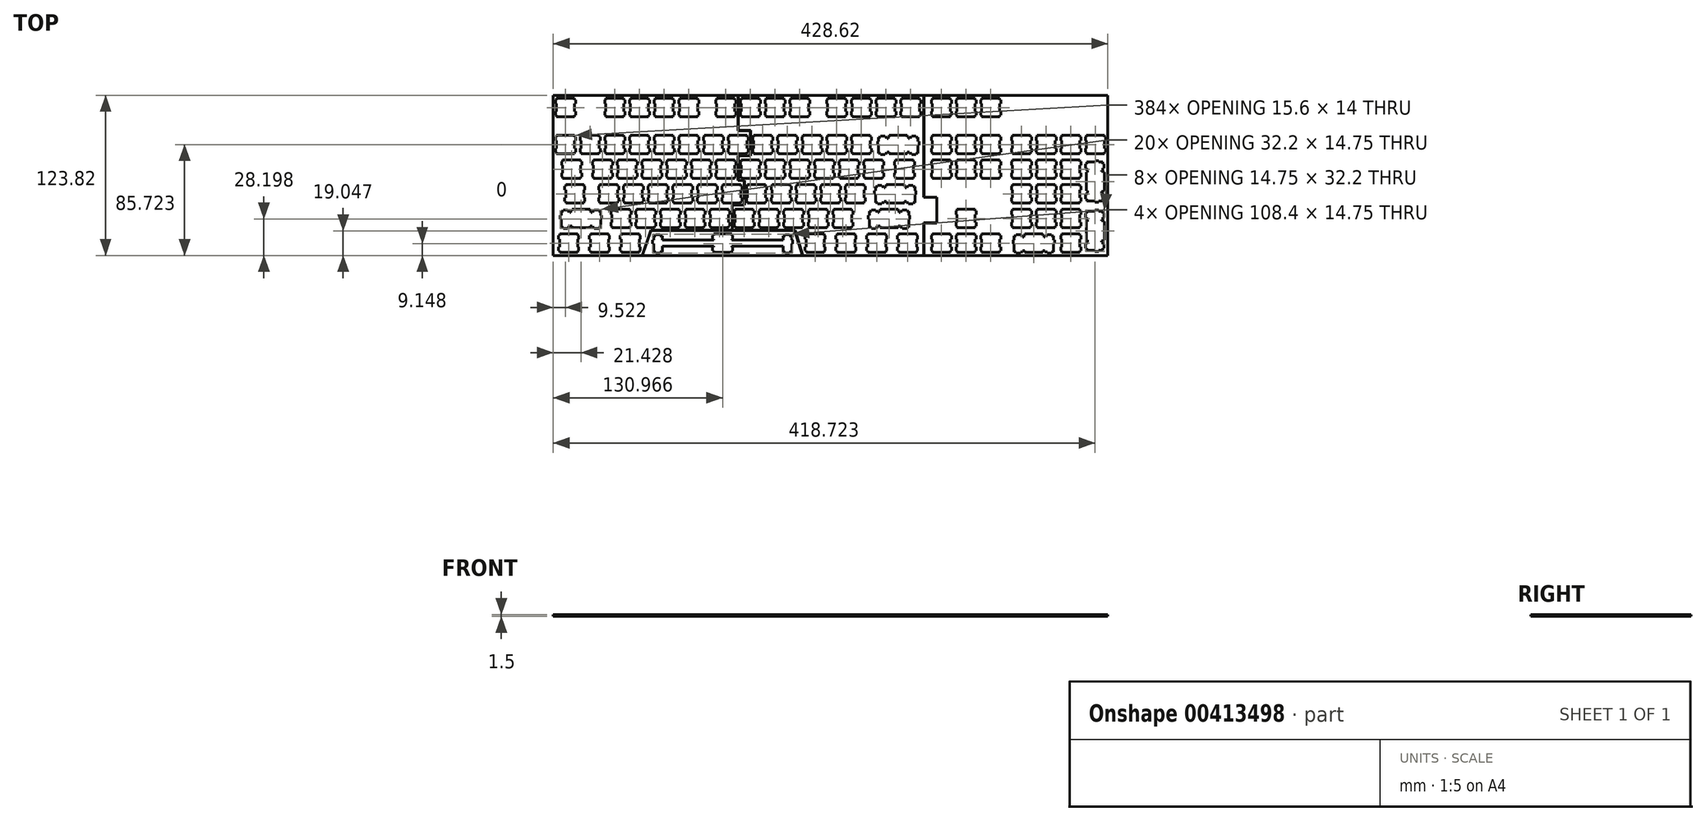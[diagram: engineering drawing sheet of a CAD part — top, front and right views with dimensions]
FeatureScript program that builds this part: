
annotation { "Feature Type Name" : "Feature", "Feature Type Description" : "" }
export const myFeature = defineFeature(function(context is Context, id is Id, definition is map)
    precondition{}
    {
        {
            var Q0;
            Q0=qCreatedBy(makeId("Top.planeOp"),FACE);
            var sketch = newSketch(context, id + "F0", { "sketchPlane" : qUnion([Q0])});
            skLineSegment(sketch, "E0", {"start": v(-214.31, 61.91) * mm, "end": v(214.31, 61.91) * mm});
            skLineSegment(sketch, "E1", {"start": v(214.31, 61.91) * mm, "end": v(214.31, -61.91) * mm});
            skLineSegment(sketch, "E2", {"start": v(214.31, -61.91) * mm, "end": v(-214.31, -61.91) * mm});
            skLineSegment(sketch, "E3", {"start": v(-214.31, -61.91) * mm, "end": v(-214.31, 61.91) * mm});
            skLineSegment(sketch, "E4", {"start": v(-197.79, 46.39) * mm, "end": v(-197.79, 45.39) * mm});
            skLineSegment(sketch, "E5", {"start": v(-197.79, 45.39) * mm, "end": v(-211.79, 45.39) * mm});
            skLineSegment(sketch, "E6", {"start": v(-211.79, 45.39) * mm, "end": v(-211.79, 46.39) * mm});
            skLineSegment(sketch, "E7", {"start": v(-211.79, 46.39) * mm, "end": v(-212.59, 46.39) * mm});
            skLineSegment(sketch, "E8", {"start": v(-212.59, 46.39) * mm, "end": v(-212.59, 49.49) * mm});
            skLineSegment(sketch, "E9", {"start": v(-212.59, 49.49) * mm, "end": v(-211.79, 49.49) * mm});
            skLineSegment(sketch, "E10", {"start": v(-211.79, 49.49) * mm, "end": v(-211.79, 55.29) * mm});
            skLineSegment(sketch, "E11", {"start": v(-211.79, 55.29) * mm, "end": v(-212.59, 55.29) * mm});
            skLineSegment(sketch, "E12", {"start": v(-212.59, 55.29) * mm, "end": v(-212.59, 58.39) * mm});
            skLineSegment(sketch, "E13", {"start": v(-212.59, 58.39) * mm, "end": v(-211.79, 58.39) * mm});
            skLineSegment(sketch, "E14", {"start": v(-211.79, 58.39) * mm, "end": v(-211.79, 59.39) * mm});
            skLineSegment(sketch, "E15", {"start": v(-211.79, 59.39) * mm, "end": v(-197.79, 59.39) * mm});
            skLineSegment(sketch, "E16", {"start": v(-197.79, 59.39) * mm, "end": v(-197.79, 58.39) * mm});
            skLineSegment(sketch, "E17", {"start": v(-197.79, 58.39) * mm, "end": v(-196.99, 58.39) * mm});
            skLineSegment(sketch, "E18", {"start": v(-196.99, 58.39) * mm, "end": v(-196.99, 55.29) * mm});
            skLineSegment(sketch, "E19", {"start": v(-196.99, 55.29) * mm, "end": v(-197.79, 55.29) * mm});
            skLineSegment(sketch, "E20", {"start": v(-197.79, 55.29) * mm, "end": v(-197.79, 49.49) * mm});
            skLineSegment(sketch, "E21", {"start": v(-197.79, 49.49) * mm, "end": v(-196.99, 49.49) * mm});
            skLineSegment(sketch, "E22", {"start": v(-196.99, 49.49) * mm, "end": v(-196.99, 46.39) * mm});
            skLineSegment(sketch, "E23", {"start": v(-196.99, 46.39) * mm, "end": v(-197.79, 46.39) * mm});
            skLineSegment(sketch, "E24", {"start": v(-197.79, 17.81) * mm, "end": v(-197.79, 16.81) * mm});
            skLineSegment(sketch, "E25", {"start": v(-197.79, 16.81) * mm, "end": v(-211.79, 16.81) * mm});
            skLineSegment(sketch, "E26", {"start": v(-211.79, 16.81) * mm, "end": v(-211.79, 17.81) * mm});
            skLineSegment(sketch, "E27", {"start": v(-211.79, 17.81) * mm, "end": v(-212.59, 17.81) * mm});
            skLineSegment(sketch, "E28", {"start": v(-212.59, 17.81) * mm, "end": v(-212.59, 20.91) * mm});
            skLineSegment(sketch, "E29", {"start": v(-212.59, 20.91) * mm, "end": v(-211.79, 20.91) * mm});
            skLineSegment(sketch, "E30", {"start": v(-211.79, 20.91) * mm, "end": v(-211.79, 26.71) * mm});
            skLineSegment(sketch, "E31", {"start": v(-211.79, 26.71) * mm, "end": v(-212.59, 26.71) * mm});
            skLineSegment(sketch, "E32", {"start": v(-212.59, 26.71) * mm, "end": v(-212.59, 29.81) * mm});
            skLineSegment(sketch, "E33", {"start": v(-212.59, 29.81) * mm, "end": v(-211.79, 29.81) * mm});
            skLineSegment(sketch, "E34", {"start": v(-211.79, 29.81) * mm, "end": v(-211.79, 30.81) * mm});
            skLineSegment(sketch, "E35", {"start": v(-211.79, 30.81) * mm, "end": v(-197.79, 30.81) * mm});
            skLineSegment(sketch, "E36", {"start": v(-197.79, 30.81) * mm, "end": v(-197.79, 29.81) * mm});
            skLineSegment(sketch, "E37", {"start": v(-197.79, 29.81) * mm, "end": v(-196.99, 29.81) * mm});
            skLineSegment(sketch, "E38", {"start": v(-196.99, 29.81) * mm, "end": v(-196.99, 26.71) * mm});
            skLineSegment(sketch, "E39", {"start": v(-196.99, 26.71) * mm, "end": v(-197.79, 26.71) * mm});
            skLineSegment(sketch, "E40", {"start": v(-197.79, 26.71) * mm, "end": v(-197.79, 20.91) * mm});
            skLineSegment(sketch, "E41", {"start": v(-197.79, 20.91) * mm, "end": v(-196.99, 20.91) * mm});
            skLineSegment(sketch, "E42", {"start": v(-196.99, 20.91) * mm, "end": v(-196.99, 17.81) * mm});
            skLineSegment(sketch, "E43", {"start": v(-196.99, 17.81) * mm, "end": v(-197.79, 17.81) * mm});
            skLineSegment(sketch, "E44", {"start": v(-195.4, -58.39) * mm, "end": v(-195.4, -59.39) * mm});
            skLineSegment(sketch, "E45", {"start": v(-195.4, -59.39) * mm, "end": v(-209.4, -59.39) * mm});
            skLineSegment(sketch, "E46", {"start": v(-209.4, -59.39) * mm, "end": v(-209.4, -58.39) * mm});
            skLineSegment(sketch, "E47", {"start": v(-209.4, -58.39) * mm, "end": v(-210.2, -58.39) * mm});
            skLineSegment(sketch, "E48", {"start": v(-210.2, -58.39) * mm, "end": v(-210.2, -55.29) * mm});
            skLineSegment(sketch, "E49", {"start": v(-210.2, -55.29) * mm, "end": v(-209.4, -55.29) * mm});
            skLineSegment(sketch, "E50", {"start": v(-209.4, -55.29) * mm, "end": v(-209.4, -49.49) * mm});
            skLineSegment(sketch, "E51", {"start": v(-209.4, -49.49) * mm, "end": v(-210.2, -49.49) * mm});
            skLineSegment(sketch, "E52", {"start": v(-210.2, -49.49) * mm, "end": v(-210.2, -46.39) * mm});
            skLineSegment(sketch, "E53", {"start": v(-210.2, -46.39) * mm, "end": v(-209.4, -46.39) * mm});
            skLineSegment(sketch, "E54", {"start": v(-209.4, -46.39) * mm, "end": v(-209.4, -45.39) * mm});
            skLineSegment(sketch, "E55", {"start": v(-209.4, -45.39) * mm, "end": v(-195.4, -45.39) * mm});
            skLineSegment(sketch, "E56", {"start": v(-195.4, -45.39) * mm, "end": v(-195.4, -46.39) * mm});
            skLineSegment(sketch, "E57", {"start": v(-195.4, -46.39) * mm, "end": v(-194.6, -46.39) * mm});
            skLineSegment(sketch, "E58", {"start": v(-194.6, -46.39) * mm, "end": v(-194.6, -49.49) * mm});
            skLineSegment(sketch, "E59", {"start": v(-194.6, -49.49) * mm, "end": v(-195.4, -49.49) * mm});
            skLineSegment(sketch, "E60", {"start": v(-195.4, -49.49) * mm, "end": v(-195.4, -55.29) * mm});
            skLineSegment(sketch, "E61", {"start": v(-195.4, -55.29) * mm, "end": v(-194.6, -55.29) * mm});
            skLineSegment(sketch, "E62", {"start": v(-194.6, -55.29) * mm, "end": v(-194.6, -58.39) * mm});
            skLineSegment(sketch, "E63", {"start": v(-194.6, -58.39) * mm, "end": v(-195.4, -58.39) * mm});
            skLineSegment(sketch, "E64", {"start": v(-193.03, -1.24) * mm, "end": v(-193.03, -2.24) * mm});
            skLineSegment(sketch, "E65", {"start": v(-193.03, -2.24) * mm, "end": v(-207.02, -2.24) * mm});
            skLineSegment(sketch, "E66", {"start": v(-207.02, -2.24) * mm, "end": v(-207.02, -1.24) * mm});
            skLineSegment(sketch, "E67", {"start": v(-207.02, -1.24) * mm, "end": v(-207.83, -1.24) * mm});
            skLineSegment(sketch, "E68", {"start": v(-207.83, -1.24) * mm, "end": v(-207.83, 1.86) * mm});
            skLineSegment(sketch, "E69", {"start": v(-207.83, 1.86) * mm, "end": v(-207.02, 1.86) * mm});
            skLineSegment(sketch, "E70", {"start": v(-207.02, 1.86) * mm, "end": v(-207.02, 7.66) * mm});
            skLineSegment(sketch, "E71", {"start": v(-207.02, 7.66) * mm, "end": v(-207.83, 7.66) * mm});
            skLineSegment(sketch, "E72", {"start": v(-207.83, 7.66) * mm, "end": v(-207.83, 10.76) * mm});
            skLineSegment(sketch, "E73", {"start": v(-207.83, 10.76) * mm, "end": v(-207.02, 10.76) * mm});
            skLineSegment(sketch, "E74", {"start": v(-207.02, 10.76) * mm, "end": v(-207.02, 11.76) * mm});
            skLineSegment(sketch, "E75", {"start": v(-207.02, 11.76) * mm, "end": v(-193.03, 11.76) * mm});
            skLineSegment(sketch, "E76", {"start": v(-193.03, 11.76) * mm, "end": v(-193.03, 10.76) * mm});
            skLineSegment(sketch, "E77", {"start": v(-193.03, 10.76) * mm, "end": v(-192.22, 10.76) * mm});
            skLineSegment(sketch, "E78", {"start": v(-192.22, 10.76) * mm, "end": v(-192.22, 7.66) * mm});
            skLineSegment(sketch, "E79", {"start": v(-192.22, 7.66) * mm, "end": v(-193.03, 7.66) * mm});
            skLineSegment(sketch, "E80", {"start": v(-193.03, 7.66) * mm, "end": v(-193.03, 1.86) * mm});
            skLineSegment(sketch, "E81", {"start": v(-193.03, 1.86) * mm, "end": v(-192.22, 1.86) * mm});
            skLineSegment(sketch, "E82", {"start": v(-192.22, 1.86) * mm, "end": v(-192.22, -1.24) * mm});
            skLineSegment(sketch, "E83", {"start": v(-192.22, -1.24) * mm, "end": v(-193.03, -1.24) * mm});
            skLineSegment(sketch, "E84", {"start": v(-190.64, -20.29) * mm, "end": v(-190.64, -21.29) * mm});
            skLineSegment(sketch, "E85", {"start": v(-190.64, -21.29) * mm, "end": v(-204.64, -21.29) * mm});
            skLineSegment(sketch, "E86", {"start": v(-204.64, -21.29) * mm, "end": v(-204.64, -20.29) * mm});
            skLineSegment(sketch, "E87", {"start": v(-204.64, -20.29) * mm, "end": v(-205.44, -20.29) * mm});
            skLineSegment(sketch, "E88", {"start": v(-205.44, -20.29) * mm, "end": v(-205.44, -17.19) * mm});
            skLineSegment(sketch, "E89", {"start": v(-205.44, -17.19) * mm, "end": v(-204.64, -17.19) * mm});
            skLineSegment(sketch, "E90", {"start": v(-204.64, -17.19) * mm, "end": v(-204.64, -11.39) * mm});
            skLineSegment(sketch, "E91", {"start": v(-204.64, -11.39) * mm, "end": v(-205.44, -11.39) * mm});
            skLineSegment(sketch, "E92", {"start": v(-205.44, -11.39) * mm, "end": v(-205.44, -8.29) * mm});
            skLineSegment(sketch, "E93", {"start": v(-205.44, -8.29) * mm, "end": v(-204.64, -8.29) * mm});
            skLineSegment(sketch, "E94", {"start": v(-204.64, -8.29) * mm, "end": v(-204.64, -7.29) * mm});
            skLineSegment(sketch, "E95", {"start": v(-204.64, -7.29) * mm, "end": v(-190.64, -7.29) * mm});
            skLineSegment(sketch, "E96", {"start": v(-190.64, -7.29) * mm, "end": v(-190.64, -8.29) * mm});
            skLineSegment(sketch, "E97", {"start": v(-190.64, -8.29) * mm, "end": v(-189.84, -8.29) * mm});
            skLineSegment(sketch, "E98", {"start": v(-189.84, -8.29) * mm, "end": v(-189.84, -11.39) * mm});
            skLineSegment(sketch, "E99", {"start": v(-189.84, -11.39) * mm, "end": v(-190.64, -11.39) * mm});
            skLineSegment(sketch, "E100", {"start": v(-190.64, -11.39) * mm, "end": v(-190.64, -17.19) * mm});
            skLineSegment(sketch, "E101", {"start": v(-190.64, -17.19) * mm, "end": v(-189.84, -17.19) * mm});
            skLineSegment(sketch, "E102", {"start": v(-189.84, -17.19) * mm, "end": v(-189.84, -20.29) * mm});
            skLineSegment(sketch, "E103", {"start": v(-189.84, -20.29) * mm, "end": v(-190.64, -20.29) * mm});
            skLineSegment(sketch, "E104", {"start": v(-178.74, 17.81) * mm, "end": v(-178.74, 16.81) * mm});
            skLineSegment(sketch, "E105", {"start": v(-178.74, 16.81) * mm, "end": v(-192.74, 16.81) * mm});
            skLineSegment(sketch, "E106", {"start": v(-192.74, 16.81) * mm, "end": v(-192.74, 17.81) * mm});
            skLineSegment(sketch, "E107", {"start": v(-192.74, 17.81) * mm, "end": v(-193.54, 17.81) * mm});
            skLineSegment(sketch, "E108", {"start": v(-193.54, 17.81) * mm, "end": v(-193.54, 20.91) * mm});
            skLineSegment(sketch, "E109", {"start": v(-193.54, 20.91) * mm, "end": v(-192.74, 20.91) * mm});
            skLineSegment(sketch, "E110", {"start": v(-192.74, 20.91) * mm, "end": v(-192.74, 26.71) * mm});
            skLineSegment(sketch, "E111", {"start": v(-192.74, 26.71) * mm, "end": v(-193.54, 26.71) * mm});
            skLineSegment(sketch, "E112", {"start": v(-193.54, 26.71) * mm, "end": v(-193.54, 29.81) * mm});
            skLineSegment(sketch, "E113", {"start": v(-193.54, 29.81) * mm, "end": v(-192.74, 29.81) * mm});
            skLineSegment(sketch, "E114", {"start": v(-192.74, 29.81) * mm, "end": v(-192.74, 30.81) * mm});
            skLineSegment(sketch, "E115", {"start": v(-192.74, 30.81) * mm, "end": v(-178.74, 30.81) * mm});
            skLineSegment(sketch, "E116", {"start": v(-178.74, 30.81) * mm, "end": v(-178.74, 29.81) * mm});
            skLineSegment(sketch, "E117", {"start": v(-178.74, 29.81) * mm, "end": v(-177.94, 29.81) * mm});
            skLineSegment(sketch, "E118", {"start": v(-177.94, 29.81) * mm, "end": v(-177.94, 26.71) * mm});
            skLineSegment(sketch, "E119", {"start": v(-177.94, 26.71) * mm, "end": v(-178.74, 26.71) * mm});
            skLineSegment(sketch, "E120", {"start": v(-178.74, 26.71) * mm, "end": v(-178.74, 20.91) * mm});
            skLineSegment(sketch, "E121", {"start": v(-178.74, 20.91) * mm, "end": v(-177.94, 20.91) * mm});
            skLineSegment(sketch, "E122", {"start": v(-177.94, 20.91) * mm, "end": v(-177.94, 17.81) * mm});
            skLineSegment(sketch, "E123", {"start": v(-177.94, 17.81) * mm, "end": v(-178.74, 17.81) * mm});
            skLineSegment(sketch, "E124", {"start": v(-177.66, -33.84) * mm, "end": v(-177.66, -40.1) * mm});
            skLineSegment(sketch, "E125", {"start": v(-177.66, -40.1) * mm, "end": v(-179.28, -40.1) * mm});
            skLineSegment(sketch, "E126", {"start": v(-179.28, -40.1) * mm, "end": v(-179.28, -41.09) * mm});
            skLineSegment(sketch, "E127", {"start": v(-179.28, -41.09) * mm, "end": v(-182.58, -41.09) * mm});
            skLineSegment(sketch, "E128", {"start": v(-182.58, -41.09) * mm, "end": v(-182.58, -40.1) * mm});
            skLineSegment(sketch, "E129", {"start": v(-182.58, -40.1) * mm, "end": v(-184.3, -40.1) * mm});
            skLineSegment(sketch, "E130", {"start": v(-184.3, -40.1) * mm, "end": v(-184.3, -39.3) * mm});
            skLineSegment(sketch, "E131", {"start": v(-184.3, -39.3) * mm, "end": v(-185.08, -39.3) * mm});
            skLineSegment(sketch, "E132", {"start": v(-185.08, -39.3) * mm, "end": v(-185.08, -39.34) * mm});
            skLineSegment(sketch, "E133", {"start": v(-185.08, -39.34) * mm, "end": v(-185.88, -39.34) * mm});
            skLineSegment(sketch, "E134", {"start": v(-185.88, -39.34) * mm, "end": v(-185.88, -40.34) * mm});
            skLineSegment(sketch, "E135", {"start": v(-185.88, -40.34) * mm, "end": v(-199.88, -40.34) * mm});
            skLineSegment(sketch, "E136", {"start": v(-199.88, -40.34) * mm, "end": v(-199.88, -39.34) * mm});
            skLineSegment(sketch, "E137", {"start": v(-199.88, -39.34) * mm, "end": v(-200.68, -39.34) * mm});
            skLineSegment(sketch, "E138", {"start": v(-200.68, -39.34) * mm, "end": v(-200.68, -39.3) * mm});
            skLineSegment(sketch, "E139", {"start": v(-200.68, -39.3) * mm, "end": v(-201.46, -39.3) * mm});
            skLineSegment(sketch, "E140", {"start": v(-201.46, -39.3) * mm, "end": v(-201.46, -40.1) * mm});
            skLineSegment(sketch, "E141", {"start": v(-201.46, -40.1) * mm, "end": v(-203.18, -40.1) * mm});
            skLineSegment(sketch, "E142", {"start": v(-203.18, -40.1) * mm, "end": v(-203.18, -41.09) * mm});
            skLineSegment(sketch, "E143", {"start": v(-203.18, -41.09) * mm, "end": v(-206.48, -41.09) * mm});
            skLineSegment(sketch, "E144", {"start": v(-206.48, -41.09) * mm, "end": v(-206.48, -40.1) * mm});
            skLineSegment(sketch, "E145", {"start": v(-206.48, -40.1) * mm, "end": v(-208.1, -40.1) * mm});
            skLineSegment(sketch, "E146", {"start": v(-208.1, -40.1) * mm, "end": v(-208.1, -33.84) * mm});
            skLineSegment(sketch, "E147", {"start": v(-208.1, -33.84) * mm, "end": v(-208.98, -33.84) * mm});
            skLineSegment(sketch, "E148", {"start": v(-208.98, -33.84) * mm, "end": v(-208.98, -31.04) * mm});
            skLineSegment(sketch, "E149", {"start": v(-208.98, -31.04) * mm, "end": v(-208.1, -31.04) * mm});
            skLineSegment(sketch, "E150", {"start": v(-208.1, -31.04) * mm, "end": v(-208.1, -27.8) * mm});
            skLineSegment(sketch, "E151", {"start": v(-208.1, -27.8) * mm, "end": v(-206.48, -27.8) * mm});
            skLineSegment(sketch, "E152", {"start": v(-206.48, -27.8) * mm, "end": v(-206.48, -26.89) * mm});
            skLineSegment(sketch, "E153", {"start": v(-206.48, -26.89) * mm, "end": v(-203.18, -26.89) * mm});
            skLineSegment(sketch, "E154", {"start": v(-203.18, -26.89) * mm, "end": v(-203.18, -27.8) * mm});
            skLineSegment(sketch, "E155", {"start": v(-203.18, -27.8) * mm, "end": v(-201.46, -27.8) * mm});
            skLineSegment(sketch, "E156", {"start": v(-201.46, -27.8) * mm, "end": v(-201.46, -28.6) * mm});
            skLineSegment(sketch, "E157", {"start": v(-201.46, -28.6) * mm, "end": v(-200.68, -28.6) * mm});
            skLineSegment(sketch, "E158", {"start": v(-200.68, -28.6) * mm, "end": v(-200.68, -27.34) * mm});
            skLineSegment(sketch, "E159", {"start": v(-200.68, -27.34) * mm, "end": v(-199.88, -27.34) * mm});
            skLineSegment(sketch, "E160", {"start": v(-199.88, -27.34) * mm, "end": v(-199.88, -26.34) * mm});
            skLineSegment(sketch, "E161", {"start": v(-199.88, -26.34) * mm, "end": v(-185.88, -26.34) * mm});
            skLineSegment(sketch, "E162", {"start": v(-185.88, -26.34) * mm, "end": v(-185.88, -27.34) * mm});
            skLineSegment(sketch, "E163", {"start": v(-185.88, -27.34) * mm, "end": v(-185.08, -27.34) * mm});
            skLineSegment(sketch, "E164", {"start": v(-185.08, -27.34) * mm, "end": v(-185.08, -28.6) * mm});
            skLineSegment(sketch, "E165", {"start": v(-185.08, -28.6) * mm, "end": v(-184.3, -28.6) * mm});
            skLineSegment(sketch, "E166", {"start": v(-184.3, -28.6) * mm, "end": v(-184.3, -27.8) * mm});
            skLineSegment(sketch, "E167", {"start": v(-184.3, -27.8) * mm, "end": v(-182.58, -27.8) * mm});
            skLineSegment(sketch, "E168", {"start": v(-182.58, -27.8) * mm, "end": v(-182.58, -26.89) * mm});
            skLineSegment(sketch, "E169", {"start": v(-182.58, -26.89) * mm, "end": v(-179.28, -26.89) * mm});
            skLineSegment(sketch, "E170", {"start": v(-179.28, -26.89) * mm, "end": v(-179.28, -27.8) * mm});
            skLineSegment(sketch, "E171", {"start": v(-179.28, -27.8) * mm, "end": v(-177.66, -27.8) * mm});
            skLineSegment(sketch, "E172", {"start": v(-177.66, -27.8) * mm, "end": v(-177.66, -31.04) * mm});
            skLineSegment(sketch, "E173", {"start": v(-177.66, -31.04) * mm, "end": v(-176.78, -31.04) * mm});
            skLineSegment(sketch, "E174", {"start": v(-176.78, -31.04) * mm, "end": v(-176.78, -33.84) * mm});
            skLineSegment(sketch, "E175", {"start": v(-176.78, -33.84) * mm, "end": v(-177.66, -33.84) * mm});
            skLineSegment(sketch, "E176", {"start": v(-171.6, -58.39) * mm, "end": v(-171.6, -59.39) * mm});
            skLineSegment(sketch, "E177", {"start": v(-171.6, -59.39) * mm, "end": v(-185.6, -59.39) * mm});
            skLineSegment(sketch, "E178", {"start": v(-185.6, -59.39) * mm, "end": v(-185.6, -58.39) * mm});
            skLineSegment(sketch, "E179", {"start": v(-185.6, -58.39) * mm, "end": v(-186.4, -58.39) * mm});
            skLineSegment(sketch, "E180", {"start": v(-186.4, -58.39) * mm, "end": v(-186.4, -55.29) * mm});
            skLineSegment(sketch, "E181", {"start": v(-186.4, -55.29) * mm, "end": v(-185.6, -55.29) * mm});
            skLineSegment(sketch, "E182", {"start": v(-185.6, -55.29) * mm, "end": v(-185.6, -49.49) * mm});
            skLineSegment(sketch, "E183", {"start": v(-185.6, -49.49) * mm, "end": v(-186.4, -49.49) * mm});
            skLineSegment(sketch, "E184", {"start": v(-186.4, -49.49) * mm, "end": v(-186.4, -46.39) * mm});
            skLineSegment(sketch, "E185", {"start": v(-186.4, -46.39) * mm, "end": v(-185.6, -46.39) * mm});
            skLineSegment(sketch, "E186", {"start": v(-185.6, -46.39) * mm, "end": v(-185.6, -45.39) * mm});
            skLineSegment(sketch, "E187", {"start": v(-185.6, -45.39) * mm, "end": v(-171.6, -45.39) * mm});
            skLineSegment(sketch, "E188", {"start": v(-171.6, -45.39) * mm, "end": v(-171.6, -46.39) * mm});
            skLineSegment(sketch, "E189", {"start": v(-171.6, -46.39) * mm, "end": v(-170.8, -46.39) * mm});
            skLineSegment(sketch, "E190", {"start": v(-170.8, -46.39) * mm, "end": v(-170.8, -49.49) * mm});
            skLineSegment(sketch, "E191", {"start": v(-170.8, -49.49) * mm, "end": v(-171.6, -49.49) * mm});
            skLineSegment(sketch, "E192", {"start": v(-171.6, -49.49) * mm, "end": v(-171.6, -55.29) * mm});
            skLineSegment(sketch, "E193", {"start": v(-171.6, -55.29) * mm, "end": v(-170.8, -55.29) * mm});
            skLineSegment(sketch, "E194", {"start": v(-170.8, -55.29) * mm, "end": v(-170.8, -58.39) * mm});
            skLineSegment(sketch, "E195", {"start": v(-170.8, -58.39) * mm, "end": v(-171.6, -58.39) * mm});
            skLineSegment(sketch, "E196", {"start": v(-169.21, -1.24) * mm, "end": v(-169.21, -2.24) * mm});
            skLineSegment(sketch, "E197", {"start": v(-169.21, -2.24) * mm, "end": v(-183.21, -2.24) * mm});
            skLineSegment(sketch, "E198", {"start": v(-183.21, -2.24) * mm, "end": v(-183.21, -1.24) * mm});
            skLineSegment(sketch, "E199", {"start": v(-183.21, -1.24) * mm, "end": v(-184.01, -1.24) * mm});
            skLineSegment(sketch, "E200", {"start": v(-184.01, -1.24) * mm, "end": v(-184.01, 1.86) * mm});
            skLineSegment(sketch, "E201", {"start": v(-184.01, 1.86) * mm, "end": v(-183.21, 1.86) * mm});
            skLineSegment(sketch, "E202", {"start": v(-183.21, 1.86) * mm, "end": v(-183.21, 7.66) * mm});
            skLineSegment(sketch, "E203", {"start": v(-183.21, 7.66) * mm, "end": v(-184.01, 7.66) * mm});
            skLineSegment(sketch, "E204", {"start": v(-184.01, 7.66) * mm, "end": v(-184.01, 10.76) * mm});
            skLineSegment(sketch, "E205", {"start": v(-184.01, 10.76) * mm, "end": v(-183.21, 10.76) * mm});
            skLineSegment(sketch, "E206", {"start": v(-183.21, 10.76) * mm, "end": v(-183.21, 11.76) * mm});
            skLineSegment(sketch, "E207", {"start": v(-183.21, 11.76) * mm, "end": v(-169.21, 11.76) * mm});
            skLineSegment(sketch, "E208", {"start": v(-169.21, 11.76) * mm, "end": v(-169.21, 10.76) * mm});
            skLineSegment(sketch, "E209", {"start": v(-169.21, 10.76) * mm, "end": v(-168.41, 10.76) * mm});
            skLineSegment(sketch, "E210", {"start": v(-168.41, 10.76) * mm, "end": v(-168.41, 7.66) * mm});
            skLineSegment(sketch, "E211", {"start": v(-168.41, 7.66) * mm, "end": v(-169.21, 7.66) * mm});
            skLineSegment(sketch, "E212", {"start": v(-169.21, 7.66) * mm, "end": v(-169.21, 1.86) * mm});
            skLineSegment(sketch, "E213", {"start": v(-169.21, 1.86) * mm, "end": v(-168.41, 1.86) * mm});
            skLineSegment(sketch, "E214", {"start": v(-168.41, 1.86) * mm, "end": v(-168.41, -1.24) * mm});
            skLineSegment(sketch, "E215", {"start": v(-168.41, -1.24) * mm, "end": v(-169.21, -1.24) * mm});
            skLineSegment(sketch, "E216", {"start": v(-164.45, -20.29) * mm, "end": v(-164.45, -21.29) * mm});
            skLineSegment(sketch, "E217", {"start": v(-164.45, -21.29) * mm, "end": v(-178.45, -21.29) * mm});
            skLineSegment(sketch, "E218", {"start": v(-178.45, -21.29) * mm, "end": v(-178.45, -20.29) * mm});
            skLineSegment(sketch, "E219", {"start": v(-178.45, -20.29) * mm, "end": v(-179.25, -20.29) * mm});
            skLineSegment(sketch, "E220", {"start": v(-179.25, -20.29) * mm, "end": v(-179.25, -17.19) * mm});
            skLineSegment(sketch, "E221", {"start": v(-179.25, -17.19) * mm, "end": v(-178.45, -17.19) * mm});
            skLineSegment(sketch, "E222", {"start": v(-178.45, -17.19) * mm, "end": v(-178.45, -11.39) * mm});
            skLineSegment(sketch, "E223", {"start": v(-178.45, -11.39) * mm, "end": v(-179.25, -11.39) * mm});
            skLineSegment(sketch, "E224", {"start": v(-179.25, -11.39) * mm, "end": v(-179.25, -8.29) * mm});
            skLineSegment(sketch, "E225", {"start": v(-179.25, -8.29) * mm, "end": v(-178.45, -8.29) * mm});
            skLineSegment(sketch, "E226", {"start": v(-178.45, -8.29) * mm, "end": v(-178.45, -7.29) * mm});
            skLineSegment(sketch, "E227", {"start": v(-178.45, -7.29) * mm, "end": v(-164.45, -7.29) * mm});
            skLineSegment(sketch, "E228", {"start": v(-164.45, -7.29) * mm, "end": v(-164.45, -8.29) * mm});
            skLineSegment(sketch, "E229", {"start": v(-164.45, -8.29) * mm, "end": v(-163.65, -8.29) * mm});
            skLineSegment(sketch, "E230", {"start": v(-163.65, -8.29) * mm, "end": v(-163.65, -11.39) * mm});
            skLineSegment(sketch, "E231", {"start": v(-163.65, -11.39) * mm, "end": v(-164.45, -11.39) * mm});
            skLineSegment(sketch, "E232", {"start": v(-164.45, -11.39) * mm, "end": v(-164.45, -17.19) * mm});
            skLineSegment(sketch, "E233", {"start": v(-164.45, -17.19) * mm, "end": v(-163.65, -17.19) * mm});
            skLineSegment(sketch, "E234", {"start": v(-163.65, -17.19) * mm, "end": v(-163.65, -20.29) * mm});
            skLineSegment(sketch, "E235", {"start": v(-163.65, -20.29) * mm, "end": v(-164.45, -20.29) * mm});
            skLineSegment(sketch, "E236", {"start": v(-159.69, 46.39) * mm, "end": v(-159.69, 45.39) * mm});
            skLineSegment(sketch, "E237", {"start": v(-159.69, 45.39) * mm, "end": v(-173.69, 45.39) * mm});
            skLineSegment(sketch, "E238", {"start": v(-173.69, 45.39) * mm, "end": v(-173.69, 46.39) * mm});
            skLineSegment(sketch, "E239", {"start": v(-173.69, 46.39) * mm, "end": v(-174.49, 46.39) * mm});
            skLineSegment(sketch, "E240", {"start": v(-174.49, 46.39) * mm, "end": v(-174.49, 49.49) * mm});
            skLineSegment(sketch, "E241", {"start": v(-174.49, 49.49) * mm, "end": v(-173.69, 49.49) * mm});
            skLineSegment(sketch, "E242", {"start": v(-173.69, 49.49) * mm, "end": v(-173.69, 55.29) * mm});
            skLineSegment(sketch, "E243", {"start": v(-173.69, 55.29) * mm, "end": v(-174.49, 55.29) * mm});
            skLineSegment(sketch, "E244", {"start": v(-174.49, 55.29) * mm, "end": v(-174.49, 58.39) * mm});
            skLineSegment(sketch, "E245", {"start": v(-174.49, 58.39) * mm, "end": v(-173.69, 58.39) * mm});
            skLineSegment(sketch, "E246", {"start": v(-173.69, 58.39) * mm, "end": v(-173.69, 59.39) * mm});
            skLineSegment(sketch, "E247", {"start": v(-173.69, 59.39) * mm, "end": v(-159.69, 59.39) * mm});
            skLineSegment(sketch, "E248", {"start": v(-159.69, 59.39) * mm, "end": v(-159.69, 58.39) * mm});
            skLineSegment(sketch, "E249", {"start": v(-159.69, 58.39) * mm, "end": v(-158.89, 58.39) * mm});
            skLineSegment(sketch, "E250", {"start": v(-158.89, 58.39) * mm, "end": v(-158.89, 55.29) * mm});
            skLineSegment(sketch, "E251", {"start": v(-158.89, 55.29) * mm, "end": v(-159.69, 55.29) * mm});
            skLineSegment(sketch, "E252", {"start": v(-159.69, 55.29) * mm, "end": v(-159.69, 49.49) * mm});
            skLineSegment(sketch, "E253", {"start": v(-159.69, 49.49) * mm, "end": v(-158.89, 49.49) * mm});
            skLineSegment(sketch, "E254", {"start": v(-158.89, 49.49) * mm, "end": v(-158.89, 46.39) * mm});
            skLineSegment(sketch, "E255", {"start": v(-158.89, 46.39) * mm, "end": v(-159.69, 46.39) * mm});
            skLineSegment(sketch, "E256", {"start": v(-159.69, 17.81) * mm, "end": v(-159.69, 16.81) * mm});
            skLineSegment(sketch, "E257", {"start": v(-159.69, 16.81) * mm, "end": v(-173.69, 16.81) * mm});
            skLineSegment(sketch, "E258", {"start": v(-173.69, 16.81) * mm, "end": v(-173.69, 17.81) * mm});
            skLineSegment(sketch, "E259", {"start": v(-173.69, 17.81) * mm, "end": v(-174.49, 17.81) * mm});
            skLineSegment(sketch, "E260", {"start": v(-174.49, 17.81) * mm, "end": v(-174.49, 20.91) * mm});
            skLineSegment(sketch, "E261", {"start": v(-174.49, 20.91) * mm, "end": v(-173.69, 20.91) * mm});
            skLineSegment(sketch, "E262", {"start": v(-173.69, 20.91) * mm, "end": v(-173.69, 26.71) * mm});
            skLineSegment(sketch, "E263", {"start": v(-173.69, 26.71) * mm, "end": v(-174.49, 26.71) * mm});
            skLineSegment(sketch, "E264", {"start": v(-174.49, 26.71) * mm, "end": v(-174.49, 29.81) * mm});
            skLineSegment(sketch, "E265", {"start": v(-174.49, 29.81) * mm, "end": v(-173.69, 29.81) * mm});
            skLineSegment(sketch, "E266", {"start": v(-173.69, 29.81) * mm, "end": v(-173.69, 30.81) * mm});
            skLineSegment(sketch, "E267", {"start": v(-173.69, 30.81) * mm, "end": v(-159.69, 30.81) * mm});
            skLineSegment(sketch, "E268", {"start": v(-159.69, 30.81) * mm, "end": v(-159.69, 29.81) * mm});
            skLineSegment(sketch, "E269", {"start": v(-159.69, 29.81) * mm, "end": v(-158.89, 29.81) * mm});
            skLineSegment(sketch, "E270", {"start": v(-158.89, 29.81) * mm, "end": v(-158.89, 26.71) * mm});
            skLineSegment(sketch, "E271", {"start": v(-158.89, 26.71) * mm, "end": v(-159.69, 26.71) * mm});
            skLineSegment(sketch, "E272", {"start": v(-159.69, 26.71) * mm, "end": v(-159.69, 20.91) * mm});
            skLineSegment(sketch, "E273", {"start": v(-159.69, 20.91) * mm, "end": v(-158.89, 20.91) * mm});
            skLineSegment(sketch, "E274", {"start": v(-158.89, 20.91) * mm, "end": v(-158.89, 17.81) * mm});
            skLineSegment(sketch, "E275", {"start": v(-158.89, 17.81) * mm, "end": v(-159.69, 17.81) * mm});
            skLineSegment(sketch, "E276", {"start": v(-154.93, -39.34) * mm, "end": v(-154.93, -40.34) * mm});
            skLineSegment(sketch, "E277", {"start": v(-154.93, -40.34) * mm, "end": v(-168.92, -40.34) * mm});
            skLineSegment(sketch, "E278", {"start": v(-168.92, -40.34) * mm, "end": v(-168.92, -39.34) * mm});
            skLineSegment(sketch, "E279", {"start": v(-168.92, -39.34) * mm, "end": v(-169.73, -39.34) * mm});
            skLineSegment(sketch, "E280", {"start": v(-169.73, -39.34) * mm, "end": v(-169.73, -36.24) * mm});
            skLineSegment(sketch, "E281", {"start": v(-169.73, -36.24) * mm, "end": v(-168.92, -36.24) * mm});
            skLineSegment(sketch, "E282", {"start": v(-168.92, -36.24) * mm, "end": v(-168.92, -30.44) * mm});
            skLineSegment(sketch, "E283", {"start": v(-168.92, -30.44) * mm, "end": v(-169.73, -30.44) * mm});
            skLineSegment(sketch, "E284", {"start": v(-169.73, -30.44) * mm, "end": v(-169.73, -27.34) * mm});
            skLineSegment(sketch, "E285", {"start": v(-169.73, -27.34) * mm, "end": v(-168.92, -27.34) * mm});
            skLineSegment(sketch, "E286", {"start": v(-168.92, -27.34) * mm, "end": v(-168.92, -26.34) * mm});
            skLineSegment(sketch, "E287", {"start": v(-168.92, -26.34) * mm, "end": v(-154.93, -26.34) * mm});
            skLineSegment(sketch, "E288", {"start": v(-154.93, -26.34) * mm, "end": v(-154.93, -27.34) * mm});
            skLineSegment(sketch, "E289", {"start": v(-154.93, -27.34) * mm, "end": v(-154.12, -27.34) * mm});
            skLineSegment(sketch, "E290", {"start": v(-154.12, -27.34) * mm, "end": v(-154.12, -30.44) * mm});
            skLineSegment(sketch, "E291", {"start": v(-154.12, -30.44) * mm, "end": v(-154.93, -30.44) * mm});
            skLineSegment(sketch, "E292", {"start": v(-154.93, -30.44) * mm, "end": v(-154.93, -36.24) * mm});
            skLineSegment(sketch, "E293", {"start": v(-154.93, -36.24) * mm, "end": v(-154.12, -36.24) * mm});
            skLineSegment(sketch, "E294", {"start": v(-154.12, -36.24) * mm, "end": v(-154.12, -39.34) * mm});
            skLineSegment(sketch, "E295", {"start": v(-154.12, -39.34) * mm, "end": v(-154.93, -39.34) * mm});
            skLineSegment(sketch, "E296", {"start": v(-150.16, -1.24) * mm, "end": v(-150.16, -2.24) * mm});
            skLineSegment(sketch, "E297", {"start": v(-150.16, -2.24) * mm, "end": v(-164.16, -2.24) * mm});
            skLineSegment(sketch, "E298", {"start": v(-164.16, -2.24) * mm, "end": v(-164.16, -1.24) * mm});
            skLineSegment(sketch, "E299", {"start": v(-164.16, -1.24) * mm, "end": v(-164.96, -1.24) * mm});
            skLineSegment(sketch, "E300", {"start": v(-164.96, -1.24) * mm, "end": v(-164.96, 1.86) * mm});
            skLineSegment(sketch, "E301", {"start": v(-164.96, 1.86) * mm, "end": v(-164.16, 1.86) * mm});
            skLineSegment(sketch, "E302", {"start": v(-164.16, 1.86) * mm, "end": v(-164.16, 7.66) * mm});
            skLineSegment(sketch, "E303", {"start": v(-164.16, 7.66) * mm, "end": v(-164.96, 7.66) * mm});
            skLineSegment(sketch, "E304", {"start": v(-164.96, 7.66) * mm, "end": v(-164.96, 10.76) * mm});
            skLineSegment(sketch, "E305", {"start": v(-164.96, 10.76) * mm, "end": v(-164.16, 10.76) * mm});
            skLineSegment(sketch, "E306", {"start": v(-164.16, 10.76) * mm, "end": v(-164.16, 11.76) * mm});
            skLineSegment(sketch, "E307", {"start": v(-164.16, 11.76) * mm, "end": v(-150.16, 11.76) * mm});
            skLineSegment(sketch, "E308", {"start": v(-150.16, 11.76) * mm, "end": v(-150.16, 10.76) * mm});
            skLineSegment(sketch, "E309", {"start": v(-150.16, 10.76) * mm, "end": v(-149.36, 10.76) * mm});
            skLineSegment(sketch, "E310", {"start": v(-149.36, 10.76) * mm, "end": v(-149.36, 7.66) * mm});
            skLineSegment(sketch, "E311", {"start": v(-149.36, 7.66) * mm, "end": v(-150.16, 7.66) * mm});
            skLineSegment(sketch, "E312", {"start": v(-150.16, 7.66) * mm, "end": v(-150.16, 1.86) * mm});
            skLineSegment(sketch, "E313", {"start": v(-150.16, 1.86) * mm, "end": v(-149.36, 1.86) * mm});
            skLineSegment(sketch, "E314", {"start": v(-149.36, 1.86) * mm, "end": v(-149.36, -1.24) * mm});
            skLineSegment(sketch, "E315", {"start": v(-149.36, -1.24) * mm, "end": v(-150.16, -1.24) * mm});
            skLineSegment(sketch, "E316", {"start": v(-147.78, -58.39) * mm, "end": v(-147.78, -59.39) * mm});
            skLineSegment(sketch, "E317", {"start": v(-147.78, -59.39) * mm, "end": v(-161.78, -59.39) * mm});
            skLineSegment(sketch, "E318", {"start": v(-161.78, -59.39) * mm, "end": v(-161.78, -58.39) * mm});
            skLineSegment(sketch, "E319", {"start": v(-161.78, -58.39) * mm, "end": v(-162.58, -58.39) * mm});
            skLineSegment(sketch, "E320", {"start": v(-162.58, -58.39) * mm, "end": v(-162.58, -55.29) * mm});
            skLineSegment(sketch, "E321", {"start": v(-162.58, -55.29) * mm, "end": v(-161.78, -55.29) * mm});
            skLineSegment(sketch, "E322", {"start": v(-161.78, -55.29) * mm, "end": v(-161.78, -49.49) * mm});
            skLineSegment(sketch, "E323", {"start": v(-161.78, -49.49) * mm, "end": v(-162.58, -49.49) * mm});
            skLineSegment(sketch, "E324", {"start": v(-162.58, -49.49) * mm, "end": v(-162.58, -46.39) * mm});
            skLineSegment(sketch, "E325", {"start": v(-162.58, -46.39) * mm, "end": v(-161.78, -46.39) * mm});
            skLineSegment(sketch, "E326", {"start": v(-161.78, -46.39) * mm, "end": v(-161.78, -45.39) * mm});
            skLineSegment(sketch, "E327", {"start": v(-161.78, -45.39) * mm, "end": v(-147.78, -45.39) * mm});
            skLineSegment(sketch, "E328", {"start": v(-147.78, -45.39) * mm, "end": v(-147.78, -46.39) * mm});
            skLineSegment(sketch, "E329", {"start": v(-147.78, -46.39) * mm, "end": v(-146.98, -46.39) * mm});
            skLineSegment(sketch, "E330", {"start": v(-146.98, -46.39) * mm, "end": v(-146.98, -49.49) * mm});
            skLineSegment(sketch, "E331", {"start": v(-146.98, -49.49) * mm, "end": v(-147.78, -49.49) * mm});
            skLineSegment(sketch, "E332", {"start": v(-147.78, -49.49) * mm, "end": v(-147.78, -55.29) * mm});
            skLineSegment(sketch, "E333", {"start": v(-147.78, -55.29) * mm, "end": v(-146.98, -55.29) * mm});
            skLineSegment(sketch, "E334", {"start": v(-146.98, -55.29) * mm, "end": v(-146.98, -58.39) * mm});
            skLineSegment(sketch, "E335", {"start": v(-146.98, -58.39) * mm, "end": v(-147.78, -58.39) * mm});
            skLineSegment(sketch, "E336", {"start": v(-145.4, -20.29) * mm, "end": v(-145.4, -21.29) * mm});
            skLineSegment(sketch, "E337", {"start": v(-145.4, -21.29) * mm, "end": v(-159.4, -21.29) * mm});
            skLineSegment(sketch, "E338", {"start": v(-159.4, -21.29) * mm, "end": v(-159.4, -20.29) * mm});
            skLineSegment(sketch, "E339", {"start": v(-159.4, -20.29) * mm, "end": v(-160.2, -20.29) * mm});
            skLineSegment(sketch, "E340", {"start": v(-160.2, -20.29) * mm, "end": v(-160.2, -17.19) * mm});
            skLineSegment(sketch, "E341", {"start": v(-160.2, -17.19) * mm, "end": v(-159.4, -17.19) * mm});
            skLineSegment(sketch, "E342", {"start": v(-159.4, -17.19) * mm, "end": v(-159.4, -11.39) * mm});
            skLineSegment(sketch, "E343", {"start": v(-159.4, -11.39) * mm, "end": v(-160.2, -11.39) * mm});
            skLineSegment(sketch, "E344", {"start": v(-160.2, -11.39) * mm, "end": v(-160.2, -8.29) * mm});
            skLineSegment(sketch, "E345", {"start": v(-160.2, -8.29) * mm, "end": v(-159.4, -8.29) * mm});
            skLineSegment(sketch, "E346", {"start": v(-159.4, -8.29) * mm, "end": v(-159.4, -7.29) * mm});
            skLineSegment(sketch, "E347", {"start": v(-159.4, -7.29) * mm, "end": v(-145.4, -7.29) * mm});
            skLineSegment(sketch, "E348", {"start": v(-145.4, -7.29) * mm, "end": v(-145.4, -8.29) * mm});
            skLineSegment(sketch, "E349", {"start": v(-145.4, -8.29) * mm, "end": v(-144.6, -8.29) * mm});
            skLineSegment(sketch, "E350", {"start": v(-144.6, -8.29) * mm, "end": v(-144.6, -11.39) * mm});
            skLineSegment(sketch, "E351", {"start": v(-144.6, -11.39) * mm, "end": v(-145.4, -11.39) * mm});
            skLineSegment(sketch, "E352", {"start": v(-145.4, -11.39) * mm, "end": v(-145.4, -17.19) * mm});
            skLineSegment(sketch, "E353", {"start": v(-145.4, -17.19) * mm, "end": v(-144.6, -17.19) * mm});
            skLineSegment(sketch, "E354", {"start": v(-144.6, -17.19) * mm, "end": v(-144.6, -20.29) * mm});
            skLineSegment(sketch, "E355", {"start": v(-144.6, -20.29) * mm, "end": v(-145.4, -20.29) * mm});
            skLineSegment(sketch, "E356", {"start": v(-140.64, 46.39) * mm, "end": v(-140.64, 45.39) * mm});
            skLineSegment(sketch, "E357", {"start": v(-140.64, 45.39) * mm, "end": v(-154.64, 45.39) * mm});
            skLineSegment(sketch, "E358", {"start": v(-154.64, 45.39) * mm, "end": v(-154.64, 46.39) * mm});
            skLineSegment(sketch, "E359", {"start": v(-154.64, 46.39) * mm, "end": v(-155.44, 46.39) * mm});
            skLineSegment(sketch, "E360", {"start": v(-155.44, 46.39) * mm, "end": v(-155.44, 49.49) * mm});
            skLineSegment(sketch, "E361", {"start": v(-155.44, 49.49) * mm, "end": v(-154.64, 49.49) * mm});
            skLineSegment(sketch, "E362", {"start": v(-154.64, 49.49) * mm, "end": v(-154.64, 55.29) * mm});
            skLineSegment(sketch, "E363", {"start": v(-154.64, 55.29) * mm, "end": v(-155.44, 55.29) * mm});
            skLineSegment(sketch, "E364", {"start": v(-155.44, 55.29) * mm, "end": v(-155.44, 58.39) * mm});
            skLineSegment(sketch, "E365", {"start": v(-155.44, 58.39) * mm, "end": v(-154.64, 58.39) * mm});
            skLineSegment(sketch, "E366", {"start": v(-154.64, 58.39) * mm, "end": v(-154.64, 59.39) * mm});
            skLineSegment(sketch, "E367", {"start": v(-154.64, 59.39) * mm, "end": v(-140.64, 59.39) * mm});
            skLineSegment(sketch, "E368", {"start": v(-140.64, 59.39) * mm, "end": v(-140.64, 58.39) * mm});
            skLineSegment(sketch, "E369", {"start": v(-140.64, 58.39) * mm, "end": v(-139.84, 58.39) * mm});
            skLineSegment(sketch, "E370", {"start": v(-139.84, 58.39) * mm, "end": v(-139.84, 55.29) * mm});
            skLineSegment(sketch, "E371", {"start": v(-139.84, 55.29) * mm, "end": v(-140.64, 55.29) * mm});
            skLineSegment(sketch, "E372", {"start": v(-140.64, 55.29) * mm, "end": v(-140.64, 49.49) * mm});
            skLineSegment(sketch, "E373", {"start": v(-140.64, 49.49) * mm, "end": v(-139.84, 49.49) * mm});
            skLineSegment(sketch, "E374", {"start": v(-139.84, 49.49) * mm, "end": v(-139.84, 46.39) * mm});
            skLineSegment(sketch, "E375", {"start": v(-139.84, 46.39) * mm, "end": v(-140.64, 46.39) * mm});
            skLineSegment(sketch, "E376", {"start": v(-140.64, 17.81) * mm, "end": v(-140.64, 16.81) * mm});
            skLineSegment(sketch, "E377", {"start": v(-140.64, 16.81) * mm, "end": v(-154.64, 16.81) * mm});
            skLineSegment(sketch, "E378", {"start": v(-154.64, 16.81) * mm, "end": v(-154.64, 17.81) * mm});
            skLineSegment(sketch, "E379", {"start": v(-154.64, 17.81) * mm, "end": v(-155.44, 17.81) * mm});
            skLineSegment(sketch, "E380", {"start": v(-155.44, 17.81) * mm, "end": v(-155.44, 20.91) * mm});
            skLineSegment(sketch, "E381", {"start": v(-155.44, 20.91) * mm, "end": v(-154.64, 20.91) * mm});
            skLineSegment(sketch, "E382", {"start": v(-154.64, 20.91) * mm, "end": v(-154.64, 26.71) * mm});
            skLineSegment(sketch, "E383", {"start": v(-154.64, 26.71) * mm, "end": v(-155.44, 26.71) * mm});
            skLineSegment(sketch, "E384", {"start": v(-155.44, 26.71) * mm, "end": v(-155.44, 29.81) * mm});
            skLineSegment(sketch, "E385", {"start": v(-155.44, 29.81) * mm, "end": v(-154.64, 29.81) * mm});
            skLineSegment(sketch, "E386", {"start": v(-154.64, 29.81) * mm, "end": v(-154.64, 30.81) * mm});
            skLineSegment(sketch, "E387", {"start": v(-154.64, 30.81) * mm, "end": v(-140.64, 30.81) * mm});
            skLineSegment(sketch, "E388", {"start": v(-140.64, 30.81) * mm, "end": v(-140.64, 29.81) * mm});
            skLineSegment(sketch, "E389", {"start": v(-140.64, 29.81) * mm, "end": v(-139.84, 29.81) * mm});
            skLineSegment(sketch, "E390", {"start": v(-139.84, 29.81) * mm, "end": v(-139.84, 26.71) * mm});
            skLineSegment(sketch, "E391", {"start": v(-139.84, 26.71) * mm, "end": v(-140.64, 26.71) * mm});
            skLineSegment(sketch, "E392", {"start": v(-140.64, 26.71) * mm, "end": v(-140.64, 20.91) * mm});
            skLineSegment(sketch, "E393", {"start": v(-140.64, 20.91) * mm, "end": v(-139.84, 20.91) * mm});
            skLineSegment(sketch, "E394", {"start": v(-139.84, 20.91) * mm, "end": v(-139.84, 17.81) * mm});
            skLineSegment(sketch, "E395", {"start": v(-139.84, 17.81) * mm, "end": v(-140.64, 17.81) * mm});
            skLineSegment(sketch, "E396", {"start": v(-135.88, -39.34) * mm, "end": v(-135.88, -40.34) * mm});
            skLineSegment(sketch, "E397", {"start": v(-135.88, -40.34) * mm, "end": v(-149.87, -40.34) * mm});
            skLineSegment(sketch, "E398", {"start": v(-149.87, -40.34) * mm, "end": v(-149.87, -39.34) * mm});
            skLineSegment(sketch, "E399", {"start": v(-149.87, -39.34) * mm, "end": v(-150.68, -39.34) * mm});
            skLineSegment(sketch, "E400", {"start": v(-150.68, -39.34) * mm, "end": v(-150.68, -36.24) * mm});
            skLineSegment(sketch, "E401", {"start": v(-150.68, -36.24) * mm, "end": v(-149.87, -36.24) * mm});
            skLineSegment(sketch, "E402", {"start": v(-149.87, -36.24) * mm, "end": v(-149.87, -30.44) * mm});
            skLineSegment(sketch, "E403", {"start": v(-149.87, -30.44) * mm, "end": v(-150.68, -30.44) * mm});
            skLineSegment(sketch, "E404", {"start": v(-150.68, -30.44) * mm, "end": v(-150.68, -27.34) * mm});
            skLineSegment(sketch, "E405", {"start": v(-150.68, -27.34) * mm, "end": v(-149.87, -27.34) * mm});
            skLineSegment(sketch, "E406", {"start": v(-149.87, -27.34) * mm, "end": v(-149.87, -26.34) * mm});
            skLineSegment(sketch, "E407", {"start": v(-149.87, -26.34) * mm, "end": v(-135.88, -26.34) * mm});
            skLineSegment(sketch, "E408", {"start": v(-135.88, -26.34) * mm, "end": v(-135.88, -27.34) * mm});
            skLineSegment(sketch, "E409", {"start": v(-135.88, -27.34) * mm, "end": v(-135.08, -27.34) * mm});
            skLineSegment(sketch, "E410", {"start": v(-135.08, -27.34) * mm, "end": v(-135.08, -30.44) * mm});
            skLineSegment(sketch, "E411", {"start": v(-135.08, -30.44) * mm, "end": v(-135.88, -30.44) * mm});
            skLineSegment(sketch, "E412", {"start": v(-135.88, -30.44) * mm, "end": v(-135.88, -36.24) * mm});
            skLineSegment(sketch, "E413", {"start": v(-135.88, -36.24) * mm, "end": v(-135.08, -36.24) * mm});
            skLineSegment(sketch, "E414", {"start": v(-135.08, -36.24) * mm, "end": v(-135.08, -39.34) * mm});
            skLineSegment(sketch, "E415", {"start": v(-135.08, -39.34) * mm, "end": v(-135.88, -39.34) * mm});
            skLineSegment(sketch, "E416", {"start": v(-131.11, -1.24) * mm, "end": v(-131.11, -2.24) * mm});
            skLineSegment(sketch, "E417", {"start": v(-131.11, -2.24) * mm, "end": v(-145.11, -2.24) * mm});
            skLineSegment(sketch, "E418", {"start": v(-145.11, -2.24) * mm, "end": v(-145.11, -1.24) * mm});
            skLineSegment(sketch, "E419", {"start": v(-145.11, -1.24) * mm, "end": v(-145.91, -1.24) * mm});
            skLineSegment(sketch, "E420", {"start": v(-145.91, -1.24) * mm, "end": v(-145.91, 1.86) * mm});
            skLineSegment(sketch, "E421", {"start": v(-145.91, 1.86) * mm, "end": v(-145.11, 1.86) * mm});
            skLineSegment(sketch, "E422", {"start": v(-145.11, 1.86) * mm, "end": v(-145.11, 7.66) * mm});
            skLineSegment(sketch, "E423", {"start": v(-145.11, 7.66) * mm, "end": v(-145.91, 7.66) * mm});
            skLineSegment(sketch, "E424", {"start": v(-145.91, 7.66) * mm, "end": v(-145.91, 10.76) * mm});
            skLineSegment(sketch, "E425", {"start": v(-145.91, 10.76) * mm, "end": v(-145.11, 10.76) * mm});
            skLineSegment(sketch, "E426", {"start": v(-145.11, 10.76) * mm, "end": v(-145.11, 11.76) * mm});
            skLineSegment(sketch, "E427", {"start": v(-145.11, 11.76) * mm, "end": v(-131.11, 11.76) * mm});
            skLineSegment(sketch, "E428", {"start": v(-131.11, 11.76) * mm, "end": v(-131.11, 10.76) * mm});
            skLineSegment(sketch, "E429", {"start": v(-131.11, 10.76) * mm, "end": v(-130.31, 10.76) * mm});
            skLineSegment(sketch, "E430", {"start": v(-130.31, 10.76) * mm, "end": v(-130.31, 7.66) * mm});
            skLineSegment(sketch, "E431", {"start": v(-130.31, 7.66) * mm, "end": v(-131.11, 7.66) * mm});
            skLineSegment(sketch, "E432", {"start": v(-131.11, 7.66) * mm, "end": v(-131.11, 1.86) * mm});
            skLineSegment(sketch, "E433", {"start": v(-131.11, 1.86) * mm, "end": v(-130.31, 1.86) * mm});
            skLineSegment(sketch, "E434", {"start": v(-130.31, 1.86) * mm, "end": v(-130.31, -1.24) * mm});
            skLineSegment(sketch, "E435", {"start": v(-130.31, -1.24) * mm, "end": v(-131.11, -1.24) * mm});
            skLineSegment(sketch, "E436", {"start": v(-126.35, -20.29) * mm, "end": v(-126.35, -21.29) * mm});
            skLineSegment(sketch, "E437", {"start": v(-126.35, -21.29) * mm, "end": v(-140.35, -21.29) * mm});
            skLineSegment(sketch, "E438", {"start": v(-140.35, -21.29) * mm, "end": v(-140.35, -20.29) * mm});
            skLineSegment(sketch, "E439", {"start": v(-140.35, -20.29) * mm, "end": v(-141.15, -20.29) * mm});
            skLineSegment(sketch, "E440", {"start": v(-141.15, -20.29) * mm, "end": v(-141.15, -17.19) * mm});
            skLineSegment(sketch, "E441", {"start": v(-141.15, -17.19) * mm, "end": v(-140.35, -17.19) * mm});
            skLineSegment(sketch, "E442", {"start": v(-140.35, -17.19) * mm, "end": v(-140.35, -11.39) * mm});
            skLineSegment(sketch, "E443", {"start": v(-140.35, -11.39) * mm, "end": v(-141.15, -11.39) * mm});
            skLineSegment(sketch, "E444", {"start": v(-141.15, -11.39) * mm, "end": v(-141.15, -8.29) * mm});
            skLineSegment(sketch, "E445", {"start": v(-141.15, -8.29) * mm, "end": v(-140.35, -8.29) * mm});
            skLineSegment(sketch, "E446", {"start": v(-140.35, -8.29) * mm, "end": v(-140.35, -7.29) * mm});
            skLineSegment(sketch, "E447", {"start": v(-140.35, -7.29) * mm, "end": v(-126.35, -7.29) * mm});
            skLineSegment(sketch, "E448", {"start": v(-126.35, -7.29) * mm, "end": v(-126.35, -8.29) * mm});
            skLineSegment(sketch, "E449", {"start": v(-126.35, -8.29) * mm, "end": v(-125.55, -8.29) * mm});
            skLineSegment(sketch, "E450", {"start": v(-125.55, -8.29) * mm, "end": v(-125.55, -11.39) * mm});
            skLineSegment(sketch, "E451", {"start": v(-125.55, -11.39) * mm, "end": v(-126.35, -11.39) * mm});
            skLineSegment(sketch, "E452", {"start": v(-126.35, -11.39) * mm, "end": v(-126.35, -17.19) * mm});
            skLineSegment(sketch, "E453", {"start": v(-126.35, -17.19) * mm, "end": v(-125.55, -17.19) * mm});
            skLineSegment(sketch, "E454", {"start": v(-125.55, -17.19) * mm, "end": v(-125.55, -20.29) * mm});
            skLineSegment(sketch, "E455", {"start": v(-125.55, -20.29) * mm, "end": v(-126.35, -20.29) * mm});
            skLineSegment(sketch, "E456", {"start": v(-121.59, 46.39) * mm, "end": v(-121.59, 45.39) * mm});
            skLineSegment(sketch, "E457", {"start": v(-121.59, 45.39) * mm, "end": v(-135.59, 45.39) * mm});
            skLineSegment(sketch, "E458", {"start": v(-135.59, 45.39) * mm, "end": v(-135.59, 46.39) * mm});
            skLineSegment(sketch, "E459", {"start": v(-135.59, 46.39) * mm, "end": v(-136.39, 46.39) * mm});
            skLineSegment(sketch, "E460", {"start": v(-136.39, 46.39) * mm, "end": v(-136.39, 49.49) * mm});
            skLineSegment(sketch, "E461", {"start": v(-136.39, 49.49) * mm, "end": v(-135.59, 49.49) * mm});
            skLineSegment(sketch, "E462", {"start": v(-135.59, 49.49) * mm, "end": v(-135.59, 55.29) * mm});
            skLineSegment(sketch, "E463", {"start": v(-135.59, 55.29) * mm, "end": v(-136.39, 55.29) * mm});
            skLineSegment(sketch, "E464", {"start": v(-136.39, 55.29) * mm, "end": v(-136.39, 58.39) * mm});
            skLineSegment(sketch, "E465", {"start": v(-136.39, 58.39) * mm, "end": v(-135.59, 58.39) * mm});
            skLineSegment(sketch, "E466", {"start": v(-135.59, 58.39) * mm, "end": v(-135.59, 59.39) * mm});
            skLineSegment(sketch, "E467", {"start": v(-135.59, 59.39) * mm, "end": v(-121.59, 59.39) * mm});
            skLineSegment(sketch, "E468", {"start": v(-121.59, 59.39) * mm, "end": v(-121.59, 58.39) * mm});
            skLineSegment(sketch, "E469", {"start": v(-121.59, 58.39) * mm, "end": v(-120.79, 58.39) * mm});
            skLineSegment(sketch, "E470", {"start": v(-120.79, 58.39) * mm, "end": v(-120.79, 55.29) * mm});
            skLineSegment(sketch, "E471", {"start": v(-120.79, 55.29) * mm, "end": v(-121.59, 55.29) * mm});
            skLineSegment(sketch, "E472", {"start": v(-121.59, 55.29) * mm, "end": v(-121.59, 49.49) * mm});
            skLineSegment(sketch, "E473", {"start": v(-121.59, 49.49) * mm, "end": v(-120.79, 49.49) * mm});
            skLineSegment(sketch, "E474", {"start": v(-120.79, 49.49) * mm, "end": v(-120.79, 46.39) * mm});
            skLineSegment(sketch, "E475", {"start": v(-120.79, 46.39) * mm, "end": v(-121.59, 46.39) * mm});
            skLineSegment(sketch, "E476", {"start": v(-121.59, 17.81) * mm, "end": v(-121.59, 16.81) * mm});
            skLineSegment(sketch, "E477", {"start": v(-121.59, 16.81) * mm, "end": v(-135.59, 16.81) * mm});
            skLineSegment(sketch, "E478", {"start": v(-135.59, 16.81) * mm, "end": v(-135.59, 17.81) * mm});
            skLineSegment(sketch, "E479", {"start": v(-135.59, 17.81) * mm, "end": v(-136.39, 17.81) * mm});
            skLineSegment(sketch, "E480", {"start": v(-136.39, 17.81) * mm, "end": v(-136.39, 20.91) * mm});
            skLineSegment(sketch, "E481", {"start": v(-136.39, 20.91) * mm, "end": v(-135.59, 20.91) * mm});
            skLineSegment(sketch, "E482", {"start": v(-135.59, 20.91) * mm, "end": v(-135.59, 26.71) * mm});
            skLineSegment(sketch, "E483", {"start": v(-135.59, 26.71) * mm, "end": v(-136.39, 26.71) * mm});
            skLineSegment(sketch, "E484", {"start": v(-136.39, 26.71) * mm, "end": v(-136.39, 29.81) * mm});
            skLineSegment(sketch, "E485", {"start": v(-136.39, 29.81) * mm, "end": v(-135.59, 29.81) * mm});
            skLineSegment(sketch, "E486", {"start": v(-135.59, 29.81) * mm, "end": v(-135.59, 30.81) * mm});
            skLineSegment(sketch, "E487", {"start": v(-135.59, 30.81) * mm, "end": v(-121.59, 30.81) * mm});
            skLineSegment(sketch, "E488", {"start": v(-121.59, 30.81) * mm, "end": v(-121.59, 29.81) * mm});
            skLineSegment(sketch, "E489", {"start": v(-121.59, 29.81) * mm, "end": v(-120.79, 29.81) * mm});
            skLineSegment(sketch, "E490", {"start": v(-120.79, 29.81) * mm, "end": v(-120.79, 26.71) * mm});
            skLineSegment(sketch, "E491", {"start": v(-120.79, 26.71) * mm, "end": v(-121.59, 26.71) * mm});
            skLineSegment(sketch, "E492", {"start": v(-121.59, 26.71) * mm, "end": v(-121.59, 20.91) * mm});
            skLineSegment(sketch, "E493", {"start": v(-121.59, 20.91) * mm, "end": v(-120.79, 20.91) * mm});
            skLineSegment(sketch, "E494", {"start": v(-120.79, 20.91) * mm, "end": v(-120.79, 17.81) * mm});
            skLineSegment(sketch, "E495", {"start": v(-120.79, 17.81) * mm, "end": v(-121.59, 17.81) * mm});
            skLineSegment(sketch, "E496", {"start": v(-116.83, -39.34) * mm, "end": v(-116.83, -40.34) * mm});
            skLineSegment(sketch, "E497", {"start": v(-116.83, -40.34) * mm, "end": v(-130.83, -40.34) * mm});
            skLineSegment(sketch, "E498", {"start": v(-130.83, -40.34) * mm, "end": v(-130.83, -39.34) * mm});
            skLineSegment(sketch, "E499", {"start": v(-130.83, -39.34) * mm, "end": v(-131.63, -39.34) * mm});
            skLineSegment(sketch, "E500", {"start": v(-131.63, -39.34) * mm, "end": v(-131.63, -36.24) * mm});
            skLineSegment(sketch, "E501", {"start": v(-131.63, -36.24) * mm, "end": v(-130.83, -36.24) * mm});
            skLineSegment(sketch, "E502", {"start": v(-130.83, -36.24) * mm, "end": v(-130.83, -30.44) * mm});
            skLineSegment(sketch, "E503", {"start": v(-130.83, -30.44) * mm, "end": v(-131.63, -30.44) * mm});
            skLineSegment(sketch, "E504", {"start": v(-131.63, -30.44) * mm, "end": v(-131.63, -27.34) * mm});
            skLineSegment(sketch, "E505", {"start": v(-131.63, -27.34) * mm, "end": v(-130.83, -27.34) * mm});
            skLineSegment(sketch, "E506", {"start": v(-130.83, -27.34) * mm, "end": v(-130.83, -26.34) * mm});
            skLineSegment(sketch, "E507", {"start": v(-130.83, -26.34) * mm, "end": v(-116.83, -26.34) * mm});
            skLineSegment(sketch, "E508", {"start": v(-116.83, -26.34) * mm, "end": v(-116.83, -27.34) * mm});
            skLineSegment(sketch, "E509", {"start": v(-116.83, -27.34) * mm, "end": v(-116.03, -27.34) * mm});
            skLineSegment(sketch, "E510", {"start": v(-116.03, -27.34) * mm, "end": v(-116.03, -30.44) * mm});
            skLineSegment(sketch, "E511", {"start": v(-116.03, -30.44) * mm, "end": v(-116.83, -30.44) * mm});
            skLineSegment(sketch, "E512", {"start": v(-116.83, -30.44) * mm, "end": v(-116.83, -36.24) * mm});
            skLineSegment(sketch, "E513", {"start": v(-116.83, -36.24) * mm, "end": v(-116.03, -36.24) * mm});
            skLineSegment(sketch, "E514", {"start": v(-116.03, -36.24) * mm, "end": v(-116.03, -39.34) * mm});
            skLineSegment(sketch, "E515", {"start": v(-116.03, -39.34) * mm, "end": v(-116.83, -39.34) * mm});
            skLineSegment(sketch, "E516", {"start": v(-112.06, -1.24) * mm, "end": v(-112.06, -2.24) * mm});
            skLineSegment(sketch, "E517", {"start": v(-112.06, -2.24) * mm, "end": v(-126.06, -2.24) * mm});
            skLineSegment(sketch, "E518", {"start": v(-126.06, -2.24) * mm, "end": v(-126.06, -1.24) * mm});
            skLineSegment(sketch, "E519", {"start": v(-126.06, -1.24) * mm, "end": v(-126.86, -1.24) * mm});
            skLineSegment(sketch, "E520", {"start": v(-126.86, -1.24) * mm, "end": v(-126.86, 1.86) * mm});
            skLineSegment(sketch, "E521", {"start": v(-126.86, 1.86) * mm, "end": v(-126.06, 1.86) * mm});
            skLineSegment(sketch, "E522", {"start": v(-126.06, 1.86) * mm, "end": v(-126.06, 7.66) * mm});
            skLineSegment(sketch, "E523", {"start": v(-126.06, 7.66) * mm, "end": v(-126.86, 7.66) * mm});
            skLineSegment(sketch, "E524", {"start": v(-126.86, 7.66) * mm, "end": v(-126.86, 10.76) * mm});
            skLineSegment(sketch, "E525", {"start": v(-126.86, 10.76) * mm, "end": v(-126.06, 10.76) * mm});
            skLineSegment(sketch, "E526", {"start": v(-126.06, 10.76) * mm, "end": v(-126.06, 11.76) * mm});
            skLineSegment(sketch, "E527", {"start": v(-126.06, 11.76) * mm, "end": v(-112.06, 11.76) * mm});
            skLineSegment(sketch, "E528", {"start": v(-112.06, 11.76) * mm, "end": v(-112.06, 10.76) * mm});
            skLineSegment(sketch, "E529", {"start": v(-112.06, 10.76) * mm, "end": v(-111.26, 10.76) * mm});
            skLineSegment(sketch, "E530", {"start": v(-111.26, 10.76) * mm, "end": v(-111.26, 7.66) * mm});
            skLineSegment(sketch, "E531", {"start": v(-111.26, 7.66) * mm, "end": v(-112.06, 7.66) * mm});
            skLineSegment(sketch, "E532", {"start": v(-112.06, 7.66) * mm, "end": v(-112.06, 1.86) * mm});
            skLineSegment(sketch, "E533", {"start": v(-112.06, 1.86) * mm, "end": v(-111.26, 1.86) * mm});
            skLineSegment(sketch, "E534", {"start": v(-111.26, 1.86) * mm, "end": v(-111.26, -1.24) * mm});
            skLineSegment(sketch, "E535", {"start": v(-111.26, -1.24) * mm, "end": v(-112.06, -1.24) * mm});
            skLineSegment(sketch, "E536", {"start": v(-107.3, -20.29) * mm, "end": v(-107.3, -21.29) * mm});
            skLineSegment(sketch, "E537", {"start": v(-107.3, -21.29) * mm, "end": v(-121.3, -21.29) * mm});
            skLineSegment(sketch, "E538", {"start": v(-121.3, -21.29) * mm, "end": v(-121.3, -20.29) * mm});
            skLineSegment(sketch, "E539", {"start": v(-121.3, -20.29) * mm, "end": v(-122.1, -20.29) * mm});
            skLineSegment(sketch, "E540", {"start": v(-122.1, -20.29) * mm, "end": v(-122.1, -17.19) * mm});
            skLineSegment(sketch, "E541", {"start": v(-122.1, -17.19) * mm, "end": v(-121.3, -17.19) * mm});
            skLineSegment(sketch, "E542", {"start": v(-121.3, -17.19) * mm, "end": v(-121.3, -11.39) * mm});
            skLineSegment(sketch, "E543", {"start": v(-121.3, -11.39) * mm, "end": v(-122.1, -11.39) * mm});
            skLineSegment(sketch, "E544", {"start": v(-122.1, -11.39) * mm, "end": v(-122.1, -8.29) * mm});
            skLineSegment(sketch, "E545", {"start": v(-122.1, -8.29) * mm, "end": v(-121.3, -8.29) * mm});
            skLineSegment(sketch, "E546", {"start": v(-121.3, -8.29) * mm, "end": v(-121.3, -7.29) * mm});
            skLineSegment(sketch, "E547", {"start": v(-121.3, -7.29) * mm, "end": v(-107.3, -7.29) * mm});
            skLineSegment(sketch, "E548", {"start": v(-107.3, -7.29) * mm, "end": v(-107.3, -8.29) * mm});
            skLineSegment(sketch, "E549", {"start": v(-107.3, -8.29) * mm, "end": v(-106.5, -8.29) * mm});
            skLineSegment(sketch, "E550", {"start": v(-106.5, -8.29) * mm, "end": v(-106.5, -11.39) * mm});
            skLineSegment(sketch, "E551", {"start": v(-106.5, -11.39) * mm, "end": v(-107.3, -11.39) * mm});
            skLineSegment(sketch, "E552", {"start": v(-107.3, -11.39) * mm, "end": v(-107.3, -17.19) * mm});
            skLineSegment(sketch, "E553", {"start": v(-107.3, -17.19) * mm, "end": v(-106.5, -17.19) * mm});
            skLineSegment(sketch, "E554", {"start": v(-106.5, -17.19) * mm, "end": v(-106.5, -20.29) * mm});
            skLineSegment(sketch, "E555", {"start": v(-106.5, -20.29) * mm, "end": v(-107.3, -20.29) * mm});
            skLineSegment(sketch, "E556", {"start": v(-102.54, 46.39) * mm, "end": v(-102.54, 45.39) * mm});
            skLineSegment(sketch, "E557", {"start": v(-102.54, 45.39) * mm, "end": v(-116.54, 45.39) * mm});
            skLineSegment(sketch, "E558", {"start": v(-116.54, 45.39) * mm, "end": v(-116.54, 46.39) * mm});
            skLineSegment(sketch, "E559", {"start": v(-116.54, 46.39) * mm, "end": v(-117.34, 46.39) * mm});
            skLineSegment(sketch, "E560", {"start": v(-117.34, 46.39) * mm, "end": v(-117.34, 49.49) * mm});
            skLineSegment(sketch, "E561", {"start": v(-117.34, 49.49) * mm, "end": v(-116.54, 49.49) * mm});
            skLineSegment(sketch, "E562", {"start": v(-116.54, 49.49) * mm, "end": v(-116.54, 55.29) * mm});
            skLineSegment(sketch, "E563", {"start": v(-116.54, 55.29) * mm, "end": v(-117.34, 55.29) * mm});
            skLineSegment(sketch, "E564", {"start": v(-117.34, 55.29) * mm, "end": v(-117.34, 58.39) * mm});
            skLineSegment(sketch, "E565", {"start": v(-117.34, 58.39) * mm, "end": v(-116.54, 58.39) * mm});
            skLineSegment(sketch, "E566", {"start": v(-116.54, 58.39) * mm, "end": v(-116.54, 59.39) * mm});
            skLineSegment(sketch, "E567", {"start": v(-116.54, 59.39) * mm, "end": v(-102.54, 59.39) * mm});
            skLineSegment(sketch, "E568", {"start": v(-102.54, 59.39) * mm, "end": v(-102.54, 58.39) * mm});
            skLineSegment(sketch, "E569", {"start": v(-102.54, 58.39) * mm, "end": v(-101.74, 58.39) * mm});
            skLineSegment(sketch, "E570", {"start": v(-101.74, 58.39) * mm, "end": v(-101.74, 55.29) * mm});
            skLineSegment(sketch, "E571", {"start": v(-101.74, 55.29) * mm, "end": v(-102.54, 55.29) * mm});
            skLineSegment(sketch, "E572", {"start": v(-102.54, 55.29) * mm, "end": v(-102.54, 49.49) * mm});
            skLineSegment(sketch, "E573", {"start": v(-102.54, 49.49) * mm, "end": v(-101.74, 49.49) * mm});
            skLineSegment(sketch, "E574", {"start": v(-101.74, 49.49) * mm, "end": v(-101.74, 46.39) * mm});
            skLineSegment(sketch, "E575", {"start": v(-101.74, 46.39) * mm, "end": v(-102.54, 46.39) * mm});
            skLineSegment(sketch, "E576", {"start": v(-102.54, 17.81) * mm, "end": v(-102.54, 16.81) * mm});
            skLineSegment(sketch, "E577", {"start": v(-102.54, 16.81) * mm, "end": v(-116.54, 16.81) * mm});
            skLineSegment(sketch, "E578", {"start": v(-116.54, 16.81) * mm, "end": v(-116.54, 17.81) * mm});
            skLineSegment(sketch, "E579", {"start": v(-116.54, 17.81) * mm, "end": v(-117.34, 17.81) * mm});
            skLineSegment(sketch, "E580", {"start": v(-117.34, 17.81) * mm, "end": v(-117.34, 20.91) * mm});
            skLineSegment(sketch, "E581", {"start": v(-117.34, 20.91) * mm, "end": v(-116.54, 20.91) * mm});
            skLineSegment(sketch, "E582", {"start": v(-116.54, 20.91) * mm, "end": v(-116.54, 26.71) * mm});
            skLineSegment(sketch, "E583", {"start": v(-116.54, 26.71) * mm, "end": v(-117.34, 26.71) * mm});
            skLineSegment(sketch, "E584", {"start": v(-117.34, 26.71) * mm, "end": v(-117.34, 29.81) * mm});
            skLineSegment(sketch, "E585", {"start": v(-117.34, 29.81) * mm, "end": v(-116.54, 29.81) * mm});
            skLineSegment(sketch, "E586", {"start": v(-116.54, 29.81) * mm, "end": v(-116.54, 30.81) * mm});
            skLineSegment(sketch, "E587", {"start": v(-116.54, 30.81) * mm, "end": v(-102.54, 30.81) * mm});
            skLineSegment(sketch, "E588", {"start": v(-102.54, 30.81) * mm, "end": v(-102.54, 29.81) * mm});
            skLineSegment(sketch, "E589", {"start": v(-102.54, 29.81) * mm, "end": v(-101.74, 29.81) * mm});
            skLineSegment(sketch, "E590", {"start": v(-101.74, 29.81) * mm, "end": v(-101.74, 26.71) * mm});
            skLineSegment(sketch, "E591", {"start": v(-101.74, 26.71) * mm, "end": v(-102.54, 26.71) * mm});
            skLineSegment(sketch, "E592", {"start": v(-102.54, 26.71) * mm, "end": v(-102.54, 20.91) * mm});
            skLineSegment(sketch, "E593", {"start": v(-102.54, 20.91) * mm, "end": v(-101.74, 20.91) * mm});
            skLineSegment(sketch, "E594", {"start": v(-101.74, 20.91) * mm, "end": v(-101.74, 17.81) * mm});
            skLineSegment(sketch, "E595", {"start": v(-101.74, 17.81) * mm, "end": v(-102.54, 17.81) * mm});
            skLineSegment(sketch, "E596", {"start": v(-97.78, -39.34) * mm, "end": v(-97.78, -40.34) * mm});
            skLineSegment(sketch, "E597", {"start": v(-97.78, -40.34) * mm, "end": v(-111.78, -40.34) * mm});
            skLineSegment(sketch, "E598", {"start": v(-111.78, -40.34) * mm, "end": v(-111.78, -39.34) * mm});
            skLineSegment(sketch, "E599", {"start": v(-111.78, -39.34) * mm, "end": v(-112.58, -39.34) * mm});
            skLineSegment(sketch, "E600", {"start": v(-112.58, -39.34) * mm, "end": v(-112.58, -36.24) * mm});
            skLineSegment(sketch, "E601", {"start": v(-112.58, -36.24) * mm, "end": v(-111.78, -36.24) * mm});
            skLineSegment(sketch, "E602", {"start": v(-111.78, -36.24) * mm, "end": v(-111.78, -30.44) * mm});
            skLineSegment(sketch, "E603", {"start": v(-111.78, -30.44) * mm, "end": v(-112.58, -30.44) * mm});
            skLineSegment(sketch, "E604", {"start": v(-112.58, -30.44) * mm, "end": v(-112.58, -27.34) * mm});
            skLineSegment(sketch, "E605", {"start": v(-112.58, -27.34) * mm, "end": v(-111.78, -27.34) * mm});
            skLineSegment(sketch, "E606", {"start": v(-111.78, -27.34) * mm, "end": v(-111.78, -26.34) * mm});
            skLineSegment(sketch, "E607", {"start": v(-111.78, -26.34) * mm, "end": v(-97.78, -26.34) * mm});
            skLineSegment(sketch, "E608", {"start": v(-97.78, -26.34) * mm, "end": v(-97.78, -27.34) * mm});
            skLineSegment(sketch, "E609", {"start": v(-97.78, -27.34) * mm, "end": v(-96.98, -27.34) * mm});
            skLineSegment(sketch, "E610", {"start": v(-96.98, -27.34) * mm, "end": v(-96.98, -30.44) * mm});
            skLineSegment(sketch, "E611", {"start": v(-96.98, -30.44) * mm, "end": v(-97.78, -30.44) * mm});
            skLineSegment(sketch, "E612", {"start": v(-97.78, -30.44) * mm, "end": v(-97.78, -36.24) * mm});
            skLineSegment(sketch, "E613", {"start": v(-97.78, -36.24) * mm, "end": v(-96.98, -36.24) * mm});
            skLineSegment(sketch, "E614", {"start": v(-96.98, -36.24) * mm, "end": v(-96.98, -39.34) * mm});
            skLineSegment(sketch, "E615", {"start": v(-96.98, -39.34) * mm, "end": v(-97.78, -39.34) * mm});
            skLineSegment(sketch, "E616", {"start": v(-93.01, -1.24) * mm, "end": v(-93.01, -2.24) * mm});
            skLineSegment(sketch, "E617", {"start": v(-93.01, -2.24) * mm, "end": v(-107.01, -2.24) * mm});
            skLineSegment(sketch, "E618", {"start": v(-107.01, -2.24) * mm, "end": v(-107.01, -1.24) * mm});
            skLineSegment(sketch, "E619", {"start": v(-107.01, -1.24) * mm, "end": v(-107.81, -1.24) * mm});
            skLineSegment(sketch, "E620", {"start": v(-107.81, -1.24) * mm, "end": v(-107.81, 1.86) * mm});
            skLineSegment(sketch, "E621", {"start": v(-107.81, 1.86) * mm, "end": v(-107.01, 1.86) * mm});
            skLineSegment(sketch, "E622", {"start": v(-107.01, 1.86) * mm, "end": v(-107.01, 7.66) * mm});
            skLineSegment(sketch, "E623", {"start": v(-107.01, 7.66) * mm, "end": v(-107.81, 7.66) * mm});
            skLineSegment(sketch, "E624", {"start": v(-107.81, 7.66) * mm, "end": v(-107.81, 10.76) * mm});
            skLineSegment(sketch, "E625", {"start": v(-107.81, 10.76) * mm, "end": v(-107.01, 10.76) * mm});
            skLineSegment(sketch, "E626", {"start": v(-107.01, 10.76) * mm, "end": v(-107.01, 11.76) * mm});
            skLineSegment(sketch, "E627", {"start": v(-107.01, 11.76) * mm, "end": v(-93.01, 11.76) * mm});
            skLineSegment(sketch, "E628", {"start": v(-93.01, 11.76) * mm, "end": v(-93.01, 10.76) * mm});
            skLineSegment(sketch, "E629", {"start": v(-93.01, 10.76) * mm, "end": v(-92.21, 10.76) * mm});
            skLineSegment(sketch, "E630", {"start": v(-92.21, 10.76) * mm, "end": v(-92.21, 7.66) * mm});
            skLineSegment(sketch, "E631", {"start": v(-92.21, 7.66) * mm, "end": v(-93.01, 7.66) * mm});
            skLineSegment(sketch, "E632", {"start": v(-93.01, 7.66) * mm, "end": v(-93.01, 1.86) * mm});
            skLineSegment(sketch, "E633", {"start": v(-93.01, 1.86) * mm, "end": v(-92.21, 1.86) * mm});
            skLineSegment(sketch, "E634", {"start": v(-92.21, 1.86) * mm, "end": v(-92.21, -1.24) * mm});
            skLineSegment(sketch, "E635", {"start": v(-92.21, -1.24) * mm, "end": v(-93.01, -1.24) * mm});
            skLineSegment(sketch, "E636", {"start": v(-88.25, -20.29) * mm, "end": v(-88.25, -21.29) * mm});
            skLineSegment(sketch, "E637", {"start": v(-88.25, -21.29) * mm, "end": v(-102.25, -21.29) * mm});
            skLineSegment(sketch, "E638", {"start": v(-102.25, -21.29) * mm, "end": v(-102.25, -20.29) * mm});
            skLineSegment(sketch, "E639", {"start": v(-102.25, -20.29) * mm, "end": v(-103.05, -20.29) * mm});
            skLineSegment(sketch, "E640", {"start": v(-103.05, -20.29) * mm, "end": v(-103.05, -17.19) * mm});
            skLineSegment(sketch, "E641", {"start": v(-103.05, -17.19) * mm, "end": v(-102.25, -17.19) * mm});
            skLineSegment(sketch, "E642", {"start": v(-102.25, -17.19) * mm, "end": v(-102.25, -11.39) * mm});
            skLineSegment(sketch, "E643", {"start": v(-102.25, -11.39) * mm, "end": v(-103.05, -11.39) * mm});
            skLineSegment(sketch, "E644", {"start": v(-103.05, -11.39) * mm, "end": v(-103.05, -8.29) * mm});
            skLineSegment(sketch, "E645", {"start": v(-103.05, -8.29) * mm, "end": v(-102.25, -8.29) * mm});
            skLineSegment(sketch, "E646", {"start": v(-102.25, -8.29) * mm, "end": v(-102.25, -7.29) * mm});
            skLineSegment(sketch, "E647", {"start": v(-102.25, -7.29) * mm, "end": v(-88.25, -7.29) * mm});
            skLineSegment(sketch, "E648", {"start": v(-88.25, -7.29) * mm, "end": v(-88.25, -8.29) * mm});
            skLineSegment(sketch, "E649", {"start": v(-88.25, -8.29) * mm, "end": v(-87.45, -8.29) * mm});
            skLineSegment(sketch, "E650", {"start": v(-87.45, -8.29) * mm, "end": v(-87.45, -11.39) * mm});
            skLineSegment(sketch, "E651", {"start": v(-87.45, -11.39) * mm, "end": v(-88.25, -11.39) * mm});
            skLineSegment(sketch, "E652", {"start": v(-88.25, -11.39) * mm, "end": v(-88.25, -17.19) * mm});
            skLineSegment(sketch, "E653", {"start": v(-88.25, -17.19) * mm, "end": v(-87.45, -17.19) * mm});
            skLineSegment(sketch, "E654", {"start": v(-87.45, -17.19) * mm, "end": v(-87.45, -20.29) * mm});
            skLineSegment(sketch, "E655", {"start": v(-87.45, -20.29) * mm, "end": v(-88.25, -20.29) * mm});
            skLineSegment(sketch, "E656", {"start": v(-83.49, 17.81) * mm, "end": v(-83.49, 16.81) * mm});
            skLineSegment(sketch, "E657", {"start": v(-83.49, 16.81) * mm, "end": v(-97.49, 16.81) * mm});
            skLineSegment(sketch, "E658", {"start": v(-97.49, 16.81) * mm, "end": v(-97.49, 17.81) * mm});
            skLineSegment(sketch, "E659", {"start": v(-97.49, 17.81) * mm, "end": v(-98.29, 17.81) * mm});
            skLineSegment(sketch, "E660", {"start": v(-98.29, 17.81) * mm, "end": v(-98.29, 20.91) * mm});
            skLineSegment(sketch, "E661", {"start": v(-98.29, 20.91) * mm, "end": v(-97.49, 20.91) * mm});
            skLineSegment(sketch, "E662", {"start": v(-97.49, 20.91) * mm, "end": v(-97.49, 26.71) * mm});
            skLineSegment(sketch, "E663", {"start": v(-97.49, 26.71) * mm, "end": v(-98.29, 26.71) * mm});
            skLineSegment(sketch, "E664", {"start": v(-98.29, 26.71) * mm, "end": v(-98.29, 29.81) * mm});
            skLineSegment(sketch, "E665", {"start": v(-98.29, 29.81) * mm, "end": v(-97.49, 29.81) * mm});
            skLineSegment(sketch, "E666", {"start": v(-97.49, 29.81) * mm, "end": v(-97.49, 30.81) * mm});
            skLineSegment(sketch, "E667", {"start": v(-97.49, 30.81) * mm, "end": v(-83.49, 30.81) * mm});
            skLineSegment(sketch, "E668", {"start": v(-83.49, 30.81) * mm, "end": v(-83.49, 29.81) * mm});
            skLineSegment(sketch, "E669", {"start": v(-83.49, 29.81) * mm, "end": v(-82.69, 29.81) * mm});
            skLineSegment(sketch, "E670", {"start": v(-82.69, 29.81) * mm, "end": v(-82.69, 26.71) * mm});
            skLineSegment(sketch, "E671", {"start": v(-82.69, 26.71) * mm, "end": v(-83.49, 26.71) * mm});
            skLineSegment(sketch, "E672", {"start": v(-83.49, 26.71) * mm, "end": v(-83.49, 20.91) * mm});
            skLineSegment(sketch, "E673", {"start": v(-83.49, 20.91) * mm, "end": v(-82.69, 20.91) * mm});
            skLineSegment(sketch, "E674", {"start": v(-82.69, 20.91) * mm, "end": v(-82.69, 17.81) * mm});
            skLineSegment(sketch, "E675", {"start": v(-82.69, 17.81) * mm, "end": v(-83.49, 17.81) * mm});
            skLineSegment(sketch, "E676", {"start": v(-78.72, -39.34) * mm, "end": v(-78.72, -40.34) * mm});
            skLineSegment(sketch, "E677", {"start": v(-78.72, -40.34) * mm, "end": v(-92.72, -40.34) * mm});
            skLineSegment(sketch, "E678", {"start": v(-92.72, -40.34) * mm, "end": v(-92.72, -39.34) * mm});
            skLineSegment(sketch, "E679", {"start": v(-92.72, -39.34) * mm, "end": v(-93.53, -39.34) * mm});
            skLineSegment(sketch, "E680", {"start": v(-93.53, -39.34) * mm, "end": v(-93.53, -36.24) * mm});
            skLineSegment(sketch, "E681", {"start": v(-93.53, -36.24) * mm, "end": v(-92.72, -36.24) * mm});
            skLineSegment(sketch, "E682", {"start": v(-92.72, -36.24) * mm, "end": v(-92.72, -30.44) * mm});
            skLineSegment(sketch, "E683", {"start": v(-92.72, -30.44) * mm, "end": v(-93.53, -30.44) * mm});
            skLineSegment(sketch, "E684", {"start": v(-93.53, -30.44) * mm, "end": v(-93.53, -27.34) * mm});
            skLineSegment(sketch, "E685", {"start": v(-93.53, -27.34) * mm, "end": v(-92.72, -27.34) * mm});
            skLineSegment(sketch, "E686", {"start": v(-92.72, -27.34) * mm, "end": v(-92.72, -26.34) * mm});
            skLineSegment(sketch, "E687", {"start": v(-92.72, -26.34) * mm, "end": v(-78.72, -26.34) * mm});
            skLineSegment(sketch, "E688", {"start": v(-78.72, -26.34) * mm, "end": v(-78.72, -27.34) * mm});
            skLineSegment(sketch, "E689", {"start": v(-78.72, -27.34) * mm, "end": v(-77.92, -27.34) * mm});
            skLineSegment(sketch, "E690", {"start": v(-77.92, -27.34) * mm, "end": v(-77.92, -30.44) * mm});
            skLineSegment(sketch, "E691", {"start": v(-77.92, -30.44) * mm, "end": v(-78.72, -30.44) * mm});
            skLineSegment(sketch, "E692", {"start": v(-78.72, -30.44) * mm, "end": v(-78.72, -36.24) * mm});
            skLineSegment(sketch, "E693", {"start": v(-78.72, -36.24) * mm, "end": v(-77.92, -36.24) * mm});
            skLineSegment(sketch, "E694", {"start": v(-77.92, -36.24) * mm, "end": v(-77.92, -39.34) * mm});
            skLineSegment(sketch, "E695", {"start": v(-77.92, -39.34) * mm, "end": v(-78.72, -39.34) * mm});
            skLineSegment(sketch, "E696", {"start": v(-73.96, 46.39) * mm, "end": v(-73.96, 45.39) * mm});
            skLineSegment(sketch, "E697", {"start": v(-73.96, 45.39) * mm, "end": v(-87.96, 45.39) * mm});
            skLineSegment(sketch, "E698", {"start": v(-87.96, 45.39) * mm, "end": v(-87.96, 46.39) * mm});
            skLineSegment(sketch, "E699", {"start": v(-87.96, 46.39) * mm, "end": v(-88.76, 46.39) * mm});
            skLineSegment(sketch, "E700", {"start": v(-88.76, 46.39) * mm, "end": v(-88.76, 49.49) * mm});
            skLineSegment(sketch, "E701", {"start": v(-88.76, 49.49) * mm, "end": v(-87.96, 49.49) * mm});
            skLineSegment(sketch, "E702", {"start": v(-87.96, 49.49) * mm, "end": v(-87.96, 55.29) * mm});
            skLineSegment(sketch, "E703", {"start": v(-87.96, 55.29) * mm, "end": v(-88.76, 55.29) * mm});
            skLineSegment(sketch, "E704", {"start": v(-88.76, 55.29) * mm, "end": v(-88.76, 58.39) * mm});
            skLineSegment(sketch, "E705", {"start": v(-88.76, 58.39) * mm, "end": v(-87.96, 58.39) * mm});
            skLineSegment(sketch, "E706", {"start": v(-87.96, 58.39) * mm, "end": v(-87.96, 59.39) * mm});
            skLineSegment(sketch, "E707", {"start": v(-87.96, 59.39) * mm, "end": v(-73.96, 59.39) * mm});
            skLineSegment(sketch, "E708", {"start": v(-73.96, 59.39) * mm, "end": v(-73.96, 58.39) * mm});
            skLineSegment(sketch, "E709", {"start": v(-73.96, 58.39) * mm, "end": v(-73.16, 58.39) * mm});
            skLineSegment(sketch, "E710", {"start": v(-73.16, 58.39) * mm, "end": v(-73.16, 55.29) * mm});
            skLineSegment(sketch, "E711", {"start": v(-73.16, 55.29) * mm, "end": v(-73.96, 55.29) * mm});
            skLineSegment(sketch, "E712", {"start": v(-73.96, 55.29) * mm, "end": v(-73.96, 49.49) * mm});
            skLineSegment(sketch, "E713", {"start": v(-73.96, 49.49) * mm, "end": v(-73.16, 49.49) * mm});
            skLineSegment(sketch, "E714", {"start": v(-73.16, 49.49) * mm, "end": v(-73.16, 46.39) * mm});
            skLineSegment(sketch, "E715", {"start": v(-73.16, 46.39) * mm, "end": v(-73.96, 46.39) * mm});
            skLineSegment(sketch, "E716", {"start": v(-73.96, -1.24) * mm, "end": v(-73.96, -2.24) * mm});
            skLineSegment(sketch, "E717", {"start": v(-73.96, -2.24) * mm, "end": v(-87.96, -2.24) * mm});
            skLineSegment(sketch, "E718", {"start": v(-87.96, -2.24) * mm, "end": v(-87.96, -1.24) * mm});
            skLineSegment(sketch, "E719", {"start": v(-87.96, -1.24) * mm, "end": v(-88.76, -1.24) * mm});
            skLineSegment(sketch, "E720", {"start": v(-88.76, -1.24) * mm, "end": v(-88.76, 1.86) * mm});
            skLineSegment(sketch, "E721", {"start": v(-88.76, 1.86) * mm, "end": v(-87.96, 1.86) * mm});
            skLineSegment(sketch, "E722", {"start": v(-87.96, 1.86) * mm, "end": v(-87.96, 7.66) * mm});
            skLineSegment(sketch, "E723", {"start": v(-87.96, 7.66) * mm, "end": v(-88.76, 7.66) * mm});
            skLineSegment(sketch, "E724", {"start": v(-88.76, 7.66) * mm, "end": v(-88.76, 10.76) * mm});
            skLineSegment(sketch, "E725", {"start": v(-88.76, 10.76) * mm, "end": v(-87.96, 10.76) * mm});
            skLineSegment(sketch, "E726", {"start": v(-87.96, 10.76) * mm, "end": v(-87.96, 11.76) * mm});
            skLineSegment(sketch, "E727", {"start": v(-87.96, 11.76) * mm, "end": v(-73.96, 11.76) * mm});
            skLineSegment(sketch, "E728", {"start": v(-73.96, 11.76) * mm, "end": v(-73.96, 10.76) * mm});
            skLineSegment(sketch, "E729", {"start": v(-73.96, 10.76) * mm, "end": v(-73.16, 10.76) * mm});
            skLineSegment(sketch, "E730", {"start": v(-73.16, 10.76) * mm, "end": v(-73.16, 7.66) * mm});
            skLineSegment(sketch, "E731", {"start": v(-73.16, 7.66) * mm, "end": v(-73.96, 7.66) * mm});
            skLineSegment(sketch, "E732", {"start": v(-73.96, 7.66) * mm, "end": v(-73.96, 1.86) * mm});
            skLineSegment(sketch, "E733", {"start": v(-73.96, 1.86) * mm, "end": v(-73.16, 1.86) * mm});
            skLineSegment(sketch, "E734", {"start": v(-73.16, 1.86) * mm, "end": v(-73.16, -1.24) * mm});
            skLineSegment(sketch, "E735", {"start": v(-73.16, -1.24) * mm, "end": v(-73.96, -1.24) * mm});
            skLineSegment(sketch, "E736", {"start": v(-69.2, -20.29) * mm, "end": v(-69.2, -21.29) * mm});
            skLineSegment(sketch, "E737", {"start": v(-69.2, -21.29) * mm, "end": v(-83.2, -21.29) * mm});
            skLineSegment(sketch, "E738", {"start": v(-83.2, -21.29) * mm, "end": v(-83.2, -20.29) * mm});
            skLineSegment(sketch, "E739", {"start": v(-83.2, -20.29) * mm, "end": v(-84, -20.29) * mm});
            skLineSegment(sketch, "E740", {"start": v(-84, -20.29) * mm, "end": v(-84, -17.19) * mm});
            skLineSegment(sketch, "E741", {"start": v(-84, -17.19) * mm, "end": v(-83.2, -17.19) * mm});
            skLineSegment(sketch, "E742", {"start": v(-83.2, -17.19) * mm, "end": v(-83.2, -11.39) * mm});
            skLineSegment(sketch, "E743", {"start": v(-83.2, -11.39) * mm, "end": v(-84, -11.39) * mm});
            skLineSegment(sketch, "E744", {"start": v(-84, -11.39) * mm, "end": v(-84, -8.29) * mm});
            skLineSegment(sketch, "E745", {"start": v(-84, -8.29) * mm, "end": v(-83.2, -8.29) * mm});
            skLineSegment(sketch, "E746", {"start": v(-83.2, -8.29) * mm, "end": v(-83.2, -7.29) * mm});
            skLineSegment(sketch, "E747", {"start": v(-83.2, -7.29) * mm, "end": v(-69.2, -7.29) * mm});
            skLineSegment(sketch, "E748", {"start": v(-69.2, -7.29) * mm, "end": v(-69.2, -8.29) * mm});
            skLineSegment(sketch, "E749", {"start": v(-69.2, -8.29) * mm, "end": v(-68.4, -8.29) * mm});
            skLineSegment(sketch, "E750", {"start": v(-68.4, -8.29) * mm, "end": v(-68.4, -11.39) * mm});
            skLineSegment(sketch, "E751", {"start": v(-68.4, -11.39) * mm, "end": v(-69.2, -11.39) * mm});
            skLineSegment(sketch, "E752", {"start": v(-69.2, -11.39) * mm, "end": v(-69.2, -17.19) * mm});
            skLineSegment(sketch, "E753", {"start": v(-69.2, -17.19) * mm, "end": v(-68.4, -17.19) * mm});
            skLineSegment(sketch, "E754", {"start": v(-68.4, -17.19) * mm, "end": v(-68.4, -20.29) * mm});
            skLineSegment(sketch, "E755", {"start": v(-68.4, -20.29) * mm, "end": v(-69.2, -20.29) * mm});
            skLineSegment(sketch, "E756", {"start": v(-64.44, 17.81) * mm, "end": v(-64.44, 16.81) * mm});
            skLineSegment(sketch, "E757", {"start": v(-64.44, 16.81) * mm, "end": v(-78.44, 16.81) * mm});
            skLineSegment(sketch, "E758", {"start": v(-78.44, 16.81) * mm, "end": v(-78.44, 17.81) * mm});
            skLineSegment(sketch, "E759", {"start": v(-78.44, 17.81) * mm, "end": v(-79.24, 17.81) * mm});
            skLineSegment(sketch, "E760", {"start": v(-79.24, 17.81) * mm, "end": v(-79.24, 20.91) * mm});
            skLineSegment(sketch, "E761", {"start": v(-79.24, 20.91) * mm, "end": v(-78.44, 20.91) * mm});
            skLineSegment(sketch, "E762", {"start": v(-78.44, 20.91) * mm, "end": v(-78.44, 26.71) * mm});
            skLineSegment(sketch, "E763", {"start": v(-78.44, 26.71) * mm, "end": v(-79.24, 26.71) * mm});
            skLineSegment(sketch, "E764", {"start": v(-79.24, 26.71) * mm, "end": v(-79.24, 29.81) * mm});
            skLineSegment(sketch, "E765", {"start": v(-79.24, 29.81) * mm, "end": v(-78.44, 29.81) * mm});
            skLineSegment(sketch, "E766", {"start": v(-78.44, 29.81) * mm, "end": v(-78.44, 30.81) * mm});
            skLineSegment(sketch, "E767", {"start": v(-78.44, 30.81) * mm, "end": v(-64.44, 30.81) * mm});
            skLineSegment(sketch, "E768", {"start": v(-64.44, 30.81) * mm, "end": v(-64.44, 29.81) * mm});
            skLineSegment(sketch, "E769", {"start": v(-64.44, 29.81) * mm, "end": v(-63.64, 29.81) * mm});
            skLineSegment(sketch, "E770", {"start": v(-63.64, 29.81) * mm, "end": v(-63.64, 26.71) * mm});
            skLineSegment(sketch, "E771", {"start": v(-63.64, 26.71) * mm, "end": v(-64.44, 26.71) * mm});
            skLineSegment(sketch, "E772", {"start": v(-64.44, 26.71) * mm, "end": v(-64.44, 20.91) * mm});
            skLineSegment(sketch, "E773", {"start": v(-64.44, 20.91) * mm, "end": v(-63.64, 20.91) * mm});
            skLineSegment(sketch, "E774", {"start": v(-63.64, 20.91) * mm, "end": v(-63.64, 17.81) * mm});
            skLineSegment(sketch, "E775", {"start": v(-63.64, 17.81) * mm, "end": v(-64.44, 17.81) * mm});
            skLineSegment(sketch, "E776", {"start": v(-59.67, -39.34) * mm, "end": v(-59.67, -40.34) * mm});
            skLineSegment(sketch, "E777", {"start": v(-59.67, -40.34) * mm, "end": v(-73.67, -40.34) * mm});
            skLineSegment(sketch, "E778", {"start": v(-73.67, -40.34) * mm, "end": v(-73.67, -39.34) * mm});
            skLineSegment(sketch, "E779", {"start": v(-73.67, -39.34) * mm, "end": v(-74.48, -39.34) * mm});
            skLineSegment(sketch, "E780", {"start": v(-74.48, -39.34) * mm, "end": v(-74.48, -36.24) * mm});
            skLineSegment(sketch, "E781", {"start": v(-74.48, -36.24) * mm, "end": v(-73.67, -36.24) * mm});
            skLineSegment(sketch, "E782", {"start": v(-73.67, -36.24) * mm, "end": v(-73.67, -30.44) * mm});
            skLineSegment(sketch, "E783", {"start": v(-73.67, -30.44) * mm, "end": v(-74.48, -30.44) * mm});
            skLineSegment(sketch, "E784", {"start": v(-74.48, -30.44) * mm, "end": v(-74.48, -27.34) * mm});
            skLineSegment(sketch, "E785", {"start": v(-74.48, -27.34) * mm, "end": v(-73.67, -27.34) * mm});
            skLineSegment(sketch, "E786", {"start": v(-73.67, -27.34) * mm, "end": v(-73.67, -26.34) * mm});
            skLineSegment(sketch, "E787", {"start": v(-73.67, -26.34) * mm, "end": v(-59.67, -26.34) * mm});
            skLineSegment(sketch, "E788", {"start": v(-59.67, -26.34) * mm, "end": v(-59.67, -27.34) * mm});
            skLineSegment(sketch, "E789", {"start": v(-59.67, -27.34) * mm, "end": v(-58.87, -27.34) * mm});
            skLineSegment(sketch, "E790", {"start": v(-58.87, -27.34) * mm, "end": v(-58.87, -30.44) * mm});
            skLineSegment(sketch, "E791", {"start": v(-58.87, -30.44) * mm, "end": v(-59.67, -30.44) * mm});
            skLineSegment(sketch, "E792", {"start": v(-59.67, -30.44) * mm, "end": v(-59.67, -36.24) * mm});
            skLineSegment(sketch, "E793", {"start": v(-59.67, -36.24) * mm, "end": v(-58.87, -36.24) * mm});
            skLineSegment(sketch, "E794", {"start": v(-58.87, -36.24) * mm, "end": v(-58.87, -39.34) * mm});
            skLineSegment(sketch, "E795", {"start": v(-58.87, -39.34) * mm, "end": v(-59.67, -39.34) * mm});
            skLineSegment(sketch, "E796", {"start": v(-54.91, 46.39) * mm, "end": v(-54.91, 45.39) * mm});
            skLineSegment(sketch, "E797", {"start": v(-54.91, 45.39) * mm, "end": v(-68.91, 45.39) * mm});
            skLineSegment(sketch, "E798", {"start": v(-68.91, 45.39) * mm, "end": v(-68.91, 46.39) * mm});
            skLineSegment(sketch, "E799", {"start": v(-68.91, 46.39) * mm, "end": v(-69.71, 46.39) * mm});
            skLineSegment(sketch, "E800", {"start": v(-69.71, 46.39) * mm, "end": v(-69.71, 49.49) * mm});
            skLineSegment(sketch, "E801", {"start": v(-69.71, 49.49) * mm, "end": v(-68.91, 49.49) * mm});
            skLineSegment(sketch, "E802", {"start": v(-68.91, 49.49) * mm, "end": v(-68.91, 55.29) * mm});
            skLineSegment(sketch, "E803", {"start": v(-68.91, 55.29) * mm, "end": v(-69.71, 55.29) * mm});
            skLineSegment(sketch, "E804", {"start": v(-69.71, 55.29) * mm, "end": v(-69.71, 58.39) * mm});
            skLineSegment(sketch, "E805", {"start": v(-69.71, 58.39) * mm, "end": v(-68.91, 58.39) * mm});
            skLineSegment(sketch, "E806", {"start": v(-68.91, 58.39) * mm, "end": v(-68.91, 59.39) * mm});
            skLineSegment(sketch, "E807", {"start": v(-68.91, 59.39) * mm, "end": v(-54.91, 59.39) * mm});
            skLineSegment(sketch, "E808", {"start": v(-54.91, 59.39) * mm, "end": v(-54.91, 58.39) * mm});
            skLineSegment(sketch, "E809", {"start": v(-54.91, 58.39) * mm, "end": v(-54.11, 58.39) * mm});
            skLineSegment(sketch, "E810", {"start": v(-54.11, 58.39) * mm, "end": v(-54.11, 55.29) * mm});
            skLineSegment(sketch, "E811", {"start": v(-54.11, 55.29) * mm, "end": v(-54.91, 55.29) * mm});
            skLineSegment(sketch, "E812", {"start": v(-54.91, 55.29) * mm, "end": v(-54.91, 49.49) * mm});
            skLineSegment(sketch, "E813", {"start": v(-54.91, 49.49) * mm, "end": v(-54.11, 49.49) * mm});
            skLineSegment(sketch, "E814", {"start": v(-54.11, 49.49) * mm, "end": v(-54.11, 46.39) * mm});
            skLineSegment(sketch, "E815", {"start": v(-54.11, 46.39) * mm, "end": v(-54.91, 46.39) * mm});
            skLineSegment(sketch, "E816", {"start": v(-54.91, -1.24) * mm, "end": v(-54.91, -2.24) * mm});
            skLineSegment(sketch, "E817", {"start": v(-54.91, -2.24) * mm, "end": v(-68.91, -2.24) * mm});
            skLineSegment(sketch, "E818", {"start": v(-68.91, -2.24) * mm, "end": v(-68.91, -1.24) * mm});
            skLineSegment(sketch, "E819", {"start": v(-68.91, -1.24) * mm, "end": v(-69.71, -1.24) * mm});
            skLineSegment(sketch, "E820", {"start": v(-69.71, -1.24) * mm, "end": v(-69.71, 1.86) * mm});
            skLineSegment(sketch, "E821", {"start": v(-69.71, 1.86) * mm, "end": v(-68.91, 1.86) * mm});
            skLineSegment(sketch, "E822", {"start": v(-68.91, 1.86) * mm, "end": v(-68.91, 7.66) * mm});
            skLineSegment(sketch, "E823", {"start": v(-68.91, 7.66) * mm, "end": v(-69.71, 7.66) * mm});
            skLineSegment(sketch, "E824", {"start": v(-69.71, 7.66) * mm, "end": v(-69.71, 10.76) * mm});
            skLineSegment(sketch, "E825", {"start": v(-69.71, 10.76) * mm, "end": v(-68.91, 10.76) * mm});
            skLineSegment(sketch, "E826", {"start": v(-68.91, 10.76) * mm, "end": v(-68.91, 11.76) * mm});
            skLineSegment(sketch, "E827", {"start": v(-68.91, 11.76) * mm, "end": v(-54.91, 11.76) * mm});
            skLineSegment(sketch, "E828", {"start": v(-54.91, 11.76) * mm, "end": v(-54.91, 10.76) * mm});
            skLineSegment(sketch, "E829", {"start": v(-54.91, 10.76) * mm, "end": v(-54.11, 10.76) * mm});
            skLineSegment(sketch, "E830", {"start": v(-54.11, 10.76) * mm, "end": v(-54.11, 7.66) * mm});
            skLineSegment(sketch, "E831", {"start": v(-54.11, 7.66) * mm, "end": v(-54.91, 7.66) * mm});
            skLineSegment(sketch, "E832", {"start": v(-54.91, 7.66) * mm, "end": v(-54.91, 1.86) * mm});
            skLineSegment(sketch, "E833", {"start": v(-54.91, 1.86) * mm, "end": v(-54.11, 1.86) * mm});
            skLineSegment(sketch, "E834", {"start": v(-54.11, 1.86) * mm, "end": v(-54.11, -1.24) * mm});
            skLineSegment(sketch, "E835", {"start": v(-54.11, -1.24) * mm, "end": v(-54.91, -1.24) * mm});
            skLineSegment(sketch, "E836", {"start": v(-50.15, -20.29) * mm, "end": v(-50.15, -21.29) * mm});
            skLineSegment(sketch, "E837", {"start": v(-50.15, -21.29) * mm, "end": v(-64.15, -21.29) * mm});
            skLineSegment(sketch, "E838", {"start": v(-64.15, -21.29) * mm, "end": v(-64.15, -20.29) * mm});
            skLineSegment(sketch, "E839", {"start": v(-64.15, -20.29) * mm, "end": v(-64.95, -20.29) * mm});
            skLineSegment(sketch, "E840", {"start": v(-64.95, -20.29) * mm, "end": v(-64.95, -17.19) * mm});
            skLineSegment(sketch, "E841", {"start": v(-64.95, -17.19) * mm, "end": v(-64.15, -17.19) * mm});
            skLineSegment(sketch, "E842", {"start": v(-64.15, -17.19) * mm, "end": v(-64.15, -11.39) * mm});
            skLineSegment(sketch, "E843", {"start": v(-64.15, -11.39) * mm, "end": v(-64.95, -11.39) * mm});
            skLineSegment(sketch, "E844", {"start": v(-64.95, -11.39) * mm, "end": v(-64.95, -8.29) * mm});
            skLineSegment(sketch, "E845", {"start": v(-64.95, -8.29) * mm, "end": v(-64.15, -8.29) * mm});
            skLineSegment(sketch, "E846", {"start": v(-64.15, -8.29) * mm, "end": v(-64.15, -7.29) * mm});
            skLineSegment(sketch, "E847", {"start": v(-64.15, -7.29) * mm, "end": v(-50.15, -7.29) * mm});
            skLineSegment(sketch, "E848", {"start": v(-50.15, -7.29) * mm, "end": v(-50.15, -8.29) * mm});
            skLineSegment(sketch, "E849", {"start": v(-50.15, -8.29) * mm, "end": v(-49.35, -8.29) * mm});
            skLineSegment(sketch, "E850", {"start": v(-49.35, -8.29) * mm, "end": v(-49.35, -11.39) * mm});
            skLineSegment(sketch, "E851", {"start": v(-49.35, -11.39) * mm, "end": v(-50.15, -11.39) * mm});
            skLineSegment(sketch, "E852", {"start": v(-50.15, -11.39) * mm, "end": v(-50.15, -17.19) * mm});
            skLineSegment(sketch, "E853", {"start": v(-50.15, -17.19) * mm, "end": v(-49.35, -17.19) * mm});
            skLineSegment(sketch, "E854", {"start": v(-49.35, -17.19) * mm, "end": v(-49.35, -20.29) * mm});
            skLineSegment(sketch, "E855", {"start": v(-49.35, -20.29) * mm, "end": v(-50.15, -20.29) * mm});
            skLineSegment(sketch, "E856", {"start": v(-45.39, 17.81) * mm, "end": v(-45.39, 16.81) * mm});
            skLineSegment(sketch, "E857", {"start": v(-45.39, 16.81) * mm, "end": v(-59.39, 16.81) * mm});
            skLineSegment(sketch, "E858", {"start": v(-59.39, 16.81) * mm, "end": v(-59.39, 17.81) * mm});
            skLineSegment(sketch, "E859", {"start": v(-59.39, 17.81) * mm, "end": v(-60.19, 17.81) * mm});
            skLineSegment(sketch, "E860", {"start": v(-60.19, 17.81) * mm, "end": v(-60.19, 20.91) * mm});
            skLineSegment(sketch, "E861", {"start": v(-60.19, 20.91) * mm, "end": v(-59.39, 20.91) * mm});
            skLineSegment(sketch, "E862", {"start": v(-59.39, 20.91) * mm, "end": v(-59.39, 26.71) * mm});
            skLineSegment(sketch, "E863", {"start": v(-59.39, 26.71) * mm, "end": v(-60.19, 26.71) * mm});
            skLineSegment(sketch, "E864", {"start": v(-60.19, 26.71) * mm, "end": v(-60.19, 29.81) * mm});
            skLineSegment(sketch, "E865", {"start": v(-60.19, 29.81) * mm, "end": v(-59.39, 29.81) * mm});
            skLineSegment(sketch, "E866", {"start": v(-59.39, 29.81) * mm, "end": v(-59.39, 30.81) * mm});
            skLineSegment(sketch, "E867", {"start": v(-59.39, 30.81) * mm, "end": v(-45.39, 30.81) * mm});
            skLineSegment(sketch, "E868", {"start": v(-45.39, 30.81) * mm, "end": v(-45.39, 29.81) * mm});
            skLineSegment(sketch, "E869", {"start": v(-45.39, 29.81) * mm, "end": v(-44.59, 29.81) * mm});
            skLineSegment(sketch, "E870", {"start": v(-44.59, 29.81) * mm, "end": v(-44.59, 26.71) * mm});
            skLineSegment(sketch, "E871", {"start": v(-44.59, 26.71) * mm, "end": v(-45.39, 26.71) * mm});
            skLineSegment(sketch, "E872", {"start": v(-45.39, 26.71) * mm, "end": v(-45.39, 20.91) * mm});
            skLineSegment(sketch, "E873", {"start": v(-45.39, 20.91) * mm, "end": v(-44.59, 20.91) * mm});
            skLineSegment(sketch, "E874", {"start": v(-44.59, 20.91) * mm, "end": v(-44.59, 17.81) * mm});
            skLineSegment(sketch, "E875", {"start": v(-44.59, 17.81) * mm, "end": v(-45.39, 17.81) * mm});
            skLineSegment(sketch, "E876", {"start": v(-40.62, -39.34) * mm, "end": v(-40.62, -40.34) * mm});
            skLineSegment(sketch, "E877", {"start": v(-40.62, -40.34) * mm, "end": v(-54.62, -40.34) * mm});
            skLineSegment(sketch, "E878", {"start": v(-54.62, -40.34) * mm, "end": v(-54.62, -39.34) * mm});
            skLineSegment(sketch, "E879", {"start": v(-54.62, -39.34) * mm, "end": v(-55.43, -39.34) * mm});
            skLineSegment(sketch, "E880", {"start": v(-55.43, -39.34) * mm, "end": v(-55.43, -36.24) * mm});
            skLineSegment(sketch, "E881", {"start": v(-55.43, -36.24) * mm, "end": v(-54.62, -36.24) * mm});
            skLineSegment(sketch, "E882", {"start": v(-54.62, -36.24) * mm, "end": v(-54.62, -30.44) * mm});
            skLineSegment(sketch, "E883", {"start": v(-54.62, -30.44) * mm, "end": v(-55.43, -30.44) * mm});
            skLineSegment(sketch, "E884", {"start": v(-55.43, -30.44) * mm, "end": v(-55.43, -27.34) * mm});
            skLineSegment(sketch, "E885", {"start": v(-55.43, -27.34) * mm, "end": v(-54.62, -27.34) * mm});
            skLineSegment(sketch, "E886", {"start": v(-54.62, -27.34) * mm, "end": v(-54.62, -26.34) * mm});
            skLineSegment(sketch, "E887", {"start": v(-54.62, -26.34) * mm, "end": v(-40.62, -26.34) * mm});
            skLineSegment(sketch, "E888", {"start": v(-40.62, -26.34) * mm, "end": v(-40.62, -27.34) * mm});
            skLineSegment(sketch, "E889", {"start": v(-40.62, -27.34) * mm, "end": v(-39.82, -27.34) * mm});
            skLineSegment(sketch, "E890", {"start": v(-39.82, -27.34) * mm, "end": v(-39.82, -30.44) * mm});
            skLineSegment(sketch, "E891", {"start": v(-39.82, -30.44) * mm, "end": v(-40.62, -30.44) * mm});
            skLineSegment(sketch, "E892", {"start": v(-40.62, -30.44) * mm, "end": v(-40.62, -36.24) * mm});
            skLineSegment(sketch, "E893", {"start": v(-40.62, -36.24) * mm, "end": v(-39.82, -36.24) * mm});
            skLineSegment(sketch, "E894", {"start": v(-39.82, -36.24) * mm, "end": v(-39.82, -39.34) * mm});
            skLineSegment(sketch, "E895", {"start": v(-39.82, -39.34) * mm, "end": v(-40.62, -39.34) * mm});
            skLineSegment(sketch, "E896", {"start": v(-35.86, 46.39) * mm, "end": v(-35.86, 45.39) * mm});
            skLineSegment(sketch, "E897", {"start": v(-35.86, 45.39) * mm, "end": v(-49.86, 45.39) * mm});
            skLineSegment(sketch, "E898", {"start": v(-49.86, 45.39) * mm, "end": v(-49.86, 46.39) * mm});
            skLineSegment(sketch, "E899", {"start": v(-49.86, 46.39) * mm, "end": v(-50.66, 46.39) * mm});
            skLineSegment(sketch, "E900", {"start": v(-50.66, 46.39) * mm, "end": v(-50.66, 49.49) * mm});
            skLineSegment(sketch, "E901", {"start": v(-50.66, 49.49) * mm, "end": v(-49.86, 49.49) * mm});
            skLineSegment(sketch, "E902", {"start": v(-49.86, 49.49) * mm, "end": v(-49.86, 55.29) * mm});
            skLineSegment(sketch, "E903", {"start": v(-49.86, 55.29) * mm, "end": v(-50.66, 55.29) * mm});
            skLineSegment(sketch, "E904", {"start": v(-50.66, 55.29) * mm, "end": v(-50.66, 58.39) * mm});
            skLineSegment(sketch, "E905", {"start": v(-50.66, 58.39) * mm, "end": v(-49.86, 58.39) * mm});
            skLineSegment(sketch, "E906", {"start": v(-49.86, 58.39) * mm, "end": v(-49.86, 59.39) * mm});
            skLineSegment(sketch, "E907", {"start": v(-49.86, 59.39) * mm, "end": v(-35.86, 59.39) * mm});
            skLineSegment(sketch, "E908", {"start": v(-35.86, 59.39) * mm, "end": v(-35.86, 58.39) * mm});
            skLineSegment(sketch, "E909", {"start": v(-35.86, 58.39) * mm, "end": v(-35.06, 58.39) * mm});
            skLineSegment(sketch, "E910", {"start": v(-35.06, 58.39) * mm, "end": v(-35.06, 55.29) * mm});
            skLineSegment(sketch, "E911", {"start": v(-35.06, 55.29) * mm, "end": v(-35.86, 55.29) * mm});
            skLineSegment(sketch, "E912", {"start": v(-35.86, 55.29) * mm, "end": v(-35.86, 49.49) * mm});
            skLineSegment(sketch, "E913", {"start": v(-35.86, 49.49) * mm, "end": v(-35.06, 49.49) * mm});
            skLineSegment(sketch, "E914", {"start": v(-35.06, 49.49) * mm, "end": v(-35.06, 46.39) * mm});
            skLineSegment(sketch, "E915", {"start": v(-35.06, 46.39) * mm, "end": v(-35.86, 46.39) * mm});
            skLineSegment(sketch, "E916", {"start": v(-35.86, -1.24) * mm, "end": v(-35.86, -2.24) * mm});
            skLineSegment(sketch, "E917", {"start": v(-35.86, -2.24) * mm, "end": v(-49.86, -2.24) * mm});
            skLineSegment(sketch, "E918", {"start": v(-49.86, -2.24) * mm, "end": v(-49.86, -1.24) * mm});
            skLineSegment(sketch, "E919", {"start": v(-49.86, -1.24) * mm, "end": v(-50.66, -1.24) * mm});
            skLineSegment(sketch, "E920", {"start": v(-50.66, -1.24) * mm, "end": v(-50.66, 1.86) * mm});
            skLineSegment(sketch, "E921", {"start": v(-50.66, 1.86) * mm, "end": v(-49.86, 1.86) * mm});
            skLineSegment(sketch, "E922", {"start": v(-49.86, 1.86) * mm, "end": v(-49.86, 7.66) * mm});
            skLineSegment(sketch, "E923", {"start": v(-49.86, 7.66) * mm, "end": v(-50.66, 7.66) * mm});
            skLineSegment(sketch, "E924", {"start": v(-50.66, 7.66) * mm, "end": v(-50.66, 10.76) * mm});
            skLineSegment(sketch, "E925", {"start": v(-50.66, 10.76) * mm, "end": v(-49.86, 10.76) * mm});
            skLineSegment(sketch, "E926", {"start": v(-49.86, 10.76) * mm, "end": v(-49.86, 11.76) * mm});
            skLineSegment(sketch, "E927", {"start": v(-49.86, 11.76) * mm, "end": v(-35.86, 11.76) * mm});
            skLineSegment(sketch, "E928", {"start": v(-35.86, 11.76) * mm, "end": v(-35.86, 10.76) * mm});
            skLineSegment(sketch, "E929", {"start": v(-35.86, 10.76) * mm, "end": v(-35.06, 10.76) * mm});
            skLineSegment(sketch, "E930", {"start": v(-35.06, 10.76) * mm, "end": v(-35.06, 7.66) * mm});
            skLineSegment(sketch, "E931", {"start": v(-35.06, 7.66) * mm, "end": v(-35.86, 7.66) * mm});
            skLineSegment(sketch, "E932", {"start": v(-35.86, 7.66) * mm, "end": v(-35.86, 1.86) * mm});
            skLineSegment(sketch, "E933", {"start": v(-35.86, 1.86) * mm, "end": v(-35.06, 1.86) * mm});
            skLineSegment(sketch, "E934", {"start": v(-35.06, 1.86) * mm, "end": v(-35.06, -1.24) * mm});
            skLineSegment(sketch, "E935", {"start": v(-35.06, -1.24) * mm, "end": v(-35.86, -1.24) * mm});
            skLineSegment(sketch, "E936", {"start": v(-31.1, -20.29) * mm, "end": v(-31.1, -21.29) * mm});
            skLineSegment(sketch, "E937", {"start": v(-31.1, -21.29) * mm, "end": v(-45.1, -21.29) * mm});
            skLineSegment(sketch, "E938", {"start": v(-45.1, -21.29) * mm, "end": v(-45.1, -20.29) * mm});
            skLineSegment(sketch, "E939", {"start": v(-45.1, -20.29) * mm, "end": v(-45.9, -20.29) * mm});
            skLineSegment(sketch, "E940", {"start": v(-45.9, -20.29) * mm, "end": v(-45.9, -17.19) * mm});
            skLineSegment(sketch, "E941", {"start": v(-45.9, -17.19) * mm, "end": v(-45.1, -17.19) * mm});
            skLineSegment(sketch, "E942", {"start": v(-45.1, -17.19) * mm, "end": v(-45.1, -11.39) * mm});
            skLineSegment(sketch, "E943", {"start": v(-45.1, -11.39) * mm, "end": v(-45.9, -11.39) * mm});
            skLineSegment(sketch, "E944", {"start": v(-45.9, -11.39) * mm, "end": v(-45.9, -8.29) * mm});
            skLineSegment(sketch, "E945", {"start": v(-45.9, -8.29) * mm, "end": v(-45.1, -8.29) * mm});
            skLineSegment(sketch, "E946", {"start": v(-45.1, -8.29) * mm, "end": v(-45.1, -7.29) * mm});
            skLineSegment(sketch, "E947", {"start": v(-45.1, -7.29) * mm, "end": v(-31.1, -7.29) * mm});
            skLineSegment(sketch, "E948", {"start": v(-31.1, -7.29) * mm, "end": v(-31.1, -8.29) * mm});
            skLineSegment(sketch, "E949", {"start": v(-31.1, -8.29) * mm, "end": v(-30.3, -8.29) * mm});
            skLineSegment(sketch, "E950", {"start": v(-30.3, -8.29) * mm, "end": v(-30.3, -11.39) * mm});
            skLineSegment(sketch, "E951", {"start": v(-30.3, -11.39) * mm, "end": v(-31.1, -11.39) * mm});
            skLineSegment(sketch, "E952", {"start": v(-31.1, -11.39) * mm, "end": v(-31.1, -17.19) * mm});
            skLineSegment(sketch, "E953", {"start": v(-31.1, -17.19) * mm, "end": v(-30.3, -17.19) * mm});
            skLineSegment(sketch, "E954", {"start": v(-30.3, -17.19) * mm, "end": v(-30.3, -20.29) * mm});
            skLineSegment(sketch, "E955", {"start": v(-30.3, -20.29) * mm, "end": v(-31.1, -20.29) * mm});
            skLineSegment(sketch, "E956", {"start": v(-30.02, -52.89) * mm, "end": v(-30.02, -59.16) * mm});
            skLineSegment(sketch, "E957", {"start": v(-30.02, -59.16) * mm, "end": v(-31.7, -59.16) * mm});
            skLineSegment(sketch, "E958", {"start": v(-31.7, -59.16) * mm, "end": v(-31.7, -60.14) * mm});
            skLineSegment(sketch, "E959", {"start": v(-31.7, -60.14) * mm, "end": v(-35, -60.14) * mm});
            skLineSegment(sketch, "E960", {"start": v(-35, -60.14) * mm, "end": v(-35, -59.16) * mm});
            skLineSegment(sketch, "E961", {"start": v(-35, -59.16) * mm, "end": v(-36.67, -59.16) * mm});
            skLineSegment(sketch, "E962", {"start": v(-36.67, -59.16) * mm, "end": v(-36.67, -54.69) * mm});
            skLineSegment(sketch, "E963", {"start": v(-36.67, -54.69) * mm, "end": v(-76.34, -54.69) * mm});
            skLineSegment(sketch, "E964", {"start": v(-76.34, -54.69) * mm, "end": v(-76.34, -55.29) * mm});
            skLineSegment(sketch, "E965", {"start": v(-76.34, -55.29) * mm, "end": v(-75.54, -55.29) * mm});
            skLineSegment(sketch, "E966", {"start": v(-75.54, -55.29) * mm, "end": v(-75.54, -58.39) * mm});
            skLineSegment(sketch, "E967", {"start": v(-75.54, -58.39) * mm, "end": v(-76.34, -58.39) * mm});
            skLineSegment(sketch, "E968", {"start": v(-76.34, -58.39) * mm, "end": v(-76.34, -59.39) * mm});
            skLineSegment(sketch, "E969", {"start": v(-76.34, -59.39) * mm, "end": v(-90.34, -59.39) * mm});
            skLineSegment(sketch, "E970", {"start": v(-90.34, -59.39) * mm, "end": v(-90.34, -58.39) * mm});
            skLineSegment(sketch, "E971", {"start": v(-90.34, -58.39) * mm, "end": v(-91.14, -58.39) * mm});
            skLineSegment(sketch, "E972", {"start": v(-91.14, -58.39) * mm, "end": v(-91.14, -55.29) * mm});
            skLineSegment(sketch, "E973", {"start": v(-91.14, -55.29) * mm, "end": v(-90.34, -55.29) * mm});
            skLineSegment(sketch, "E974", {"start": v(-90.34, -55.29) * mm, "end": v(-90.34, -54.69) * mm});
            skLineSegment(sketch, "E975", {"start": v(-90.34, -54.69) * mm, "end": v(-130.02, -54.69) * mm});
            skLineSegment(sketch, "E976", {"start": v(-130.02, -54.69) * mm, "end": v(-130.02, -59.16) * mm});
            skLineSegment(sketch, "E977", {"start": v(-130.02, -59.16) * mm, "end": v(-131.7, -59.16) * mm});
            skLineSegment(sketch, "E978", {"start": v(-131.7, -59.16) * mm, "end": v(-131.7, -60.14) * mm});
            skLineSegment(sketch, "E979", {"start": v(-131.7, -60.14) * mm, "end": v(-135, -60.14) * mm});
            skLineSegment(sketch, "E980", {"start": v(-135, -60.14) * mm, "end": v(-135, -59.16) * mm});
            skLineSegment(sketch, "E981", {"start": v(-135, -59.16) * mm, "end": v(-136.67, -59.16) * mm});
            skLineSegment(sketch, "E982", {"start": v(-136.67, -59.16) * mm, "end": v(-136.67, -52.89) * mm});
            skLineSegment(sketch, "E983", {"start": v(-136.67, -52.89) * mm, "end": v(-137.54, -52.89) * mm});
            skLineSegment(sketch, "E984", {"start": v(-137.54, -52.89) * mm, "end": v(-137.54, -50.09) * mm});
            skLineSegment(sketch, "E985", {"start": v(-137.54, -50.09) * mm, "end": v(-136.67, -50.09) * mm});
            skLineSegment(sketch, "E986", {"start": v(-136.67, -50.09) * mm, "end": v(-136.67, -46.86) * mm});
            skLineSegment(sketch, "E987", {"start": v(-136.67, -46.86) * mm, "end": v(-135, -46.86) * mm});
            skLineSegment(sketch, "E988", {"start": v(-135, -46.86) * mm, "end": v(-135, -45.94) * mm});
            skLineSegment(sketch, "E989", {"start": v(-135, -45.94) * mm, "end": v(-131.7, -45.94) * mm});
            skLineSegment(sketch, "E990", {"start": v(-131.7, -45.94) * mm, "end": v(-131.7, -46.86) * mm});
            skLineSegment(sketch, "E991", {"start": v(-131.7, -46.86) * mm, "end": v(-130.02, -46.86) * mm});
            skLineSegment(sketch, "E992", {"start": v(-130.02, -46.86) * mm, "end": v(-130.02, -50.09) * mm});
            skLineSegment(sketch, "E993", {"start": v(-130.02, -50.09) * mm, "end": v(-90.34, -50.09) * mm});
            skLineSegment(sketch, "E994", {"start": v(-90.34, -50.09) * mm, "end": v(-90.34, -49.49) * mm});
            skLineSegment(sketch, "E995", {"start": v(-90.34, -49.49) * mm, "end": v(-91.14, -49.49) * mm});
            skLineSegment(sketch, "E996", {"start": v(-91.14, -49.49) * mm, "end": v(-91.14, -46.39) * mm});
            skLineSegment(sketch, "E997", {"start": v(-91.14, -46.39) * mm, "end": v(-90.34, -46.39) * mm});
            skLineSegment(sketch, "E998", {"start": v(-90.34, -46.39) * mm, "end": v(-90.34, -45.39) * mm});
            skLineSegment(sketch, "E999", {"start": v(-90.34, -45.39) * mm, "end": v(-76.34, -45.39) * mm});
            skLineSegment(sketch, "E1000", {"start": v(-76.34, -45.39) * mm, "end": v(-76.34, -46.39) * mm});
            skLineSegment(sketch, "E1001", {"start": v(-76.34, -46.39) * mm, "end": v(-75.54, -46.39) * mm});
            skLineSegment(sketch, "E1002", {"start": v(-75.54, -46.39) * mm, "end": v(-75.54, -49.49) * mm});
            skLineSegment(sketch, "E1003", {"start": v(-75.54, -49.49) * mm, "end": v(-76.34, -49.49) * mm});
            skLineSegment(sketch, "E1004", {"start": v(-76.34, -49.49) * mm, "end": v(-76.34, -50.09) * mm});
            skLineSegment(sketch, "E1005", {"start": v(-76.34, -50.09) * mm, "end": v(-36.67, -50.09) * mm});
            skLineSegment(sketch, "E1006", {"start": v(-36.67, -50.09) * mm, "end": v(-36.67, -46.86) * mm});
            skLineSegment(sketch, "E1007", {"start": v(-36.67, -46.86) * mm, "end": v(-35, -46.86) * mm});
            skLineSegment(sketch, "E1008", {"start": v(-35, -46.86) * mm, "end": v(-35, -45.94) * mm});
            skLineSegment(sketch, "E1009", {"start": v(-35, -45.94) * mm, "end": v(-31.7, -45.94) * mm});
            skLineSegment(sketch, "E1010", {"start": v(-31.7, -45.94) * mm, "end": v(-31.7, -46.86) * mm});
            skLineSegment(sketch, "E1011", {"start": v(-31.7, -46.86) * mm, "end": v(-30.02, -46.86) * mm});
            skLineSegment(sketch, "E1012", {"start": v(-30.02, -46.86) * mm, "end": v(-30.02, -50.09) * mm});
            skLineSegment(sketch, "E1013", {"start": v(-30.02, -50.09) * mm, "end": v(-29.14, -50.09) * mm});
            skLineSegment(sketch, "E1014", {"start": v(-29.14, -50.09) * mm, "end": v(-29.14, -52.89) * mm});
            skLineSegment(sketch, "E1015", {"start": v(-29.14, -52.89) * mm, "end": v(-30.02, -52.89) * mm});
            skLineSegment(sketch, "E1016", {"start": v(-26.34, 17.81) * mm, "end": v(-26.34, 16.81) * mm});
            skLineSegment(sketch, "E1017", {"start": v(-26.34, 16.81) * mm, "end": v(-40.34, 16.81) * mm});
            skLineSegment(sketch, "E1018", {"start": v(-40.34, 16.81) * mm, "end": v(-40.34, 17.81) * mm});
            skLineSegment(sketch, "E1019", {"start": v(-40.34, 17.81) * mm, "end": v(-41.14, 17.81) * mm});
            skLineSegment(sketch, "E1020", {"start": v(-41.14, 17.81) * mm, "end": v(-41.14, 20.91) * mm});
            skLineSegment(sketch, "E1021", {"start": v(-41.14, 20.91) * mm, "end": v(-40.34, 20.91) * mm});
            skLineSegment(sketch, "E1022", {"start": v(-40.34, 20.91) * mm, "end": v(-40.34, 26.71) * mm});
            skLineSegment(sketch, "E1023", {"start": v(-40.34, 26.71) * mm, "end": v(-41.14, 26.71) * mm});
            skLineSegment(sketch, "E1024", {"start": v(-41.14, 26.71) * mm, "end": v(-41.14, 29.81) * mm});
            skLineSegment(sketch, "E1025", {"start": v(-41.14, 29.81) * mm, "end": v(-40.34, 29.81) * mm});
            skLineSegment(sketch, "E1026", {"start": v(-40.34, 29.81) * mm, "end": v(-40.34, 30.81) * mm});
            skLineSegment(sketch, "E1027", {"start": v(-40.34, 30.81) * mm, "end": v(-26.34, 30.81) * mm});
            skLineSegment(sketch, "E1028", {"start": v(-26.34, 30.81) * mm, "end": v(-26.34, 29.81) * mm});
            skLineSegment(sketch, "E1029", {"start": v(-26.34, 29.81) * mm, "end": v(-25.54, 29.81) * mm});
            skLineSegment(sketch, "E1030", {"start": v(-25.54, 29.81) * mm, "end": v(-25.54, 26.71) * mm});
            skLineSegment(sketch, "E1031", {"start": v(-25.54, 26.71) * mm, "end": v(-26.34, 26.71) * mm});
            skLineSegment(sketch, "E1032", {"start": v(-26.34, 26.71) * mm, "end": v(-26.34, 20.91) * mm});
            skLineSegment(sketch, "E1033", {"start": v(-26.34, 20.91) * mm, "end": v(-25.54, 20.91) * mm});
            skLineSegment(sketch, "E1034", {"start": v(-25.54, 20.91) * mm, "end": v(-25.54, 17.81) * mm});
            skLineSegment(sketch, "E1035", {"start": v(-25.54, 17.81) * mm, "end": v(-26.34, 17.81) * mm});
            skLineSegment(sketch, "E1036", {"start": v(-21.57, -39.34) * mm, "end": v(-21.57, -40.34) * mm});
            skLineSegment(sketch, "E1037", {"start": v(-21.57, -40.34) * mm, "end": v(-35.57, -40.34) * mm});
            skLineSegment(sketch, "E1038", {"start": v(-35.57, -40.34) * mm, "end": v(-35.57, -39.34) * mm});
            skLineSegment(sketch, "E1039", {"start": v(-35.57, -39.34) * mm, "end": v(-36.38, -39.34) * mm});
            skLineSegment(sketch, "E1040", {"start": v(-36.38, -39.34) * mm, "end": v(-36.38, -36.24) * mm});
            skLineSegment(sketch, "E1041", {"start": v(-36.38, -36.24) * mm, "end": v(-35.57, -36.24) * mm});
            skLineSegment(sketch, "E1042", {"start": v(-35.57, -36.24) * mm, "end": v(-35.57, -30.44) * mm});
            skLineSegment(sketch, "E1043", {"start": v(-35.57, -30.44) * mm, "end": v(-36.38, -30.44) * mm});
            skLineSegment(sketch, "E1044", {"start": v(-36.38, -30.44) * mm, "end": v(-36.38, -27.34) * mm});
            skLineSegment(sketch, "E1045", {"start": v(-36.38, -27.34) * mm, "end": v(-35.57, -27.34) * mm});
            skLineSegment(sketch, "E1046", {"start": v(-35.57, -27.34) * mm, "end": v(-35.57, -26.34) * mm});
            skLineSegment(sketch, "E1047", {"start": v(-35.57, -26.34) * mm, "end": v(-21.57, -26.34) * mm});
            skLineSegment(sketch, "E1048", {"start": v(-21.57, -26.34) * mm, "end": v(-21.57, -27.34) * mm});
            skLineSegment(sketch, "E1049", {"start": v(-21.57, -27.34) * mm, "end": v(-20.77, -27.34) * mm});
            skLineSegment(sketch, "E1050", {"start": v(-20.77, -27.34) * mm, "end": v(-20.77, -30.44) * mm});
            skLineSegment(sketch, "E1051", {"start": v(-20.77, -30.44) * mm, "end": v(-21.57, -30.44) * mm});
            skLineSegment(sketch, "E1052", {"start": v(-21.57, -30.44) * mm, "end": v(-21.57, -36.24) * mm});
            skLineSegment(sketch, "E1053", {"start": v(-21.57, -36.24) * mm, "end": v(-20.77, -36.24) * mm});
            skLineSegment(sketch, "E1054", {"start": v(-20.77, -36.24) * mm, "end": v(-20.77, -39.34) * mm});
            skLineSegment(sketch, "E1055", {"start": v(-20.77, -39.34) * mm, "end": v(-21.57, -39.34) * mm});
            skLineSegment(sketch, "E1056", {"start": v(-16.81, 46.39) * mm, "end": v(-16.81, 45.39) * mm});
            skLineSegment(sketch, "E1057", {"start": v(-16.81, 45.39) * mm, "end": v(-30.81, 45.39) * mm});
            skLineSegment(sketch, "E1058", {"start": v(-30.81, 45.39) * mm, "end": v(-30.81, 46.39) * mm});
            skLineSegment(sketch, "E1059", {"start": v(-30.81, 46.39) * mm, "end": v(-31.61, 46.39) * mm});
            skLineSegment(sketch, "E1060", {"start": v(-31.61, 46.39) * mm, "end": v(-31.61, 49.49) * mm});
            skLineSegment(sketch, "E1061", {"start": v(-31.61, 49.49) * mm, "end": v(-30.81, 49.49) * mm});
            skLineSegment(sketch, "E1062", {"start": v(-30.81, 49.49) * mm, "end": v(-30.81, 55.29) * mm});
            skLineSegment(sketch, "E1063", {"start": v(-30.81, 55.29) * mm, "end": v(-31.61, 55.29) * mm});
            skLineSegment(sketch, "E1064", {"start": v(-31.61, 55.29) * mm, "end": v(-31.61, 58.39) * mm});
            skLineSegment(sketch, "E1065", {"start": v(-31.61, 58.39) * mm, "end": v(-30.81, 58.39) * mm});
            skLineSegment(sketch, "E1066", {"start": v(-30.81, 58.39) * mm, "end": v(-30.81, 59.39) * mm});
            skLineSegment(sketch, "E1067", {"start": v(-30.81, 59.39) * mm, "end": v(-16.81, 59.39) * mm});
            skLineSegment(sketch, "E1068", {"start": v(-16.81, 59.39) * mm, "end": v(-16.81, 58.39) * mm});
            skLineSegment(sketch, "E1069", {"start": v(-16.81, 58.39) * mm, "end": v(-16.01, 58.39) * mm});
            skLineSegment(sketch, "E1070", {"start": v(-16.01, 58.39) * mm, "end": v(-16.01, 55.29) * mm});
            skLineSegment(sketch, "E1071", {"start": v(-16.01, 55.29) * mm, "end": v(-16.81, 55.29) * mm});
            skLineSegment(sketch, "E1072", {"start": v(-16.81, 55.29) * mm, "end": v(-16.81, 49.49) * mm});
            skLineSegment(sketch, "E1073", {"start": v(-16.81, 49.49) * mm, "end": v(-16.01, 49.49) * mm});
            skLineSegment(sketch, "E1074", {"start": v(-16.01, 49.49) * mm, "end": v(-16.01, 46.39) * mm});
            skLineSegment(sketch, "E1075", {"start": v(-16.01, 46.39) * mm, "end": v(-16.81, 46.39) * mm});
            skLineSegment(sketch, "E1076", {"start": v(-16.81, -1.24) * mm, "end": v(-16.81, -2.24) * mm});
            skLineSegment(sketch, "E1077", {"start": v(-16.81, -2.24) * mm, "end": v(-30.81, -2.24) * mm});
            skLineSegment(sketch, "E1078", {"start": v(-30.81, -2.24) * mm, "end": v(-30.81, -1.24) * mm});
            skLineSegment(sketch, "E1079", {"start": v(-30.81, -1.24) * mm, "end": v(-31.61, -1.24) * mm});
            skLineSegment(sketch, "E1080", {"start": v(-31.61, -1.24) * mm, "end": v(-31.61, 1.86) * mm});
            skLineSegment(sketch, "E1081", {"start": v(-31.61, 1.86) * mm, "end": v(-30.81, 1.86) * mm});
            skLineSegment(sketch, "E1082", {"start": v(-30.81, 1.86) * mm, "end": v(-30.81, 7.66) * mm});
            skLineSegment(sketch, "E1083", {"start": v(-30.81, 7.66) * mm, "end": v(-31.61, 7.66) * mm});
            skLineSegment(sketch, "E1084", {"start": v(-31.61, 7.66) * mm, "end": v(-31.61, 10.76) * mm});
            skLineSegment(sketch, "E1085", {"start": v(-31.61, 10.76) * mm, "end": v(-30.81, 10.76) * mm});
            skLineSegment(sketch, "E1086", {"start": v(-30.81, 10.76) * mm, "end": v(-30.81, 11.76) * mm});
            skLineSegment(sketch, "E1087", {"start": v(-30.81, 11.76) * mm, "end": v(-16.81, 11.76) * mm});
            skLineSegment(sketch, "E1088", {"start": v(-16.81, 11.76) * mm, "end": v(-16.81, 10.76) * mm});
            skLineSegment(sketch, "E1089", {"start": v(-16.81, 10.76) * mm, "end": v(-16.01, 10.76) * mm});
            skLineSegment(sketch, "E1090", {"start": v(-16.01, 10.76) * mm, "end": v(-16.01, 7.66) * mm});
            skLineSegment(sketch, "E1091", {"start": v(-16.01, 7.66) * mm, "end": v(-16.81, 7.66) * mm});
            skLineSegment(sketch, "E1092", {"start": v(-16.81, 7.66) * mm, "end": v(-16.81, 1.86) * mm});
            skLineSegment(sketch, "E1093", {"start": v(-16.81, 1.86) * mm, "end": v(-16.01, 1.86) * mm});
            skLineSegment(sketch, "E1094", {"start": v(-16.01, 1.86) * mm, "end": v(-16.01, -1.24) * mm});
            skLineSegment(sketch, "E1095", {"start": v(-16.01, -1.24) * mm, "end": v(-16.81, -1.24) * mm});
            skLineSegment(sketch, "E1096", {"start": v(-12.05, -20.29) * mm, "end": v(-12.05, -21.29) * mm});
            skLineSegment(sketch, "E1097", {"start": v(-12.05, -21.29) * mm, "end": v(-26.05, -21.29) * mm});
            skLineSegment(sketch, "E1098", {"start": v(-26.05, -21.29) * mm, "end": v(-26.05, -20.29) * mm});
            skLineSegment(sketch, "E1099", {"start": v(-26.05, -20.29) * mm, "end": v(-26.85, -20.29) * mm});
            skLineSegment(sketch, "E1100", {"start": v(-26.85, -20.29) * mm, "end": v(-26.85, -17.19) * mm});
            skLineSegment(sketch, "E1101", {"start": v(-26.85, -17.19) * mm, "end": v(-26.05, -17.19) * mm});
            skLineSegment(sketch, "E1102", {"start": v(-26.05, -17.19) * mm, "end": v(-26.05, -11.39) * mm});
            skLineSegment(sketch, "E1103", {"start": v(-26.05, -11.39) * mm, "end": v(-26.85, -11.39) * mm});
            skLineSegment(sketch, "E1104", {"start": v(-26.85, -11.39) * mm, "end": v(-26.85, -8.29) * mm});
            skLineSegment(sketch, "E1105", {"start": v(-26.85, -8.29) * mm, "end": v(-26.05, -8.29) * mm});
            skLineSegment(sketch, "E1106", {"start": v(-26.05, -8.29) * mm, "end": v(-26.05, -7.29) * mm});
            skLineSegment(sketch, "E1107", {"start": v(-26.05, -7.29) * mm, "end": v(-12.05, -7.29) * mm});
            skLineSegment(sketch, "E1108", {"start": v(-12.05, -7.29) * mm, "end": v(-12.05, -8.29) * mm});
            skLineSegment(sketch, "E1109", {"start": v(-12.05, -8.29) * mm, "end": v(-11.25, -8.29) * mm});
            skLineSegment(sketch, "E1110", {"start": v(-11.25, -8.29) * mm, "end": v(-11.25, -11.39) * mm});
            skLineSegment(sketch, "E1111", {"start": v(-11.25, -11.39) * mm, "end": v(-12.05, -11.39) * mm});
            skLineSegment(sketch, "E1112", {"start": v(-12.05, -11.39) * mm, "end": v(-12.05, -17.19) * mm});
            skLineSegment(sketch, "E1113", {"start": v(-12.05, -17.19) * mm, "end": v(-11.25, -17.19) * mm});
            skLineSegment(sketch, "E1114", {"start": v(-11.25, -17.19) * mm, "end": v(-11.25, -20.29) * mm});
            skLineSegment(sketch, "E1115", {"start": v(-11.25, -20.29) * mm, "end": v(-12.05, -20.29) * mm});
            skLineSegment(sketch, "E1116", {"start": v(-7.29, 17.81) * mm, "end": v(-7.29, 16.81) * mm});
            skLineSegment(sketch, "E1117", {"start": v(-7.29, 16.81) * mm, "end": v(-21.29, 16.81) * mm});
            skLineSegment(sketch, "E1118", {"start": v(-21.29, 16.81) * mm, "end": v(-21.29, 17.81) * mm});
            skLineSegment(sketch, "E1119", {"start": v(-21.29, 17.81) * mm, "end": v(-22.09, 17.81) * mm});
            skLineSegment(sketch, "E1120", {"start": v(-22.09, 17.81) * mm, "end": v(-22.09, 20.91) * mm});
            skLineSegment(sketch, "E1121", {"start": v(-22.09, 20.91) * mm, "end": v(-21.29, 20.91) * mm});
            skLineSegment(sketch, "E1122", {"start": v(-21.29, 20.91) * mm, "end": v(-21.29, 26.71) * mm});
            skLineSegment(sketch, "E1123", {"start": v(-21.29, 26.71) * mm, "end": v(-22.09, 26.71) * mm});
            skLineSegment(sketch, "E1124", {"start": v(-22.09, 26.71) * mm, "end": v(-22.09, 29.81) * mm});
            skLineSegment(sketch, "E1125", {"start": v(-22.09, 29.81) * mm, "end": v(-21.29, 29.81) * mm});
            skLineSegment(sketch, "E1126", {"start": v(-21.29, 29.81) * mm, "end": v(-21.29, 30.81) * mm});
            skLineSegment(sketch, "E1127", {"start": v(-21.29, 30.81) * mm, "end": v(-7.29, 30.81) * mm});
            skLineSegment(sketch, "E1128", {"start": v(-7.29, 30.81) * mm, "end": v(-7.29, 29.81) * mm});
            skLineSegment(sketch, "E1129", {"start": v(-7.29, 29.81) * mm, "end": v(-6.49, 29.81) * mm});
            skLineSegment(sketch, "E1130", {"start": v(-6.49, 29.81) * mm, "end": v(-6.49, 26.71) * mm});
            skLineSegment(sketch, "E1131", {"start": v(-6.49, 26.71) * mm, "end": v(-7.29, 26.71) * mm});
            skLineSegment(sketch, "E1132", {"start": v(-7.29, 26.71) * mm, "end": v(-7.29, 20.91) * mm});
            skLineSegment(sketch, "E1133", {"start": v(-7.29, 20.91) * mm, "end": v(-6.49, 20.91) * mm});
            skLineSegment(sketch, "E1134", {"start": v(-6.49, 20.91) * mm, "end": v(-6.49, 17.81) * mm});
            skLineSegment(sketch, "E1135", {"start": v(-6.49, 17.81) * mm, "end": v(-7.29, 17.81) * mm});
            skLineSegment(sketch, "E1136", {"start": v(-4.9, -58.39) * mm, "end": v(-4.9, -59.39) * mm});
            skLineSegment(sketch, "E1137", {"start": v(-4.9, -59.39) * mm, "end": v(-18.9, -59.39) * mm});
            skLineSegment(sketch, "E1138", {"start": v(-18.9, -59.39) * mm, "end": v(-18.9, -58.39) * mm});
            skLineSegment(sketch, "E1139", {"start": v(-18.9, -58.39) * mm, "end": v(-19.7, -58.39) * mm});
            skLineSegment(sketch, "E1140", {"start": v(-19.7, -58.39) * mm, "end": v(-19.7, -55.29) * mm});
            skLineSegment(sketch, "E1141", {"start": v(-19.7, -55.29) * mm, "end": v(-18.9, -55.29) * mm});
            skLineSegment(sketch, "E1142", {"start": v(-18.9, -55.29) * mm, "end": v(-18.9, -49.49) * mm});
            skLineSegment(sketch, "E1143", {"start": v(-18.9, -49.49) * mm, "end": v(-19.7, -49.49) * mm});
            skLineSegment(sketch, "E1144", {"start": v(-19.7, -49.49) * mm, "end": v(-19.7, -46.39) * mm});
            skLineSegment(sketch, "E1145", {"start": v(-19.7, -46.39) * mm, "end": v(-18.9, -46.39) * mm});
            skLineSegment(sketch, "E1146", {"start": v(-18.9, -46.39) * mm, "end": v(-18.9, -45.39) * mm});
            skLineSegment(sketch, "E1147", {"start": v(-18.9, -45.39) * mm, "end": v(-4.9, -45.39) * mm});
            skLineSegment(sketch, "E1148", {"start": v(-4.9, -45.39) * mm, "end": v(-4.9, -46.39) * mm});
            skLineSegment(sketch, "E1149", {"start": v(-4.9, -46.39) * mm, "end": v(-4.1, -46.39) * mm});
            skLineSegment(sketch, "E1150", {"start": v(-4.1, -46.39) * mm, "end": v(-4.1, -49.49) * mm});
            skLineSegment(sketch, "E1151", {"start": v(-4.1, -49.49) * mm, "end": v(-4.9, -49.49) * mm});
            skLineSegment(sketch, "E1152", {"start": v(-4.9, -49.49) * mm, "end": v(-4.9, -55.29) * mm});
            skLineSegment(sketch, "E1153", {"start": v(-4.9, -55.29) * mm, "end": v(-4.1, -55.29) * mm});
            skLineSegment(sketch, "E1154", {"start": v(-4.1, -55.29) * mm, "end": v(-4.1, -58.39) * mm});
            skLineSegment(sketch, "E1155", {"start": v(-4.1, -58.39) * mm, "end": v(-4.9, -58.39) * mm});
            skLineSegment(sketch, "E1156", {"start": v(-2.52, -39.34) * mm, "end": v(-2.52, -40.34) * mm});
            skLineSegment(sketch, "E1157", {"start": v(-2.52, -40.34) * mm, "end": v(-16.52, -40.34) * mm});
            skLineSegment(sketch, "E1158", {"start": v(-16.52, -40.34) * mm, "end": v(-16.52, -39.34) * mm});
            skLineSegment(sketch, "E1159", {"start": v(-16.52, -39.34) * mm, "end": v(-17.33, -39.34) * mm});
            skLineSegment(sketch, "E1160", {"start": v(-17.33, -39.34) * mm, "end": v(-17.33, -36.24) * mm});
            skLineSegment(sketch, "E1161", {"start": v(-17.33, -36.24) * mm, "end": v(-16.52, -36.24) * mm});
            skLineSegment(sketch, "E1162", {"start": v(-16.52, -36.24) * mm, "end": v(-16.52, -30.44) * mm});
            skLineSegment(sketch, "E1163", {"start": v(-16.52, -30.44) * mm, "end": v(-17.33, -30.44) * mm});
            skLineSegment(sketch, "E1164", {"start": v(-17.33, -30.44) * mm, "end": v(-17.33, -27.34) * mm});
            skLineSegment(sketch, "E1165", {"start": v(-17.33, -27.34) * mm, "end": v(-16.52, -27.34) * mm});
            skLineSegment(sketch, "E1166", {"start": v(-16.52, -27.34) * mm, "end": v(-16.52, -26.34) * mm});
            skLineSegment(sketch, "E1167", {"start": v(-16.52, -26.34) * mm, "end": v(-2.52, -26.34) * mm});
            skLineSegment(sketch, "E1168", {"start": v(-2.52, -26.34) * mm, "end": v(-2.52, -27.34) * mm});
            skLineSegment(sketch, "E1169", {"start": v(-2.52, -27.34) * mm, "end": v(-1.72, -27.34) * mm});
            skLineSegment(sketch, "E1170", {"start": v(-1.72, -27.34) * mm, "end": v(-1.72, -30.44) * mm});
            skLineSegment(sketch, "E1171", {"start": v(-1.72, -30.44) * mm, "end": v(-2.52, -30.44) * mm});
            skLineSegment(sketch, "E1172", {"start": v(-2.52, -30.44) * mm, "end": v(-2.52, -36.24) * mm});
            skLineSegment(sketch, "E1173", {"start": v(-2.52, -36.24) * mm, "end": v(-1.72, -36.24) * mm});
            skLineSegment(sketch, "E1174", {"start": v(-1.72, -36.24) * mm, "end": v(-1.72, -39.34) * mm});
            skLineSegment(sketch, "E1175", {"start": v(-1.72, -39.34) * mm, "end": v(-2.52, -39.34) * mm});
            skLineSegment(sketch, "E1176", {"start": v(2.24, -1.24) * mm, "end": v(2.24, -2.24) * mm});
            skLineSegment(sketch, "E1177", {"start": v(2.24, -2.24) * mm, "end": v(-11.76, -2.24) * mm});
            skLineSegment(sketch, "E1178", {"start": v(-11.76, -2.24) * mm, "end": v(-11.76, -1.24) * mm});
            skLineSegment(sketch, "E1179", {"start": v(-11.76, -1.24) * mm, "end": v(-12.56, -1.24) * mm});
            skLineSegment(sketch, "E1180", {"start": v(-12.56, -1.24) * mm, "end": v(-12.56, 1.86) * mm});
            skLineSegment(sketch, "E1181", {"start": v(-12.56, 1.86) * mm, "end": v(-11.76, 1.86) * mm});
            skLineSegment(sketch, "E1182", {"start": v(-11.76, 1.86) * mm, "end": v(-11.76, 7.66) * mm});
            skLineSegment(sketch, "E1183", {"start": v(-11.76, 7.66) * mm, "end": v(-12.56, 7.66) * mm});
            skLineSegment(sketch, "E1184", {"start": v(-12.56, 7.66) * mm, "end": v(-12.56, 10.76) * mm});
            skLineSegment(sketch, "E1185", {"start": v(-12.56, 10.76) * mm, "end": v(-11.76, 10.76) * mm});
            skLineSegment(sketch, "E1186", {"start": v(-11.76, 10.76) * mm, "end": v(-11.76, 11.76) * mm});
            skLineSegment(sketch, "E1187", {"start": v(-11.76, 11.76) * mm, "end": v(2.24, 11.76) * mm});
            skLineSegment(sketch, "E1188", {"start": v(2.24, 11.76) * mm, "end": v(2.24, 10.76) * mm});
            skLineSegment(sketch, "E1189", {"start": v(2.24, 10.76) * mm, "end": v(3.04, 10.76) * mm});
            skLineSegment(sketch, "E1190", {"start": v(3.04, 10.76) * mm, "end": v(3.04, 7.66) * mm});
            skLineSegment(sketch, "E1191", {"start": v(3.04, 7.66) * mm, "end": v(2.24, 7.66) * mm});
            skLineSegment(sketch, "E1192", {"start": v(2.24, 7.66) * mm, "end": v(2.24, 1.86) * mm});
            skLineSegment(sketch, "E1193", {"start": v(2.24, 1.86) * mm, "end": v(3.04, 1.86) * mm});
            skLineSegment(sketch, "E1194", {"start": v(3.04, 1.86) * mm, "end": v(3.04, -1.24) * mm});
            skLineSegment(sketch, "E1195", {"start": v(3.04, -1.24) * mm, "end": v(2.24, -1.24) * mm});
            skLineSegment(sketch, "E1196", {"start": v(7, -20.29) * mm, "end": v(7, -21.29) * mm});
            skLineSegment(sketch, "E1197", {"start": v(7, -21.29) * mm, "end": v(-7, -21.29) * mm});
            skLineSegment(sketch, "E1198", {"start": v(-7, -21.29) * mm, "end": v(-7, -20.29) * mm});
            skLineSegment(sketch, "E1199", {"start": v(-7, -20.29) * mm, "end": v(-7.8, -20.29) * mm});
            skLineSegment(sketch, "E1200", {"start": v(-7.8, -20.29) * mm, "end": v(-7.8, -17.19) * mm});
            skLineSegment(sketch, "E1201", {"start": v(-7.8, -17.19) * mm, "end": v(-7, -17.19) * mm});
            skLineSegment(sketch, "E1202", {"start": v(-7, -17.19) * mm, "end": v(-7, -11.39) * mm});
            skLineSegment(sketch, "E1203", {"start": v(-7, -11.39) * mm, "end": v(-7.8, -11.39) * mm});
            skLineSegment(sketch, "E1204", {"start": v(-7.8, -11.39) * mm, "end": v(-7.8, -8.29) * mm});
            skLineSegment(sketch, "E1205", {"start": v(-7.8, -8.29) * mm, "end": v(-7, -8.29) * mm});
            skLineSegment(sketch, "E1206", {"start": v(-7, -8.29) * mm, "end": v(-7, -7.29) * mm});
            skLineSegment(sketch, "E1207", {"start": v(-7, -7.29) * mm, "end": v(7, -7.29) * mm});
            skLineSegment(sketch, "E1208", {"start": v(7, -7.29) * mm, "end": v(7, -8.29) * mm});
            skLineSegment(sketch, "E1209", {"start": v(7, -8.29) * mm, "end": v(7.8, -8.29) * mm});
            skLineSegment(sketch, "E1210", {"start": v(7.8, -8.29) * mm, "end": v(7.8, -11.39) * mm});
            skLineSegment(sketch, "E1211", {"start": v(7.8, -11.39) * mm, "end": v(7, -11.39) * mm});
            skLineSegment(sketch, "E1212", {"start": v(7, -11.39) * mm, "end": v(7, -17.19) * mm});
            skLineSegment(sketch, "E1213", {"start": v(7, -17.19) * mm, "end": v(7.8, -17.19) * mm});
            skLineSegment(sketch, "E1214", {"start": v(7.8, -17.19) * mm, "end": v(7.8, -20.29) * mm});
            skLineSegment(sketch, "E1215", {"start": v(7.8, -20.29) * mm, "end": v(7, -20.29) * mm});
            skLineSegment(sketch, "E1216", {"start": v(11.76, 46.39) * mm, "end": v(11.76, 45.39) * mm});
            skLineSegment(sketch, "E1217", {"start": v(11.76, 45.39) * mm, "end": v(-2.24, 45.39) * mm});
            skLineSegment(sketch, "E1218", {"start": v(-2.24, 45.39) * mm, "end": v(-2.24, 46.39) * mm});
            skLineSegment(sketch, "E1219", {"start": v(-2.24, 46.39) * mm, "end": v(-3.04, 46.39) * mm});
            skLineSegment(sketch, "E1220", {"start": v(-3.04, 46.39) * mm, "end": v(-3.04, 49.49) * mm});
            skLineSegment(sketch, "E1221", {"start": v(-3.04, 49.49) * mm, "end": v(-2.24, 49.49) * mm});
            skLineSegment(sketch, "E1222", {"start": v(-2.24, 49.49) * mm, "end": v(-2.24, 55.29) * mm});
            skLineSegment(sketch, "E1223", {"start": v(-2.24, 55.29) * mm, "end": v(-3.04, 55.29) * mm});
            skLineSegment(sketch, "E1224", {"start": v(-3.04, 55.29) * mm, "end": v(-3.04, 58.39) * mm});
            skLineSegment(sketch, "E1225", {"start": v(-3.04, 58.39) * mm, "end": v(-2.24, 58.39) * mm});
            skLineSegment(sketch, "E1226", {"start": v(-2.24, 58.39) * mm, "end": v(-2.24, 59.39) * mm});
            skLineSegment(sketch, "E1227", {"start": v(-2.24, 59.39) * mm, "end": v(11.76, 59.39) * mm});
            skLineSegment(sketch, "E1228", {"start": v(11.76, 59.39) * mm, "end": v(11.76, 58.39) * mm});
            skLineSegment(sketch, "E1229", {"start": v(11.76, 58.39) * mm, "end": v(12.56, 58.39) * mm});
            skLineSegment(sketch, "E1230", {"start": v(12.56, 58.39) * mm, "end": v(12.56, 55.29) * mm});
            skLineSegment(sketch, "E1231", {"start": v(12.56, 55.29) * mm, "end": v(11.76, 55.29) * mm});
            skLineSegment(sketch, "E1232", {"start": v(11.76, 55.29) * mm, "end": v(11.76, 49.49) * mm});
            skLineSegment(sketch, "E1233", {"start": v(11.76, 49.49) * mm, "end": v(12.56, 49.49) * mm});
            skLineSegment(sketch, "E1234", {"start": v(12.56, 49.49) * mm, "end": v(12.56, 46.39) * mm});
            skLineSegment(sketch, "E1235", {"start": v(12.56, 46.39) * mm, "end": v(11.76, 46.39) * mm});
            skLineSegment(sketch, "E1236", {"start": v(11.76, 17.81) * mm, "end": v(11.76, 16.81) * mm});
            skLineSegment(sketch, "E1237", {"start": v(11.76, 16.81) * mm, "end": v(-2.24, 16.81) * mm});
            skLineSegment(sketch, "E1238", {"start": v(-2.24, 16.81) * mm, "end": v(-2.24, 17.81) * mm});
            skLineSegment(sketch, "E1239", {"start": v(-2.24, 17.81) * mm, "end": v(-3.04, 17.81) * mm});
            skLineSegment(sketch, "E1240", {"start": v(-3.04, 17.81) * mm, "end": v(-3.04, 20.91) * mm});
            skLineSegment(sketch, "E1241", {"start": v(-3.04, 20.91) * mm, "end": v(-2.24, 20.91) * mm});
            skLineSegment(sketch, "E1242", {"start": v(-2.24, 20.91) * mm, "end": v(-2.24, 26.71) * mm});
            skLineSegment(sketch, "E1243", {"start": v(-2.24, 26.71) * mm, "end": v(-3.04, 26.71) * mm});
            skLineSegment(sketch, "E1244", {"start": v(-3.04, 26.71) * mm, "end": v(-3.04, 29.81) * mm});
            skLineSegment(sketch, "E1245", {"start": v(-3.04, 29.81) * mm, "end": v(-2.24, 29.81) * mm});
            skLineSegment(sketch, "E1246", {"start": v(-2.24, 29.81) * mm, "end": v(-2.24, 30.81) * mm});
            skLineSegment(sketch, "E1247", {"start": v(-2.24, 30.81) * mm, "end": v(11.76, 30.81) * mm});
            skLineSegment(sketch, "E1248", {"start": v(11.76, 30.81) * mm, "end": v(11.76, 29.81) * mm});
            skLineSegment(sketch, "E1249", {"start": v(11.76, 29.81) * mm, "end": v(12.56, 29.81) * mm});
            skLineSegment(sketch, "E1250", {"start": v(12.56, 29.81) * mm, "end": v(12.56, 26.71) * mm});
            skLineSegment(sketch, "E1251", {"start": v(12.56, 26.71) * mm, "end": v(11.76, 26.71) * mm});
            skLineSegment(sketch, "E1252", {"start": v(11.76, 26.71) * mm, "end": v(11.76, 20.91) * mm});
            skLineSegment(sketch, "E1253", {"start": v(11.76, 20.91) * mm, "end": v(12.56, 20.91) * mm});
            skLineSegment(sketch, "E1254", {"start": v(12.56, 20.91) * mm, "end": v(12.56, 17.81) * mm});
            skLineSegment(sketch, "E1255", {"start": v(12.56, 17.81) * mm, "end": v(11.76, 17.81) * mm});
            skLineSegment(sketch, "E1256", {"start": v(16.53, -39.34) * mm, "end": v(16.53, -40.34) * mm});
            skLineSegment(sketch, "E1257", {"start": v(16.53, -40.34) * mm, "end": v(2.53, -40.34) * mm});
            skLineSegment(sketch, "E1258", {"start": v(2.53, -40.34) * mm, "end": v(2.53, -39.34) * mm});
            skLineSegment(sketch, "E1259", {"start": v(2.53, -39.34) * mm, "end": v(1.72, -39.34) * mm});
            skLineSegment(sketch, "E1260", {"start": v(1.72, -39.34) * mm, "end": v(1.72, -36.24) * mm});
            skLineSegment(sketch, "E1261", {"start": v(1.72, -36.24) * mm, "end": v(2.53, -36.24) * mm});
            skLineSegment(sketch, "E1262", {"start": v(2.53, -36.24) * mm, "end": v(2.53, -30.44) * mm});
            skLineSegment(sketch, "E1263", {"start": v(2.53, -30.44) * mm, "end": v(1.72, -30.44) * mm});
            skLineSegment(sketch, "E1264", {"start": v(1.72, -30.44) * mm, "end": v(1.72, -27.34) * mm});
            skLineSegment(sketch, "E1265", {"start": v(1.72, -27.34) * mm, "end": v(2.53, -27.34) * mm});
            skLineSegment(sketch, "E1266", {"start": v(2.53, -27.34) * mm, "end": v(2.53, -26.34) * mm});
            skLineSegment(sketch, "E1267", {"start": v(2.53, -26.34) * mm, "end": v(16.53, -26.34) * mm});
            skLineSegment(sketch, "E1268", {"start": v(16.53, -26.34) * mm, "end": v(16.53, -27.34) * mm});
            skLineSegment(sketch, "E1269", {"start": v(16.53, -27.34) * mm, "end": v(17.33, -27.34) * mm});
            skLineSegment(sketch, "E1270", {"start": v(17.33, -27.34) * mm, "end": v(17.33, -30.44) * mm});
            skLineSegment(sketch, "E1271", {"start": v(17.33, -30.44) * mm, "end": v(16.53, -30.44) * mm});
            skLineSegment(sketch, "E1272", {"start": v(16.53, -30.44) * mm, "end": v(16.53, -36.24) * mm});
            skLineSegment(sketch, "E1273", {"start": v(16.53, -36.24) * mm, "end": v(17.33, -36.24) * mm});
            skLineSegment(sketch, "E1274", {"start": v(17.33, -36.24) * mm, "end": v(17.33, -39.34) * mm});
            skLineSegment(sketch, "E1275", {"start": v(17.33, -39.34) * mm, "end": v(16.53, -39.34) * mm});
            skLineSegment(sketch, "E1276", {"start": v(18.9, -58.39) * mm, "end": v(18.9, -59.39) * mm});
            skLineSegment(sketch, "E1277", {"start": v(18.9, -59.39) * mm, "end": v(4.9, -59.39) * mm});
            skLineSegment(sketch, "E1278", {"start": v(4.9, -59.39) * mm, "end": v(4.9, -58.39) * mm});
            skLineSegment(sketch, "E1279", {"start": v(4.9, -58.39) * mm, "end": v(4.1, -58.39) * mm});
            skLineSegment(sketch, "E1280", {"start": v(4.1, -58.39) * mm, "end": v(4.1, -55.29) * mm});
            skLineSegment(sketch, "E1281", {"start": v(4.1, -55.29) * mm, "end": v(4.9, -55.29) * mm});
            skLineSegment(sketch, "E1282", {"start": v(4.9, -55.29) * mm, "end": v(4.9, -49.49) * mm});
            skLineSegment(sketch, "E1283", {"start": v(4.9, -49.49) * mm, "end": v(4.1, -49.49) * mm});
            skLineSegment(sketch, "E1284", {"start": v(4.1, -49.49) * mm, "end": v(4.1, -46.39) * mm});
            skLineSegment(sketch, "E1285", {"start": v(4.1, -46.39) * mm, "end": v(4.9, -46.39) * mm});
            skLineSegment(sketch, "E1286", {"start": v(4.9, -46.39) * mm, "end": v(4.9, -45.39) * mm});
            skLineSegment(sketch, "E1287", {"start": v(4.9, -45.39) * mm, "end": v(18.9, -45.39) * mm});
            skLineSegment(sketch, "E1288", {"start": v(18.9, -45.39) * mm, "end": v(18.9, -46.39) * mm});
            skLineSegment(sketch, "E1289", {"start": v(18.9, -46.39) * mm, "end": v(19.7, -46.39) * mm});
            skLineSegment(sketch, "E1290", {"start": v(19.7, -46.39) * mm, "end": v(19.7, -49.49) * mm});
            skLineSegment(sketch, "E1291", {"start": v(19.7, -49.49) * mm, "end": v(18.9, -49.49) * mm});
            skLineSegment(sketch, "E1292", {"start": v(18.9, -49.49) * mm, "end": v(18.9, -55.29) * mm});
            skLineSegment(sketch, "E1293", {"start": v(18.9, -55.29) * mm, "end": v(19.7, -55.29) * mm});
            skLineSegment(sketch, "E1294", {"start": v(19.7, -55.29) * mm, "end": v(19.7, -58.39) * mm});
            skLineSegment(sketch, "E1295", {"start": v(19.7, -58.39) * mm, "end": v(18.9, -58.39) * mm});
            skLineSegment(sketch, "E1296", {"start": v(21.29, -1.24) * mm, "end": v(21.29, -2.24) * mm});
            skLineSegment(sketch, "E1297", {"start": v(21.29, -2.24) * mm, "end": v(7.29, -2.24) * mm});
            skLineSegment(sketch, "E1298", {"start": v(7.29, -2.24) * mm, "end": v(7.29, -1.24) * mm});
            skLineSegment(sketch, "E1299", {"start": v(7.29, -1.24) * mm, "end": v(6.49, -1.24) * mm});
            skLineSegment(sketch, "E1300", {"start": v(6.49, -1.24) * mm, "end": v(6.49, 1.86) * mm});
            skLineSegment(sketch, "E1301", {"start": v(6.49, 1.86) * mm, "end": v(7.29, 1.86) * mm});
            skLineSegment(sketch, "E1302", {"start": v(7.29, 1.86) * mm, "end": v(7.29, 7.66) * mm});
            skLineSegment(sketch, "E1303", {"start": v(7.29, 7.66) * mm, "end": v(6.49, 7.66) * mm});
            skLineSegment(sketch, "E1304", {"start": v(6.49, 7.66) * mm, "end": v(6.49, 10.76) * mm});
            skLineSegment(sketch, "E1305", {"start": v(6.49, 10.76) * mm, "end": v(7.29, 10.76) * mm});
            skLineSegment(sketch, "E1306", {"start": v(7.29, 10.76) * mm, "end": v(7.29, 11.76) * mm});
            skLineSegment(sketch, "E1307", {"start": v(7.29, 11.76) * mm, "end": v(21.29, 11.76) * mm});
            skLineSegment(sketch, "E1308", {"start": v(21.29, 11.76) * mm, "end": v(21.29, 10.76) * mm});
            skLineSegment(sketch, "E1309", {"start": v(21.29, 10.76) * mm, "end": v(22.09, 10.76) * mm});
            skLineSegment(sketch, "E1310", {"start": v(22.09, 10.76) * mm, "end": v(22.09, 7.66) * mm});
            skLineSegment(sketch, "E1311", {"start": v(22.09, 7.66) * mm, "end": v(21.29, 7.66) * mm});
            skLineSegment(sketch, "E1312", {"start": v(21.29, 7.66) * mm, "end": v(21.29, 1.86) * mm});
            skLineSegment(sketch, "E1313", {"start": v(21.29, 1.86) * mm, "end": v(22.09, 1.86) * mm});
            skLineSegment(sketch, "E1314", {"start": v(22.09, 1.86) * mm, "end": v(22.09, -1.24) * mm});
            skLineSegment(sketch, "E1315", {"start": v(22.09, -1.24) * mm, "end": v(21.29, -1.24) * mm});
            skLineSegment(sketch, "E1316", {"start": v(26.05, -20.29) * mm, "end": v(26.05, -21.29) * mm});
            skLineSegment(sketch, "E1317", {"start": v(26.05, -21.29) * mm, "end": v(12.05, -21.29) * mm});
            skLineSegment(sketch, "E1318", {"start": v(12.05, -21.29) * mm, "end": v(12.05, -20.29) * mm});
            skLineSegment(sketch, "E1319", {"start": v(12.05, -20.29) * mm, "end": v(11.25, -20.29) * mm});
            skLineSegment(sketch, "E1320", {"start": v(11.25, -20.29) * mm, "end": v(11.25, -17.19) * mm});
            skLineSegment(sketch, "E1321", {"start": v(11.25, -17.19) * mm, "end": v(12.05, -17.19) * mm});
            skLineSegment(sketch, "E1322", {"start": v(12.05, -17.19) * mm, "end": v(12.05, -11.39) * mm});
            skLineSegment(sketch, "E1323", {"start": v(12.05, -11.39) * mm, "end": v(11.25, -11.39) * mm});
            skLineSegment(sketch, "E1324", {"start": v(11.25, -11.39) * mm, "end": v(11.25, -8.29) * mm});
            skLineSegment(sketch, "E1325", {"start": v(11.25, -8.29) * mm, "end": v(12.05, -8.29) * mm});
            skLineSegment(sketch, "E1326", {"start": v(12.05, -8.29) * mm, "end": v(12.05, -7.29) * mm});
            skLineSegment(sketch, "E1327", {"start": v(12.05, -7.29) * mm, "end": v(26.05, -7.29) * mm});
            skLineSegment(sketch, "E1328", {"start": v(26.05, -7.29) * mm, "end": v(26.05, -8.29) * mm});
            skLineSegment(sketch, "E1329", {"start": v(26.05, -8.29) * mm, "end": v(26.85, -8.29) * mm});
            skLineSegment(sketch, "E1330", {"start": v(26.85, -8.29) * mm, "end": v(26.85, -11.39) * mm});
            skLineSegment(sketch, "E1331", {"start": v(26.85, -11.39) * mm, "end": v(26.05, -11.39) * mm});
            skLineSegment(sketch, "E1332", {"start": v(26.05, -11.39) * mm, "end": v(26.05, -17.19) * mm});
            skLineSegment(sketch, "E1333", {"start": v(26.05, -17.19) * mm, "end": v(26.85, -17.19) * mm});
            skLineSegment(sketch, "E1334", {"start": v(26.85, -17.19) * mm, "end": v(26.85, -20.29) * mm});
            skLineSegment(sketch, "E1335", {"start": v(26.85, -20.29) * mm, "end": v(26.05, -20.29) * mm});
            skLineSegment(sketch, "E1336", {"start": v(30.81, 46.39) * mm, "end": v(30.81, 45.39) * mm});
            skLineSegment(sketch, "E1337", {"start": v(30.81, 45.39) * mm, "end": v(16.81, 45.39) * mm});
            skLineSegment(sketch, "E1338", {"start": v(16.81, 45.39) * mm, "end": v(16.81, 46.39) * mm});
            skLineSegment(sketch, "E1339", {"start": v(16.81, 46.39) * mm, "end": v(16.01, 46.39) * mm});
            skLineSegment(sketch, "E1340", {"start": v(16.01, 46.39) * mm, "end": v(16.01, 49.49) * mm});
            skLineSegment(sketch, "E1341", {"start": v(16.01, 49.49) * mm, "end": v(16.81, 49.49) * mm});
            skLineSegment(sketch, "E1342", {"start": v(16.81, 49.49) * mm, "end": v(16.81, 55.29) * mm});
            skLineSegment(sketch, "E1343", {"start": v(16.81, 55.29) * mm, "end": v(16.01, 55.29) * mm});
            skLineSegment(sketch, "E1344", {"start": v(16.01, 55.29) * mm, "end": v(16.01, 58.39) * mm});
            skLineSegment(sketch, "E1345", {"start": v(16.01, 58.39) * mm, "end": v(16.81, 58.39) * mm});
            skLineSegment(sketch, "E1346", {"start": v(16.81, 58.39) * mm, "end": v(16.81, 59.39) * mm});
            skLineSegment(sketch, "E1347", {"start": v(16.81, 59.39) * mm, "end": v(30.81, 59.39) * mm});
            skLineSegment(sketch, "E1348", {"start": v(30.81, 59.39) * mm, "end": v(30.81, 58.39) * mm});
            skLineSegment(sketch, "E1349", {"start": v(30.81, 58.39) * mm, "end": v(31.61, 58.39) * mm});
            skLineSegment(sketch, "E1350", {"start": v(31.61, 58.39) * mm, "end": v(31.61, 55.29) * mm});
            skLineSegment(sketch, "E1351", {"start": v(31.61, 55.29) * mm, "end": v(30.81, 55.29) * mm});
            skLineSegment(sketch, "E1352", {"start": v(30.81, 55.29) * mm, "end": v(30.81, 49.49) * mm});
            skLineSegment(sketch, "E1353", {"start": v(30.81, 49.49) * mm, "end": v(31.61, 49.49) * mm});
            skLineSegment(sketch, "E1354", {"start": v(31.61, 49.49) * mm, "end": v(31.61, 46.39) * mm});
            skLineSegment(sketch, "E1355", {"start": v(31.61, 46.39) * mm, "end": v(30.81, 46.39) * mm});
            skLineSegment(sketch, "E1356", {"start": v(30.81, 17.81) * mm, "end": v(30.81, 16.81) * mm});
            skLineSegment(sketch, "E1357", {"start": v(30.81, 16.81) * mm, "end": v(16.81, 16.81) * mm});
            skLineSegment(sketch, "E1358", {"start": v(16.81, 16.81) * mm, "end": v(16.81, 17.81) * mm});
            skLineSegment(sketch, "E1359", {"start": v(16.81, 17.81) * mm, "end": v(16.01, 17.81) * mm});
            skLineSegment(sketch, "E1360", {"start": v(16.01, 17.81) * mm, "end": v(16.01, 20.91) * mm});
            skLineSegment(sketch, "E1361", {"start": v(16.01, 20.91) * mm, "end": v(16.81, 20.91) * mm});
            skLineSegment(sketch, "E1362", {"start": v(16.81, 20.91) * mm, "end": v(16.81, 26.71) * mm});
            skLineSegment(sketch, "E1363", {"start": v(16.81, 26.71) * mm, "end": v(16.01, 26.71) * mm});
            skLineSegment(sketch, "E1364", {"start": v(16.01, 26.71) * mm, "end": v(16.01, 29.81) * mm});
            skLineSegment(sketch, "E1365", {"start": v(16.01, 29.81) * mm, "end": v(16.81, 29.81) * mm});
            skLineSegment(sketch, "E1366", {"start": v(16.81, 29.81) * mm, "end": v(16.81, 30.81) * mm});
            skLineSegment(sketch, "E1367", {"start": v(16.81, 30.81) * mm, "end": v(30.81, 30.81) * mm});
            skLineSegment(sketch, "E1368", {"start": v(30.81, 30.81) * mm, "end": v(30.81, 29.81) * mm});
            skLineSegment(sketch, "E1369", {"start": v(30.81, 29.81) * mm, "end": v(31.61, 29.81) * mm});
            skLineSegment(sketch, "E1370", {"start": v(31.61, 29.81) * mm, "end": v(31.61, 26.71) * mm});
            skLineSegment(sketch, "E1371", {"start": v(31.61, 26.71) * mm, "end": v(30.81, 26.71) * mm});
            skLineSegment(sketch, "E1372", {"start": v(30.81, 26.71) * mm, "end": v(30.81, 20.91) * mm});
            skLineSegment(sketch, "E1373", {"start": v(30.81, 20.91) * mm, "end": v(31.61, 20.91) * mm});
            skLineSegment(sketch, "E1374", {"start": v(31.61, 20.91) * mm, "end": v(31.61, 17.81) * mm});
            skLineSegment(sketch, "E1375", {"start": v(31.61, 17.81) * mm, "end": v(30.81, 17.81) * mm});
            skLineSegment(sketch, "E1376", {"start": v(40.34, -1.24) * mm, "end": v(40.34, -2.24) * mm});
            skLineSegment(sketch, "E1377", {"start": v(40.34, -2.24) * mm, "end": v(26.34, -2.24) * mm});
            skLineSegment(sketch, "E1378", {"start": v(26.34, -2.24) * mm, "end": v(26.34, -1.24) * mm});
            skLineSegment(sketch, "E1379", {"start": v(26.34, -1.24) * mm, "end": v(25.54, -1.24) * mm});
            skLineSegment(sketch, "E1380", {"start": v(25.54, -1.24) * mm, "end": v(25.54, 1.86) * mm});
            skLineSegment(sketch, "E1381", {"start": v(25.54, 1.86) * mm, "end": v(26.34, 1.86) * mm});
            skLineSegment(sketch, "E1382", {"start": v(26.34, 1.86) * mm, "end": v(26.34, 7.66) * mm});
            skLineSegment(sketch, "E1383", {"start": v(26.34, 7.66) * mm, "end": v(25.54, 7.66) * mm});
            skLineSegment(sketch, "E1384", {"start": v(25.54, 7.66) * mm, "end": v(25.54, 10.76) * mm});
            skLineSegment(sketch, "E1385", {"start": v(25.54, 10.76) * mm, "end": v(26.34, 10.76) * mm});
            skLineSegment(sketch, "E1386", {"start": v(26.34, 10.76) * mm, "end": v(26.34, 11.76) * mm});
            skLineSegment(sketch, "E1387", {"start": v(26.34, 11.76) * mm, "end": v(40.34, 11.76) * mm});
            skLineSegment(sketch, "E1388", {"start": v(40.34, 11.76) * mm, "end": v(40.34, 10.76) * mm});
            skLineSegment(sketch, "E1389", {"start": v(40.34, 10.76) * mm, "end": v(41.14, 10.76) * mm});
            skLineSegment(sketch, "E1390", {"start": v(41.14, 10.76) * mm, "end": v(41.14, 7.66) * mm});
            skLineSegment(sketch, "E1391", {"start": v(41.14, 7.66) * mm, "end": v(40.34, 7.66) * mm});
            skLineSegment(sketch, "E1392", {"start": v(40.34, 7.66) * mm, "end": v(40.34, 1.86) * mm});
            skLineSegment(sketch, "E1393", {"start": v(40.34, 1.86) * mm, "end": v(41.14, 1.86) * mm});
            skLineSegment(sketch, "E1394", {"start": v(41.14, 1.86) * mm, "end": v(41.14, -1.24) * mm});
            skLineSegment(sketch, "E1395", {"start": v(41.14, -1.24) * mm, "end": v(40.34, -1.24) * mm});
            skLineSegment(sketch, "E1396", {"start": v(42.72, -58.39) * mm, "end": v(42.72, -59.39) * mm});
            skLineSegment(sketch, "E1397", {"start": v(42.72, -59.39) * mm, "end": v(28.72, -59.39) * mm});
            skLineSegment(sketch, "E1398", {"start": v(28.72, -59.39) * mm, "end": v(28.72, -58.39) * mm});
            skLineSegment(sketch, "E1399", {"start": v(28.72, -58.39) * mm, "end": v(27.92, -58.39) * mm});
            skLineSegment(sketch, "E1400", {"start": v(27.92, -58.39) * mm, "end": v(27.92, -55.29) * mm});
            skLineSegment(sketch, "E1401", {"start": v(27.92, -55.29) * mm, "end": v(28.72, -55.29) * mm});
            skLineSegment(sketch, "E1402", {"start": v(28.72, -55.29) * mm, "end": v(28.72, -49.49) * mm});
            skLineSegment(sketch, "E1403", {"start": v(28.72, -49.49) * mm, "end": v(27.92, -49.49) * mm});
            skLineSegment(sketch, "E1404", {"start": v(27.92, -49.49) * mm, "end": v(27.92, -46.39) * mm});
            skLineSegment(sketch, "E1405", {"start": v(27.92, -46.39) * mm, "end": v(28.72, -46.39) * mm});
            skLineSegment(sketch, "E1406", {"start": v(28.72, -46.39) * mm, "end": v(28.72, -45.39) * mm});
            skLineSegment(sketch, "E1407", {"start": v(28.72, -45.39) * mm, "end": v(42.72, -45.39) * mm});
            skLineSegment(sketch, "E1408", {"start": v(42.72, -45.39) * mm, "end": v(42.72, -46.39) * mm});
            skLineSegment(sketch, "E1409", {"start": v(42.72, -46.39) * mm, "end": v(43.52, -46.39) * mm});
            skLineSegment(sketch, "E1410", {"start": v(43.52, -46.39) * mm, "end": v(43.52, -49.49) * mm});
            skLineSegment(sketch, "E1411", {"start": v(43.52, -49.49) * mm, "end": v(42.72, -49.49) * mm});
            skLineSegment(sketch, "E1412", {"start": v(42.72, -49.49) * mm, "end": v(42.72, -55.29) * mm});
            skLineSegment(sketch, "E1413", {"start": v(42.72, -55.29) * mm, "end": v(43.52, -55.29) * mm});
            skLineSegment(sketch, "E1414", {"start": v(43.52, -55.29) * mm, "end": v(43.52, -58.39) * mm});
            skLineSegment(sketch, "E1415", {"start": v(43.52, -58.39) * mm, "end": v(42.72, -58.39) * mm});
            skLineSegment(sketch, "E1416", {"start": v(49.86, 46.39) * mm, "end": v(49.86, 45.39) * mm});
            skLineSegment(sketch, "E1417", {"start": v(49.86, 45.39) * mm, "end": v(35.86, 45.39) * mm});
            skLineSegment(sketch, "E1418", {"start": v(35.86, 45.39) * mm, "end": v(35.86, 46.39) * mm});
            skLineSegment(sketch, "E1419", {"start": v(35.86, 46.39) * mm, "end": v(35.06, 46.39) * mm});
            skLineSegment(sketch, "E1420", {"start": v(35.06, 46.39) * mm, "end": v(35.06, 49.49) * mm});
            skLineSegment(sketch, "E1421", {"start": v(35.06, 49.49) * mm, "end": v(35.86, 49.49) * mm});
            skLineSegment(sketch, "E1422", {"start": v(35.86, 49.49) * mm, "end": v(35.86, 55.29) * mm});
            skLineSegment(sketch, "E1423", {"start": v(35.86, 55.29) * mm, "end": v(35.06, 55.29) * mm});
            skLineSegment(sketch, "E1424", {"start": v(35.06, 55.29) * mm, "end": v(35.06, 58.39) * mm});
            skLineSegment(sketch, "E1425", {"start": v(35.06, 58.39) * mm, "end": v(35.86, 58.39) * mm});
            skLineSegment(sketch, "E1426", {"start": v(35.86, 58.39) * mm, "end": v(35.86, 59.39) * mm});
            skLineSegment(sketch, "E1427", {"start": v(35.86, 59.39) * mm, "end": v(49.86, 59.39) * mm});
            skLineSegment(sketch, "E1428", {"start": v(49.86, 59.39) * mm, "end": v(49.86, 58.39) * mm});
            skLineSegment(sketch, "E1429", {"start": v(49.86, 58.39) * mm, "end": v(50.66, 58.39) * mm});
            skLineSegment(sketch, "E1430", {"start": v(50.66, 58.39) * mm, "end": v(50.66, 55.29) * mm});
            skLineSegment(sketch, "E1431", {"start": v(50.66, 55.29) * mm, "end": v(49.86, 55.29) * mm});
            skLineSegment(sketch, "E1432", {"start": v(49.86, 55.29) * mm, "end": v(49.86, 49.49) * mm});
            skLineSegment(sketch, "E1433", {"start": v(49.86, 49.49) * mm, "end": v(50.66, 49.49) * mm});
            skLineSegment(sketch, "E1434", {"start": v(50.66, 49.49) * mm, "end": v(50.66, 46.39) * mm});
            skLineSegment(sketch, "E1435", {"start": v(50.66, 46.39) * mm, "end": v(49.86, 46.39) * mm});
            skLineSegment(sketch, "E1436", {"start": v(60.47, -33.84) * mm, "end": v(60.47, -40.1) * mm});
            skLineSegment(sketch, "E1437", {"start": v(60.47, -40.1) * mm, "end": v(58.84, -40.1) * mm});
            skLineSegment(sketch, "E1438", {"start": v(58.84, -40.1) * mm, "end": v(58.84, -41.09) * mm});
            skLineSegment(sketch, "E1439", {"start": v(58.84, -41.09) * mm, "end": v(55.54, -41.09) * mm});
            skLineSegment(sketch, "E1440", {"start": v(55.54, -41.09) * mm, "end": v(55.54, -40.1) * mm});
            skLineSegment(sketch, "E1441", {"start": v(55.54, -40.1) * mm, "end": v(53.82, -40.1) * mm});
            skLineSegment(sketch, "E1442", {"start": v(53.82, -40.1) * mm, "end": v(53.82, -39.3) * mm});
            skLineSegment(sketch, "E1443", {"start": v(53.82, -39.3) * mm, "end": v(53.04, -39.3) * mm});
            skLineSegment(sketch, "E1444", {"start": v(53.04, -39.3) * mm, "end": v(53.04, -39.34) * mm});
            skLineSegment(sketch, "E1445", {"start": v(53.04, -39.34) * mm, "end": v(52.24, -39.34) * mm});
            skLineSegment(sketch, "E1446", {"start": v(52.24, -39.34) * mm, "end": v(52.24, -40.34) * mm});
            skLineSegment(sketch, "E1447", {"start": v(52.24, -40.34) * mm, "end": v(38.24, -40.34) * mm});
            skLineSegment(sketch, "E1448", {"start": v(38.24, -40.34) * mm, "end": v(38.24, -39.34) * mm});
            skLineSegment(sketch, "E1449", {"start": v(38.24, -39.34) * mm, "end": v(37.44, -39.34) * mm});
            skLineSegment(sketch, "E1450", {"start": v(37.44, -39.34) * mm, "end": v(37.44, -39.3) * mm});
            skLineSegment(sketch, "E1451", {"start": v(37.44, -39.3) * mm, "end": v(36.67, -39.3) * mm});
            skLineSegment(sketch, "E1452", {"start": v(36.67, -39.3) * mm, "end": v(36.67, -40.1) * mm});
            skLineSegment(sketch, "E1453", {"start": v(36.67, -40.1) * mm, "end": v(34.94, -40.1) * mm});
            skLineSegment(sketch, "E1454", {"start": v(34.94, -40.1) * mm, "end": v(34.94, -41.09) * mm});
            skLineSegment(sketch, "E1455", {"start": v(34.94, -41.09) * mm, "end": v(31.64, -41.09) * mm});
            skLineSegment(sketch, "E1456", {"start": v(31.64, -41.09) * mm, "end": v(31.64, -40.1) * mm});
            skLineSegment(sketch, "E1457", {"start": v(31.64, -40.1) * mm, "end": v(30.02, -40.1) * mm});
            skLineSegment(sketch, "E1458", {"start": v(30.02, -40.1) * mm, "end": v(30.02, -33.84) * mm});
            skLineSegment(sketch, "E1459", {"start": v(30.02, -33.84) * mm, "end": v(29.14, -33.84) * mm});
            skLineSegment(sketch, "E1460", {"start": v(29.14, -33.84) * mm, "end": v(29.14, -31.04) * mm});
            skLineSegment(sketch, "E1461", {"start": v(29.14, -31.04) * mm, "end": v(30.02, -31.04) * mm});
            skLineSegment(sketch, "E1462", {"start": v(30.02, -31.04) * mm, "end": v(30.02, -27.8) * mm});
            skLineSegment(sketch, "E1463", {"start": v(30.02, -27.8) * mm, "end": v(31.64, -27.8) * mm});
            skLineSegment(sketch, "E1464", {"start": v(31.64, -27.8) * mm, "end": v(31.64, -26.89) * mm});
            skLineSegment(sketch, "E1465", {"start": v(31.64, -26.89) * mm, "end": v(34.94, -26.89) * mm});
            skLineSegment(sketch, "E1466", {"start": v(34.94, -26.89) * mm, "end": v(34.94, -27.8) * mm});
            skLineSegment(sketch, "E1467", {"start": v(34.94, -27.8) * mm, "end": v(36.67, -27.8) * mm});
            skLineSegment(sketch, "E1468", {"start": v(36.67, -27.8) * mm, "end": v(36.67, -28.6) * mm});
            skLineSegment(sketch, "E1469", {"start": v(36.67, -28.6) * mm, "end": v(37.44, -28.6) * mm});
            skLineSegment(sketch, "E1470", {"start": v(37.44, -28.6) * mm, "end": v(37.44, -27.34) * mm});
            skLineSegment(sketch, "E1471", {"start": v(37.44, -27.34) * mm, "end": v(38.24, -27.34) * mm});
            skLineSegment(sketch, "E1472", {"start": v(38.24, -27.34) * mm, "end": v(38.24, -26.34) * mm});
            skLineSegment(sketch, "E1473", {"start": v(38.24, -26.34) * mm, "end": v(52.24, -26.34) * mm});
            skLineSegment(sketch, "E1474", {"start": v(52.24, -26.34) * mm, "end": v(52.24, -27.34) * mm});
            skLineSegment(sketch, "E1475", {"start": v(52.24, -27.34) * mm, "end": v(53.04, -27.34) * mm});
            skLineSegment(sketch, "E1476", {"start": v(53.04, -27.34) * mm, "end": v(53.04, -28.6) * mm});
            skLineSegment(sketch, "E1477", {"start": v(53.04, -28.6) * mm, "end": v(53.82, -28.6) * mm});
            skLineSegment(sketch, "E1478", {"start": v(53.82, -28.6) * mm, "end": v(53.82, -27.8) * mm});
            skLineSegment(sketch, "E1479", {"start": v(53.82, -27.8) * mm, "end": v(55.54, -27.8) * mm});
            skLineSegment(sketch, "E1480", {"start": v(55.54, -27.8) * mm, "end": v(55.54, -26.89) * mm});
            skLineSegment(sketch, "E1481", {"start": v(55.54, -26.89) * mm, "end": v(58.84, -26.89) * mm});
            skLineSegment(sketch, "E1482", {"start": v(58.84, -26.89) * mm, "end": v(58.84, -27.8) * mm});
            skLineSegment(sketch, "E1483", {"start": v(58.84, -27.8) * mm, "end": v(60.47, -27.8) * mm});
            skLineSegment(sketch, "E1484", {"start": v(60.47, -27.8) * mm, "end": v(60.47, -31.04) * mm});
            skLineSegment(sketch, "E1485", {"start": v(60.47, -31.04) * mm, "end": v(61.34, -31.04) * mm});
            skLineSegment(sketch, "E1486", {"start": v(61.34, -31.04) * mm, "end": v(61.34, -33.84) * mm});
            skLineSegment(sketch, "E1487", {"start": v(61.34, -33.84) * mm, "end": v(60.47, -33.84) * mm});
            skLineSegment(sketch, "E1488", {"start": v(64.15, -1.24) * mm, "end": v(64.15, -2.24) * mm});
            skLineSegment(sketch, "E1489", {"start": v(64.15, -2.24) * mm, "end": v(50.15, -2.24) * mm});
            skLineSegment(sketch, "E1490", {"start": v(50.15, -2.24) * mm, "end": v(50.15, -1.24) * mm});
            skLineSegment(sketch, "E1491", {"start": v(50.15, -1.24) * mm, "end": v(49.35, -1.24) * mm});
            skLineSegment(sketch, "E1492", {"start": v(49.35, -1.24) * mm, "end": v(49.35, 1.86) * mm});
            skLineSegment(sketch, "E1493", {"start": v(49.35, 1.86) * mm, "end": v(50.15, 1.86) * mm});
            skLineSegment(sketch, "E1494", {"start": v(50.15, 1.86) * mm, "end": v(50.15, 7.66) * mm});
            skLineSegment(sketch, "E1495", {"start": v(50.15, 7.66) * mm, "end": v(49.35, 7.66) * mm});
            skLineSegment(sketch, "E1496", {"start": v(49.35, 7.66) * mm, "end": v(49.35, 10.76) * mm});
            skLineSegment(sketch, "E1497", {"start": v(49.35, 10.76) * mm, "end": v(50.15, 10.76) * mm});
            skLineSegment(sketch, "E1498", {"start": v(50.15, 10.76) * mm, "end": v(50.15, 11.76) * mm});
            skLineSegment(sketch, "E1499", {"start": v(50.15, 11.76) * mm, "end": v(64.15, 11.76) * mm});
            skLineSegment(sketch, "E1500", {"start": v(64.15, 11.76) * mm, "end": v(64.15, 10.76) * mm});
            skLineSegment(sketch, "E1501", {"start": v(64.15, 10.76) * mm, "end": v(64.95, 10.76) * mm});
            skLineSegment(sketch, "E1502", {"start": v(64.95, 10.76) * mm, "end": v(64.95, 7.66) * mm});
            skLineSegment(sketch, "E1503", {"start": v(64.95, 7.66) * mm, "end": v(64.15, 7.66) * mm});
            skLineSegment(sketch, "E1504", {"start": v(64.15, 7.66) * mm, "end": v(64.15, 1.86) * mm});
            skLineSegment(sketch, "E1505", {"start": v(64.15, 1.86) * mm, "end": v(64.95, 1.86) * mm});
            skLineSegment(sketch, "E1506", {"start": v(64.95, 1.86) * mm, "end": v(64.95, -1.24) * mm});
            skLineSegment(sketch, "E1507", {"start": v(64.95, -1.24) * mm, "end": v(64.15, -1.24) * mm});
            skLineSegment(sketch, "E1508", {"start": v(65.23, -14.79) * mm, "end": v(65.23, -21.06) * mm});
            skLineSegment(sketch, "E1509", {"start": v(65.23, -21.06) * mm, "end": v(63.6, -21.06) * mm});
            skLineSegment(sketch, "E1510", {"start": v(63.6, -21.06) * mm, "end": v(63.6, -22.04) * mm});
            skLineSegment(sketch, "E1511", {"start": v(63.6, -22.04) * mm, "end": v(60.3, -22.04) * mm});
            skLineSegment(sketch, "E1512", {"start": v(60.3, -22.04) * mm, "end": v(60.3, -21.06) * mm});
            skLineSegment(sketch, "E1513", {"start": v(60.3, -21.06) * mm, "end": v(58.58, -21.06) * mm});
            skLineSegment(sketch, "E1514", {"start": v(58.58, -21.06) * mm, "end": v(58.58, -20.26) * mm});
            skLineSegment(sketch, "E1515", {"start": v(58.58, -20.26) * mm, "end": v(57.8, -20.26) * mm});
            skLineSegment(sketch, "E1516", {"start": v(57.8, -20.26) * mm, "end": v(57.8, -20.29) * mm});
            skLineSegment(sketch, "E1517", {"start": v(57.8, -20.29) * mm, "end": v(57, -20.29) * mm});
            skLineSegment(sketch, "E1518", {"start": v(57, -20.29) * mm, "end": v(57, -21.29) * mm});
            skLineSegment(sketch, "E1519", {"start": v(57, -21.29) * mm, "end": v(43, -21.29) * mm});
            skLineSegment(sketch, "E1520", {"start": v(43, -21.29) * mm, "end": v(43, -20.29) * mm});
            skLineSegment(sketch, "E1521", {"start": v(43, -20.29) * mm, "end": v(42.2, -20.29) * mm});
            skLineSegment(sketch, "E1522", {"start": v(42.2, -20.29) * mm, "end": v(42.2, -20.26) * mm});
            skLineSegment(sketch, "E1523", {"start": v(42.2, -20.26) * mm, "end": v(41.43, -20.26) * mm});
            skLineSegment(sketch, "E1524", {"start": v(41.43, -20.26) * mm, "end": v(41.43, -21.06) * mm});
            skLineSegment(sketch, "E1525", {"start": v(41.43, -21.06) * mm, "end": v(39.7, -21.06) * mm});
            skLineSegment(sketch, "E1526", {"start": v(39.7, -21.06) * mm, "end": v(39.7, -22.04) * mm});
            skLineSegment(sketch, "E1527", {"start": v(39.7, -22.04) * mm, "end": v(36.4, -22.04) * mm});
            skLineSegment(sketch, "E1528", {"start": v(36.4, -22.04) * mm, "end": v(36.4, -21.06) * mm});
            skLineSegment(sketch, "E1529", {"start": v(36.4, -21.06) * mm, "end": v(34.78, -21.06) * mm});
            skLineSegment(sketch, "E1530", {"start": v(34.78, -21.06) * mm, "end": v(34.78, -14.79) * mm});
            skLineSegment(sketch, "E1531", {"start": v(34.78, -14.79) * mm, "end": v(33.9, -14.79) * mm});
            skLineSegment(sketch, "E1532", {"start": v(33.9, -14.79) * mm, "end": v(33.9, -11.99) * mm});
            skLineSegment(sketch, "E1533", {"start": v(33.9, -11.99) * mm, "end": v(34.78, -11.99) * mm});
            skLineSegment(sketch, "E1534", {"start": v(34.78, -11.99) * mm, "end": v(34.78, -8.76) * mm});
            skLineSegment(sketch, "E1535", {"start": v(34.78, -8.76) * mm, "end": v(36.4, -8.76) * mm});
            skLineSegment(sketch, "E1536", {"start": v(36.4, -8.76) * mm, "end": v(36.4, -7.84) * mm});
            skLineSegment(sketch, "E1537", {"start": v(36.4, -7.84) * mm, "end": v(39.7, -7.84) * mm});
            skLineSegment(sketch, "E1538", {"start": v(39.7, -7.84) * mm, "end": v(39.7, -8.76) * mm});
            skLineSegment(sketch, "E1539", {"start": v(39.7, -8.76) * mm, "end": v(41.43, -8.76) * mm});
            skLineSegment(sketch, "E1540", {"start": v(41.43, -8.76) * mm, "end": v(41.43, -9.56) * mm});
            skLineSegment(sketch, "E1541", {"start": v(41.43, -9.56) * mm, "end": v(42.2, -9.56) * mm});
            skLineSegment(sketch, "E1542", {"start": v(42.2, -9.56) * mm, "end": v(42.2, -8.29) * mm});
            skLineSegment(sketch, "E1543", {"start": v(42.2, -8.29) * mm, "end": v(43, -8.29) * mm});
            skLineSegment(sketch, "E1544", {"start": v(43, -8.29) * mm, "end": v(43, -7.29) * mm});
            skLineSegment(sketch, "E1545", {"start": v(43, -7.29) * mm, "end": v(57, -7.29) * mm});
            skLineSegment(sketch, "E1546", {"start": v(57, -7.29) * mm, "end": v(57, -8.29) * mm});
            skLineSegment(sketch, "E1547", {"start": v(57, -8.29) * mm, "end": v(57.8, -8.29) * mm});
            skLineSegment(sketch, "E1548", {"start": v(57.8, -8.29) * mm, "end": v(57.8, -9.56) * mm});
            skLineSegment(sketch, "E1549", {"start": v(57.8, -9.56) * mm, "end": v(58.58, -9.56) * mm});
            skLineSegment(sketch, "E1550", {"start": v(58.58, -9.56) * mm, "end": v(58.58, -8.76) * mm});
            skLineSegment(sketch, "E1551", {"start": v(58.58, -8.76) * mm, "end": v(60.3, -8.76) * mm});
            skLineSegment(sketch, "E1552", {"start": v(60.3, -8.76) * mm, "end": v(60.3, -7.84) * mm});
            skLineSegment(sketch, "E1553", {"start": v(60.3, -7.84) * mm, "end": v(63.6, -7.84) * mm});
            skLineSegment(sketch, "E1554", {"start": v(63.6, -7.84) * mm, "end": v(63.6, -8.76) * mm});
            skLineSegment(sketch, "E1555", {"start": v(63.6, -8.76) * mm, "end": v(65.23, -8.76) * mm});
            skLineSegment(sketch, "E1556", {"start": v(65.23, -8.76) * mm, "end": v(65.23, -11.99) * mm});
            skLineSegment(sketch, "E1557", {"start": v(65.23, -11.99) * mm, "end": v(66.1, -11.99) * mm});
            skLineSegment(sketch, "E1558", {"start": v(66.1, -11.99) * mm, "end": v(66.1, -14.79) * mm});
            skLineSegment(sketch, "E1559", {"start": v(66.1, -14.79) * mm, "end": v(65.23, -14.79) * mm});
            skLineSegment(sketch, "E1560", {"start": v(66.53, -58.39) * mm, "end": v(66.53, -59.39) * mm});
            skLineSegment(sketch, "E1561", {"start": v(66.53, -59.39) * mm, "end": v(52.53, -59.39) * mm});
            skLineSegment(sketch, "E1562", {"start": v(52.53, -59.39) * mm, "end": v(52.53, -58.39) * mm});
            skLineSegment(sketch, "E1563", {"start": v(52.53, -58.39) * mm, "end": v(51.73, -58.39) * mm});
            skLineSegment(sketch, "E1564", {"start": v(51.73, -58.39) * mm, "end": v(51.73, -55.29) * mm});
            skLineSegment(sketch, "E1565", {"start": v(51.73, -55.29) * mm, "end": v(52.53, -55.29) * mm});
            skLineSegment(sketch, "E1566", {"start": v(52.53, -55.29) * mm, "end": v(52.53, -49.49) * mm});
            skLineSegment(sketch, "E1567", {"start": v(52.53, -49.49) * mm, "end": v(51.73, -49.49) * mm});
            skLineSegment(sketch, "E1568", {"start": v(51.73, -49.49) * mm, "end": v(51.73, -46.39) * mm});
            skLineSegment(sketch, "E1569", {"start": v(51.73, -46.39) * mm, "end": v(52.53, -46.39) * mm});
            skLineSegment(sketch, "E1570", {"start": v(52.53, -46.39) * mm, "end": v(52.53, -45.39) * mm});
            skLineSegment(sketch, "E1571", {"start": v(52.53, -45.39) * mm, "end": v(66.53, -45.39) * mm});
            skLineSegment(sketch, "E1572", {"start": v(66.53, -45.39) * mm, "end": v(66.53, -46.39) * mm});
            skLineSegment(sketch, "E1573", {"start": v(66.53, -46.39) * mm, "end": v(67.33, -46.39) * mm});
            skLineSegment(sketch, "E1574", {"start": v(67.33, -46.39) * mm, "end": v(67.33, -49.49) * mm});
            skLineSegment(sketch, "E1575", {"start": v(67.33, -49.49) * mm, "end": v(66.53, -49.49) * mm});
            skLineSegment(sketch, "E1576", {"start": v(66.53, -49.49) * mm, "end": v(66.53, -55.29) * mm});
            skLineSegment(sketch, "E1577", {"start": v(66.53, -55.29) * mm, "end": v(67.33, -55.29) * mm});
            skLineSegment(sketch, "E1578", {"start": v(67.33, -55.29) * mm, "end": v(67.33, -58.39) * mm});
            skLineSegment(sketch, "E1579", {"start": v(67.33, -58.39) * mm, "end": v(66.53, -58.39) * mm});
            skLineSegment(sketch, "E1580", {"start": v(67.61, 23.31) * mm, "end": v(67.61, 17.04) * mm});
            skLineSegment(sketch, "E1581", {"start": v(67.61, 17.04) * mm, "end": v(65.99, 17.04) * mm});
            skLineSegment(sketch, "E1582", {"start": v(65.99, 17.04) * mm, "end": v(65.99, 16.06) * mm});
            skLineSegment(sketch, "E1583", {"start": v(65.99, 16.06) * mm, "end": v(62.69, 16.06) * mm});
            skLineSegment(sketch, "E1584", {"start": v(62.69, 16.06) * mm, "end": v(62.69, 17.04) * mm});
            skLineSegment(sketch, "E1585", {"start": v(62.69, 17.04) * mm, "end": v(60.96, 17.04) * mm});
            skLineSegment(sketch, "E1586", {"start": v(60.96, 17.04) * mm, "end": v(60.96, 17.84) * mm});
            skLineSegment(sketch, "E1587", {"start": v(60.96, 17.84) * mm, "end": v(60.19, 17.84) * mm});
            skLineSegment(sketch, "E1588", {"start": v(60.19, 17.84) * mm, "end": v(60.19, 17.81) * mm});
            skLineSegment(sketch, "E1589", {"start": v(60.19, 17.81) * mm, "end": v(59.39, 17.81) * mm});
            skLineSegment(sketch, "E1590", {"start": v(59.39, 17.81) * mm, "end": v(59.39, 16.81) * mm});
            skLineSegment(sketch, "E1591", {"start": v(59.39, 16.81) * mm, "end": v(45.39, 16.81) * mm});
            skLineSegment(sketch, "E1592", {"start": v(45.39, 16.81) * mm, "end": v(45.39, 17.81) * mm});
            skLineSegment(sketch, "E1593", {"start": v(45.39, 17.81) * mm, "end": v(44.59, 17.81) * mm});
            skLineSegment(sketch, "E1594", {"start": v(44.59, 17.81) * mm, "end": v(44.59, 17.84) * mm});
            skLineSegment(sketch, "E1595", {"start": v(44.59, 17.84) * mm, "end": v(43.81, 17.84) * mm});
            skLineSegment(sketch, "E1596", {"start": v(43.81, 17.84) * mm, "end": v(43.81, 17.04) * mm});
            skLineSegment(sketch, "E1597", {"start": v(43.81, 17.04) * mm, "end": v(42.09, 17.04) * mm});
            skLineSegment(sketch, "E1598", {"start": v(42.09, 17.04) * mm, "end": v(42.09, 16.06) * mm});
            skLineSegment(sketch, "E1599", {"start": v(42.09, 16.06) * mm, "end": v(38.79, 16.06) * mm});
            skLineSegment(sketch, "E1600", {"start": v(38.79, 16.06) * mm, "end": v(38.79, 17.04) * mm});
            skLineSegment(sketch, "E1601", {"start": v(38.79, 17.04) * mm, "end": v(37.16, 17.04) * mm});
            skLineSegment(sketch, "E1602", {"start": v(37.16, 17.04) * mm, "end": v(37.16, 23.31) * mm});
            skLineSegment(sketch, "E1603", {"start": v(37.16, 23.31) * mm, "end": v(36.29, 23.31) * mm});
            skLineSegment(sketch, "E1604", {"start": v(36.29, 23.31) * mm, "end": v(36.29, 26.11) * mm});
            skLineSegment(sketch, "E1605", {"start": v(36.29, 26.11) * mm, "end": v(37.16, 26.11) * mm});
            skLineSegment(sketch, "E1606", {"start": v(37.16, 26.11) * mm, "end": v(37.16, 29.34) * mm});
            skLineSegment(sketch, "E1607", {"start": v(37.16, 29.34) * mm, "end": v(38.79, 29.34) * mm});
            skLineSegment(sketch, "E1608", {"start": v(38.79, 29.34) * mm, "end": v(38.79, 30.26) * mm});
            skLineSegment(sketch, "E1609", {"start": v(38.79, 30.26) * mm, "end": v(42.09, 30.26) * mm});
            skLineSegment(sketch, "E1610", {"start": v(42.09, 30.26) * mm, "end": v(42.09, 29.34) * mm});
            skLineSegment(sketch, "E1611", {"start": v(42.09, 29.34) * mm, "end": v(43.81, 29.34) * mm});
            skLineSegment(sketch, "E1612", {"start": v(43.81, 29.34) * mm, "end": v(43.81, 28.54) * mm});
            skLineSegment(sketch, "E1613", {"start": v(43.81, 28.54) * mm, "end": v(44.59, 28.54) * mm});
            skLineSegment(sketch, "E1614", {"start": v(44.59, 28.54) * mm, "end": v(44.59, 29.81) * mm});
            skLineSegment(sketch, "E1615", {"start": v(44.59, 29.81) * mm, "end": v(45.39, 29.81) * mm});
            skLineSegment(sketch, "E1616", {"start": v(45.39, 29.81) * mm, "end": v(45.39, 30.81) * mm});
            skLineSegment(sketch, "E1617", {"start": v(45.39, 30.81) * mm, "end": v(59.39, 30.81) * mm});
            skLineSegment(sketch, "E1618", {"start": v(59.39, 30.81) * mm, "end": v(59.39, 29.81) * mm});
            skLineSegment(sketch, "E1619", {"start": v(59.39, 29.81) * mm, "end": v(60.19, 29.81) * mm});
            skLineSegment(sketch, "E1620", {"start": v(60.19, 29.81) * mm, "end": v(60.19, 28.54) * mm});
            skLineSegment(sketch, "E1621", {"start": v(60.19, 28.54) * mm, "end": v(60.96, 28.54) * mm});
            skLineSegment(sketch, "E1622", {"start": v(60.96, 28.54) * mm, "end": v(60.96, 29.34) * mm});
            skLineSegment(sketch, "E1623", {"start": v(60.96, 29.34) * mm, "end": v(62.69, 29.34) * mm});
            skLineSegment(sketch, "E1624", {"start": v(62.69, 29.34) * mm, "end": v(62.69, 30.26) * mm});
            skLineSegment(sketch, "E1625", {"start": v(62.69, 30.26) * mm, "end": v(65.99, 30.26) * mm});
            skLineSegment(sketch, "E1626", {"start": v(65.99, 30.26) * mm, "end": v(65.99, 29.34) * mm});
            skLineSegment(sketch, "E1627", {"start": v(65.99, 29.34) * mm, "end": v(67.61, 29.34) * mm});
            skLineSegment(sketch, "E1628", {"start": v(67.61, 29.34) * mm, "end": v(67.61, 26.11) * mm});
            skLineSegment(sketch, "E1629", {"start": v(67.61, 26.11) * mm, "end": v(68.49, 26.11) * mm});
            skLineSegment(sketch, "E1630", {"start": v(68.49, 26.11) * mm, "end": v(68.49, 23.31) * mm});
            skLineSegment(sketch, "E1631", {"start": v(68.49, 23.31) * mm, "end": v(67.61, 23.31) * mm});
            skLineSegment(sketch, "E1632", {"start": v(68.91, 46.39) * mm, "end": v(68.91, 45.39) * mm});
            skLineSegment(sketch, "E1633", {"start": v(68.91, 45.39) * mm, "end": v(54.91, 45.39) * mm});
            skLineSegment(sketch, "E1634", {"start": v(54.91, 45.39) * mm, "end": v(54.91, 46.39) * mm});
            skLineSegment(sketch, "E1635", {"start": v(54.91, 46.39) * mm, "end": v(54.11, 46.39) * mm});
            skLineSegment(sketch, "E1636", {"start": v(54.11, 46.39) * mm, "end": v(54.11, 49.49) * mm});
            skLineSegment(sketch, "E1637", {"start": v(54.11, 49.49) * mm, "end": v(54.91, 49.49) * mm});
            skLineSegment(sketch, "E1638", {"start": v(54.91, 49.49) * mm, "end": v(54.91, 55.29) * mm});
            skLineSegment(sketch, "E1639", {"start": v(54.91, 55.29) * mm, "end": v(54.11, 55.29) * mm});
            skLineSegment(sketch, "E1640", {"start": v(54.11, 55.29) * mm, "end": v(54.11, 58.39) * mm});
            skLineSegment(sketch, "E1641", {"start": v(54.11, 58.39) * mm, "end": v(54.91, 58.39) * mm});
            skLineSegment(sketch, "E1642", {"start": v(54.91, 58.39) * mm, "end": v(54.91, 59.39) * mm});
            skLineSegment(sketch, "E1643", {"start": v(54.91, 59.39) * mm, "end": v(68.91, 59.39) * mm});
            skLineSegment(sketch, "E1644", {"start": v(68.91, 59.39) * mm, "end": v(68.91, 58.39) * mm});
            skLineSegment(sketch, "E1645", {"start": v(68.91, 58.39) * mm, "end": v(69.71, 58.39) * mm});
            skLineSegment(sketch, "E1646", {"start": v(69.71, 58.39) * mm, "end": v(69.71, 55.29) * mm});
            skLineSegment(sketch, "E1647", {"start": v(69.71, 55.29) * mm, "end": v(68.91, 55.29) * mm});
            skLineSegment(sketch, "E1648", {"start": v(68.91, 55.29) * mm, "end": v(68.91, 49.49) * mm});
            skLineSegment(sketch, "E1649", {"start": v(68.91, 49.49) * mm, "end": v(69.71, 49.49) * mm});
            skLineSegment(sketch, "E1650", {"start": v(69.71, 49.49) * mm, "end": v(69.71, 46.39) * mm});
            skLineSegment(sketch, "E1651", {"start": v(69.71, 46.39) * mm, "end": v(68.91, 46.39) * mm});
            skLineSegment(sketch, "E1652", {"start": v(92.73, 17.81) * mm, "end": v(92.73, 16.81) * mm});
            skLineSegment(sketch, "E1653", {"start": v(92.73, 16.81) * mm, "end": v(78.73, 16.81) * mm});
            skLineSegment(sketch, "E1654", {"start": v(78.73, 16.81) * mm, "end": v(78.73, 17.81) * mm});
            skLineSegment(sketch, "E1655", {"start": v(78.73, 17.81) * mm, "end": v(77.92, 17.81) * mm});
            skLineSegment(sketch, "E1656", {"start": v(77.92, 17.81) * mm, "end": v(77.92, 20.91) * mm});
            skLineSegment(sketch, "E1657", {"start": v(77.92, 20.91) * mm, "end": v(78.73, 20.91) * mm});
            skLineSegment(sketch, "E1658", {"start": v(78.73, 20.91) * mm, "end": v(78.73, 26.71) * mm});
            skLineSegment(sketch, "E1659", {"start": v(78.73, 26.71) * mm, "end": v(77.92, 26.71) * mm});
            skLineSegment(sketch, "E1660", {"start": v(77.92, 26.71) * mm, "end": v(77.92, 29.81) * mm});
            skLineSegment(sketch, "E1661", {"start": v(77.92, 29.81) * mm, "end": v(78.73, 29.81) * mm});
            skLineSegment(sketch, "E1662", {"start": v(78.73, 29.81) * mm, "end": v(78.73, 30.81) * mm});
            skLineSegment(sketch, "E1663", {"start": v(78.73, 30.81) * mm, "end": v(92.73, 30.81) * mm});
            skLineSegment(sketch, "E1664", {"start": v(92.73, 30.81) * mm, "end": v(92.73, 29.81) * mm});
            skLineSegment(sketch, "E1665", {"start": v(92.73, 29.81) * mm, "end": v(93.53, 29.81) * mm});
            skLineSegment(sketch, "E1666", {"start": v(93.53, 29.81) * mm, "end": v(93.53, 26.71) * mm});
            skLineSegment(sketch, "E1667", {"start": v(93.53, 26.71) * mm, "end": v(92.73, 26.71) * mm});
            skLineSegment(sketch, "E1668", {"start": v(92.73, 26.71) * mm, "end": v(92.73, 20.91) * mm});
            skLineSegment(sketch, "E1669", {"start": v(92.73, 20.91) * mm, "end": v(93.53, 20.91) * mm});
            skLineSegment(sketch, "E1670", {"start": v(93.53, 20.91) * mm, "end": v(93.53, 17.81) * mm});
            skLineSegment(sketch, "E1671", {"start": v(93.53, 17.81) * mm, "end": v(92.73, 17.81) * mm});
            skLineSegment(sketch, "E1672", {"start": v(92.73, -58.39) * mm, "end": v(92.73, -59.39) * mm});
            skLineSegment(sketch, "E1673", {"start": v(92.73, -59.39) * mm, "end": v(78.73, -59.39) * mm});
            skLineSegment(sketch, "E1674", {"start": v(78.73, -59.39) * mm, "end": v(78.73, -58.39) * mm});
            skLineSegment(sketch, "E1675", {"start": v(78.73, -58.39) * mm, "end": v(77.92, -58.39) * mm});
            skLineSegment(sketch, "E1676", {"start": v(77.92, -58.39) * mm, "end": v(77.92, -55.29) * mm});
            skLineSegment(sketch, "E1677", {"start": v(77.92, -55.29) * mm, "end": v(78.73, -55.29) * mm});
            skLineSegment(sketch, "E1678", {"start": v(78.73, -55.29) * mm, "end": v(78.73, -49.49) * mm});
            skLineSegment(sketch, "E1679", {"start": v(78.73, -49.49) * mm, "end": v(77.92, -49.49) * mm});
            skLineSegment(sketch, "E1680", {"start": v(77.92, -49.49) * mm, "end": v(77.92, -46.39) * mm});
            skLineSegment(sketch, "E1681", {"start": v(77.92, -46.39) * mm, "end": v(78.73, -46.39) * mm});
            skLineSegment(sketch, "E1682", {"start": v(78.73, -46.39) * mm, "end": v(78.73, -45.39) * mm});
            skLineSegment(sketch, "E1683", {"start": v(78.73, -45.39) * mm, "end": v(92.73, -45.39) * mm});
            skLineSegment(sketch, "E1684", {"start": v(92.73, -45.39) * mm, "end": v(92.73, -46.39) * mm});
            skLineSegment(sketch, "E1685", {"start": v(92.73, -46.39) * mm, "end": v(93.53, -46.39) * mm});
            skLineSegment(sketch, "E1686", {"start": v(93.53, -46.39) * mm, "end": v(93.53, -49.49) * mm});
            skLineSegment(sketch, "E1687", {"start": v(93.53, -49.49) * mm, "end": v(92.73, -49.49) * mm});
            skLineSegment(sketch, "E1688", {"start": v(92.73, -49.49) * mm, "end": v(92.73, -55.29) * mm});
            skLineSegment(sketch, "E1689", {"start": v(92.73, -55.29) * mm, "end": v(93.53, -55.29) * mm});
            skLineSegment(sketch, "E1690", {"start": v(93.53, -55.29) * mm, "end": v(93.53, -58.39) * mm});
            skLineSegment(sketch, "E1691", {"start": v(93.53, -58.39) * mm, "end": v(92.73, -58.39) * mm});
            skLineSegment(sketch, "E1692", {"start": v(92.73, 46.39) * mm, "end": v(92.73, 45.39) * mm});
            skLineSegment(sketch, "E1693", {"start": v(92.73, 45.39) * mm, "end": v(78.73, 45.39) * mm});
            skLineSegment(sketch, "E1694", {"start": v(78.73, 45.39) * mm, "end": v(78.73, 46.39) * mm});
            skLineSegment(sketch, "E1695", {"start": v(78.73, 46.39) * mm, "end": v(77.92, 46.39) * mm});
            skLineSegment(sketch, "E1696", {"start": v(77.92, 46.39) * mm, "end": v(77.92, 49.49) * mm});
            skLineSegment(sketch, "E1697", {"start": v(77.92, 49.49) * mm, "end": v(78.73, 49.49) * mm});
            skLineSegment(sketch, "E1698", {"start": v(78.73, 49.49) * mm, "end": v(78.73, 55.29) * mm});
            skLineSegment(sketch, "E1699", {"start": v(78.73, 55.29) * mm, "end": v(77.92, 55.29) * mm});
            skLineSegment(sketch, "E1700", {"start": v(77.92, 55.29) * mm, "end": v(77.92, 58.39) * mm});
            skLineSegment(sketch, "E1701", {"start": v(77.92, 58.39) * mm, "end": v(78.73, 58.39) * mm});
            skLineSegment(sketch, "E1702", {"start": v(78.73, 58.39) * mm, "end": v(78.73, 59.39) * mm});
            skLineSegment(sketch, "E1703", {"start": v(78.73, 59.39) * mm, "end": v(92.73, 59.39) * mm});
            skLineSegment(sketch, "E1704", {"start": v(92.73, 59.39) * mm, "end": v(92.73, 58.39) * mm});
            skLineSegment(sketch, "E1705", {"start": v(92.73, 58.39) * mm, "end": v(93.53, 58.39) * mm});
            skLineSegment(sketch, "E1706", {"start": v(93.53, 58.39) * mm, "end": v(93.53, 55.29) * mm});
            skLineSegment(sketch, "E1707", {"start": v(93.53, 55.29) * mm, "end": v(92.73, 55.29) * mm});
            skLineSegment(sketch, "E1708", {"start": v(92.73, 55.29) * mm, "end": v(92.73, 49.49) * mm});
            skLineSegment(sketch, "E1709", {"start": v(92.73, 49.49) * mm, "end": v(93.53, 49.49) * mm});
            skLineSegment(sketch, "E1710", {"start": v(93.53, 49.49) * mm, "end": v(93.53, 46.39) * mm});
            skLineSegment(sketch, "E1711", {"start": v(93.53, 46.39) * mm, "end": v(92.73, 46.39) * mm});
            skLineSegment(sketch, "E1712", {"start": v(92.73, -1.24) * mm, "end": v(92.73, -2.24) * mm});
            skLineSegment(sketch, "E1713", {"start": v(92.73, -2.24) * mm, "end": v(78.73, -2.24) * mm});
            skLineSegment(sketch, "E1714", {"start": v(78.73, -2.24) * mm, "end": v(78.73, -1.24) * mm});
            skLineSegment(sketch, "E1715", {"start": v(78.73, -1.24) * mm, "end": v(77.92, -1.24) * mm});
            skLineSegment(sketch, "E1716", {"start": v(77.92, -1.24) * mm, "end": v(77.92, 1.86) * mm});
            skLineSegment(sketch, "E1717", {"start": v(77.92, 1.86) * mm, "end": v(78.73, 1.86) * mm});
            skLineSegment(sketch, "E1718", {"start": v(78.73, 1.86) * mm, "end": v(78.73, 7.66) * mm});
            skLineSegment(sketch, "E1719", {"start": v(78.73, 7.66) * mm, "end": v(77.92, 7.66) * mm});
            skLineSegment(sketch, "E1720", {"start": v(77.92, 7.66) * mm, "end": v(77.92, 10.76) * mm});
            skLineSegment(sketch, "E1721", {"start": v(77.92, 10.76) * mm, "end": v(78.73, 10.76) * mm});
            skLineSegment(sketch, "E1722", {"start": v(78.73, 10.76) * mm, "end": v(78.73, 11.76) * mm});
            skLineSegment(sketch, "E1723", {"start": v(78.73, 11.76) * mm, "end": v(92.73, 11.76) * mm});
            skLineSegment(sketch, "E1724", {"start": v(92.73, 11.76) * mm, "end": v(92.73, 10.76) * mm});
            skLineSegment(sketch, "E1725", {"start": v(92.73, 10.76) * mm, "end": v(93.53, 10.76) * mm});
            skLineSegment(sketch, "E1726", {"start": v(93.53, 10.76) * mm, "end": v(93.53, 7.66) * mm});
            skLineSegment(sketch, "E1727", {"start": v(93.53, 7.66) * mm, "end": v(92.73, 7.66) * mm});
            skLineSegment(sketch, "E1728", {"start": v(92.73, 7.66) * mm, "end": v(92.73, 1.86) * mm});
            skLineSegment(sketch, "E1729", {"start": v(92.73, 1.86) * mm, "end": v(93.53, 1.86) * mm});
            skLineSegment(sketch, "E1730", {"start": v(93.53, 1.86) * mm, "end": v(93.53, -1.24) * mm});
            skLineSegment(sketch, "E1731", {"start": v(93.53, -1.24) * mm, "end": v(92.73, -1.24) * mm});
            skLineSegment(sketch, "E1732", {"start": v(111.78, 17.81) * mm, "end": v(111.78, 16.81) * mm});
            skLineSegment(sketch, "E1733", {"start": v(111.78, 16.81) * mm, "end": v(97.78, 16.81) * mm});
            skLineSegment(sketch, "E1734", {"start": v(97.78, 16.81) * mm, "end": v(97.78, 17.81) * mm});
            skLineSegment(sketch, "E1735", {"start": v(97.78, 17.81) * mm, "end": v(96.97, 17.81) * mm});
            skLineSegment(sketch, "E1736", {"start": v(96.97, 17.81) * mm, "end": v(96.97, 20.91) * mm});
            skLineSegment(sketch, "E1737", {"start": v(96.97, 20.91) * mm, "end": v(97.78, 20.91) * mm});
            skLineSegment(sketch, "E1738", {"start": v(97.78, 20.91) * mm, "end": v(97.78, 26.71) * mm});
            skLineSegment(sketch, "E1739", {"start": v(97.78, 26.71) * mm, "end": v(96.97, 26.71) * mm});
            skLineSegment(sketch, "E1740", {"start": v(96.97, 26.71) * mm, "end": v(96.97, 29.81) * mm});
            skLineSegment(sketch, "E1741", {"start": v(96.97, 29.81) * mm, "end": v(97.78, 29.81) * mm});
            skLineSegment(sketch, "E1742", {"start": v(97.78, 29.81) * mm, "end": v(97.78, 30.81) * mm});
            skLineSegment(sketch, "E1743", {"start": v(97.78, 30.81) * mm, "end": v(111.78, 30.81) * mm});
            skLineSegment(sketch, "E1744", {"start": v(111.78, 30.81) * mm, "end": v(111.78, 29.81) * mm});
            skLineSegment(sketch, "E1745", {"start": v(111.78, 29.81) * mm, "end": v(112.58, 29.81) * mm});
            skLineSegment(sketch, "E1746", {"start": v(112.58, 29.81) * mm, "end": v(112.58, 26.71) * mm});
            skLineSegment(sketch, "E1747", {"start": v(112.58, 26.71) * mm, "end": v(111.78, 26.71) * mm});
            skLineSegment(sketch, "E1748", {"start": v(111.78, 26.71) * mm, "end": v(111.78, 20.91) * mm});
            skLineSegment(sketch, "E1749", {"start": v(111.78, 20.91) * mm, "end": v(112.58, 20.91) * mm});
            skLineSegment(sketch, "E1750", {"start": v(112.58, 20.91) * mm, "end": v(112.58, 17.81) * mm});
            skLineSegment(sketch, "E1751", {"start": v(112.58, 17.81) * mm, "end": v(111.78, 17.81) * mm});
            skLineSegment(sketch, "E1752", {"start": v(111.78, -58.39) * mm, "end": v(111.78, -59.39) * mm});
            skLineSegment(sketch, "E1753", {"start": v(111.78, -59.39) * mm, "end": v(97.78, -59.39) * mm});
            skLineSegment(sketch, "E1754", {"start": v(97.78, -59.39) * mm, "end": v(97.78, -58.39) * mm});
            skLineSegment(sketch, "E1755", {"start": v(97.78, -58.39) * mm, "end": v(96.97, -58.39) * mm});
            skLineSegment(sketch, "E1756", {"start": v(96.97, -58.39) * mm, "end": v(96.97, -55.29) * mm});
            skLineSegment(sketch, "E1757", {"start": v(96.97, -55.29) * mm, "end": v(97.78, -55.29) * mm});
            skLineSegment(sketch, "E1758", {"start": v(97.78, -55.29) * mm, "end": v(97.78, -49.49) * mm});
            skLineSegment(sketch, "E1759", {"start": v(97.78, -49.49) * mm, "end": v(96.97, -49.49) * mm});
            skLineSegment(sketch, "E1760", {"start": v(96.97, -49.49) * mm, "end": v(96.97, -46.39) * mm});
            skLineSegment(sketch, "E1761", {"start": v(96.97, -46.39) * mm, "end": v(97.78, -46.39) * mm});
            skLineSegment(sketch, "E1762", {"start": v(97.78, -46.39) * mm, "end": v(97.78, -45.39) * mm});
            skLineSegment(sketch, "E1763", {"start": v(97.78, -45.39) * mm, "end": v(111.78, -45.39) * mm});
            skLineSegment(sketch, "E1764", {"start": v(111.78, -45.39) * mm, "end": v(111.78, -46.39) * mm});
            skLineSegment(sketch, "E1765", {"start": v(111.78, -46.39) * mm, "end": v(112.58, -46.39) * mm});
            skLineSegment(sketch, "E1766", {"start": v(112.58, -46.39) * mm, "end": v(112.58, -49.49) * mm});
            skLineSegment(sketch, "E1767", {"start": v(112.58, -49.49) * mm, "end": v(111.78, -49.49) * mm});
            skLineSegment(sketch, "E1768", {"start": v(111.78, -49.49) * mm, "end": v(111.78, -55.29) * mm});
            skLineSegment(sketch, "E1769", {"start": v(111.78, -55.29) * mm, "end": v(112.58, -55.29) * mm});
            skLineSegment(sketch, "E1770", {"start": v(112.58, -55.29) * mm, "end": v(112.58, -58.39) * mm});
            skLineSegment(sketch, "E1771", {"start": v(112.58, -58.39) * mm, "end": v(111.78, -58.39) * mm});
            skLineSegment(sketch, "E1772", {"start": v(111.78, 46.39) * mm, "end": v(111.78, 45.39) * mm});
            skLineSegment(sketch, "E1773", {"start": v(111.78, 45.39) * mm, "end": v(97.78, 45.39) * mm});
            skLineSegment(sketch, "E1774", {"start": v(97.78, 45.39) * mm, "end": v(97.78, 46.39) * mm});
            skLineSegment(sketch, "E1775", {"start": v(97.78, 46.39) * mm, "end": v(96.97, 46.39) * mm});
            skLineSegment(sketch, "E1776", {"start": v(96.97, 46.39) * mm, "end": v(96.97, 49.49) * mm});
            skLineSegment(sketch, "E1777", {"start": v(96.97, 49.49) * mm, "end": v(97.78, 49.49) * mm});
            skLineSegment(sketch, "E1778", {"start": v(97.78, 49.49) * mm, "end": v(97.78, 55.29) * mm});
            skLineSegment(sketch, "E1779", {"start": v(97.78, 55.29) * mm, "end": v(96.97, 55.29) * mm});
            skLineSegment(sketch, "E1780", {"start": v(96.97, 55.29) * mm, "end": v(96.97, 58.39) * mm});
            skLineSegment(sketch, "E1781", {"start": v(96.97, 58.39) * mm, "end": v(97.78, 58.39) * mm});
            skLineSegment(sketch, "E1782", {"start": v(97.78, 58.39) * mm, "end": v(97.78, 59.39) * mm});
            skLineSegment(sketch, "E1783", {"start": v(97.78, 59.39) * mm, "end": v(111.78, 59.39) * mm});
            skLineSegment(sketch, "E1784", {"start": v(111.78, 59.39) * mm, "end": v(111.78, 58.39) * mm});
            skLineSegment(sketch, "E1785", {"start": v(111.78, 58.39) * mm, "end": v(112.58, 58.39) * mm});
            skLineSegment(sketch, "E1786", {"start": v(112.58, 58.39) * mm, "end": v(112.58, 55.29) * mm});
            skLineSegment(sketch, "E1787", {"start": v(112.58, 55.29) * mm, "end": v(111.78, 55.29) * mm});
            skLineSegment(sketch, "E1788", {"start": v(111.78, 55.29) * mm, "end": v(111.78, 49.49) * mm});
            skLineSegment(sketch, "E1789", {"start": v(111.78, 49.49) * mm, "end": v(112.58, 49.49) * mm});
            skLineSegment(sketch, "E1790", {"start": v(112.58, 49.49) * mm, "end": v(112.58, 46.39) * mm});
            skLineSegment(sketch, "E1791", {"start": v(112.58, 46.39) * mm, "end": v(111.78, 46.39) * mm});
            skLineSegment(sketch, "E1792", {"start": v(111.78, -1.24) * mm, "end": v(111.78, -2.24) * mm});
            skLineSegment(sketch, "E1793", {"start": v(111.78, -2.24) * mm, "end": v(97.78, -2.24) * mm});
            skLineSegment(sketch, "E1794", {"start": v(97.78, -2.24) * mm, "end": v(97.78, -1.24) * mm});
            skLineSegment(sketch, "E1795", {"start": v(97.78, -1.24) * mm, "end": v(96.97, -1.24) * mm});
            skLineSegment(sketch, "E1796", {"start": v(96.97, -1.24) * mm, "end": v(96.97, 1.86) * mm});
            skLineSegment(sketch, "E1797", {"start": v(96.97, 1.86) * mm, "end": v(97.78, 1.86) * mm});
            skLineSegment(sketch, "E1798", {"start": v(97.78, 1.86) * mm, "end": v(97.78, 7.66) * mm});
            skLineSegment(sketch, "E1799", {"start": v(97.78, 7.66) * mm, "end": v(96.97, 7.66) * mm});
            skLineSegment(sketch, "E1800", {"start": v(96.97, 7.66) * mm, "end": v(96.97, 10.76) * mm});
            skLineSegment(sketch, "E1801", {"start": v(96.97, 10.76) * mm, "end": v(97.78, 10.76) * mm});
            skLineSegment(sketch, "E1802", {"start": v(97.78, 10.76) * mm, "end": v(97.78, 11.76) * mm});
            skLineSegment(sketch, "E1803", {"start": v(97.78, 11.76) * mm, "end": v(111.78, 11.76) * mm});
            skLineSegment(sketch, "E1804", {"start": v(111.78, 11.76) * mm, "end": v(111.78, 10.76) * mm});
            skLineSegment(sketch, "E1805", {"start": v(111.78, 10.76) * mm, "end": v(112.58, 10.76) * mm});
            skLineSegment(sketch, "E1806", {"start": v(112.58, 10.76) * mm, "end": v(112.58, 7.66) * mm});
            skLineSegment(sketch, "E1807", {"start": v(112.58, 7.66) * mm, "end": v(111.78, 7.66) * mm});
            skLineSegment(sketch, "E1808", {"start": v(111.78, 7.66) * mm, "end": v(111.78, 1.86) * mm});
            skLineSegment(sketch, "E1809", {"start": v(111.78, 1.86) * mm, "end": v(112.58, 1.86) * mm});
            skLineSegment(sketch, "E1810", {"start": v(112.58, 1.86) * mm, "end": v(112.58, -1.24) * mm});
            skLineSegment(sketch, "E1811", {"start": v(112.58, -1.24) * mm, "end": v(111.78, -1.24) * mm});
            skLineSegment(sketch, "E1812", {"start": v(111.78, -39.34) * mm, "end": v(111.78, -40.34) * mm});
            skLineSegment(sketch, "E1813", {"start": v(111.78, -40.34) * mm, "end": v(97.78, -40.34) * mm});
            skLineSegment(sketch, "E1814", {"start": v(97.78, -40.34) * mm, "end": v(97.78, -39.34) * mm});
            skLineSegment(sketch, "E1815", {"start": v(97.78, -39.34) * mm, "end": v(96.97, -39.34) * mm});
            skLineSegment(sketch, "E1816", {"start": v(96.97, -39.34) * mm, "end": v(96.97, -36.24) * mm});
            skLineSegment(sketch, "E1817", {"start": v(96.97, -36.24) * mm, "end": v(97.78, -36.24) * mm});
            skLineSegment(sketch, "E1818", {"start": v(97.78, -36.24) * mm, "end": v(97.78, -30.44) * mm});
            skLineSegment(sketch, "E1819", {"start": v(97.78, -30.44) * mm, "end": v(96.97, -30.44) * mm});
            skLineSegment(sketch, "E1820", {"start": v(96.97, -30.44) * mm, "end": v(96.97, -27.34) * mm});
            skLineSegment(sketch, "E1821", {"start": v(96.97, -27.34) * mm, "end": v(97.78, -27.34) * mm});
            skLineSegment(sketch, "E1822", {"start": v(97.78, -27.34) * mm, "end": v(97.78, -26.34) * mm});
            skLineSegment(sketch, "E1823", {"start": v(97.78, -26.34) * mm, "end": v(111.78, -26.34) * mm});
            skLineSegment(sketch, "E1824", {"start": v(111.78, -26.34) * mm, "end": v(111.78, -27.34) * mm});
            skLineSegment(sketch, "E1825", {"start": v(111.78, -27.34) * mm, "end": v(112.58, -27.34) * mm});
            skLineSegment(sketch, "E1826", {"start": v(112.58, -27.34) * mm, "end": v(112.58, -30.44) * mm});
            skLineSegment(sketch, "E1827", {"start": v(112.58, -30.44) * mm, "end": v(111.78, -30.44) * mm});
            skLineSegment(sketch, "E1828", {"start": v(111.78, -30.44) * mm, "end": v(111.78, -36.24) * mm});
            skLineSegment(sketch, "E1829", {"start": v(111.78, -36.24) * mm, "end": v(112.58, -36.24) * mm});
            skLineSegment(sketch, "E1830", {"start": v(112.58, -36.24) * mm, "end": v(112.58, -39.34) * mm});
            skLineSegment(sketch, "E1831", {"start": v(112.58, -39.34) * mm, "end": v(111.78, -39.34) * mm});
            skLineSegment(sketch, "E1832", {"start": v(130.83, 17.81) * mm, "end": v(130.83, 16.81) * mm});
            skLineSegment(sketch, "E1833", {"start": v(130.83, 16.81) * mm, "end": v(116.83, 16.81) * mm});
            skLineSegment(sketch, "E1834", {"start": v(116.83, 16.81) * mm, "end": v(116.83, 17.81) * mm});
            skLineSegment(sketch, "E1835", {"start": v(116.83, 17.81) * mm, "end": v(116.02, 17.81) * mm});
            skLineSegment(sketch, "E1836", {"start": v(116.02, 17.81) * mm, "end": v(116.02, 20.91) * mm});
            skLineSegment(sketch, "E1837", {"start": v(116.02, 20.91) * mm, "end": v(116.83, 20.91) * mm});
            skLineSegment(sketch, "E1838", {"start": v(116.83, 20.91) * mm, "end": v(116.83, 26.71) * mm});
            skLineSegment(sketch, "E1839", {"start": v(116.83, 26.71) * mm, "end": v(116.02, 26.71) * mm});
            skLineSegment(sketch, "E1840", {"start": v(116.02, 26.71) * mm, "end": v(116.02, 29.81) * mm});
            skLineSegment(sketch, "E1841", {"start": v(116.02, 29.81) * mm, "end": v(116.83, 29.81) * mm});
            skLineSegment(sketch, "E1842", {"start": v(116.83, 29.81) * mm, "end": v(116.83, 30.81) * mm});
            skLineSegment(sketch, "E1843", {"start": v(116.83, 30.81) * mm, "end": v(130.83, 30.81) * mm});
            skLineSegment(sketch, "E1844", {"start": v(130.83, 30.81) * mm, "end": v(130.83, 29.81) * mm});
            skLineSegment(sketch, "E1845", {"start": v(130.83, 29.81) * mm, "end": v(131.63, 29.81) * mm});
            skLineSegment(sketch, "E1846", {"start": v(131.63, 29.81) * mm, "end": v(131.63, 26.71) * mm});
            skLineSegment(sketch, "E1847", {"start": v(131.63, 26.71) * mm, "end": v(130.83, 26.71) * mm});
            skLineSegment(sketch, "E1848", {"start": v(130.83, 26.71) * mm, "end": v(130.83, 20.91) * mm});
            skLineSegment(sketch, "E1849", {"start": v(130.83, 20.91) * mm, "end": v(131.63, 20.91) * mm});
            skLineSegment(sketch, "E1850", {"start": v(131.63, 20.91) * mm, "end": v(131.63, 17.81) * mm});
            skLineSegment(sketch, "E1851", {"start": v(131.63, 17.81) * mm, "end": v(130.83, 17.81) * mm});
            skLineSegment(sketch, "E1852", {"start": v(130.83, -58.39) * mm, "end": v(130.83, -59.39) * mm});
            skLineSegment(sketch, "E1853", {"start": v(130.83, -59.39) * mm, "end": v(116.83, -59.39) * mm});
            skLineSegment(sketch, "E1854", {"start": v(116.83, -59.39) * mm, "end": v(116.83, -58.39) * mm});
            skLineSegment(sketch, "E1855", {"start": v(116.83, -58.39) * mm, "end": v(116.02, -58.39) * mm});
            skLineSegment(sketch, "E1856", {"start": v(116.02, -58.39) * mm, "end": v(116.02, -55.29) * mm});
            skLineSegment(sketch, "E1857", {"start": v(116.02, -55.29) * mm, "end": v(116.83, -55.29) * mm});
            skLineSegment(sketch, "E1858", {"start": v(116.83, -55.29) * mm, "end": v(116.83, -49.49) * mm});
            skLineSegment(sketch, "E1859", {"start": v(116.83, -49.49) * mm, "end": v(116.02, -49.49) * mm});
            skLineSegment(sketch, "E1860", {"start": v(116.02, -49.49) * mm, "end": v(116.02, -46.39) * mm});
            skLineSegment(sketch, "E1861", {"start": v(116.02, -46.39) * mm, "end": v(116.83, -46.39) * mm});
            skLineSegment(sketch, "E1862", {"start": v(116.83, -46.39) * mm, "end": v(116.83, -45.39) * mm});
            skLineSegment(sketch, "E1863", {"start": v(116.83, -45.39) * mm, "end": v(130.83, -45.39) * mm});
            skLineSegment(sketch, "E1864", {"start": v(130.83, -45.39) * mm, "end": v(130.83, -46.39) * mm});
            skLineSegment(sketch, "E1865", {"start": v(130.83, -46.39) * mm, "end": v(131.63, -46.39) * mm});
            skLineSegment(sketch, "E1866", {"start": v(131.63, -46.39) * mm, "end": v(131.63, -49.49) * mm});
            skLineSegment(sketch, "E1867", {"start": v(131.63, -49.49) * mm, "end": v(130.83, -49.49) * mm});
            skLineSegment(sketch, "E1868", {"start": v(130.83, -49.49) * mm, "end": v(130.83, -55.29) * mm});
            skLineSegment(sketch, "E1869", {"start": v(130.83, -55.29) * mm, "end": v(131.63, -55.29) * mm});
            skLineSegment(sketch, "E1870", {"start": v(131.63, -55.29) * mm, "end": v(131.63, -58.39) * mm});
            skLineSegment(sketch, "E1871", {"start": v(131.63, -58.39) * mm, "end": v(130.83, -58.39) * mm});
            skLineSegment(sketch, "E1872", {"start": v(130.83, 46.39) * mm, "end": v(130.83, 45.39) * mm});
            skLineSegment(sketch, "E1873", {"start": v(130.83, 45.39) * mm, "end": v(116.83, 45.39) * mm});
            skLineSegment(sketch, "E1874", {"start": v(116.83, 45.39) * mm, "end": v(116.83, 46.39) * mm});
            skLineSegment(sketch, "E1875", {"start": v(116.83, 46.39) * mm, "end": v(116.02, 46.39) * mm});
            skLineSegment(sketch, "E1876", {"start": v(116.02, 46.39) * mm, "end": v(116.02, 49.49) * mm});
            skLineSegment(sketch, "E1877", {"start": v(116.02, 49.49) * mm, "end": v(116.83, 49.49) * mm});
            skLineSegment(sketch, "E1878", {"start": v(116.83, 49.49) * mm, "end": v(116.83, 55.29) * mm});
            skLineSegment(sketch, "E1879", {"start": v(116.83, 55.29) * mm, "end": v(116.02, 55.29) * mm});
            skLineSegment(sketch, "E1880", {"start": v(116.02, 55.29) * mm, "end": v(116.02, 58.39) * mm});
            skLineSegment(sketch, "E1881", {"start": v(116.02, 58.39) * mm, "end": v(116.83, 58.39) * mm});
            skLineSegment(sketch, "E1882", {"start": v(116.83, 58.39) * mm, "end": v(116.83, 59.39) * mm});
            skLineSegment(sketch, "E1883", {"start": v(116.83, 59.39) * mm, "end": v(130.83, 59.39) * mm});
            skLineSegment(sketch, "E1884", {"start": v(130.83, 59.39) * mm, "end": v(130.83, 58.39) * mm});
            skLineSegment(sketch, "E1885", {"start": v(130.83, 58.39) * mm, "end": v(131.63, 58.39) * mm});
            skLineSegment(sketch, "E1886", {"start": v(131.63, 58.39) * mm, "end": v(131.63, 55.29) * mm});
            skLineSegment(sketch, "E1887", {"start": v(131.63, 55.29) * mm, "end": v(130.83, 55.29) * mm});
            skLineSegment(sketch, "E1888", {"start": v(130.83, 55.29) * mm, "end": v(130.83, 49.49) * mm});
            skLineSegment(sketch, "E1889", {"start": v(130.83, 49.49) * mm, "end": v(131.63, 49.49) * mm});
            skLineSegment(sketch, "E1890", {"start": v(131.63, 49.49) * mm, "end": v(131.63, 46.39) * mm});
            skLineSegment(sketch, "E1891", {"start": v(131.63, 46.39) * mm, "end": v(130.83, 46.39) * mm});
            skLineSegment(sketch, "E1892", {"start": v(130.83, -1.24) * mm, "end": v(130.83, -2.24) * mm});
            skLineSegment(sketch, "E1893", {"start": v(130.83, -2.24) * mm, "end": v(116.83, -2.24) * mm});
            skLineSegment(sketch, "E1894", {"start": v(116.83, -2.24) * mm, "end": v(116.83, -1.24) * mm});
            skLineSegment(sketch, "E1895", {"start": v(116.83, -1.24) * mm, "end": v(116.02, -1.24) * mm});
            skLineSegment(sketch, "E1896", {"start": v(116.02, -1.24) * mm, "end": v(116.02, 1.86) * mm});
            skLineSegment(sketch, "E1897", {"start": v(116.02, 1.86) * mm, "end": v(116.83, 1.86) * mm});
            skLineSegment(sketch, "E1898", {"start": v(116.83, 1.86) * mm, "end": v(116.83, 7.66) * mm});
            skLineSegment(sketch, "E1899", {"start": v(116.83, 7.66) * mm, "end": v(116.02, 7.66) * mm});
            skLineSegment(sketch, "E1900", {"start": v(116.02, 7.66) * mm, "end": v(116.02, 10.76) * mm});
            skLineSegment(sketch, "E1901", {"start": v(116.02, 10.76) * mm, "end": v(116.83, 10.76) * mm});
            skLineSegment(sketch, "E1902", {"start": v(116.83, 10.76) * mm, "end": v(116.83, 11.76) * mm});
            skLineSegment(sketch, "E1903", {"start": v(116.83, 11.76) * mm, "end": v(130.83, 11.76) * mm});
            skLineSegment(sketch, "E1904", {"start": v(130.83, 11.76) * mm, "end": v(130.83, 10.76) * mm});
            skLineSegment(sketch, "E1905", {"start": v(130.83, 10.76) * mm, "end": v(131.63, 10.76) * mm});
            skLineSegment(sketch, "E1906", {"start": v(131.63, 10.76) * mm, "end": v(131.63, 7.66) * mm});
            skLineSegment(sketch, "E1907", {"start": v(131.63, 7.66) * mm, "end": v(130.83, 7.66) * mm});
            skLineSegment(sketch, "E1908", {"start": v(130.83, 7.66) * mm, "end": v(130.83, 1.86) * mm});
            skLineSegment(sketch, "E1909", {"start": v(130.83, 1.86) * mm, "end": v(131.63, 1.86) * mm});
            skLineSegment(sketch, "E1910", {"start": v(131.63, 1.86) * mm, "end": v(131.63, -1.24) * mm});
            skLineSegment(sketch, "E1911", {"start": v(131.63, -1.24) * mm, "end": v(130.83, -1.24) * mm});
            skLineSegment(sketch, "E1912", {"start": v(154.64, 17.81) * mm, "end": v(154.64, 16.81) * mm});
            skLineSegment(sketch, "E1913", {"start": v(154.64, 16.81) * mm, "end": v(140.64, 16.81) * mm});
            skLineSegment(sketch, "E1914", {"start": v(140.64, 16.81) * mm, "end": v(140.64, 17.81) * mm});
            skLineSegment(sketch, "E1915", {"start": v(140.64, 17.81) * mm, "end": v(139.84, 17.81) * mm});
            skLineSegment(sketch, "E1916", {"start": v(139.84, 17.81) * mm, "end": v(139.84, 20.91) * mm});
            skLineSegment(sketch, "E1917", {"start": v(139.84, 20.91) * mm, "end": v(140.64, 20.91) * mm});
            skLineSegment(sketch, "E1918", {"start": v(140.64, 20.91) * mm, "end": v(140.64, 26.71) * mm});
            skLineSegment(sketch, "E1919", {"start": v(140.64, 26.71) * mm, "end": v(139.84, 26.71) * mm});
            skLineSegment(sketch, "E1920", {"start": v(139.84, 26.71) * mm, "end": v(139.84, 29.81) * mm});
            skLineSegment(sketch, "E1921", {"start": v(139.84, 29.81) * mm, "end": v(140.64, 29.81) * mm});
            skLineSegment(sketch, "E1922", {"start": v(140.64, 29.81) * mm, "end": v(140.64, 30.81) * mm});
            skLineSegment(sketch, "E1923", {"start": v(140.64, 30.81) * mm, "end": v(154.64, 30.81) * mm});
            skLineSegment(sketch, "E1924", {"start": v(154.64, 30.81) * mm, "end": v(154.64, 29.81) * mm});
            skLineSegment(sketch, "E1925", {"start": v(154.64, 29.81) * mm, "end": v(155.44, 29.81) * mm});
            skLineSegment(sketch, "E1926", {"start": v(155.44, 29.81) * mm, "end": v(155.44, 26.71) * mm});
            skLineSegment(sketch, "E1927", {"start": v(155.44, 26.71) * mm, "end": v(154.64, 26.71) * mm});
            skLineSegment(sketch, "E1928", {"start": v(154.64, 26.71) * mm, "end": v(154.64, 20.91) * mm});
            skLineSegment(sketch, "E1929", {"start": v(154.64, 20.91) * mm, "end": v(155.44, 20.91) * mm});
            skLineSegment(sketch, "E1930", {"start": v(155.44, 20.91) * mm, "end": v(155.44, 17.81) * mm});
            skLineSegment(sketch, "E1931", {"start": v(155.44, 17.81) * mm, "end": v(154.64, 17.81) * mm});
            skLineSegment(sketch, "E1932", {"start": v(154.64, -20.29) * mm, "end": v(154.64, -21.29) * mm});
            skLineSegment(sketch, "E1933", {"start": v(154.64, -21.29) * mm, "end": v(140.64, -21.29) * mm});
            skLineSegment(sketch, "E1934", {"start": v(140.64, -21.29) * mm, "end": v(140.64, -20.29) * mm});
            skLineSegment(sketch, "E1935", {"start": v(140.64, -20.29) * mm, "end": v(139.84, -20.29) * mm});
            skLineSegment(sketch, "E1936", {"start": v(139.84, -20.29) * mm, "end": v(139.84, -17.19) * mm});
            skLineSegment(sketch, "E1937", {"start": v(139.84, -17.19) * mm, "end": v(140.64, -17.19) * mm});
            skLineSegment(sketch, "E1938", {"start": v(140.64, -17.19) * mm, "end": v(140.64, -11.39) * mm});
            skLineSegment(sketch, "E1939", {"start": v(140.64, -11.39) * mm, "end": v(139.84, -11.39) * mm});
            skLineSegment(sketch, "E1940", {"start": v(139.84, -11.39) * mm, "end": v(139.84, -8.29) * mm});
            skLineSegment(sketch, "E1941", {"start": v(139.84, -8.29) * mm, "end": v(140.64, -8.29) * mm});
            skLineSegment(sketch, "E1942", {"start": v(140.64, -8.29) * mm, "end": v(140.64, -7.29) * mm});
            skLineSegment(sketch, "E1943", {"start": v(140.64, -7.29) * mm, "end": v(154.64, -7.29) * mm});
            skLineSegment(sketch, "E1944", {"start": v(154.64, -7.29) * mm, "end": v(154.64, -8.29) * mm});
            skLineSegment(sketch, "E1945", {"start": v(154.64, -8.29) * mm, "end": v(155.44, -8.29) * mm});
            skLineSegment(sketch, "E1946", {"start": v(155.44, -8.29) * mm, "end": v(155.44, -11.39) * mm});
            skLineSegment(sketch, "E1947", {"start": v(155.44, -11.39) * mm, "end": v(154.64, -11.39) * mm});
            skLineSegment(sketch, "E1948", {"start": v(154.64, -11.39) * mm, "end": v(154.64, -17.19) * mm});
            skLineSegment(sketch, "E1949", {"start": v(154.64, -17.19) * mm, "end": v(155.44, -17.19) * mm});
            skLineSegment(sketch, "E1950", {"start": v(155.44, -17.19) * mm, "end": v(155.44, -20.29) * mm});
            skLineSegment(sketch, "E1951", {"start": v(155.44, -20.29) * mm, "end": v(154.64, -20.29) * mm});
            skLineSegment(sketch, "E1952", {"start": v(154.64, -1.24) * mm, "end": v(154.64, -2.24) * mm});
            skLineSegment(sketch, "E1953", {"start": v(154.64, -2.24) * mm, "end": v(140.64, -2.24) * mm});
            skLineSegment(sketch, "E1954", {"start": v(140.64, -2.24) * mm, "end": v(140.64, -1.24) * mm});
            skLineSegment(sketch, "E1955", {"start": v(140.64, -1.24) * mm, "end": v(139.84, -1.24) * mm});
            skLineSegment(sketch, "E1956", {"start": v(139.84, -1.24) * mm, "end": v(139.84, 1.86) * mm});
            skLineSegment(sketch, "E1957", {"start": v(139.84, 1.86) * mm, "end": v(140.64, 1.86) * mm});
            skLineSegment(sketch, "E1958", {"start": v(140.64, 1.86) * mm, "end": v(140.64, 7.66) * mm});
            skLineSegment(sketch, "E1959", {"start": v(140.64, 7.66) * mm, "end": v(139.84, 7.66) * mm});
            skLineSegment(sketch, "E1960", {"start": v(139.84, 7.66) * mm, "end": v(139.84, 10.76) * mm});
            skLineSegment(sketch, "E1961", {"start": v(139.84, 10.76) * mm, "end": v(140.64, 10.76) * mm});
            skLineSegment(sketch, "E1962", {"start": v(140.64, 10.76) * mm, "end": v(140.64, 11.76) * mm});
            skLineSegment(sketch, "E1963", {"start": v(140.64, 11.76) * mm, "end": v(154.64, 11.76) * mm});
            skLineSegment(sketch, "E1964", {"start": v(154.64, 11.76) * mm, "end": v(154.64, 10.76) * mm});
            skLineSegment(sketch, "E1965", {"start": v(154.64, 10.76) * mm, "end": v(155.44, 10.76) * mm});
            skLineSegment(sketch, "E1966", {"start": v(155.44, 10.76) * mm, "end": v(155.44, 7.66) * mm});
            skLineSegment(sketch, "E1967", {"start": v(155.44, 7.66) * mm, "end": v(154.64, 7.66) * mm});
            skLineSegment(sketch, "E1968", {"start": v(154.64, 7.66) * mm, "end": v(154.64, 1.86) * mm});
            skLineSegment(sketch, "E1969", {"start": v(154.64, 1.86) * mm, "end": v(155.44, 1.86) * mm});
            skLineSegment(sketch, "E1970", {"start": v(155.44, 1.86) * mm, "end": v(155.44, -1.24) * mm});
            skLineSegment(sketch, "E1971", {"start": v(155.44, -1.24) * mm, "end": v(154.64, -1.24) * mm});
            skLineSegment(sketch, "E1972", {"start": v(154.64, -39.34) * mm, "end": v(154.64, -40.34) * mm});
            skLineSegment(sketch, "E1973", {"start": v(154.64, -40.34) * mm, "end": v(140.64, -40.34) * mm});
            skLineSegment(sketch, "E1974", {"start": v(140.64, -40.34) * mm, "end": v(140.64, -39.34) * mm});
            skLineSegment(sketch, "E1975", {"start": v(140.64, -39.34) * mm, "end": v(139.84, -39.34) * mm});
            skLineSegment(sketch, "E1976", {"start": v(139.84, -39.34) * mm, "end": v(139.84, -36.24) * mm});
            skLineSegment(sketch, "E1977", {"start": v(139.84, -36.24) * mm, "end": v(140.64, -36.24) * mm});
            skLineSegment(sketch, "E1978", {"start": v(140.64, -36.24) * mm, "end": v(140.64, -30.44) * mm});
            skLineSegment(sketch, "E1979", {"start": v(140.64, -30.44) * mm, "end": v(139.84, -30.44) * mm});
            skLineSegment(sketch, "E1980", {"start": v(139.84, -30.44) * mm, "end": v(139.84, -27.34) * mm});
            skLineSegment(sketch, "E1981", {"start": v(139.84, -27.34) * mm, "end": v(140.64, -27.34) * mm});
            skLineSegment(sketch, "E1982", {"start": v(140.64, -27.34) * mm, "end": v(140.64, -26.34) * mm});
            skLineSegment(sketch, "E1983", {"start": v(140.64, -26.34) * mm, "end": v(154.64, -26.34) * mm});
            skLineSegment(sketch, "E1984", {"start": v(154.64, -26.34) * mm, "end": v(154.64, -27.34) * mm});
            skLineSegment(sketch, "E1985", {"start": v(154.64, -27.34) * mm, "end": v(155.44, -27.34) * mm});
            skLineSegment(sketch, "E1986", {"start": v(155.44, -27.34) * mm, "end": v(155.44, -30.44) * mm});
            skLineSegment(sketch, "E1987", {"start": v(155.44, -30.44) * mm, "end": v(154.64, -30.44) * mm});
            skLineSegment(sketch, "E1988", {"start": v(154.64, -30.44) * mm, "end": v(154.64, -36.24) * mm});
            skLineSegment(sketch, "E1989", {"start": v(154.64, -36.24) * mm, "end": v(155.44, -36.24) * mm});
            skLineSegment(sketch, "E1990", {"start": v(155.44, -36.24) * mm, "end": v(155.44, -39.34) * mm});
            skLineSegment(sketch, "E1991", {"start": v(155.44, -39.34) * mm, "end": v(154.64, -39.34) * mm});
            skLineSegment(sketch, "E1992", {"start": v(172.39, -52.89) * mm, "end": v(172.39, -59.16) * mm});
            skLineSegment(sketch, "E1993", {"start": v(172.39, -59.16) * mm, "end": v(170.76, -59.16) * mm});
            skLineSegment(sketch, "E1994", {"start": v(170.76, -59.16) * mm, "end": v(170.76, -60.14) * mm});
            skLineSegment(sketch, "E1995", {"start": v(170.76, -60.14) * mm, "end": v(167.46, -60.14) * mm});
            skLineSegment(sketch, "E1996", {"start": v(167.46, -60.14) * mm, "end": v(167.46, -59.16) * mm});
            skLineSegment(sketch, "E1997", {"start": v(167.46, -59.16) * mm, "end": v(165.74, -59.16) * mm});
            skLineSegment(sketch, "E1998", {"start": v(165.74, -59.16) * mm, "end": v(165.74, -58.36) * mm});
            skLineSegment(sketch, "E1999", {"start": v(165.74, -58.36) * mm, "end": v(164.96, -58.36) * mm});
            skLineSegment(sketch, "E2000", {"start": v(164.96, -58.36) * mm, "end": v(164.96, -58.39) * mm});
            skLineSegment(sketch, "E2001", {"start": v(164.96, -58.39) * mm, "end": v(164.16, -58.39) * mm});
            skLineSegment(sketch, "E2002", {"start": v(164.16, -58.39) * mm, "end": v(164.16, -59.39) * mm});
            skLineSegment(sketch, "E2003", {"start": v(164.16, -59.39) * mm, "end": v(150.16, -59.39) * mm});
            skLineSegment(sketch, "E2004", {"start": v(150.16, -59.39) * mm, "end": v(150.16, -58.39) * mm});
            skLineSegment(sketch, "E2005", {"start": v(150.16, -58.39) * mm, "end": v(149.36, -58.39) * mm});
            skLineSegment(sketch, "E2006", {"start": v(149.36, -58.39) * mm, "end": v(149.36, -58.36) * mm});
            skLineSegment(sketch, "E2007", {"start": v(149.36, -58.36) * mm, "end": v(148.59, -58.36) * mm});
            skLineSegment(sketch, "E2008", {"start": v(148.59, -58.36) * mm, "end": v(148.59, -59.16) * mm});
            skLineSegment(sketch, "E2009", {"start": v(148.59, -59.16) * mm, "end": v(146.86, -59.16) * mm});
            skLineSegment(sketch, "E2010", {"start": v(146.86, -59.16) * mm, "end": v(146.86, -60.14) * mm});
            skLineSegment(sketch, "E2011", {"start": v(146.86, -60.14) * mm, "end": v(143.56, -60.14) * mm});
            skLineSegment(sketch, "E2012", {"start": v(143.56, -60.14) * mm, "end": v(143.56, -59.16) * mm});
            skLineSegment(sketch, "E2013", {"start": v(143.56, -59.16) * mm, "end": v(141.94, -59.16) * mm});
            skLineSegment(sketch, "E2014", {"start": v(141.94, -59.16) * mm, "end": v(141.94, -52.89) * mm});
            skLineSegment(sketch, "E2015", {"start": v(141.94, -52.89) * mm, "end": v(141.06, -52.89) * mm});
            skLineSegment(sketch, "E2016", {"start": v(141.06, -52.89) * mm, "end": v(141.06, -50.09) * mm});
            skLineSegment(sketch, "E2017", {"start": v(141.06, -50.09) * mm, "end": v(141.94, -50.09) * mm});
            skLineSegment(sketch, "E2018", {"start": v(141.94, -50.09) * mm, "end": v(141.94, -46.86) * mm});
            skLineSegment(sketch, "E2019", {"start": v(141.94, -46.86) * mm, "end": v(143.56, -46.86) * mm});
            skLineSegment(sketch, "E2020", {"start": v(143.56, -46.86) * mm, "end": v(143.56, -45.94) * mm});
            skLineSegment(sketch, "E2021", {"start": v(143.56, -45.94) * mm, "end": v(146.86, -45.94) * mm});
            skLineSegment(sketch, "E2022", {"start": v(146.86, -45.94) * mm, "end": v(146.86, -46.86) * mm});
            skLineSegment(sketch, "E2023", {"start": v(146.86, -46.86) * mm, "end": v(148.59, -46.86) * mm});
            skLineSegment(sketch, "E2024", {"start": v(148.59, -46.86) * mm, "end": v(148.59, -47.66) * mm});
            skLineSegment(sketch, "E2025", {"start": v(148.59, -47.66) * mm, "end": v(149.36, -47.66) * mm});
            skLineSegment(sketch, "E2026", {"start": v(149.36, -47.66) * mm, "end": v(149.36, -46.39) * mm});
            skLineSegment(sketch, "E2027", {"start": v(149.36, -46.39) * mm, "end": v(150.16, -46.39) * mm});
            skLineSegment(sketch, "E2028", {"start": v(150.16, -46.39) * mm, "end": v(150.16, -45.39) * mm});
            skLineSegment(sketch, "E2029", {"start": v(150.16, -45.39) * mm, "end": v(164.16, -45.39) * mm});
            skLineSegment(sketch, "E2030", {"start": v(164.16, -45.39) * mm, "end": v(164.16, -46.39) * mm});
            skLineSegment(sketch, "E2031", {"start": v(164.16, -46.39) * mm, "end": v(164.96, -46.39) * mm});
            skLineSegment(sketch, "E2032", {"start": v(164.96, -46.39) * mm, "end": v(164.96, -47.66) * mm});
            skLineSegment(sketch, "E2033", {"start": v(164.96, -47.66) * mm, "end": v(165.74, -47.66) * mm});
            skLineSegment(sketch, "E2034", {"start": v(165.74, -47.66) * mm, "end": v(165.74, -46.86) * mm});
            skLineSegment(sketch, "E2035", {"start": v(165.74, -46.86) * mm, "end": v(167.46, -46.86) * mm});
            skLineSegment(sketch, "E2036", {"start": v(167.46, -46.86) * mm, "end": v(167.46, -45.94) * mm});
            skLineSegment(sketch, "E2037", {"start": v(167.46, -45.94) * mm, "end": v(170.76, -45.94) * mm});
            skLineSegment(sketch, "E2038", {"start": v(170.76, -45.94) * mm, "end": v(170.76, -46.86) * mm});
            skLineSegment(sketch, "E2039", {"start": v(170.76, -46.86) * mm, "end": v(172.39, -46.86) * mm});
            skLineSegment(sketch, "E2040", {"start": v(172.39, -46.86) * mm, "end": v(172.39, -50.09) * mm});
            skLineSegment(sketch, "E2041", {"start": v(172.39, -50.09) * mm, "end": v(173.26, -50.09) * mm});
            skLineSegment(sketch, "E2042", {"start": v(173.26, -50.09) * mm, "end": v(173.26, -52.89) * mm});
            skLineSegment(sketch, "E2043", {"start": v(173.26, -52.89) * mm, "end": v(172.39, -52.89) * mm});
            skLineSegment(sketch, "E2044", {"start": v(173.69, 17.81) * mm, "end": v(173.69, 16.81) * mm});
            skLineSegment(sketch, "E2045", {"start": v(173.69, 16.81) * mm, "end": v(159.69, 16.81) * mm});
            skLineSegment(sketch, "E2046", {"start": v(159.69, 16.81) * mm, "end": v(159.69, 17.81) * mm});
            skLineSegment(sketch, "E2047", {"start": v(159.69, 17.81) * mm, "end": v(158.89, 17.81) * mm});
            skLineSegment(sketch, "E2048", {"start": v(158.89, 17.81) * mm, "end": v(158.89, 20.91) * mm});
            skLineSegment(sketch, "E2049", {"start": v(158.89, 20.91) * mm, "end": v(159.69, 20.91) * mm});
            skLineSegment(sketch, "E2050", {"start": v(159.69, 20.91) * mm, "end": v(159.69, 26.71) * mm});
            skLineSegment(sketch, "E2051", {"start": v(159.69, 26.71) * mm, "end": v(158.89, 26.71) * mm});
            skLineSegment(sketch, "E2052", {"start": v(158.89, 26.71) * mm, "end": v(158.89, 29.81) * mm});
            skLineSegment(sketch, "E2053", {"start": v(158.89, 29.81) * mm, "end": v(159.69, 29.81) * mm});
            skLineSegment(sketch, "E2054", {"start": v(159.69, 29.81) * mm, "end": v(159.69, 30.81) * mm});
            skLineSegment(sketch, "E2055", {"start": v(159.69, 30.81) * mm, "end": v(173.69, 30.81) * mm});
            skLineSegment(sketch, "E2056", {"start": v(173.69, 30.81) * mm, "end": v(173.69, 29.81) * mm});
            skLineSegment(sketch, "E2057", {"start": v(173.69, 29.81) * mm, "end": v(174.49, 29.81) * mm});
            skLineSegment(sketch, "E2058", {"start": v(174.49, 29.81) * mm, "end": v(174.49, 26.71) * mm});
            skLineSegment(sketch, "E2059", {"start": v(174.49, 26.71) * mm, "end": v(173.69, 26.71) * mm});
            skLineSegment(sketch, "E2060", {"start": v(173.69, 26.71) * mm, "end": v(173.69, 20.91) * mm});
            skLineSegment(sketch, "E2061", {"start": v(173.69, 20.91) * mm, "end": v(174.49, 20.91) * mm});
            skLineSegment(sketch, "E2062", {"start": v(174.49, 20.91) * mm, "end": v(174.49, 17.81) * mm});
            skLineSegment(sketch, "E2063", {"start": v(174.49, 17.81) * mm, "end": v(173.69, 17.81) * mm});
            skLineSegment(sketch, "E2064", {"start": v(173.69, -20.29) * mm, "end": v(173.69, -21.29) * mm});
            skLineSegment(sketch, "E2065", {"start": v(173.69, -21.29) * mm, "end": v(159.69, -21.29) * mm});
            skLineSegment(sketch, "E2066", {"start": v(159.69, -21.29) * mm, "end": v(159.69, -20.29) * mm});
            skLineSegment(sketch, "E2067", {"start": v(159.69, -20.29) * mm, "end": v(158.89, -20.29) * mm});
            skLineSegment(sketch, "E2068", {"start": v(158.89, -20.29) * mm, "end": v(158.89, -17.19) * mm});
            skLineSegment(sketch, "E2069", {"start": v(158.89, -17.19) * mm, "end": v(159.69, -17.19) * mm});
            skLineSegment(sketch, "E2070", {"start": v(159.69, -17.19) * mm, "end": v(159.69, -11.39) * mm});
            skLineSegment(sketch, "E2071", {"start": v(159.69, -11.39) * mm, "end": v(158.89, -11.39) * mm});
            skLineSegment(sketch, "E2072", {"start": v(158.89, -11.39) * mm, "end": v(158.89, -8.29) * mm});
            skLineSegment(sketch, "E2073", {"start": v(158.89, -8.29) * mm, "end": v(159.69, -8.29) * mm});
            skLineSegment(sketch, "E2074", {"start": v(159.69, -8.29) * mm, "end": v(159.69, -7.29) * mm});
            skLineSegment(sketch, "E2075", {"start": v(159.69, -7.29) * mm, "end": v(173.69, -7.29) * mm});
            skLineSegment(sketch, "E2076", {"start": v(173.69, -7.29) * mm, "end": v(173.69, -8.29) * mm});
            skLineSegment(sketch, "E2077", {"start": v(173.69, -8.29) * mm, "end": v(174.49, -8.29) * mm});
            skLineSegment(sketch, "E2078", {"start": v(174.49, -8.29) * mm, "end": v(174.49, -11.39) * mm});
            skLineSegment(sketch, "E2079", {"start": v(174.49, -11.39) * mm, "end": v(173.69, -11.39) * mm});
            skLineSegment(sketch, "E2080", {"start": v(173.69, -11.39) * mm, "end": v(173.69, -17.19) * mm});
            skLineSegment(sketch, "E2081", {"start": v(173.69, -17.19) * mm, "end": v(174.49, -17.19) * mm});
            skLineSegment(sketch, "E2082", {"start": v(174.49, -17.19) * mm, "end": v(174.49, -20.29) * mm});
            skLineSegment(sketch, "E2083", {"start": v(174.49, -20.29) * mm, "end": v(173.69, -20.29) * mm});
            skLineSegment(sketch, "E2084", {"start": v(173.69, -1.24) * mm, "end": v(173.69, -2.24) * mm});
            skLineSegment(sketch, "E2085", {"start": v(173.69, -2.24) * mm, "end": v(159.69, -2.24) * mm});
            skLineSegment(sketch, "E2086", {"start": v(159.69, -2.24) * mm, "end": v(159.69, -1.24) * mm});
            skLineSegment(sketch, "E2087", {"start": v(159.69, -1.24) * mm, "end": v(158.89, -1.24) * mm});
            skLineSegment(sketch, "E2088", {"start": v(158.89, -1.24) * mm, "end": v(158.89, 1.86) * mm});
            skLineSegment(sketch, "E2089", {"start": v(158.89, 1.86) * mm, "end": v(159.69, 1.86) * mm});
            skLineSegment(sketch, "E2090", {"start": v(159.69, 1.86) * mm, "end": v(159.69, 7.66) * mm});
            skLineSegment(sketch, "E2091", {"start": v(159.69, 7.66) * mm, "end": v(158.89, 7.66) * mm});
            skLineSegment(sketch, "E2092", {"start": v(158.89, 7.66) * mm, "end": v(158.89, 10.76) * mm});
            skLineSegment(sketch, "E2093", {"start": v(158.89, 10.76) * mm, "end": v(159.69, 10.76) * mm});
            skLineSegment(sketch, "E2094", {"start": v(159.69, 10.76) * mm, "end": v(159.69, 11.76) * mm});
            skLineSegment(sketch, "E2095", {"start": v(159.69, 11.76) * mm, "end": v(173.69, 11.76) * mm});
            skLineSegment(sketch, "E2096", {"start": v(173.69, 11.76) * mm, "end": v(173.69, 10.76) * mm});
            skLineSegment(sketch, "E2097", {"start": v(173.69, 10.76) * mm, "end": v(174.49, 10.76) * mm});
            skLineSegment(sketch, "E2098", {"start": v(174.49, 10.76) * mm, "end": v(174.49, 7.66) * mm});
            skLineSegment(sketch, "E2099", {"start": v(174.49, 7.66) * mm, "end": v(173.69, 7.66) * mm});
            skLineSegment(sketch, "E2100", {"start": v(173.69, 7.66) * mm, "end": v(173.69, 1.86) * mm});
            skLineSegment(sketch, "E2101", {"start": v(173.69, 1.86) * mm, "end": v(174.49, 1.86) * mm});
            skLineSegment(sketch, "E2102", {"start": v(174.49, 1.86) * mm, "end": v(174.49, -1.24) * mm});
            skLineSegment(sketch, "E2103", {"start": v(174.49, -1.24) * mm, "end": v(173.69, -1.24) * mm});
            skLineSegment(sketch, "E2104", {"start": v(173.69, -39.34) * mm, "end": v(173.69, -40.34) * mm});
            skLineSegment(sketch, "E2105", {"start": v(173.69, -40.34) * mm, "end": v(159.69, -40.34) * mm});
            skLineSegment(sketch, "E2106", {"start": v(159.69, -40.34) * mm, "end": v(159.69, -39.34) * mm});
            skLineSegment(sketch, "E2107", {"start": v(159.69, -39.34) * mm, "end": v(158.89, -39.34) * mm});
            skLineSegment(sketch, "E2108", {"start": v(158.89, -39.34) * mm, "end": v(158.89, -36.24) * mm});
            skLineSegment(sketch, "E2109", {"start": v(158.89, -36.24) * mm, "end": v(159.69, -36.24) * mm});
            skLineSegment(sketch, "E2110", {"start": v(159.69, -36.24) * mm, "end": v(159.69, -30.44) * mm});
            skLineSegment(sketch, "E2111", {"start": v(159.69, -30.44) * mm, "end": v(158.89, -30.44) * mm});
            skLineSegment(sketch, "E2112", {"start": v(158.89, -30.44) * mm, "end": v(158.89, -27.34) * mm});
            skLineSegment(sketch, "E2113", {"start": v(158.89, -27.34) * mm, "end": v(159.69, -27.34) * mm});
            skLineSegment(sketch, "E2114", {"start": v(159.69, -27.34) * mm, "end": v(159.69, -26.34) * mm});
            skLineSegment(sketch, "E2115", {"start": v(159.69, -26.34) * mm, "end": v(173.69, -26.34) * mm});
            skLineSegment(sketch, "E2116", {"start": v(173.69, -26.34) * mm, "end": v(173.69, -27.34) * mm});
            skLineSegment(sketch, "E2117", {"start": v(173.69, -27.34) * mm, "end": v(174.49, -27.34) * mm});
            skLineSegment(sketch, "E2118", {"start": v(174.49, -27.34) * mm, "end": v(174.49, -30.44) * mm});
            skLineSegment(sketch, "E2119", {"start": v(174.49, -30.44) * mm, "end": v(173.69, -30.44) * mm});
            skLineSegment(sketch, "E2120", {"start": v(173.69, -30.44) * mm, "end": v(173.69, -36.24) * mm});
            skLineSegment(sketch, "E2121", {"start": v(173.69, -36.24) * mm, "end": v(174.49, -36.24) * mm});
            skLineSegment(sketch, "E2122", {"start": v(174.49, -36.24) * mm, "end": v(174.49, -39.34) * mm});
            skLineSegment(sketch, "E2123", {"start": v(174.49, -39.34) * mm, "end": v(173.69, -39.34) * mm});
            skLineSegment(sketch, "E2124", {"start": v(192.74, -58.39) * mm, "end": v(192.74, -59.39) * mm});
            skLineSegment(sketch, "E2125", {"start": v(192.74, -59.39) * mm, "end": v(178.74, -59.39) * mm});
            skLineSegment(sketch, "E2126", {"start": v(178.74, -59.39) * mm, "end": v(178.74, -58.39) * mm});
            skLineSegment(sketch, "E2127", {"start": v(178.74, -58.39) * mm, "end": v(177.94, -58.39) * mm});
            skLineSegment(sketch, "E2128", {"start": v(177.94, -58.39) * mm, "end": v(177.94, -55.29) * mm});
            skLineSegment(sketch, "E2129", {"start": v(177.94, -55.29) * mm, "end": v(178.74, -55.29) * mm});
            skLineSegment(sketch, "E2130", {"start": v(178.74, -55.29) * mm, "end": v(178.74, -49.49) * mm});
            skLineSegment(sketch, "E2131", {"start": v(178.74, -49.49) * mm, "end": v(177.94, -49.49) * mm});
            skLineSegment(sketch, "E2132", {"start": v(177.94, -49.49) * mm, "end": v(177.94, -46.39) * mm});
            skLineSegment(sketch, "E2133", {"start": v(177.94, -46.39) * mm, "end": v(178.74, -46.39) * mm});
            skLineSegment(sketch, "E2134", {"start": v(178.74, -46.39) * mm, "end": v(178.74, -45.39) * mm});
            skLineSegment(sketch, "E2135", {"start": v(178.74, -45.39) * mm, "end": v(192.74, -45.39) * mm});
            skLineSegment(sketch, "E2136", {"start": v(192.74, -45.39) * mm, "end": v(192.74, -46.39) * mm});
            skLineSegment(sketch, "E2137", {"start": v(192.74, -46.39) * mm, "end": v(193.54, -46.39) * mm});
            skLineSegment(sketch, "E2138", {"start": v(193.54, -46.39) * mm, "end": v(193.54, -49.49) * mm});
            skLineSegment(sketch, "E2139", {"start": v(193.54, -49.49) * mm, "end": v(192.74, -49.49) * mm});
            skLineSegment(sketch, "E2140", {"start": v(192.74, -49.49) * mm, "end": v(192.74, -55.29) * mm});
            skLineSegment(sketch, "E2141", {"start": v(192.74, -55.29) * mm, "end": v(193.54, -55.29) * mm});
            skLineSegment(sketch, "E2142", {"start": v(193.54, -55.29) * mm, "end": v(193.54, -58.39) * mm});
            skLineSegment(sketch, "E2143", {"start": v(193.54, -58.39) * mm, "end": v(192.74, -58.39) * mm});
            skLineSegment(sketch, "E2144", {"start": v(192.74, 17.81) * mm, "end": v(192.74, 16.81) * mm});
            skLineSegment(sketch, "E2145", {"start": v(192.74, 16.81) * mm, "end": v(178.74, 16.81) * mm});
            skLineSegment(sketch, "E2146", {"start": v(178.74, 16.81) * mm, "end": v(178.74, 17.81) * mm});
            skLineSegment(sketch, "E2147", {"start": v(178.74, 17.81) * mm, "end": v(177.94, 17.81) * mm});
            skLineSegment(sketch, "E2148", {"start": v(177.94, 17.81) * mm, "end": v(177.94, 20.91) * mm});
            skLineSegment(sketch, "E2149", {"start": v(177.94, 20.91) * mm, "end": v(178.74, 20.91) * mm});
            skLineSegment(sketch, "E2150", {"start": v(178.74, 20.91) * mm, "end": v(178.74, 26.71) * mm});
            skLineSegment(sketch, "E2151", {"start": v(178.74, 26.71) * mm, "end": v(177.94, 26.71) * mm});
            skLineSegment(sketch, "E2152", {"start": v(177.94, 26.71) * mm, "end": v(177.94, 29.81) * mm});
            skLineSegment(sketch, "E2153", {"start": v(177.94, 29.81) * mm, "end": v(178.74, 29.81) * mm});
            skLineSegment(sketch, "E2154", {"start": v(178.74, 29.81) * mm, "end": v(178.74, 30.81) * mm});
            skLineSegment(sketch, "E2155", {"start": v(178.74, 30.81) * mm, "end": v(192.74, 30.81) * mm});
            skLineSegment(sketch, "E2156", {"start": v(192.74, 30.81) * mm, "end": v(192.74, 29.81) * mm});
            skLineSegment(sketch, "E2157", {"start": v(192.74, 29.81) * mm, "end": v(193.54, 29.81) * mm});
            skLineSegment(sketch, "E2158", {"start": v(193.54, 29.81) * mm, "end": v(193.54, 26.71) * mm});
            skLineSegment(sketch, "E2159", {"start": v(193.54, 26.71) * mm, "end": v(192.74, 26.71) * mm});
            skLineSegment(sketch, "E2160", {"start": v(192.74, 26.71) * mm, "end": v(192.74, 20.91) * mm});
            skLineSegment(sketch, "E2161", {"start": v(192.74, 20.91) * mm, "end": v(193.54, 20.91) * mm});
            skLineSegment(sketch, "E2162", {"start": v(193.54, 20.91) * mm, "end": v(193.54, 17.81) * mm});
            skLineSegment(sketch, "E2163", {"start": v(193.54, 17.81) * mm, "end": v(192.74, 17.81) * mm});
            skLineSegment(sketch, "E2164", {"start": v(192.74, -20.29) * mm, "end": v(192.74, -21.29) * mm});
            skLineSegment(sketch, "E2165", {"start": v(192.74, -21.29) * mm, "end": v(178.74, -21.29) * mm});
            skLineSegment(sketch, "E2166", {"start": v(178.74, -21.29) * mm, "end": v(178.74, -20.29) * mm});
            skLineSegment(sketch, "E2167", {"start": v(178.74, -20.29) * mm, "end": v(177.94, -20.29) * mm});
            skLineSegment(sketch, "E2168", {"start": v(177.94, -20.29) * mm, "end": v(177.94, -17.19) * mm});
            skLineSegment(sketch, "E2169", {"start": v(177.94, -17.19) * mm, "end": v(178.74, -17.19) * mm});
            skLineSegment(sketch, "E2170", {"start": v(178.74, -17.19) * mm, "end": v(178.74, -11.39) * mm});
            skLineSegment(sketch, "E2171", {"start": v(178.74, -11.39) * mm, "end": v(177.94, -11.39) * mm});
            skLineSegment(sketch, "E2172", {"start": v(177.94, -11.39) * mm, "end": v(177.94, -8.29) * mm});
            skLineSegment(sketch, "E2173", {"start": v(177.94, -8.29) * mm, "end": v(178.74, -8.29) * mm});
            skLineSegment(sketch, "E2174", {"start": v(178.74, -8.29) * mm, "end": v(178.74, -7.29) * mm});
            skLineSegment(sketch, "E2175", {"start": v(178.74, -7.29) * mm, "end": v(192.74, -7.29) * mm});
            skLineSegment(sketch, "E2176", {"start": v(192.74, -7.29) * mm, "end": v(192.74, -8.29) * mm});
            skLineSegment(sketch, "E2177", {"start": v(192.74, -8.29) * mm, "end": v(193.54, -8.29) * mm});
            skLineSegment(sketch, "E2178", {"start": v(193.54, -8.29) * mm, "end": v(193.54, -11.39) * mm});
            skLineSegment(sketch, "E2179", {"start": v(193.54, -11.39) * mm, "end": v(192.74, -11.39) * mm});
            skLineSegment(sketch, "E2180", {"start": v(192.74, -11.39) * mm, "end": v(192.74, -17.19) * mm});
            skLineSegment(sketch, "E2181", {"start": v(192.74, -17.19) * mm, "end": v(193.54, -17.19) * mm});
            skLineSegment(sketch, "E2182", {"start": v(193.54, -17.19) * mm, "end": v(193.54, -20.29) * mm});
            skLineSegment(sketch, "E2183", {"start": v(193.54, -20.29) * mm, "end": v(192.74, -20.29) * mm});
            skLineSegment(sketch, "E2184", {"start": v(192.74, -1.24) * mm, "end": v(192.74, -2.24) * mm});
            skLineSegment(sketch, "E2185", {"start": v(192.74, -2.24) * mm, "end": v(178.74, -2.24) * mm});
            skLineSegment(sketch, "E2186", {"start": v(178.74, -2.24) * mm, "end": v(178.74, -1.24) * mm});
            skLineSegment(sketch, "E2187", {"start": v(178.74, -1.24) * mm, "end": v(177.94, -1.24) * mm});
            skLineSegment(sketch, "E2188", {"start": v(177.94, -1.24) * mm, "end": v(177.94, 1.86) * mm});
            skLineSegment(sketch, "E2189", {"start": v(177.94, 1.86) * mm, "end": v(178.74, 1.86) * mm});
            skLineSegment(sketch, "E2190", {"start": v(178.74, 1.86) * mm, "end": v(178.74, 7.66) * mm});
            skLineSegment(sketch, "E2191", {"start": v(178.74, 7.66) * mm, "end": v(177.94, 7.66) * mm});
            skLineSegment(sketch, "E2192", {"start": v(177.94, 7.66) * mm, "end": v(177.94, 10.76) * mm});
            skLineSegment(sketch, "E2193", {"start": v(177.94, 10.76) * mm, "end": v(178.74, 10.76) * mm});
            skLineSegment(sketch, "E2194", {"start": v(178.74, 10.76) * mm, "end": v(178.74, 11.76) * mm});
            skLineSegment(sketch, "E2195", {"start": v(178.74, 11.76) * mm, "end": v(192.74, 11.76) * mm});
            skLineSegment(sketch, "E2196", {"start": v(192.74, 11.76) * mm, "end": v(192.74, 10.76) * mm});
            skLineSegment(sketch, "E2197", {"start": v(192.74, 10.76) * mm, "end": v(193.54, 10.76) * mm});
            skLineSegment(sketch, "E2198", {"start": v(193.54, 10.76) * mm, "end": v(193.54, 7.66) * mm});
            skLineSegment(sketch, "E2199", {"start": v(193.54, 7.66) * mm, "end": v(192.74, 7.66) * mm});
            skLineSegment(sketch, "E2200", {"start": v(192.74, 7.66) * mm, "end": v(192.74, 1.86) * mm});
            skLineSegment(sketch, "E2201", {"start": v(192.74, 1.86) * mm, "end": v(193.54, 1.86) * mm});
            skLineSegment(sketch, "E2202", {"start": v(193.54, 1.86) * mm, "end": v(193.54, -1.24) * mm});
            skLineSegment(sketch, "E2203", {"start": v(193.54, -1.24) * mm, "end": v(192.74, -1.24) * mm});
            skLineSegment(sketch, "E2204", {"start": v(192.74, -39.34) * mm, "end": v(192.74, -40.34) * mm});
            skLineSegment(sketch, "E2205", {"start": v(192.74, -40.34) * mm, "end": v(178.74, -40.34) * mm});
            skLineSegment(sketch, "E2206", {"start": v(178.74, -40.34) * mm, "end": v(178.74, -39.34) * mm});
            skLineSegment(sketch, "E2207", {"start": v(178.74, -39.34) * mm, "end": v(177.94, -39.34) * mm});
            skLineSegment(sketch, "E2208", {"start": v(177.94, -39.34) * mm, "end": v(177.94, -36.24) * mm});
            skLineSegment(sketch, "E2209", {"start": v(177.94, -36.24) * mm, "end": v(178.74, -36.24) * mm});
            skLineSegment(sketch, "E2210", {"start": v(178.74, -36.24) * mm, "end": v(178.74, -30.44) * mm});
            skLineSegment(sketch, "E2211", {"start": v(178.74, -30.44) * mm, "end": v(177.94, -30.44) * mm});
            skLineSegment(sketch, "E2212", {"start": v(177.94, -30.44) * mm, "end": v(177.94, -27.34) * mm});
            skLineSegment(sketch, "E2213", {"start": v(177.94, -27.34) * mm, "end": v(178.74, -27.34) * mm});
            skLineSegment(sketch, "E2214", {"start": v(178.74, -27.34) * mm, "end": v(178.74, -26.34) * mm});
            skLineSegment(sketch, "E2215", {"start": v(178.74, -26.34) * mm, "end": v(192.74, -26.34) * mm});
            skLineSegment(sketch, "E2216", {"start": v(192.74, -26.34) * mm, "end": v(192.74, -27.34) * mm});
            skLineSegment(sketch, "E2217", {"start": v(192.74, -27.34) * mm, "end": v(193.54, -27.34) * mm});
            skLineSegment(sketch, "E2218", {"start": v(193.54, -27.34) * mm, "end": v(193.54, -30.44) * mm});
            skLineSegment(sketch, "E2219", {"start": v(193.54, -30.44) * mm, "end": v(192.74, -30.44) * mm});
            skLineSegment(sketch, "E2220", {"start": v(192.74, -30.44) * mm, "end": v(192.74, -36.24) * mm});
            skLineSegment(sketch, "E2221", {"start": v(192.74, -36.24) * mm, "end": v(193.54, -36.24) * mm});
            skLineSegment(sketch, "E2222", {"start": v(193.54, -36.24) * mm, "end": v(193.54, -39.34) * mm});
            skLineSegment(sketch, "E2223", {"start": v(193.54, -39.34) * mm, "end": v(192.74, -39.34) * mm});
            skLineSegment(sketch, "E2224", {"start": v(210.79, -11.76) * mm, "end": v(210.79, -12.56) * mm});
            skLineSegment(sketch, "E2225", {"start": v(210.79, -12.56) * mm, "end": v(209.52, -12.56) * mm});
            skLineSegment(sketch, "E2226", {"start": v(209.52, -12.56) * mm, "end": v(209.52, -13.34) * mm});
            skLineSegment(sketch, "E2227", {"start": v(209.52, -13.34) * mm, "end": v(210.32, -13.34) * mm});
            skLineSegment(sketch, "E2228", {"start": v(210.32, -13.34) * mm, "end": v(210.32, -15.06) * mm});
            skLineSegment(sketch, "E2229", {"start": v(210.32, -15.06) * mm, "end": v(211.24, -15.06) * mm});
            skLineSegment(sketch, "E2230", {"start": v(211.24, -15.06) * mm, "end": v(211.24, -18.36) * mm});
            skLineSegment(sketch, "E2231", {"start": v(211.24, -18.36) * mm, "end": v(210.32, -18.36) * mm});
            skLineSegment(sketch, "E2232", {"start": v(210.32, -18.36) * mm, "end": v(210.32, -19.99) * mm});
            skLineSegment(sketch, "E2233", {"start": v(210.32, -19.99) * mm, "end": v(207.09, -19.99) * mm});
            skLineSegment(sketch, "E2234", {"start": v(207.09, -19.99) * mm, "end": v(207.09, -20.86) * mm});
            skLineSegment(sketch, "E2235", {"start": v(207.09, -20.86) * mm, "end": v(204.29, -20.86) * mm});
            skLineSegment(sketch, "E2236", {"start": v(204.29, -20.86) * mm, "end": v(204.29, -19.99) * mm});
            skLineSegment(sketch, "E2237", {"start": v(204.29, -19.99) * mm, "end": v(198.02, -19.99) * mm});
            skLineSegment(sketch, "E2238", {"start": v(198.02, -19.99) * mm, "end": v(198.02, -18.36) * mm});
            skLineSegment(sketch, "E2239", {"start": v(198.02, -18.36) * mm, "end": v(197.04, -18.36) * mm});
            skLineSegment(sketch, "E2240", {"start": v(197.04, -18.36) * mm, "end": v(197.04, -15.06) * mm});
            skLineSegment(sketch, "E2241", {"start": v(197.04, -15.06) * mm, "end": v(198.02, -15.06) * mm});
            skLineSegment(sketch, "E2242", {"start": v(198.02, -15.06) * mm, "end": v(198.02, -13.34) * mm});
            skLineSegment(sketch, "E2243", {"start": v(198.02, -13.34) * mm, "end": v(198.82, -13.34) * mm});
            skLineSegment(sketch, "E2244", {"start": v(198.82, -13.34) * mm, "end": v(198.82, -12.56) * mm});
            skLineSegment(sketch, "E2245", {"start": v(198.82, -12.56) * mm, "end": v(198.79, -12.56) * mm});
            skLineSegment(sketch, "E2246", {"start": v(198.79, -12.56) * mm, "end": v(198.79, -11.76) * mm});
            skLineSegment(sketch, "E2247", {"start": v(198.79, -11.76) * mm, "end": v(197.79, -11.76) * mm});
            skLineSegment(sketch, "E2248", {"start": v(197.79, -11.76) * mm, "end": v(197.79, 2.24) * mm});
            skLineSegment(sketch, "E2249", {"start": v(197.79, 2.24) * mm, "end": v(198.79, 2.24) * mm});
            skLineSegment(sketch, "E2250", {"start": v(198.79, 2.24) * mm, "end": v(198.79, 3.04) * mm});
            skLineSegment(sketch, "E2251", {"start": v(198.79, 3.04) * mm, "end": v(198.82, 3.04) * mm});
            skLineSegment(sketch, "E2252", {"start": v(198.82, 3.04) * mm, "end": v(198.82, 3.81) * mm});
            skLineSegment(sketch, "E2253", {"start": v(198.82, 3.81) * mm, "end": v(198.02, 3.81) * mm});
            skLineSegment(sketch, "E2254", {"start": v(198.02, 3.81) * mm, "end": v(198.02, 5.54) * mm});
            skLineSegment(sketch, "E2255", {"start": v(198.02, 5.54) * mm, "end": v(197.04, 5.54) * mm});
            skLineSegment(sketch, "E2256", {"start": v(197.04, 5.54) * mm, "end": v(197.04, 8.84) * mm});
            skLineSegment(sketch, "E2257", {"start": v(197.04, 8.84) * mm, "end": v(198.02, 8.84) * mm});
            skLineSegment(sketch, "E2258", {"start": v(198.02, 8.84) * mm, "end": v(198.02, 10.46) * mm});
            skLineSegment(sketch, "E2259", {"start": v(198.02, 10.46) * mm, "end": v(204.29, 10.46) * mm});
            skLineSegment(sketch, "E2260", {"start": v(204.29, 10.46) * mm, "end": v(204.29, 11.34) * mm});
            skLineSegment(sketch, "E2261", {"start": v(204.29, 11.34) * mm, "end": v(207.09, 11.34) * mm});
            skLineSegment(sketch, "E2262", {"start": v(207.09, 11.34) * mm, "end": v(207.09, 10.46) * mm});
            skLineSegment(sketch, "E2263", {"start": v(207.09, 10.46) * mm, "end": v(210.32, 10.46) * mm});
            skLineSegment(sketch, "E2264", {"start": v(210.32, 10.46) * mm, "end": v(210.32, 8.84) * mm});
            skLineSegment(sketch, "E2265", {"start": v(210.32, 8.84) * mm, "end": v(211.24, 8.84) * mm});
            skLineSegment(sketch, "E2266", {"start": v(211.24, 8.84) * mm, "end": v(211.24, 5.54) * mm});
            skLineSegment(sketch, "E2267", {"start": v(211.24, 5.54) * mm, "end": v(210.32, 5.54) * mm});
            skLineSegment(sketch, "E2268", {"start": v(210.32, 5.54) * mm, "end": v(210.32, 3.81) * mm});
            skLineSegment(sketch, "E2269", {"start": v(210.32, 3.81) * mm, "end": v(209.52, 3.81) * mm});
            skLineSegment(sketch, "E2270", {"start": v(209.52, 3.81) * mm, "end": v(209.52, 3.04) * mm});
            skLineSegment(sketch, "E2271", {"start": v(209.52, 3.04) * mm, "end": v(210.79, 3.04) * mm});
            skLineSegment(sketch, "E2272", {"start": v(210.79, 3.04) * mm, "end": v(210.79, 2.24) * mm});
            skLineSegment(sketch, "E2273", {"start": v(210.79, 2.24) * mm, "end": v(211.79, 2.24) * mm});
            skLineSegment(sketch, "E2274", {"start": v(211.79, 2.24) * mm, "end": v(211.79, -11.76) * mm});
            skLineSegment(sketch, "E2275", {"start": v(211.79, -11.76) * mm, "end": v(210.79, -11.76) * mm});
            skLineSegment(sketch, "E2276", {"start": v(210.79, -49.86) * mm, "end": v(210.79, -50.66) * mm});
            skLineSegment(sketch, "E2277", {"start": v(210.79, -50.66) * mm, "end": v(209.52, -50.66) * mm});
            skLineSegment(sketch, "E2278", {"start": v(209.52, -50.66) * mm, "end": v(209.52, -51.44) * mm});
            skLineSegment(sketch, "E2279", {"start": v(209.52, -51.44) * mm, "end": v(210.32, -51.44) * mm});
            skLineSegment(sketch, "E2280", {"start": v(210.32, -51.44) * mm, "end": v(210.32, -53.16) * mm});
            skLineSegment(sketch, "E2281", {"start": v(210.32, -53.16) * mm, "end": v(211.24, -53.16) * mm});
            skLineSegment(sketch, "E2282", {"start": v(211.24, -53.16) * mm, "end": v(211.24, -56.46) * mm});
            skLineSegment(sketch, "E2283", {"start": v(211.24, -56.46) * mm, "end": v(210.32, -56.46) * mm});
            skLineSegment(sketch, "E2284", {"start": v(210.32, -56.46) * mm, "end": v(210.32, -58.09) * mm});
            skLineSegment(sketch, "E2285", {"start": v(210.32, -58.09) * mm, "end": v(207.09, -58.09) * mm});
            skLineSegment(sketch, "E2286", {"start": v(207.09, -58.09) * mm, "end": v(207.09, -58.96) * mm});
            skLineSegment(sketch, "E2287", {"start": v(207.09, -58.96) * mm, "end": v(204.29, -58.96) * mm});
            skLineSegment(sketch, "E2288", {"start": v(204.29, -58.96) * mm, "end": v(204.29, -58.09) * mm});
            skLineSegment(sketch, "E2289", {"start": v(204.29, -58.09) * mm, "end": v(198.02, -58.09) * mm});
            skLineSegment(sketch, "E2290", {"start": v(198.02, -58.09) * mm, "end": v(198.02, -56.46) * mm});
            skLineSegment(sketch, "E2291", {"start": v(198.02, -56.46) * mm, "end": v(197.04, -56.46) * mm});
            skLineSegment(sketch, "E2292", {"start": v(197.04, -56.46) * mm, "end": v(197.04, -53.16) * mm});
            skLineSegment(sketch, "E2293", {"start": v(197.04, -53.16) * mm, "end": v(198.02, -53.16) * mm});
            skLineSegment(sketch, "E2294", {"start": v(198.02, -53.16) * mm, "end": v(198.02, -51.44) * mm});
            skLineSegment(sketch, "E2295", {"start": v(198.02, -51.44) * mm, "end": v(198.82, -51.44) * mm});
            skLineSegment(sketch, "E2296", {"start": v(198.82, -51.44) * mm, "end": v(198.82, -50.66) * mm});
            skLineSegment(sketch, "E2297", {"start": v(198.82, -50.66) * mm, "end": v(198.79, -50.66) * mm});
            skLineSegment(sketch, "E2298", {"start": v(198.79, -50.66) * mm, "end": v(198.79, -49.86) * mm});
            skLineSegment(sketch, "E2299", {"start": v(198.79, -49.86) * mm, "end": v(197.79, -49.86) * mm});
            skLineSegment(sketch, "E2300", {"start": v(197.79, -49.86) * mm, "end": v(197.79, -35.86) * mm});
            skLineSegment(sketch, "E2301", {"start": v(197.79, -35.86) * mm, "end": v(198.79, -35.86) * mm});
            skLineSegment(sketch, "E2302", {"start": v(198.79, -35.86) * mm, "end": v(198.79, -35.06) * mm});
            skLineSegment(sketch, "E2303", {"start": v(198.79, -35.06) * mm, "end": v(198.82, -35.06) * mm});
            skLineSegment(sketch, "E2304", {"start": v(198.82, -35.06) * mm, "end": v(198.82, -34.29) * mm});
            skLineSegment(sketch, "E2305", {"start": v(198.82, -34.29) * mm, "end": v(198.02, -34.29) * mm});
            skLineSegment(sketch, "E2306", {"start": v(198.02, -34.29) * mm, "end": v(198.02, -32.56) * mm});
            skLineSegment(sketch, "E2307", {"start": v(198.02, -32.56) * mm, "end": v(197.04, -32.56) * mm});
            skLineSegment(sketch, "E2308", {"start": v(197.04, -32.56) * mm, "end": v(197.04, -29.26) * mm});
            skLineSegment(sketch, "E2309", {"start": v(197.04, -29.26) * mm, "end": v(198.02, -29.26) * mm});
            skLineSegment(sketch, "E2310", {"start": v(198.02, -29.26) * mm, "end": v(198.02, -27.64) * mm});
            skLineSegment(sketch, "E2311", {"start": v(198.02, -27.64) * mm, "end": v(204.29, -27.64) * mm});
            skLineSegment(sketch, "E2312", {"start": v(204.29, -27.64) * mm, "end": v(204.29, -26.76) * mm});
            skLineSegment(sketch, "E2313", {"start": v(204.29, -26.76) * mm, "end": v(207.09, -26.76) * mm});
            skLineSegment(sketch, "E2314", {"start": v(207.09, -26.76) * mm, "end": v(207.09, -27.64) * mm});
            skLineSegment(sketch, "E2315", {"start": v(207.09, -27.64) * mm, "end": v(210.32, -27.64) * mm});
            skLineSegment(sketch, "E2316", {"start": v(210.32, -27.64) * mm, "end": v(210.32, -29.26) * mm});
            skLineSegment(sketch, "E2317", {"start": v(210.32, -29.26) * mm, "end": v(211.24, -29.26) * mm});
            skLineSegment(sketch, "E2318", {"start": v(211.24, -29.26) * mm, "end": v(211.24, -32.56) * mm});
            skLineSegment(sketch, "E2319", {"start": v(211.24, -32.56) * mm, "end": v(210.32, -32.56) * mm});
            skLineSegment(sketch, "E2320", {"start": v(210.32, -32.56) * mm, "end": v(210.32, -34.29) * mm});
            skLineSegment(sketch, "E2321", {"start": v(210.32, -34.29) * mm, "end": v(209.52, -34.29) * mm});
            skLineSegment(sketch, "E2322", {"start": v(209.52, -34.29) * mm, "end": v(209.52, -35.06) * mm});
            skLineSegment(sketch, "E2323", {"start": v(209.52, -35.06) * mm, "end": v(210.79, -35.06) * mm});
            skLineSegment(sketch, "E2324", {"start": v(210.79, -35.06) * mm, "end": v(210.79, -35.86) * mm});
            skLineSegment(sketch, "E2325", {"start": v(210.79, -35.86) * mm, "end": v(211.79, -35.86) * mm});
            skLineSegment(sketch, "E2326", {"start": v(211.79, -35.86) * mm, "end": v(211.79, -49.86) * mm});
            skLineSegment(sketch, "E2327", {"start": v(211.79, -49.86) * mm, "end": v(210.79, -49.86) * mm});
            skLineSegment(sketch, "E2328", {"start": v(211.79, 17.81) * mm, "end": v(211.79, 16.81) * mm});
            skLineSegment(sketch, "E2329", {"start": v(211.79, 16.81) * mm, "end": v(197.79, 16.81) * mm});
            skLineSegment(sketch, "E2330", {"start": v(197.79, 16.81) * mm, "end": v(197.79, 17.81) * mm});
            skLineSegment(sketch, "E2331", {"start": v(197.79, 17.81) * mm, "end": v(196.99, 17.81) * mm});
            skLineSegment(sketch, "E2332", {"start": v(196.99, 17.81) * mm, "end": v(196.99, 20.91) * mm});
            skLineSegment(sketch, "E2333", {"start": v(196.99, 20.91) * mm, "end": v(197.79, 20.91) * mm});
            skLineSegment(sketch, "E2334", {"start": v(197.79, 20.91) * mm, "end": v(197.79, 26.71) * mm});
            skLineSegment(sketch, "E2335", {"start": v(197.79, 26.71) * mm, "end": v(196.99, 26.71) * mm});
            skLineSegment(sketch, "E2336", {"start": v(196.99, 26.71) * mm, "end": v(196.99, 29.81) * mm});
            skLineSegment(sketch, "E2337", {"start": v(196.99, 29.81) * mm, "end": v(197.79, 29.81) * mm});
            skLineSegment(sketch, "E2338", {"start": v(197.79, 29.81) * mm, "end": v(197.79, 30.81) * mm});
            skLineSegment(sketch, "E2339", {"start": v(197.79, 30.81) * mm, "end": v(211.79, 30.81) * mm});
            skLineSegment(sketch, "E2340", {"start": v(211.79, 30.81) * mm, "end": v(211.79, 29.81) * mm});
            skLineSegment(sketch, "E2341", {"start": v(211.79, 29.81) * mm, "end": v(212.59, 29.81) * mm});
            skLineSegment(sketch, "E2342", {"start": v(212.59, 29.81) * mm, "end": v(212.59, 26.71) * mm});
            skLineSegment(sketch, "E2343", {"start": v(212.59, 26.71) * mm, "end": v(211.79, 26.71) * mm});
            skLineSegment(sketch, "E2344", {"start": v(211.79, 26.71) * mm, "end": v(211.79, 20.91) * mm});
            skLineSegment(sketch, "E2345", {"start": v(211.79, 20.91) * mm, "end": v(212.59, 20.91) * mm});
            skLineSegment(sketch, "E2346", {"start": v(212.59, 20.91) * mm, "end": v(212.59, 17.81) * mm});
            skLineSegment(sketch, "E2347", {"start": v(212.59, 17.81) * mm, "end": v(211.79, 17.81) * mm});
            skSolve(sketch);
        }
        {
            var Q0;
            Q0=makeQuery(id+"F0.imprint","IMPRINT",FACE,{"disambiguationData":[TD([[makeQuery(id+"F0.imprint","IMPRINT",EDGE,{"derivedFrom":sQuery(id+"F0.wireOp",EDGE,"E0")}),-1.0]])]});
            extrude(context, id + "F1", {"entities" : qUnion([Q0]), "depth" : 1.5 * mm});
        }
        {
            var Q0;
            Q0=makeQuery(id+"F1.opExtrude","CAP_FACE",FACE,{"disambiguationData":[OSD([sQuery(id+"F0.wireOp",EDGE,"E0"),sQuery(id+"F0.wireOp",EDGE,"E1"),sQuery(id+"F0.wireOp",EDGE,"E2"),sQuery(id+"F0.wireOp",EDGE,"E3"),sQuery(id+"F0.wireOp",EDGE,"E4"),sQuery(id+"F0.wireOp",EDGE,"E5"),sQuery(id+"F0.wireOp",EDGE,"E6"),sQuery(id+"F0.wireOp",EDGE,"E7"),sQuery(id+"F0.wireOp",EDGE,"E8"),sQuery(id+"F0.wireOp",EDGE,"E9"),sQuery(id+"F0.wireOp",EDGE,"E10"),sQuery(id+"F0.wireOp",EDGE,"E11"),sQuery(id+"F0.wireOp",EDGE,"E12"),sQuery(id+"F0.wireOp",EDGE,"E13"),sQuery(id+"F0.wireOp",EDGE,"E14"),sQuery(id+"F0.wireOp",EDGE,"E15"),sQuery(id+"F0.wireOp",EDGE,"E16"),sQuery(id+"F0.wireOp",EDGE,"E17"),sQuery(id+"F0.wireOp",EDGE,"E18"),sQuery(id+"F0.wireOp",EDGE,"E19"),sQuery(id+"F0.wireOp",EDGE,"E20"),sQuery(id+"F0.wireOp",EDGE,"E21"),sQuery(id+"F0.wireOp",EDGE,"E22"),sQuery(id+"F0.wireOp",EDGE,"E23"),sQuery(id+"F0.wireOp",EDGE,"E24"),sQuery(id+"F0.wireOp",EDGE,"E25"),sQuery(id+"F0.wireOp",EDGE,"E26"),sQuery(id+"F0.wireOp",EDGE,"E27"),sQuery(id+"F0.wireOp",EDGE,"E28"),sQuery(id+"F0.wireOp",EDGE,"E29"),sQuery(id+"F0.wireOp",EDGE,"E30"),sQuery(id+"F0.wireOp",EDGE,"E31"),sQuery(id+"F0.wireOp",EDGE,"E32"),sQuery(id+"F0.wireOp",EDGE,"E33"),sQuery(id+"F0.wireOp",EDGE,"E34"),sQuery(id+"F0.wireOp",EDGE,"E35"),sQuery(id+"F0.wireOp",EDGE,"E36"),sQuery(id+"F0.wireOp",EDGE,"E37"),sQuery(id+"F0.wireOp",EDGE,"E38"),sQuery(id+"F0.wireOp",EDGE,"E39"),sQuery(id+"F0.wireOp",EDGE,"E40"),sQuery(id+"F0.wireOp",EDGE,"E41"),sQuery(id+"F0.wireOp",EDGE,"E42"),sQuery(id+"F0.wireOp",EDGE,"E43"),sQuery(id+"F0.wireOp",EDGE,"E44"),sQuery(id+"F0.wireOp",EDGE,"E45"),sQuery(id+"F0.wireOp",EDGE,"E46"),sQuery(id+"F0.wireOp",EDGE,"E47"),sQuery(id+"F0.wireOp",EDGE,"E48"),sQuery(id+"F0.wireOp",EDGE,"E49"),sQuery(id+"F0.wireOp",EDGE,"E50"),sQuery(id+"F0.wireOp",EDGE,"E51"),sQuery(id+"F0.wireOp",EDGE,"E52"),sQuery(id+"F0.wireOp",EDGE,"E53"),sQuery(id+"F0.wireOp",EDGE,"E54"),sQuery(id+"F0.wireOp",EDGE,"E55"),sQuery(id+"F0.wireOp",EDGE,"E56"),sQuery(id+"F0.wireOp",EDGE,"E57"),sQuery(id+"F0.wireOp",EDGE,"E58"),sQuery(id+"F0.wireOp",EDGE,"E59"),sQuery(id+"F0.wireOp",EDGE,"E60"),sQuery(id+"F0.wireOp",EDGE,"E61"),sQuery(id+"F0.wireOp",EDGE,"E62"),sQuery(id+"F0.wireOp",EDGE,"E63"),sQuery(id+"F0.wireOp",EDGE,"E64"),sQuery(id+"F0.wireOp",EDGE,"E65"),sQuery(id+"F0.wireOp",EDGE,"E66"),sQuery(id+"F0.wireOp",EDGE,"E67"),sQuery(id+"F0.wireOp",EDGE,"E68"),sQuery(id+"F0.wireOp",EDGE,"E69"),sQuery(id+"F0.wireOp",EDGE,"E70"),sQuery(id+"F0.wireOp",EDGE,"E71"),sQuery(id+"F0.wireOp",EDGE,"E72"),sQuery(id+"F0.wireOp",EDGE,"E73"),sQuery(id+"F0.wireOp",EDGE,"E74"),sQuery(id+"F0.wireOp",EDGE,"E75"),sQuery(id+"F0.wireOp",EDGE,"E76"),sQuery(id+"F0.wireOp",EDGE,"E77"),sQuery(id+"F0.wireOp",EDGE,"E78"),sQuery(id+"F0.wireOp",EDGE,"E79"),sQuery(id+"F0.wireOp",EDGE,"E80"),sQuery(id+"F0.wireOp",EDGE,"E81"),sQuery(id+"F0.wireOp",EDGE,"E82"),sQuery(id+"F0.wireOp",EDGE,"E83"),sQuery(id+"F0.wireOp",EDGE,"E84"),sQuery(id+"F0.wireOp",EDGE,"E85"),sQuery(id+"F0.wireOp",EDGE,"E86"),sQuery(id+"F0.wireOp",EDGE,"E87"),sQuery(id+"F0.wireOp",EDGE,"E88"),sQuery(id+"F0.wireOp",EDGE,"E89"),sQuery(id+"F0.wireOp",EDGE,"E90"),sQuery(id+"F0.wireOp",EDGE,"E91"),sQuery(id+"F0.wireOp",EDGE,"E92"),sQuery(id+"F0.wireOp",EDGE,"E93"),sQuery(id+"F0.wireOp",EDGE,"E94"),sQuery(id+"F0.wireOp",EDGE,"E95"),sQuery(id+"F0.wireOp",EDGE,"E96"),sQuery(id+"F0.wireOp",EDGE,"E97"),sQuery(id+"F0.wireOp",EDGE,"E98"),sQuery(id+"F0.wireOp",EDGE,"E99"),sQuery(id+"F0.wireOp",EDGE,"E100"),sQuery(id+"F0.wireOp",EDGE,"E101"),sQuery(id+"F0.wireOp",EDGE,"E102"),sQuery(id+"F0.wireOp",EDGE,"E103"),sQuery(id+"F0.wireOp",EDGE,"E104"),sQuery(id+"F0.wireOp",EDGE,"E105"),sQuery(id+"F0.wireOp",EDGE,"E106"),sQuery(id+"F0.wireOp",EDGE,"E107"),sQuery(id+"F0.wireOp",EDGE,"E108"),sQuery(id+"F0.wireOp",EDGE,"E109"),sQuery(id+"F0.wireOp",EDGE,"E110"),sQuery(id+"F0.wireOp",EDGE,"E111"),sQuery(id+"F0.wireOp",EDGE,"E112"),sQuery(id+"F0.wireOp",EDGE,"E113"),sQuery(id+"F0.wireOp",EDGE,"E114"),sQuery(id+"F0.wireOp",EDGE,"E115"),sQuery(id+"F0.wireOp",EDGE,"E116"),sQuery(id+"F0.wireOp",EDGE,"E117"),sQuery(id+"F0.wireOp",EDGE,"E118"),sQuery(id+"F0.wireOp",EDGE,"E119"),sQuery(id+"F0.wireOp",EDGE,"E120"),sQuery(id+"F0.wireOp",EDGE,"E121"),sQuery(id+"F0.wireOp",EDGE,"E122"),sQuery(id+"F0.wireOp",EDGE,"E123"),sQuery(id+"F0.wireOp",EDGE,"E124"),sQuery(id+"F0.wireOp",EDGE,"E125"),sQuery(id+"F0.wireOp",EDGE,"E126"),sQuery(id+"F0.wireOp",EDGE,"E127"),sQuery(id+"F0.wireOp",EDGE,"E128"),sQuery(id+"F0.wireOp",EDGE,"E129"),sQuery(id+"F0.wireOp",EDGE,"E130"),sQuery(id+"F0.wireOp",EDGE,"E131"),sQuery(id+"F0.wireOp",EDGE,"E132"),sQuery(id+"F0.wireOp",EDGE,"E133"),sQuery(id+"F0.wireOp",EDGE,"E134"),sQuery(id+"F0.wireOp",EDGE,"E135"),sQuery(id+"F0.wireOp",EDGE,"E136"),sQuery(id+"F0.wireOp",EDGE,"E137"),sQuery(id+"F0.wireOp",EDGE,"E138"),sQuery(id+"F0.wireOp",EDGE,"E139"),sQuery(id+"F0.wireOp",EDGE,"E140"),sQuery(id+"F0.wireOp",EDGE,"E141"),sQuery(id+"F0.wireOp",EDGE,"E142"),sQuery(id+"F0.wireOp",EDGE,"E143"),sQuery(id+"F0.wireOp",EDGE,"E144"),sQuery(id+"F0.wireOp",EDGE,"E145"),sQuery(id+"F0.wireOp",EDGE,"E146"),sQuery(id+"F0.wireOp",EDGE,"E147"),sQuery(id+"F0.wireOp",EDGE,"E148"),sQuery(id+"F0.wireOp",EDGE,"E149"),sQuery(id+"F0.wireOp",EDGE,"E150"),sQuery(id+"F0.wireOp",EDGE,"E151"),sQuery(id+"F0.wireOp",EDGE,"E152"),sQuery(id+"F0.wireOp",EDGE,"E153"),sQuery(id+"F0.wireOp",EDGE,"E154"),sQuery(id+"F0.wireOp",EDGE,"E155"),sQuery(id+"F0.wireOp",EDGE,"E156"),sQuery(id+"F0.wireOp",EDGE,"E157"),sQuery(id+"F0.wireOp",EDGE,"E158"),sQuery(id+"F0.wireOp",EDGE,"E159"),sQuery(id+"F0.wireOp",EDGE,"E160"),sQuery(id+"F0.wireOp",EDGE,"E161"),sQuery(id+"F0.wireOp",EDGE,"E162"),sQuery(id+"F0.wireOp",EDGE,"E163"),sQuery(id+"F0.wireOp",EDGE,"E164"),sQuery(id+"F0.wireOp",EDGE,"E165"),sQuery(id+"F0.wireOp",EDGE,"E166"),sQuery(id+"F0.wireOp",EDGE,"E167"),sQuery(id+"F0.wireOp",EDGE,"E168"),sQuery(id+"F0.wireOp",EDGE,"E169"),sQuery(id+"F0.wireOp",EDGE,"E170"),sQuery(id+"F0.wireOp",EDGE,"E171"),sQuery(id+"F0.wireOp",EDGE,"E172"),sQuery(id+"F0.wireOp",EDGE,"E173"),sQuery(id+"F0.wireOp",EDGE,"E174"),sQuery(id+"F0.wireOp",EDGE,"E175"),sQuery(id+"F0.wireOp",EDGE,"E176"),sQuery(id+"F0.wireOp",EDGE,"E177"),sQuery(id+"F0.wireOp",EDGE,"E178"),sQuery(id+"F0.wireOp",EDGE,"E179"),sQuery(id+"F0.wireOp",EDGE,"E180"),sQuery(id+"F0.wireOp",EDGE,"E181"),sQuery(id+"F0.wireOp",EDGE,"E182"),sQuery(id+"F0.wireOp",EDGE,"E183"),sQuery(id+"F0.wireOp",EDGE,"E184"),sQuery(id+"F0.wireOp",EDGE,"E185"),sQuery(id+"F0.wireOp",EDGE,"E186"),sQuery(id+"F0.wireOp",EDGE,"E187"),sQuery(id+"F0.wireOp",EDGE,"E188"),sQuery(id+"F0.wireOp",EDGE,"E189"),sQuery(id+"F0.wireOp",EDGE,"E190"),sQuery(id+"F0.wireOp",EDGE,"E191"),sQuery(id+"F0.wireOp",EDGE,"E192"),sQuery(id+"F0.wireOp",EDGE,"E193"),sQuery(id+"F0.wireOp",EDGE,"E194"),sQuery(id+"F0.wireOp",EDGE,"E195"),sQuery(id+"F0.wireOp",EDGE,"E196"),sQuery(id+"F0.wireOp",EDGE,"E197"),sQuery(id+"F0.wireOp",EDGE,"E198"),sQuery(id+"F0.wireOp",EDGE,"E199"),sQuery(id+"F0.wireOp",EDGE,"E200"),sQuery(id+"F0.wireOp",EDGE,"E201"),sQuery(id+"F0.wireOp",EDGE,"E202"),sQuery(id+"F0.wireOp",EDGE,"E203"),sQuery(id+"F0.wireOp",EDGE,"E204"),sQuery(id+"F0.wireOp",EDGE,"E205"),sQuery(id+"F0.wireOp",EDGE,"E206"),sQuery(id+"F0.wireOp",EDGE,"E207"),sQuery(id+"F0.wireOp",EDGE,"E208"),sQuery(id+"F0.wireOp",EDGE,"E209"),sQuery(id+"F0.wireOp",EDGE,"E210"),sQuery(id+"F0.wireOp",EDGE,"E211"),sQuery(id+"F0.wireOp",EDGE,"E212"),sQuery(id+"F0.wireOp",EDGE,"E213"),sQuery(id+"F0.wireOp",EDGE,"E214"),sQuery(id+"F0.wireOp",EDGE,"E215"),sQuery(id+"F0.wireOp",EDGE,"E216"),sQuery(id+"F0.wireOp",EDGE,"E217"),sQuery(id+"F0.wireOp",EDGE,"E218"),sQuery(id+"F0.wireOp",EDGE,"E219"),sQuery(id+"F0.wireOp",EDGE,"E220"),sQuery(id+"F0.wireOp",EDGE,"E221"),sQuery(id+"F0.wireOp",EDGE,"E222"),sQuery(id+"F0.wireOp",EDGE,"E223"),sQuery(id+"F0.wireOp",EDGE,"E224"),sQuery(id+"F0.wireOp",EDGE,"E225"),sQuery(id+"F0.wireOp",EDGE,"E226"),sQuery(id+"F0.wireOp",EDGE,"E227"),sQuery(id+"F0.wireOp",EDGE,"E228"),sQuery(id+"F0.wireOp",EDGE,"E229"),sQuery(id+"F0.wireOp",EDGE,"E230"),sQuery(id+"F0.wireOp",EDGE,"E231"),sQuery(id+"F0.wireOp",EDGE,"E232"),sQuery(id+"F0.wireOp",EDGE,"E233"),sQuery(id+"F0.wireOp",EDGE,"E234"),sQuery(id+"F0.wireOp",EDGE,"E235"),sQuery(id+"F0.wireOp",EDGE,"E236"),sQuery(id+"F0.wireOp",EDGE,"E237"),sQuery(id+"F0.wireOp",EDGE,"E238"),sQuery(id+"F0.wireOp",EDGE,"E239"),sQuery(id+"F0.wireOp",EDGE,"E240"),sQuery(id+"F0.wireOp",EDGE,"E241"),sQuery(id+"F0.wireOp",EDGE,"E242"),sQuery(id+"F0.wireOp",EDGE,"E243"),sQuery(id+"F0.wireOp",EDGE,"E244"),sQuery(id+"F0.wireOp",EDGE,"E245"),sQuery(id+"F0.wireOp",EDGE,"E246"),sQuery(id+"F0.wireOp",EDGE,"E247"),sQuery(id+"F0.wireOp",EDGE,"E248"),sQuery(id+"F0.wireOp",EDGE,"E249"),sQuery(id+"F0.wireOp",EDGE,"E250"),sQuery(id+"F0.wireOp",EDGE,"E251"),sQuery(id+"F0.wireOp",EDGE,"E252"),sQuery(id+"F0.wireOp",EDGE,"E253"),sQuery(id+"F0.wireOp",EDGE,"E254"),sQuery(id+"F0.wireOp",EDGE,"E255"),sQuery(id+"F0.wireOp",EDGE,"E256"),sQuery(id+"F0.wireOp",EDGE,"E257"),sQuery(id+"F0.wireOp",EDGE,"E258"),sQuery(id+"F0.wireOp",EDGE,"E259"),sQuery(id+"F0.wireOp",EDGE,"E260"),sQuery(id+"F0.wireOp",EDGE,"E261"),sQuery(id+"F0.wireOp",EDGE,"E262"),sQuery(id+"F0.wireOp",EDGE,"E263"),sQuery(id+"F0.wireOp",EDGE,"E264"),sQuery(id+"F0.wireOp",EDGE,"E265"),sQuery(id+"F0.wireOp",EDGE,"E266"),sQuery(id+"F0.wireOp",EDGE,"E267"),sQuery(id+"F0.wireOp",EDGE,"E268"),sQuery(id+"F0.wireOp",EDGE,"E269"),sQuery(id+"F0.wireOp",EDGE,"E270"),sQuery(id+"F0.wireOp",EDGE,"E271"),sQuery(id+"F0.wireOp",EDGE,"E272"),sQuery(id+"F0.wireOp",EDGE,"E273"),sQuery(id+"F0.wireOp",EDGE,"E274"),sQuery(id+"F0.wireOp",EDGE,"E275"),sQuery(id+"F0.wireOp",EDGE,"E276"),sQuery(id+"F0.wireOp",EDGE,"E277"),sQuery(id+"F0.wireOp",EDGE,"E278"),sQuery(id+"F0.wireOp",EDGE,"E279"),sQuery(id+"F0.wireOp",EDGE,"E280"),sQuery(id+"F0.wireOp",EDGE,"E281"),sQuery(id+"F0.wireOp",EDGE,"E282"),sQuery(id+"F0.wireOp",EDGE,"E283"),sQuery(id+"F0.wireOp",EDGE,"E284"),sQuery(id+"F0.wireOp",EDGE,"E285"),sQuery(id+"F0.wireOp",EDGE,"E286"),sQuery(id+"F0.wireOp",EDGE,"E287"),sQuery(id+"F0.wireOp",EDGE,"E288"),sQuery(id+"F0.wireOp",EDGE,"E289"),sQuery(id+"F0.wireOp",EDGE,"E290"),sQuery(id+"F0.wireOp",EDGE,"E291"),sQuery(id+"F0.wireOp",EDGE,"E292"),sQuery(id+"F0.wireOp",EDGE,"E293"),sQuery(id+"F0.wireOp",EDGE,"E294"),sQuery(id+"F0.wireOp",EDGE,"E295"),sQuery(id+"F0.wireOp",EDGE,"E296"),sQuery(id+"F0.wireOp",EDGE,"E297"),sQuery(id+"F0.wireOp",EDGE,"E298"),sQuery(id+"F0.wireOp",EDGE,"E299"),sQuery(id+"F0.wireOp",EDGE,"E300"),sQuery(id+"F0.wireOp",EDGE,"E301"),sQuery(id+"F0.wireOp",EDGE,"E302"),sQuery(id+"F0.wireOp",EDGE,"E303"),sQuery(id+"F0.wireOp",EDGE,"E304"),sQuery(id+"F0.wireOp",EDGE,"E305"),sQuery(id+"F0.wireOp",EDGE,"E306"),sQuery(id+"F0.wireOp",EDGE,"E307"),sQuery(id+"F0.wireOp",EDGE,"E308"),sQuery(id+"F0.wireOp",EDGE,"E309"),sQuery(id+"F0.wireOp",EDGE,"E310"),sQuery(id+"F0.wireOp",EDGE,"E311"),sQuery(id+"F0.wireOp",EDGE,"E312"),sQuery(id+"F0.wireOp",EDGE,"E313"),sQuery(id+"F0.wireOp",EDGE,"E314"),sQuery(id+"F0.wireOp",EDGE,"E315"),sQuery(id+"F0.wireOp",EDGE,"E316"),sQuery(id+"F0.wireOp",EDGE,"E317"),sQuery(id+"F0.wireOp",EDGE,"E318"),sQuery(id+"F0.wireOp",EDGE,"E319"),sQuery(id+"F0.wireOp",EDGE,"E320"),sQuery(id+"F0.wireOp",EDGE,"E321"),sQuery(id+"F0.wireOp",EDGE,"E322"),sQuery(id+"F0.wireOp",EDGE,"E323"),sQuery(id+"F0.wireOp",EDGE,"E324"),sQuery(id+"F0.wireOp",EDGE,"E325"),sQuery(id+"F0.wireOp",EDGE,"E326"),sQuery(id+"F0.wireOp",EDGE,"E327"),sQuery(id+"F0.wireOp",EDGE,"E328"),sQuery(id+"F0.wireOp",EDGE,"E329"),sQuery(id+"F0.wireOp",EDGE,"E330"),sQuery(id+"F0.wireOp",EDGE,"E331"),sQuery(id+"F0.wireOp",EDGE,"E332"),sQuery(id+"F0.wireOp",EDGE,"E333"),sQuery(id+"F0.wireOp",EDGE,"E334"),sQuery(id+"F0.wireOp",EDGE,"E335"),sQuery(id+"F0.wireOp",EDGE,"E336"),sQuery(id+"F0.wireOp",EDGE,"E337"),sQuery(id+"F0.wireOp",EDGE,"E338"),sQuery(id+"F0.wireOp",EDGE,"E339"),sQuery(id+"F0.wireOp",EDGE,"E340"),sQuery(id+"F0.wireOp",EDGE,"E341"),sQuery(id+"F0.wireOp",EDGE,"E342"),sQuery(id+"F0.wireOp",EDGE,"E343"),sQuery(id+"F0.wireOp",EDGE,"E344"),sQuery(id+"F0.wireOp",EDGE,"E345"),sQuery(id+"F0.wireOp",EDGE,"E346"),sQuery(id+"F0.wireOp",EDGE,"E347"),sQuery(id+"F0.wireOp",EDGE,"E348"),sQuery(id+"F0.wireOp",EDGE,"E349"),sQuery(id+"F0.wireOp",EDGE,"E350"),sQuery(id+"F0.wireOp",EDGE,"E351"),sQuery(id+"F0.wireOp",EDGE,"E352"),sQuery(id+"F0.wireOp",EDGE,"E353"),sQuery(id+"F0.wireOp",EDGE,"E354"),sQuery(id+"F0.wireOp",EDGE,"E355"),sQuery(id+"F0.wireOp",EDGE,"E356"),sQuery(id+"F0.wireOp",EDGE,"E357"),sQuery(id+"F0.wireOp",EDGE,"E358"),sQuery(id+"F0.wireOp",EDGE,"E359"),sQuery(id+"F0.wireOp",EDGE,"E360"),sQuery(id+"F0.wireOp",EDGE,"E361"),sQuery(id+"F0.wireOp",EDGE,"E362"),sQuery(id+"F0.wireOp",EDGE,"E363"),sQuery(id+"F0.wireOp",EDGE,"E364"),sQuery(id+"F0.wireOp",EDGE,"E365"),sQuery(id+"F0.wireOp",EDGE,"E366"),sQuery(id+"F0.wireOp",EDGE,"E367"),sQuery(id+"F0.wireOp",EDGE,"E368"),sQuery(id+"F0.wireOp",EDGE,"E369"),sQuery(id+"F0.wireOp",EDGE,"E370"),sQuery(id+"F0.wireOp",EDGE,"E371"),sQuery(id+"F0.wireOp",EDGE,"E372"),sQuery(id+"F0.wireOp",EDGE,"E373"),sQuery(id+"F0.wireOp",EDGE,"E374"),sQuery(id+"F0.wireOp",EDGE,"E375"),sQuery(id+"F0.wireOp",EDGE,"E376"),sQuery(id+"F0.wireOp",EDGE,"E377"),sQuery(id+"F0.wireOp",EDGE,"E378"),sQuery(id+"F0.wireOp",EDGE,"E379"),sQuery(id+"F0.wireOp",EDGE,"E380"),sQuery(id+"F0.wireOp",EDGE,"E381"),sQuery(id+"F0.wireOp",EDGE,"E382"),sQuery(id+"F0.wireOp",EDGE,"E383"),sQuery(id+"F0.wireOp",EDGE,"E384"),sQuery(id+"F0.wireOp",EDGE,"E385"),sQuery(id+"F0.wireOp",EDGE,"E386"),sQuery(id+"F0.wireOp",EDGE,"E387"),sQuery(id+"F0.wireOp",EDGE,"E388"),sQuery(id+"F0.wireOp",EDGE,"E389"),sQuery(id+"F0.wireOp",EDGE,"E390"),sQuery(id+"F0.wireOp",EDGE,"E391"),sQuery(id+"F0.wireOp",EDGE,"E392"),sQuery(id+"F0.wireOp",EDGE,"E393"),sQuery(id+"F0.wireOp",EDGE,"E394"),sQuery(id+"F0.wireOp",EDGE,"E395"),sQuery(id+"F0.wireOp",EDGE,"E396"),sQuery(id+"F0.wireOp",EDGE,"E397"),sQuery(id+"F0.wireOp",EDGE,"E398"),sQuery(id+"F0.wireOp",EDGE,"E399"),sQuery(id+"F0.wireOp",EDGE,"E400"),sQuery(id+"F0.wireOp",EDGE,"E401"),sQuery(id+"F0.wireOp",EDGE,"E402"),sQuery(id+"F0.wireOp",EDGE,"E403"),sQuery(id+"F0.wireOp",EDGE,"E404"),sQuery(id+"F0.wireOp",EDGE,"E405"),sQuery(id+"F0.wireOp",EDGE,"E406"),sQuery(id+"F0.wireOp",EDGE,"E407"),sQuery(id+"F0.wireOp",EDGE,"E408"),sQuery(id+"F0.wireOp",EDGE,"E409"),sQuery(id+"F0.wireOp",EDGE,"E410"),sQuery(id+"F0.wireOp",EDGE,"E411"),sQuery(id+"F0.wireOp",EDGE,"E412"),sQuery(id+"F0.wireOp",EDGE,"E413"),sQuery(id+"F0.wireOp",EDGE,"E414"),sQuery(id+"F0.wireOp",EDGE,"E415"),sQuery(id+"F0.wireOp",EDGE,"E416"),sQuery(id+"F0.wireOp",EDGE,"E417"),sQuery(id+"F0.wireOp",EDGE,"E418"),sQuery(id+"F0.wireOp",EDGE,"E419"),sQuery(id+"F0.wireOp",EDGE,"E420"),sQuery(id+"F0.wireOp",EDGE,"E421"),sQuery(id+"F0.wireOp",EDGE,"E422"),sQuery(id+"F0.wireOp",EDGE,"E423"),sQuery(id+"F0.wireOp",EDGE,"E424"),sQuery(id+"F0.wireOp",EDGE,"E425"),sQuery(id+"F0.wireOp",EDGE,"E426"),sQuery(id+"F0.wireOp",EDGE,"E427"),sQuery(id+"F0.wireOp",EDGE,"E428"),sQuery(id+"F0.wireOp",EDGE,"E429"),sQuery(id+"F0.wireOp",EDGE,"E430"),sQuery(id+"F0.wireOp",EDGE,"E431"),sQuery(id+"F0.wireOp",EDGE,"E432"),sQuery(id+"F0.wireOp",EDGE,"E433"),sQuery(id+"F0.wireOp",EDGE,"E434"),sQuery(id+"F0.wireOp",EDGE,"E435"),sQuery(id+"F0.wireOp",EDGE,"E436"),sQuery(id+"F0.wireOp",EDGE,"E437"),sQuery(id+"F0.wireOp",EDGE,"E438"),sQuery(id+"F0.wireOp",EDGE,"E439"),sQuery(id+"F0.wireOp",EDGE,"E440"),sQuery(id+"F0.wireOp",EDGE,"E441"),sQuery(id+"F0.wireOp",EDGE,"E442"),sQuery(id+"F0.wireOp",EDGE,"E443"),sQuery(id+"F0.wireOp",EDGE,"E444"),sQuery(id+"F0.wireOp",EDGE,"E445"),sQuery(id+"F0.wireOp",EDGE,"E446"),sQuery(id+"F0.wireOp",EDGE,"E447"),sQuery(id+"F0.wireOp",EDGE,"E448"),sQuery(id+"F0.wireOp",EDGE,"E449"),sQuery(id+"F0.wireOp",EDGE,"E450"),sQuery(id+"F0.wireOp",EDGE,"E451"),sQuery(id+"F0.wireOp",EDGE,"E452"),sQuery(id+"F0.wireOp",EDGE,"E453"),sQuery(id+"F0.wireOp",EDGE,"E454"),sQuery(id+"F0.wireOp",EDGE,"E455"),sQuery(id+"F0.wireOp",EDGE,"E456"),sQuery(id+"F0.wireOp",EDGE,"E457"),sQuery(id+"F0.wireOp",EDGE,"E458"),sQuery(id+"F0.wireOp",EDGE,"E459"),sQuery(id+"F0.wireOp",EDGE,"E460"),sQuery(id+"F0.wireOp",EDGE,"E461"),sQuery(id+"F0.wireOp",EDGE,"E462"),sQuery(id+"F0.wireOp",EDGE,"E463"),sQuery(id+"F0.wireOp",EDGE,"E464"),sQuery(id+"F0.wireOp",EDGE,"E465"),sQuery(id+"F0.wireOp",EDGE,"E466"),sQuery(id+"F0.wireOp",EDGE,"E467"),sQuery(id+"F0.wireOp",EDGE,"E468"),sQuery(id+"F0.wireOp",EDGE,"E469"),sQuery(id+"F0.wireOp",EDGE,"E470"),sQuery(id+"F0.wireOp",EDGE,"E471"),sQuery(id+"F0.wireOp",EDGE,"E472"),sQuery(id+"F0.wireOp",EDGE,"E473"),sQuery(id+"F0.wireOp",EDGE,"E474"),sQuery(id+"F0.wireOp",EDGE,"E475"),sQuery(id+"F0.wireOp",EDGE,"E476"),sQuery(id+"F0.wireOp",EDGE,"E477"),sQuery(id+"F0.wireOp",EDGE,"E478"),sQuery(id+"F0.wireOp",EDGE,"E479"),sQuery(id+"F0.wireOp",EDGE,"E480"),sQuery(id+"F0.wireOp",EDGE,"E481"),sQuery(id+"F0.wireOp",EDGE,"E482"),sQuery(id+"F0.wireOp",EDGE,"E483"),sQuery(id+"F0.wireOp",EDGE,"E484"),sQuery(id+"F0.wireOp",EDGE,"E485"),sQuery(id+"F0.wireOp",EDGE,"E486"),sQuery(id+"F0.wireOp",EDGE,"E487"),sQuery(id+"F0.wireOp",EDGE,"E488"),sQuery(id+"F0.wireOp",EDGE,"E489"),sQuery(id+"F0.wireOp",EDGE,"E490"),sQuery(id+"F0.wireOp",EDGE,"E491"),sQuery(id+"F0.wireOp",EDGE,"E492"),sQuery(id+"F0.wireOp",EDGE,"E493"),sQuery(id+"F0.wireOp",EDGE,"E494"),sQuery(id+"F0.wireOp",EDGE,"E495"),sQuery(id+"F0.wireOp",EDGE,"E496"),sQuery(id+"F0.wireOp",EDGE,"E497"),sQuery(id+"F0.wireOp",EDGE,"E498"),sQuery(id+"F0.wireOp",EDGE,"E499"),sQuery(id+"F0.wireOp",EDGE,"E500"),sQuery(id+"F0.wireOp",EDGE,"E501"),sQuery(id+"F0.wireOp",EDGE,"E502"),sQuery(id+"F0.wireOp",EDGE,"E503"),sQuery(id+"F0.wireOp",EDGE,"E504"),sQuery(id+"F0.wireOp",EDGE,"E505"),sQuery(id+"F0.wireOp",EDGE,"E506"),sQuery(id+"F0.wireOp",EDGE,"E507"),sQuery(id+"F0.wireOp",EDGE,"E508"),sQuery(id+"F0.wireOp",EDGE,"E509"),sQuery(id+"F0.wireOp",EDGE,"E510"),sQuery(id+"F0.wireOp",EDGE,"E511"),sQuery(id+"F0.wireOp",EDGE,"E512"),sQuery(id+"F0.wireOp",EDGE,"E513"),sQuery(id+"F0.wireOp",EDGE,"E514"),sQuery(id+"F0.wireOp",EDGE,"E515"),sQuery(id+"F0.wireOp",EDGE,"E516"),sQuery(id+"F0.wireOp",EDGE,"E517"),sQuery(id+"F0.wireOp",EDGE,"E518"),sQuery(id+"F0.wireOp",EDGE,"E519"),sQuery(id+"F0.wireOp",EDGE,"E520"),sQuery(id+"F0.wireOp",EDGE,"E521"),sQuery(id+"F0.wireOp",EDGE,"E522"),sQuery(id+"F0.wireOp",EDGE,"E523"),sQuery(id+"F0.wireOp",EDGE,"E524"),sQuery(id+"F0.wireOp",EDGE,"E525"),sQuery(id+"F0.wireOp",EDGE,"E526"),sQuery(id+"F0.wireOp",EDGE,"E527"),sQuery(id+"F0.wireOp",EDGE,"E528"),sQuery(id+"F0.wireOp",EDGE,"E529"),sQuery(id+"F0.wireOp",EDGE,"E530"),sQuery(id+"F0.wireOp",EDGE,"E531"),sQuery(id+"F0.wireOp",EDGE,"E532"),sQuery(id+"F0.wireOp",EDGE,"E533"),sQuery(id+"F0.wireOp",EDGE,"E534"),sQuery(id+"F0.wireOp",EDGE,"E535"),sQuery(id+"F0.wireOp",EDGE,"E536"),sQuery(id+"F0.wireOp",EDGE,"E537"),sQuery(id+"F0.wireOp",EDGE,"E538"),sQuery(id+"F0.wireOp",EDGE,"E539"),sQuery(id+"F0.wireOp",EDGE,"E540"),sQuery(id+"F0.wireOp",EDGE,"E541"),sQuery(id+"F0.wireOp",EDGE,"E542"),sQuery(id+"F0.wireOp",EDGE,"E543"),sQuery(id+"F0.wireOp",EDGE,"E544"),sQuery(id+"F0.wireOp",EDGE,"E545"),sQuery(id+"F0.wireOp",EDGE,"E546"),sQuery(id+"F0.wireOp",EDGE,"E547"),sQuery(id+"F0.wireOp",EDGE,"E548"),sQuery(id+"F0.wireOp",EDGE,"E549"),sQuery(id+"F0.wireOp",EDGE,"E550"),sQuery(id+"F0.wireOp",EDGE,"E551"),sQuery(id+"F0.wireOp",EDGE,"E552"),sQuery(id+"F0.wireOp",EDGE,"E553"),sQuery(id+"F0.wireOp",EDGE,"E554"),sQuery(id+"F0.wireOp",EDGE,"E555"),sQuery(id+"F0.wireOp",EDGE,"E556"),sQuery(id+"F0.wireOp",EDGE,"E557"),sQuery(id+"F0.wireOp",EDGE,"E558"),sQuery(id+"F0.wireOp",EDGE,"E559"),sQuery(id+"F0.wireOp",EDGE,"E560"),sQuery(id+"F0.wireOp",EDGE,"E561"),sQuery(id+"F0.wireOp",EDGE,"E562"),sQuery(id+"F0.wireOp",EDGE,"E563"),sQuery(id+"F0.wireOp",EDGE,"E564"),sQuery(id+"F0.wireOp",EDGE,"E565"),sQuery(id+"F0.wireOp",EDGE,"E566"),sQuery(id+"F0.wireOp",EDGE,"E567"),sQuery(id+"F0.wireOp",EDGE,"E568"),sQuery(id+"F0.wireOp",EDGE,"E569"),sQuery(id+"F0.wireOp",EDGE,"E570"),sQuery(id+"F0.wireOp",EDGE,"E571"),sQuery(id+"F0.wireOp",EDGE,"E572"),sQuery(id+"F0.wireOp",EDGE,"E573"),sQuery(id+"F0.wireOp",EDGE,"E574"),sQuery(id+"F0.wireOp",EDGE,"E575"),sQuery(id+"F0.wireOp",EDGE,"E576"),sQuery(id+"F0.wireOp",EDGE,"E577"),sQuery(id+"F0.wireOp",EDGE,"E578"),sQuery(id+"F0.wireOp",EDGE,"E579"),sQuery(id+"F0.wireOp",EDGE,"E580"),sQuery(id+"F0.wireOp",EDGE,"E581"),sQuery(id+"F0.wireOp",EDGE,"E582"),sQuery(id+"F0.wireOp",EDGE,"E583"),sQuery(id+"F0.wireOp",EDGE,"E584"),sQuery(id+"F0.wireOp",EDGE,"E585"),sQuery(id+"F0.wireOp",EDGE,"E586"),sQuery(id+"F0.wireOp",EDGE,"E587"),sQuery(id+"F0.wireOp",EDGE,"E588"),sQuery(id+"F0.wireOp",EDGE,"E589"),sQuery(id+"F0.wireOp",EDGE,"E590"),sQuery(id+"F0.wireOp",EDGE,"E591"),sQuery(id+"F0.wireOp",EDGE,"E592"),sQuery(id+"F0.wireOp",EDGE,"E593"),sQuery(id+"F0.wireOp",EDGE,"E594"),sQuery(id+"F0.wireOp",EDGE,"E595"),sQuery(id+"F0.wireOp",EDGE,"E596"),sQuery(id+"F0.wireOp",EDGE,"E597"),sQuery(id+"F0.wireOp",EDGE,"E598"),sQuery(id+"F0.wireOp",EDGE,"E599"),sQuery(id+"F0.wireOp",EDGE,"E600"),sQuery(id+"F0.wireOp",EDGE,"E601"),sQuery(id+"F0.wireOp",EDGE,"E602"),sQuery(id+"F0.wireOp",EDGE,"E603"),sQuery(id+"F0.wireOp",EDGE,"E604"),sQuery(id+"F0.wireOp",EDGE,"E605"),sQuery(id+"F0.wireOp",EDGE,"E606"),sQuery(id+"F0.wireOp",EDGE,"E607"),sQuery(id+"F0.wireOp",EDGE,"E608"),sQuery(id+"F0.wireOp",EDGE,"E609"),sQuery(id+"F0.wireOp",EDGE,"E610"),sQuery(id+"F0.wireOp",EDGE,"E611"),sQuery(id+"F0.wireOp",EDGE,"E612"),sQuery(id+"F0.wireOp",EDGE,"E613"),sQuery(id+"F0.wireOp",EDGE,"E614"),sQuery(id+"F0.wireOp",EDGE,"E615"),sQuery(id+"F0.wireOp",EDGE,"E616"),sQuery(id+"F0.wireOp",EDGE,"E617"),sQuery(id+"F0.wireOp",EDGE,"E618"),sQuery(id+"F0.wireOp",EDGE,"E619"),sQuery(id+"F0.wireOp",EDGE,"E620"),sQuery(id+"F0.wireOp",EDGE,"E621"),sQuery(id+"F0.wireOp",EDGE,"E622"),sQuery(id+"F0.wireOp",EDGE,"E623"),sQuery(id+"F0.wireOp",EDGE,"E624"),sQuery(id+"F0.wireOp",EDGE,"E625"),sQuery(id+"F0.wireOp",EDGE,"E626"),sQuery(id+"F0.wireOp",EDGE,"E627"),sQuery(id+"F0.wireOp",EDGE,"E628"),sQuery(id+"F0.wireOp",EDGE,"E629"),sQuery(id+"F0.wireOp",EDGE,"E630"),sQuery(id+"F0.wireOp",EDGE,"E631"),sQuery(id+"F0.wireOp",EDGE,"E632"),sQuery(id+"F0.wireOp",EDGE,"E633"),sQuery(id+"F0.wireOp",EDGE,"E634"),sQuery(id+"F0.wireOp",EDGE,"E635"),sQuery(id+"F0.wireOp",EDGE,"E636"),sQuery(id+"F0.wireOp",EDGE,"E637"),sQuery(id+"F0.wireOp",EDGE,"E638"),sQuery(id+"F0.wireOp",EDGE,"E639"),sQuery(id+"F0.wireOp",EDGE,"E640"),sQuery(id+"F0.wireOp",EDGE,"E641"),sQuery(id+"F0.wireOp",EDGE,"E642"),sQuery(id+"F0.wireOp",EDGE,"E643"),sQuery(id+"F0.wireOp",EDGE,"E644"),sQuery(id+"F0.wireOp",EDGE,"E645"),sQuery(id+"F0.wireOp",EDGE,"E646"),sQuery(id+"F0.wireOp",EDGE,"E647"),sQuery(id+"F0.wireOp",EDGE,"E648"),sQuery(id+"F0.wireOp",EDGE,"E649"),sQuery(id+"F0.wireOp",EDGE,"E650"),sQuery(id+"F0.wireOp",EDGE,"E651"),sQuery(id+"F0.wireOp",EDGE,"E652"),sQuery(id+"F0.wireOp",EDGE,"E653"),sQuery(id+"F0.wireOp",EDGE,"E654"),sQuery(id+"F0.wireOp",EDGE,"E655"),sQuery(id+"F0.wireOp",EDGE,"E656"),sQuery(id+"F0.wireOp",EDGE,"E657"),sQuery(id+"F0.wireOp",EDGE,"E658"),sQuery(id+"F0.wireOp",EDGE,"E659"),sQuery(id+"F0.wireOp",EDGE,"E660"),sQuery(id+"F0.wireOp",EDGE,"E661"),sQuery(id+"F0.wireOp",EDGE,"E662"),sQuery(id+"F0.wireOp",EDGE,"E663"),sQuery(id+"F0.wireOp",EDGE,"E664"),sQuery(id+"F0.wireOp",EDGE,"E665"),sQuery(id+"F0.wireOp",EDGE,"E666"),sQuery(id+"F0.wireOp",EDGE,"E667"),sQuery(id+"F0.wireOp",EDGE,"E668"),sQuery(id+"F0.wireOp",EDGE,"E669"),sQuery(id+"F0.wireOp",EDGE,"E670"),sQuery(id+"F0.wireOp",EDGE,"E671"),sQuery(id+"F0.wireOp",EDGE,"E672"),sQuery(id+"F0.wireOp",EDGE,"E673"),sQuery(id+"F0.wireOp",EDGE,"E674"),sQuery(id+"F0.wireOp",EDGE,"E675"),sQuery(id+"F0.wireOp",EDGE,"E676"),sQuery(id+"F0.wireOp",EDGE,"E677"),sQuery(id+"F0.wireOp",EDGE,"E678"),sQuery(id+"F0.wireOp",EDGE,"E679"),sQuery(id+"F0.wireOp",EDGE,"E680"),sQuery(id+"F0.wireOp",EDGE,"E681"),sQuery(id+"F0.wireOp",EDGE,"E682"),sQuery(id+"F0.wireOp",EDGE,"E683"),sQuery(id+"F0.wireOp",EDGE,"E684"),sQuery(id+"F0.wireOp",EDGE,"E685"),sQuery(id+"F0.wireOp",EDGE,"E686"),sQuery(id+"F0.wireOp",EDGE,"E687"),sQuery(id+"F0.wireOp",EDGE,"E688"),sQuery(id+"F0.wireOp",EDGE,"E689"),sQuery(id+"F0.wireOp",EDGE,"E690"),sQuery(id+"F0.wireOp",EDGE,"E691"),sQuery(id+"F0.wireOp",EDGE,"E692"),sQuery(id+"F0.wireOp",EDGE,"E693"),sQuery(id+"F0.wireOp",EDGE,"E694"),sQuery(id+"F0.wireOp",EDGE,"E695"),sQuery(id+"F0.wireOp",EDGE,"E696"),sQuery(id+"F0.wireOp",EDGE,"E697"),sQuery(id+"F0.wireOp",EDGE,"E698"),sQuery(id+"F0.wireOp",EDGE,"E699"),sQuery(id+"F0.wireOp",EDGE,"E700"),sQuery(id+"F0.wireOp",EDGE,"E701"),sQuery(id+"F0.wireOp",EDGE,"E702"),sQuery(id+"F0.wireOp",EDGE,"E703"),sQuery(id+"F0.wireOp",EDGE,"E704"),sQuery(id+"F0.wireOp",EDGE,"E705"),sQuery(id+"F0.wireOp",EDGE,"E706"),sQuery(id+"F0.wireOp",EDGE,"E707"),sQuery(id+"F0.wireOp",EDGE,"E708"),sQuery(id+"F0.wireOp",EDGE,"E709"),sQuery(id+"F0.wireOp",EDGE,"E710"),sQuery(id+"F0.wireOp",EDGE,"E711"),sQuery(id+"F0.wireOp",EDGE,"E712"),sQuery(id+"F0.wireOp",EDGE,"E713"),sQuery(id+"F0.wireOp",EDGE,"E714"),sQuery(id+"F0.wireOp",EDGE,"E715"),sQuery(id+"F0.wireOp",EDGE,"E716"),sQuery(id+"F0.wireOp",EDGE,"E717"),sQuery(id+"F0.wireOp",EDGE,"E718"),sQuery(id+"F0.wireOp",EDGE,"E719"),sQuery(id+"F0.wireOp",EDGE,"E720"),sQuery(id+"F0.wireOp",EDGE,"E721"),sQuery(id+"F0.wireOp",EDGE,"E722"),sQuery(id+"F0.wireOp",EDGE,"E723"),sQuery(id+"F0.wireOp",EDGE,"E724"),sQuery(id+"F0.wireOp",EDGE,"E725"),sQuery(id+"F0.wireOp",EDGE,"E726"),sQuery(id+"F0.wireOp",EDGE,"E727"),sQuery(id+"F0.wireOp",EDGE,"E728"),sQuery(id+"F0.wireOp",EDGE,"E729"),sQuery(id+"F0.wireOp",EDGE,"E730"),sQuery(id+"F0.wireOp",EDGE,"E731"),sQuery(id+"F0.wireOp",EDGE,"E732"),sQuery(id+"F0.wireOp",EDGE,"E733"),sQuery(id+"F0.wireOp",EDGE,"E734"),sQuery(id+"F0.wireOp",EDGE,"E735"),sQuery(id+"F0.wireOp",EDGE,"E736"),sQuery(id+"F0.wireOp",EDGE,"E737"),sQuery(id+"F0.wireOp",EDGE,"E738"),sQuery(id+"F0.wireOp",EDGE,"E739"),sQuery(id+"F0.wireOp",EDGE,"E740"),sQuery(id+"F0.wireOp",EDGE,"E741"),sQuery(id+"F0.wireOp",EDGE,"E742"),sQuery(id+"F0.wireOp",EDGE,"E743"),sQuery(id+"F0.wireOp",EDGE,"E744"),sQuery(id+"F0.wireOp",EDGE,"E745"),sQuery(id+"F0.wireOp",EDGE,"E746"),sQuery(id+"F0.wireOp",EDGE,"E747"),sQuery(id+"F0.wireOp",EDGE,"E748"),sQuery(id+"F0.wireOp",EDGE,"E749"),sQuery(id+"F0.wireOp",EDGE,"E750"),sQuery(id+"F0.wireOp",EDGE,"E751"),sQuery(id+"F0.wireOp",EDGE,"E752"),sQuery(id+"F0.wireOp",EDGE,"E753"),sQuery(id+"F0.wireOp",EDGE,"E754"),sQuery(id+"F0.wireOp",EDGE,"E755"),sQuery(id+"F0.wireOp",EDGE,"E756"),sQuery(id+"F0.wireOp",EDGE,"E757"),sQuery(id+"F0.wireOp",EDGE,"E758"),sQuery(id+"F0.wireOp",EDGE,"E759"),sQuery(id+"F0.wireOp",EDGE,"E760"),sQuery(id+"F0.wireOp",EDGE,"E761"),sQuery(id+"F0.wireOp",EDGE,"E762"),sQuery(id+"F0.wireOp",EDGE,"E763"),sQuery(id+"F0.wireOp",EDGE,"E764"),sQuery(id+"F0.wireOp",EDGE,"E765"),sQuery(id+"F0.wireOp",EDGE,"E766"),sQuery(id+"F0.wireOp",EDGE,"E767"),sQuery(id+"F0.wireOp",EDGE,"E768"),sQuery(id+"F0.wireOp",EDGE,"E769"),sQuery(id+"F0.wireOp",EDGE,"E770"),sQuery(id+"F0.wireOp",EDGE,"E771"),sQuery(id+"F0.wireOp",EDGE,"E772"),sQuery(id+"F0.wireOp",EDGE,"E773"),sQuery(id+"F0.wireOp",EDGE,"E774"),sQuery(id+"F0.wireOp",EDGE,"E775"),sQuery(id+"F0.wireOp",EDGE,"E776"),sQuery(id+"F0.wireOp",EDGE,"E777"),sQuery(id+"F0.wireOp",EDGE,"E778"),sQuery(id+"F0.wireOp",EDGE,"E779"),sQuery(id+"F0.wireOp",EDGE,"E780"),sQuery(id+"F0.wireOp",EDGE,"E781"),sQuery(id+"F0.wireOp",EDGE,"E782"),sQuery(id+"F0.wireOp",EDGE,"E783"),sQuery(id+"F0.wireOp",EDGE,"E784"),sQuery(id+"F0.wireOp",EDGE,"E785"),sQuery(id+"F0.wireOp",EDGE,"E786"),sQuery(id+"F0.wireOp",EDGE,"E787"),sQuery(id+"F0.wireOp",EDGE,"E788"),sQuery(id+"F0.wireOp",EDGE,"E789"),sQuery(id+"F0.wireOp",EDGE,"E790"),sQuery(id+"F0.wireOp",EDGE,"E791"),sQuery(id+"F0.wireOp",EDGE,"E792"),sQuery(id+"F0.wireOp",EDGE,"E793"),sQuery(id+"F0.wireOp",EDGE,"E794"),sQuery(id+"F0.wireOp",EDGE,"E795"),sQuery(id+"F0.wireOp",EDGE,"E796"),sQuery(id+"F0.wireOp",EDGE,"E797"),sQuery(id+"F0.wireOp",EDGE,"E798"),sQuery(id+"F0.wireOp",EDGE,"E799"),sQuery(id+"F0.wireOp",EDGE,"E800"),sQuery(id+"F0.wireOp",EDGE,"E801"),sQuery(id+"F0.wireOp",EDGE,"E802"),sQuery(id+"F0.wireOp",EDGE,"E803"),sQuery(id+"F0.wireOp",EDGE,"E804"),sQuery(id+"F0.wireOp",EDGE,"E805"),sQuery(id+"F0.wireOp",EDGE,"E806"),sQuery(id+"F0.wireOp",EDGE,"E807"),sQuery(id+"F0.wireOp",EDGE,"E808"),sQuery(id+"F0.wireOp",EDGE,"E809"),sQuery(id+"F0.wireOp",EDGE,"E810"),sQuery(id+"F0.wireOp",EDGE,"E811"),sQuery(id+"F0.wireOp",EDGE,"E812"),sQuery(id+"F0.wireOp",EDGE,"E813"),sQuery(id+"F0.wireOp",EDGE,"E814"),sQuery(id+"F0.wireOp",EDGE,"E815"),sQuery(id+"F0.wireOp",EDGE,"E816"),sQuery(id+"F0.wireOp",EDGE,"E817"),sQuery(id+"F0.wireOp",EDGE,"E818"),sQuery(id+"F0.wireOp",EDGE,"E819"),sQuery(id+"F0.wireOp",EDGE,"E820"),sQuery(id+"F0.wireOp",EDGE,"E821"),sQuery(id+"F0.wireOp",EDGE,"E822"),sQuery(id+"F0.wireOp",EDGE,"E823"),sQuery(id+"F0.wireOp",EDGE,"E824"),sQuery(id+"F0.wireOp",EDGE,"E825"),sQuery(id+"F0.wireOp",EDGE,"E826"),sQuery(id+"F0.wireOp",EDGE,"E827"),sQuery(id+"F0.wireOp",EDGE,"E828"),sQuery(id+"F0.wireOp",EDGE,"E829"),sQuery(id+"F0.wireOp",EDGE,"E830"),sQuery(id+"F0.wireOp",EDGE,"E831"),sQuery(id+"F0.wireOp",EDGE,"E832"),sQuery(id+"F0.wireOp",EDGE,"E833"),sQuery(id+"F0.wireOp",EDGE,"E834"),sQuery(id+"F0.wireOp",EDGE,"E835"),sQuery(id+"F0.wireOp",EDGE,"E836"),sQuery(id+"F0.wireOp",EDGE,"E837"),sQuery(id+"F0.wireOp",EDGE,"E838"),sQuery(id+"F0.wireOp",EDGE,"E839"),sQuery(id+"F0.wireOp",EDGE,"E840"),sQuery(id+"F0.wireOp",EDGE,"E841"),sQuery(id+"F0.wireOp",EDGE,"E842"),sQuery(id+"F0.wireOp",EDGE,"E843"),sQuery(id+"F0.wireOp",EDGE,"E844"),sQuery(id+"F0.wireOp",EDGE,"E845"),sQuery(id+"F0.wireOp",EDGE,"E846"),sQuery(id+"F0.wireOp",EDGE,"E847"),sQuery(id+"F0.wireOp",EDGE,"E848"),sQuery(id+"F0.wireOp",EDGE,"E849"),sQuery(id+"F0.wireOp",EDGE,"E850"),sQuery(id+"F0.wireOp",EDGE,"E851"),sQuery(id+"F0.wireOp",EDGE,"E852"),sQuery(id+"F0.wireOp",EDGE,"E853"),sQuery(id+"F0.wireOp",EDGE,"E854"),sQuery(id+"F0.wireOp",EDGE,"E855"),sQuery(id+"F0.wireOp",EDGE,"E856"),sQuery(id+"F0.wireOp",EDGE,"E857"),sQuery(id+"F0.wireOp",EDGE,"E858"),sQuery(id+"F0.wireOp",EDGE,"E859"),sQuery(id+"F0.wireOp",EDGE,"E860"),sQuery(id+"F0.wireOp",EDGE,"E861"),sQuery(id+"F0.wireOp",EDGE,"E862"),sQuery(id+"F0.wireOp",EDGE,"E863"),sQuery(id+"F0.wireOp",EDGE,"E864"),sQuery(id+"F0.wireOp",EDGE,"E865"),sQuery(id+"F0.wireOp",EDGE,"E866"),sQuery(id+"F0.wireOp",EDGE,"E867"),sQuery(id+"F0.wireOp",EDGE,"E868"),sQuery(id+"F0.wireOp",EDGE,"E869"),sQuery(id+"F0.wireOp",EDGE,"E870"),sQuery(id+"F0.wireOp",EDGE,"E871"),sQuery(id+"F0.wireOp",EDGE,"E872"),sQuery(id+"F0.wireOp",EDGE,"E873"),sQuery(id+"F0.wireOp",EDGE,"E874"),sQuery(id+"F0.wireOp",EDGE,"E875"),sQuery(id+"F0.wireOp",EDGE,"E876"),sQuery(id+"F0.wireOp",EDGE,"E877"),sQuery(id+"F0.wireOp",EDGE,"E878"),sQuery(id+"F0.wireOp",EDGE,"E879"),sQuery(id+"F0.wireOp",EDGE,"E880"),sQuery(id+"F0.wireOp",EDGE,"E881"),sQuery(id+"F0.wireOp",EDGE,"E882"),sQuery(id+"F0.wireOp",EDGE,"E883"),sQuery(id+"F0.wireOp",EDGE,"E884"),sQuery(id+"F0.wireOp",EDGE,"E885"),sQuery(id+"F0.wireOp",EDGE,"E886"),sQuery(id+"F0.wireOp",EDGE,"E887"),sQuery(id+"F0.wireOp",EDGE,"E888"),sQuery(id+"F0.wireOp",EDGE,"E889"),sQuery(id+"F0.wireOp",EDGE,"E890"),sQuery(id+"F0.wireOp",EDGE,"E891"),sQuery(id+"F0.wireOp",EDGE,"E892"),sQuery(id+"F0.wireOp",EDGE,"E893"),sQuery(id+"F0.wireOp",EDGE,"E894"),sQuery(id+"F0.wireOp",EDGE,"E895"),sQuery(id+"F0.wireOp",EDGE,"E896"),sQuery(id+"F0.wireOp",EDGE,"E897"),sQuery(id+"F0.wireOp",EDGE,"E898"),sQuery(id+"F0.wireOp",EDGE,"E899"),sQuery(id+"F0.wireOp",EDGE,"E900"),sQuery(id+"F0.wireOp",EDGE,"E901"),sQuery(id+"F0.wireOp",EDGE,"E902"),sQuery(id+"F0.wireOp",EDGE,"E903"),sQuery(id+"F0.wireOp",EDGE,"E904"),sQuery(id+"F0.wireOp",EDGE,"E905"),sQuery(id+"F0.wireOp",EDGE,"E906"),sQuery(id+"F0.wireOp",EDGE,"E907"),sQuery(id+"F0.wireOp",EDGE,"E908"),sQuery(id+"F0.wireOp",EDGE,"E909"),sQuery(id+"F0.wireOp",EDGE,"E910"),sQuery(id+"F0.wireOp",EDGE,"E911"),sQuery(id+"F0.wireOp",EDGE,"E912"),sQuery(id+"F0.wireOp",EDGE,"E913"),sQuery(id+"F0.wireOp",EDGE,"E914"),sQuery(id+"F0.wireOp",EDGE,"E915"),sQuery(id+"F0.wireOp",EDGE,"E916"),sQuery(id+"F0.wireOp",EDGE,"E917"),sQuery(id+"F0.wireOp",EDGE,"E918"),sQuery(id+"F0.wireOp",EDGE,"E919"),sQuery(id+"F0.wireOp",EDGE,"E920"),sQuery(id+"F0.wireOp",EDGE,"E921"),sQuery(id+"F0.wireOp",EDGE,"E922"),sQuery(id+"F0.wireOp",EDGE,"E923"),sQuery(id+"F0.wireOp",EDGE,"E924"),sQuery(id+"F0.wireOp",EDGE,"E925"),sQuery(id+"F0.wireOp",EDGE,"E926"),sQuery(id+"F0.wireOp",EDGE,"E927"),sQuery(id+"F0.wireOp",EDGE,"E928"),sQuery(id+"F0.wireOp",EDGE,"E929"),sQuery(id+"F0.wireOp",EDGE,"E930"),sQuery(id+"F0.wireOp",EDGE,"E931"),sQuery(id+"F0.wireOp",EDGE,"E932"),sQuery(id+"F0.wireOp",EDGE,"E933"),sQuery(id+"F0.wireOp",EDGE,"E934"),sQuery(id+"F0.wireOp",EDGE,"E935"),sQuery(id+"F0.wireOp",EDGE,"E936"),sQuery(id+"F0.wireOp",EDGE,"E937"),sQuery(id+"F0.wireOp",EDGE,"E938"),sQuery(id+"F0.wireOp",EDGE,"E939"),sQuery(id+"F0.wireOp",EDGE,"E940"),sQuery(id+"F0.wireOp",EDGE,"E941"),sQuery(id+"F0.wireOp",EDGE,"E942"),sQuery(id+"F0.wireOp",EDGE,"E943"),sQuery(id+"F0.wireOp",EDGE,"E944"),sQuery(id+"F0.wireOp",EDGE,"E945"),sQuery(id+"F0.wireOp",EDGE,"E946"),sQuery(id+"F0.wireOp",EDGE,"E947"),sQuery(id+"F0.wireOp",EDGE,"E948"),sQuery(id+"F0.wireOp",EDGE,"E949"),sQuery(id+"F0.wireOp",EDGE,"E950"),sQuery(id+"F0.wireOp",EDGE,"E951"),sQuery(id+"F0.wireOp",EDGE,"E952"),sQuery(id+"F0.wireOp",EDGE,"E953"),sQuery(id+"F0.wireOp",EDGE,"E954"),sQuery(id+"F0.wireOp",EDGE,"E955"),sQuery(id+"F0.wireOp",EDGE,"E956"),sQuery(id+"F0.wireOp",EDGE,"E957"),sQuery(id+"F0.wireOp",EDGE,"E958"),sQuery(id+"F0.wireOp",EDGE,"E959"),sQuery(id+"F0.wireOp",EDGE,"E960"),sQuery(id+"F0.wireOp",EDGE,"E961"),sQuery(id+"F0.wireOp",EDGE,"E962"),sQuery(id+"F0.wireOp",EDGE,"E963"),sQuery(id+"F0.wireOp",EDGE,"E964"),sQuery(id+"F0.wireOp",EDGE,"E965"),sQuery(id+"F0.wireOp",EDGE,"E966"),sQuery(id+"F0.wireOp",EDGE,"E967"),sQuery(id+"F0.wireOp",EDGE,"E968"),sQuery(id+"F0.wireOp",EDGE,"E969"),sQuery(id+"F0.wireOp",EDGE,"E970"),sQuery(id+"F0.wireOp",EDGE,"E971"),sQuery(id+"F0.wireOp",EDGE,"E972"),sQuery(id+"F0.wireOp",EDGE,"E973"),sQuery(id+"F0.wireOp",EDGE,"E974"),sQuery(id+"F0.wireOp",EDGE,"E975"),sQuery(id+"F0.wireOp",EDGE,"E976"),sQuery(id+"F0.wireOp",EDGE,"E977"),sQuery(id+"F0.wireOp",EDGE,"E978"),sQuery(id+"F0.wireOp",EDGE,"E979"),sQuery(id+"F0.wireOp",EDGE,"E980"),sQuery(id+"F0.wireOp",EDGE,"E981"),sQuery(id+"F0.wireOp",EDGE,"E982"),sQuery(id+"F0.wireOp",EDGE,"E983"),sQuery(id+"F0.wireOp",EDGE,"E984"),sQuery(id+"F0.wireOp",EDGE,"E985"),sQuery(id+"F0.wireOp",EDGE,"E986"),sQuery(id+"F0.wireOp",EDGE,"E987"),sQuery(id+"F0.wireOp",EDGE,"E988"),sQuery(id+"F0.wireOp",EDGE,"E989"),sQuery(id+"F0.wireOp",EDGE,"E990"),sQuery(id+"F0.wireOp",EDGE,"E991"),sQuery(id+"F0.wireOp",EDGE,"E992"),sQuery(id+"F0.wireOp",EDGE,"E993"),sQuery(id+"F0.wireOp",EDGE,"E994"),sQuery(id+"F0.wireOp",EDGE,"E995"),sQuery(id+"F0.wireOp",EDGE,"E996"),sQuery(id+"F0.wireOp",EDGE,"E997"),sQuery(id+"F0.wireOp",EDGE,"E998"),sQuery(id+"F0.wireOp",EDGE,"E999"),sQuery(id+"F0.wireOp",EDGE,"E1000"),sQuery(id+"F0.wireOp",EDGE,"E1001"),sQuery(id+"F0.wireOp",EDGE,"E1002"),sQuery(id+"F0.wireOp",EDGE,"E1003"),sQuery(id+"F0.wireOp",EDGE,"E1004"),sQuery(id+"F0.wireOp",EDGE,"E1005"),sQuery(id+"F0.wireOp",EDGE,"E1006"),sQuery(id+"F0.wireOp",EDGE,"E1007"),sQuery(id+"F0.wireOp",EDGE,"E1008"),sQuery(id+"F0.wireOp",EDGE,"E1009"),sQuery(id+"F0.wireOp",EDGE,"E1010"),sQuery(id+"F0.wireOp",EDGE,"E1011"),sQuery(id+"F0.wireOp",EDGE,"E1012"),sQuery(id+"F0.wireOp",EDGE,"E1013"),sQuery(id+"F0.wireOp",EDGE,"E1014"),sQuery(id+"F0.wireOp",EDGE,"E1015"),sQuery(id+"F0.wireOp",EDGE,"E1016"),sQuery(id+"F0.wireOp",EDGE,"E1017"),sQuery(id+"F0.wireOp",EDGE,"E1018"),sQuery(id+"F0.wireOp",EDGE,"E1019"),sQuery(id+"F0.wireOp",EDGE,"E1020"),sQuery(id+"F0.wireOp",EDGE,"E1021"),sQuery(id+"F0.wireOp",EDGE,"E1022"),sQuery(id+"F0.wireOp",EDGE,"E1023"),sQuery(id+"F0.wireOp",EDGE,"E1024"),sQuery(id+"F0.wireOp",EDGE,"E1025"),sQuery(id+"F0.wireOp",EDGE,"E1026"),sQuery(id+"F0.wireOp",EDGE,"E1027"),sQuery(id+"F0.wireOp",EDGE,"E1028"),sQuery(id+"F0.wireOp",EDGE,"E1029"),sQuery(id+"F0.wireOp",EDGE,"E1030"),sQuery(id+"F0.wireOp",EDGE,"E1031"),sQuery(id+"F0.wireOp",EDGE,"E1032"),sQuery(id+"F0.wireOp",EDGE,"E1033"),sQuery(id+"F0.wireOp",EDGE,"E1034"),sQuery(id+"F0.wireOp",EDGE,"E1035"),sQuery(id+"F0.wireOp",EDGE,"E1036"),sQuery(id+"F0.wireOp",EDGE,"E1037"),sQuery(id+"F0.wireOp",EDGE,"E1038"),sQuery(id+"F0.wireOp",EDGE,"E1039"),sQuery(id+"F0.wireOp",EDGE,"E1040"),sQuery(id+"F0.wireOp",EDGE,"E1041"),sQuery(id+"F0.wireOp",EDGE,"E1042"),sQuery(id+"F0.wireOp",EDGE,"E1043"),sQuery(id+"F0.wireOp",EDGE,"E1044"),sQuery(id+"F0.wireOp",EDGE,"E1045"),sQuery(id+"F0.wireOp",EDGE,"E1046"),sQuery(id+"F0.wireOp",EDGE,"E1047"),sQuery(id+"F0.wireOp",EDGE,"E1048"),sQuery(id+"F0.wireOp",EDGE,"E1049"),sQuery(id+"F0.wireOp",EDGE,"E1050"),sQuery(id+"F0.wireOp",EDGE,"E1051"),sQuery(id+"F0.wireOp",EDGE,"E1052"),sQuery(id+"F0.wireOp",EDGE,"E1053"),sQuery(id+"F0.wireOp",EDGE,"E1054"),sQuery(id+"F0.wireOp",EDGE,"E1055"),sQuery(id+"F0.wireOp",EDGE,"E1056"),sQuery(id+"F0.wireOp",EDGE,"E1057"),sQuery(id+"F0.wireOp",EDGE,"E1058"),sQuery(id+"F0.wireOp",EDGE,"E1059"),sQuery(id+"F0.wireOp",EDGE,"E1060"),sQuery(id+"F0.wireOp",EDGE,"E1061"),sQuery(id+"F0.wireOp",EDGE,"E1062"),sQuery(id+"F0.wireOp",EDGE,"E1063"),sQuery(id+"F0.wireOp",EDGE,"E1064"),sQuery(id+"F0.wireOp",EDGE,"E1065"),sQuery(id+"F0.wireOp",EDGE,"E1066"),sQuery(id+"F0.wireOp",EDGE,"E1067"),sQuery(id+"F0.wireOp",EDGE,"E1068"),sQuery(id+"F0.wireOp",EDGE,"E1069"),sQuery(id+"F0.wireOp",EDGE,"E1070"),sQuery(id+"F0.wireOp",EDGE,"E1071"),sQuery(id+"F0.wireOp",EDGE,"E1072"),sQuery(id+"F0.wireOp",EDGE,"E1073"),sQuery(id+"F0.wireOp",EDGE,"E1074"),sQuery(id+"F0.wireOp",EDGE,"E1075"),sQuery(id+"F0.wireOp",EDGE,"E1076"),sQuery(id+"F0.wireOp",EDGE,"E1077"),sQuery(id+"F0.wireOp",EDGE,"E1078"),sQuery(id+"F0.wireOp",EDGE,"E1079"),sQuery(id+"F0.wireOp",EDGE,"E1080"),sQuery(id+"F0.wireOp",EDGE,"E1081"),sQuery(id+"F0.wireOp",EDGE,"E1082"),sQuery(id+"F0.wireOp",EDGE,"E1083"),sQuery(id+"F0.wireOp",EDGE,"E1084"),sQuery(id+"F0.wireOp",EDGE,"E1085"),sQuery(id+"F0.wireOp",EDGE,"E1086"),sQuery(id+"F0.wireOp",EDGE,"E1087"),sQuery(id+"F0.wireOp",EDGE,"E1088"),sQuery(id+"F0.wireOp",EDGE,"E1089"),sQuery(id+"F0.wireOp",EDGE,"E1090"),sQuery(id+"F0.wireOp",EDGE,"E1091"),sQuery(id+"F0.wireOp",EDGE,"E1092"),sQuery(id+"F0.wireOp",EDGE,"E1093"),sQuery(id+"F0.wireOp",EDGE,"E1094"),sQuery(id+"F0.wireOp",EDGE,"E1095"),sQuery(id+"F0.wireOp",EDGE,"E1096"),sQuery(id+"F0.wireOp",EDGE,"E1097"),sQuery(id+"F0.wireOp",EDGE,"E1098"),sQuery(id+"F0.wireOp",EDGE,"E1099"),sQuery(id+"F0.wireOp",EDGE,"E1100"),sQuery(id+"F0.wireOp",EDGE,"E1101"),sQuery(id+"F0.wireOp",EDGE,"E1102"),sQuery(id+"F0.wireOp",EDGE,"E1103"),sQuery(id+"F0.wireOp",EDGE,"E1104"),sQuery(id+"F0.wireOp",EDGE,"E1105"),sQuery(id+"F0.wireOp",EDGE,"E1106"),sQuery(id+"F0.wireOp",EDGE,"E1107"),sQuery(id+"F0.wireOp",EDGE,"E1108"),sQuery(id+"F0.wireOp",EDGE,"E1109"),sQuery(id+"F0.wireOp",EDGE,"E1110"),sQuery(id+"F0.wireOp",EDGE,"E1111"),sQuery(id+"F0.wireOp",EDGE,"E1112"),sQuery(id+"F0.wireOp",EDGE,"E1113"),sQuery(id+"F0.wireOp",EDGE,"E1114"),sQuery(id+"F0.wireOp",EDGE,"E1115"),sQuery(id+"F0.wireOp",EDGE,"E1116"),sQuery(id+"F0.wireOp",EDGE,"E1117"),sQuery(id+"F0.wireOp",EDGE,"E1118"),sQuery(id+"F0.wireOp",EDGE,"E1119"),sQuery(id+"F0.wireOp",EDGE,"E1120"),sQuery(id+"F0.wireOp",EDGE,"E1121"),sQuery(id+"F0.wireOp",EDGE,"E1122"),sQuery(id+"F0.wireOp",EDGE,"E1123"),sQuery(id+"F0.wireOp",EDGE,"E1124"),sQuery(id+"F0.wireOp",EDGE,"E1125"),sQuery(id+"F0.wireOp",EDGE,"E1126"),sQuery(id+"F0.wireOp",EDGE,"E1127"),sQuery(id+"F0.wireOp",EDGE,"E1128"),sQuery(id+"F0.wireOp",EDGE,"E1129"),sQuery(id+"F0.wireOp",EDGE,"E1130"),sQuery(id+"F0.wireOp",EDGE,"E1131"),sQuery(id+"F0.wireOp",EDGE,"E1132"),sQuery(id+"F0.wireOp",EDGE,"E1133"),sQuery(id+"F0.wireOp",EDGE,"E1134"),sQuery(id+"F0.wireOp",EDGE,"E1135"),sQuery(id+"F0.wireOp",EDGE,"E1136"),sQuery(id+"F0.wireOp",EDGE,"E1137"),sQuery(id+"F0.wireOp",EDGE,"E1138"),sQuery(id+"F0.wireOp",EDGE,"E1139"),sQuery(id+"F0.wireOp",EDGE,"E1140"),sQuery(id+"F0.wireOp",EDGE,"E1141"),sQuery(id+"F0.wireOp",EDGE,"E1142"),sQuery(id+"F0.wireOp",EDGE,"E1143"),sQuery(id+"F0.wireOp",EDGE,"E1144"),sQuery(id+"F0.wireOp",EDGE,"E1145"),sQuery(id+"F0.wireOp",EDGE,"E1146"),sQuery(id+"F0.wireOp",EDGE,"E1147"),sQuery(id+"F0.wireOp",EDGE,"E1148"),sQuery(id+"F0.wireOp",EDGE,"E1149"),sQuery(id+"F0.wireOp",EDGE,"E1150"),sQuery(id+"F0.wireOp",EDGE,"E1151"),sQuery(id+"F0.wireOp",EDGE,"E1152"),sQuery(id+"F0.wireOp",EDGE,"E1153"),sQuery(id+"F0.wireOp",EDGE,"E1154"),sQuery(id+"F0.wireOp",EDGE,"E1155"),sQuery(id+"F0.wireOp",EDGE,"E1156"),sQuery(id+"F0.wireOp",EDGE,"E1157"),sQuery(id+"F0.wireOp",EDGE,"E1158"),sQuery(id+"F0.wireOp",EDGE,"E1159"),sQuery(id+"F0.wireOp",EDGE,"E1160"),sQuery(id+"F0.wireOp",EDGE,"E1161"),sQuery(id+"F0.wireOp",EDGE,"E1162"),sQuery(id+"F0.wireOp",EDGE,"E1163"),sQuery(id+"F0.wireOp",EDGE,"E1164"),sQuery(id+"F0.wireOp",EDGE,"E1165"),sQuery(id+"F0.wireOp",EDGE,"E1166"),sQuery(id+"F0.wireOp",EDGE,"E1167"),sQuery(id+"F0.wireOp",EDGE,"E1168"),sQuery(id+"F0.wireOp",EDGE,"E1169"),sQuery(id+"F0.wireOp",EDGE,"E1170"),sQuery(id+"F0.wireOp",EDGE,"E1171"),sQuery(id+"F0.wireOp",EDGE,"E1172"),sQuery(id+"F0.wireOp",EDGE,"E1173"),sQuery(id+"F0.wireOp",EDGE,"E1174"),sQuery(id+"F0.wireOp",EDGE,"E1175"),sQuery(id+"F0.wireOp",EDGE,"E1176"),sQuery(id+"F0.wireOp",EDGE,"E1177"),sQuery(id+"F0.wireOp",EDGE,"E1178"),sQuery(id+"F0.wireOp",EDGE,"E1179"),sQuery(id+"F0.wireOp",EDGE,"E1180"),sQuery(id+"F0.wireOp",EDGE,"E1181"),sQuery(id+"F0.wireOp",EDGE,"E1182"),sQuery(id+"F0.wireOp",EDGE,"E1183"),sQuery(id+"F0.wireOp",EDGE,"E1184"),sQuery(id+"F0.wireOp",EDGE,"E1185"),sQuery(id+"F0.wireOp",EDGE,"E1186"),sQuery(id+"F0.wireOp",EDGE,"E1187"),sQuery(id+"F0.wireOp",EDGE,"E1188"),sQuery(id+"F0.wireOp",EDGE,"E1189"),sQuery(id+"F0.wireOp",EDGE,"E1190"),sQuery(id+"F0.wireOp",EDGE,"E1191"),sQuery(id+"F0.wireOp",EDGE,"E1192"),sQuery(id+"F0.wireOp",EDGE,"E1193"),sQuery(id+"F0.wireOp",EDGE,"E1194"),sQuery(id+"F0.wireOp",EDGE,"E1195"),sQuery(id+"F0.wireOp",EDGE,"E1196"),sQuery(id+"F0.wireOp",EDGE,"E1197"),sQuery(id+"F0.wireOp",EDGE,"E1198"),sQuery(id+"F0.wireOp",EDGE,"E1199"),sQuery(id+"F0.wireOp",EDGE,"E1200"),sQuery(id+"F0.wireOp",EDGE,"E1201"),sQuery(id+"F0.wireOp",EDGE,"E1202"),sQuery(id+"F0.wireOp",EDGE,"E1203"),sQuery(id+"F0.wireOp",EDGE,"E1204"),sQuery(id+"F0.wireOp",EDGE,"E1205"),sQuery(id+"F0.wireOp",EDGE,"E1206"),sQuery(id+"F0.wireOp",EDGE,"E1207"),sQuery(id+"F0.wireOp",EDGE,"E1208"),sQuery(id+"F0.wireOp",EDGE,"E1209"),sQuery(id+"F0.wireOp",EDGE,"E1210"),sQuery(id+"F0.wireOp",EDGE,"E1211"),sQuery(id+"F0.wireOp",EDGE,"E1212"),sQuery(id+"F0.wireOp",EDGE,"E1213"),sQuery(id+"F0.wireOp",EDGE,"E1214"),sQuery(id+"F0.wireOp",EDGE,"E1215"),sQuery(id+"F0.wireOp",EDGE,"E1216"),sQuery(id+"F0.wireOp",EDGE,"E1217"),sQuery(id+"F0.wireOp",EDGE,"E1218"),sQuery(id+"F0.wireOp",EDGE,"E1219"),sQuery(id+"F0.wireOp",EDGE,"E1220"),sQuery(id+"F0.wireOp",EDGE,"E1221"),sQuery(id+"F0.wireOp",EDGE,"E1222"),sQuery(id+"F0.wireOp",EDGE,"E1223"),sQuery(id+"F0.wireOp",EDGE,"E1224"),sQuery(id+"F0.wireOp",EDGE,"E1225"),sQuery(id+"F0.wireOp",EDGE,"E1226"),sQuery(id+"F0.wireOp",EDGE,"E1227"),sQuery(id+"F0.wireOp",EDGE,"E1228"),sQuery(id+"F0.wireOp",EDGE,"E1229"),sQuery(id+"F0.wireOp",EDGE,"E1230"),sQuery(id+"F0.wireOp",EDGE,"E1231"),sQuery(id+"F0.wireOp",EDGE,"E1232"),sQuery(id+"F0.wireOp",EDGE,"E1233"),sQuery(id+"F0.wireOp",EDGE,"E1234"),sQuery(id+"F0.wireOp",EDGE,"E1235"),sQuery(id+"F0.wireOp",EDGE,"E1236"),sQuery(id+"F0.wireOp",EDGE,"E1237"),sQuery(id+"F0.wireOp",EDGE,"E1238"),sQuery(id+"F0.wireOp",EDGE,"E1239"),sQuery(id+"F0.wireOp",EDGE,"E1240"),sQuery(id+"F0.wireOp",EDGE,"E1241"),sQuery(id+"F0.wireOp",EDGE,"E1242"),sQuery(id+"F0.wireOp",EDGE,"E1243"),sQuery(id+"F0.wireOp",EDGE,"E1244"),sQuery(id+"F0.wireOp",EDGE,"E1245"),sQuery(id+"F0.wireOp",EDGE,"E1246"),sQuery(id+"F0.wireOp",EDGE,"E1247"),sQuery(id+"F0.wireOp",EDGE,"E1248"),sQuery(id+"F0.wireOp",EDGE,"E1249"),sQuery(id+"F0.wireOp",EDGE,"E1250"),sQuery(id+"F0.wireOp",EDGE,"E1251"),sQuery(id+"F0.wireOp",EDGE,"E1252"),sQuery(id+"F0.wireOp",EDGE,"E1253"),sQuery(id+"F0.wireOp",EDGE,"E1254"),sQuery(id+"F0.wireOp",EDGE,"E1255"),sQuery(id+"F0.wireOp",EDGE,"E1256"),sQuery(id+"F0.wireOp",EDGE,"E1257"),sQuery(id+"F0.wireOp",EDGE,"E1258"),sQuery(id+"F0.wireOp",EDGE,"E1259"),sQuery(id+"F0.wireOp",EDGE,"E1260"),sQuery(id+"F0.wireOp",EDGE,"E1261"),sQuery(id+"F0.wireOp",EDGE,"E1262"),sQuery(id+"F0.wireOp",EDGE,"E1263"),sQuery(id+"F0.wireOp",EDGE,"E1264"),sQuery(id+"F0.wireOp",EDGE,"E1265"),sQuery(id+"F0.wireOp",EDGE,"E1266"),sQuery(id+"F0.wireOp",EDGE,"E1267"),sQuery(id+"F0.wireOp",EDGE,"E1268"),sQuery(id+"F0.wireOp",EDGE,"E1269"),sQuery(id+"F0.wireOp",EDGE,"E1270"),sQuery(id+"F0.wireOp",EDGE,"E1271"),sQuery(id+"F0.wireOp",EDGE,"E1272"),sQuery(id+"F0.wireOp",EDGE,"E1273"),sQuery(id+"F0.wireOp",EDGE,"E1274"),sQuery(id+"F0.wireOp",EDGE,"E1275"),sQuery(id+"F0.wireOp",EDGE,"E1276"),sQuery(id+"F0.wireOp",EDGE,"E1277"),sQuery(id+"F0.wireOp",EDGE,"E1278"),sQuery(id+"F0.wireOp",EDGE,"E1279"),sQuery(id+"F0.wireOp",EDGE,"E1280"),sQuery(id+"F0.wireOp",EDGE,"E1281"),sQuery(id+"F0.wireOp",EDGE,"E1282"),sQuery(id+"F0.wireOp",EDGE,"E1283"),sQuery(id+"F0.wireOp",EDGE,"E1284"),sQuery(id+"F0.wireOp",EDGE,"E1285"),sQuery(id+"F0.wireOp",EDGE,"E1286"),sQuery(id+"F0.wireOp",EDGE,"E1287"),sQuery(id+"F0.wireOp",EDGE,"E1288"),sQuery(id+"F0.wireOp",EDGE,"E1289"),sQuery(id+"F0.wireOp",EDGE,"E1290"),sQuery(id+"F0.wireOp",EDGE,"E1291"),sQuery(id+"F0.wireOp",EDGE,"E1292"),sQuery(id+"F0.wireOp",EDGE,"E1293"),sQuery(id+"F0.wireOp",EDGE,"E1294"),sQuery(id+"F0.wireOp",EDGE,"E1295"),sQuery(id+"F0.wireOp",EDGE,"E1296"),sQuery(id+"F0.wireOp",EDGE,"E1297"),sQuery(id+"F0.wireOp",EDGE,"E1298"),sQuery(id+"F0.wireOp",EDGE,"E1299"),sQuery(id+"F0.wireOp",EDGE,"E1300"),sQuery(id+"F0.wireOp",EDGE,"E1301"),sQuery(id+"F0.wireOp",EDGE,"E1302"),sQuery(id+"F0.wireOp",EDGE,"E1303"),sQuery(id+"F0.wireOp",EDGE,"E1304"),sQuery(id+"F0.wireOp",EDGE,"E1305"),sQuery(id+"F0.wireOp",EDGE,"E1306"),sQuery(id+"F0.wireOp",EDGE,"E1307"),sQuery(id+"F0.wireOp",EDGE,"E1308"),sQuery(id+"F0.wireOp",EDGE,"E1309"),sQuery(id+"F0.wireOp",EDGE,"E1310"),sQuery(id+"F0.wireOp",EDGE,"E1311"),sQuery(id+"F0.wireOp",EDGE,"E1312"),sQuery(id+"F0.wireOp",EDGE,"E1313"),sQuery(id+"F0.wireOp",EDGE,"E1314"),sQuery(id+"F0.wireOp",EDGE,"E1315"),sQuery(id+"F0.wireOp",EDGE,"E1316"),sQuery(id+"F0.wireOp",EDGE,"E1317"),sQuery(id+"F0.wireOp",EDGE,"E1318"),sQuery(id+"F0.wireOp",EDGE,"E1319"),sQuery(id+"F0.wireOp",EDGE,"E1320"),sQuery(id+"F0.wireOp",EDGE,"E1321"),sQuery(id+"F0.wireOp",EDGE,"E1322"),sQuery(id+"F0.wireOp",EDGE,"E1323"),sQuery(id+"F0.wireOp",EDGE,"E1324"),sQuery(id+"F0.wireOp",EDGE,"E1325"),sQuery(id+"F0.wireOp",EDGE,"E1326"),sQuery(id+"F0.wireOp",EDGE,"E1327"),sQuery(id+"F0.wireOp",EDGE,"E1328"),sQuery(id+"F0.wireOp",EDGE,"E1329"),sQuery(id+"F0.wireOp",EDGE,"E1330"),sQuery(id+"F0.wireOp",EDGE,"E1331"),sQuery(id+"F0.wireOp",EDGE,"E1332"),sQuery(id+"F0.wireOp",EDGE,"E1333"),sQuery(id+"F0.wireOp",EDGE,"E1334"),sQuery(id+"F0.wireOp",EDGE,"E1335"),sQuery(id+"F0.wireOp",EDGE,"E1336"),sQuery(id+"F0.wireOp",EDGE,"E1337"),sQuery(id+"F0.wireOp",EDGE,"E1338"),sQuery(id+"F0.wireOp",EDGE,"E1339"),sQuery(id+"F0.wireOp",EDGE,"E1340"),sQuery(id+"F0.wireOp",EDGE,"E1341"),sQuery(id+"F0.wireOp",EDGE,"E1342"),sQuery(id+"F0.wireOp",EDGE,"E1343"),sQuery(id+"F0.wireOp",EDGE,"E1344"),sQuery(id+"F0.wireOp",EDGE,"E1345"),sQuery(id+"F0.wireOp",EDGE,"E1346"),sQuery(id+"F0.wireOp",EDGE,"E1347"),sQuery(id+"F0.wireOp",EDGE,"E1348"),sQuery(id+"F0.wireOp",EDGE,"E1349"),sQuery(id+"F0.wireOp",EDGE,"E1350"),sQuery(id+"F0.wireOp",EDGE,"E1351"),sQuery(id+"F0.wireOp",EDGE,"E1352"),sQuery(id+"F0.wireOp",EDGE,"E1353"),sQuery(id+"F0.wireOp",EDGE,"E1354"),sQuery(id+"F0.wireOp",EDGE,"E1355"),sQuery(id+"F0.wireOp",EDGE,"E1356"),sQuery(id+"F0.wireOp",EDGE,"E1357"),sQuery(id+"F0.wireOp",EDGE,"E1358"),sQuery(id+"F0.wireOp",EDGE,"E1359"),sQuery(id+"F0.wireOp",EDGE,"E1360"),sQuery(id+"F0.wireOp",EDGE,"E1361"),sQuery(id+"F0.wireOp",EDGE,"E1362"),sQuery(id+"F0.wireOp",EDGE,"E1363"),sQuery(id+"F0.wireOp",EDGE,"E1364"),sQuery(id+"F0.wireOp",EDGE,"E1365"),sQuery(id+"F0.wireOp",EDGE,"E1366"),sQuery(id+"F0.wireOp",EDGE,"E1367"),sQuery(id+"F0.wireOp",EDGE,"E1368"),sQuery(id+"F0.wireOp",EDGE,"E1369"),sQuery(id+"F0.wireOp",EDGE,"E1370"),sQuery(id+"F0.wireOp",EDGE,"E1371"),sQuery(id+"F0.wireOp",EDGE,"E1372"),sQuery(id+"F0.wireOp",EDGE,"E1373"),sQuery(id+"F0.wireOp",EDGE,"E1374"),sQuery(id+"F0.wireOp",EDGE,"E1375"),sQuery(id+"F0.wireOp",EDGE,"E1376"),sQuery(id+"F0.wireOp",EDGE,"E1377"),sQuery(id+"F0.wireOp",EDGE,"E1378"),sQuery(id+"F0.wireOp",EDGE,"E1379"),sQuery(id+"F0.wireOp",EDGE,"E1380"),sQuery(id+"F0.wireOp",EDGE,"E1381"),sQuery(id+"F0.wireOp",EDGE,"E1382"),sQuery(id+"F0.wireOp",EDGE,"E1383"),sQuery(id+"F0.wireOp",EDGE,"E1384"),sQuery(id+"F0.wireOp",EDGE,"E1385"),sQuery(id+"F0.wireOp",EDGE,"E1386"),sQuery(id+"F0.wireOp",EDGE,"E1387"),sQuery(id+"F0.wireOp",EDGE,"E1388"),sQuery(id+"F0.wireOp",EDGE,"E1389"),sQuery(id+"F0.wireOp",EDGE,"E1390"),sQuery(id+"F0.wireOp",EDGE,"E1391"),sQuery(id+"F0.wireOp",EDGE,"E1392"),sQuery(id+"F0.wireOp",EDGE,"E1393"),sQuery(id+"F0.wireOp",EDGE,"E1394"),sQuery(id+"F0.wireOp",EDGE,"E1395"),sQuery(id+"F0.wireOp",EDGE,"E1396"),sQuery(id+"F0.wireOp",EDGE,"E1397"),sQuery(id+"F0.wireOp",EDGE,"E1398"),sQuery(id+"F0.wireOp",EDGE,"E1399"),sQuery(id+"F0.wireOp",EDGE,"E1400"),sQuery(id+"F0.wireOp",EDGE,"E1401"),sQuery(id+"F0.wireOp",EDGE,"E1402"),sQuery(id+"F0.wireOp",EDGE,"E1403"),sQuery(id+"F0.wireOp",EDGE,"E1404"),sQuery(id+"F0.wireOp",EDGE,"E1405"),sQuery(id+"F0.wireOp",EDGE,"E1406"),sQuery(id+"F0.wireOp",EDGE,"E1407"),sQuery(id+"F0.wireOp",EDGE,"E1408"),sQuery(id+"F0.wireOp",EDGE,"E1409"),sQuery(id+"F0.wireOp",EDGE,"E1410"),sQuery(id+"F0.wireOp",EDGE,"E1411"),sQuery(id+"F0.wireOp",EDGE,"E1412"),sQuery(id+"F0.wireOp",EDGE,"E1413"),sQuery(id+"F0.wireOp",EDGE,"E1414"),sQuery(id+"F0.wireOp",EDGE,"E1415"),sQuery(id+"F0.wireOp",EDGE,"E1416"),sQuery(id+"F0.wireOp",EDGE,"E1417"),sQuery(id+"F0.wireOp",EDGE,"E1418"),sQuery(id+"F0.wireOp",EDGE,"E1419"),sQuery(id+"F0.wireOp",EDGE,"E1420"),sQuery(id+"F0.wireOp",EDGE,"E1421"),sQuery(id+"F0.wireOp",EDGE,"E1422"),sQuery(id+"F0.wireOp",EDGE,"E1423"),sQuery(id+"F0.wireOp",EDGE,"E1424"),sQuery(id+"F0.wireOp",EDGE,"E1425"),sQuery(id+"F0.wireOp",EDGE,"E1426"),sQuery(id+"F0.wireOp",EDGE,"E1427"),sQuery(id+"F0.wireOp",EDGE,"E1428"),sQuery(id+"F0.wireOp",EDGE,"E1429"),sQuery(id+"F0.wireOp",EDGE,"E1430"),sQuery(id+"F0.wireOp",EDGE,"E1431"),sQuery(id+"F0.wireOp",EDGE,"E1432"),sQuery(id+"F0.wireOp",EDGE,"E1433"),sQuery(id+"F0.wireOp",EDGE,"E1434"),sQuery(id+"F0.wireOp",EDGE,"E1435"),sQuery(id+"F0.wireOp",EDGE,"E1436"),sQuery(id+"F0.wireOp",EDGE,"E1437"),sQuery(id+"F0.wireOp",EDGE,"E1438"),sQuery(id+"F0.wireOp",EDGE,"E1439"),sQuery(id+"F0.wireOp",EDGE,"E1440"),sQuery(id+"F0.wireOp",EDGE,"E1441"),sQuery(id+"F0.wireOp",EDGE,"E1442"),sQuery(id+"F0.wireOp",EDGE,"E1443"),sQuery(id+"F0.wireOp",EDGE,"E1444"),sQuery(id+"F0.wireOp",EDGE,"E1445"),sQuery(id+"F0.wireOp",EDGE,"E1446"),sQuery(id+"F0.wireOp",EDGE,"E1447"),sQuery(id+"F0.wireOp",EDGE,"E1448"),sQuery(id+"F0.wireOp",EDGE,"E1449"),sQuery(id+"F0.wireOp",EDGE,"E1450"),sQuery(id+"F0.wireOp",EDGE,"E1451"),sQuery(id+"F0.wireOp",EDGE,"E1452"),sQuery(id+"F0.wireOp",EDGE,"E1453"),sQuery(id+"F0.wireOp",EDGE,"E1454"),sQuery(id+"F0.wireOp",EDGE,"E1455"),sQuery(id+"F0.wireOp",EDGE,"E1456"),sQuery(id+"F0.wireOp",EDGE,"E1457"),sQuery(id+"F0.wireOp",EDGE,"E1458"),sQuery(id+"F0.wireOp",EDGE,"E1459"),sQuery(id+"F0.wireOp",EDGE,"E1460"),sQuery(id+"F0.wireOp",EDGE,"E1461"),sQuery(id+"F0.wireOp",EDGE,"E1462"),sQuery(id+"F0.wireOp",EDGE,"E1463"),sQuery(id+"F0.wireOp",EDGE,"E1464"),sQuery(id+"F0.wireOp",EDGE,"E1465"),sQuery(id+"F0.wireOp",EDGE,"E1466"),sQuery(id+"F0.wireOp",EDGE,"E1467"),sQuery(id+"F0.wireOp",EDGE,"E1468"),sQuery(id+"F0.wireOp",EDGE,"E1469"),sQuery(id+"F0.wireOp",EDGE,"E1470"),sQuery(id+"F0.wireOp",EDGE,"E1471"),sQuery(id+"F0.wireOp",EDGE,"E1472"),sQuery(id+"F0.wireOp",EDGE,"E1473"),sQuery(id+"F0.wireOp",EDGE,"E1474"),sQuery(id+"F0.wireOp",EDGE,"E1475"),sQuery(id+"F0.wireOp",EDGE,"E1476"),sQuery(id+"F0.wireOp",EDGE,"E1477"),sQuery(id+"F0.wireOp",EDGE,"E1478"),sQuery(id+"F0.wireOp",EDGE,"E1479"),sQuery(id+"F0.wireOp",EDGE,"E1480"),sQuery(id+"F0.wireOp",EDGE,"E1481"),sQuery(id+"F0.wireOp",EDGE,"E1482"),sQuery(id+"F0.wireOp",EDGE,"E1483"),sQuery(id+"F0.wireOp",EDGE,"E1484"),sQuery(id+"F0.wireOp",EDGE,"E1485"),sQuery(id+"F0.wireOp",EDGE,"E1486"),sQuery(id+"F0.wireOp",EDGE,"E1487"),sQuery(id+"F0.wireOp",EDGE,"E1488"),sQuery(id+"F0.wireOp",EDGE,"E1489"),sQuery(id+"F0.wireOp",EDGE,"E1490"),sQuery(id+"F0.wireOp",EDGE,"E1491"),sQuery(id+"F0.wireOp",EDGE,"E1492"),sQuery(id+"F0.wireOp",EDGE,"E1493"),sQuery(id+"F0.wireOp",EDGE,"E1494"),sQuery(id+"F0.wireOp",EDGE,"E1495"),sQuery(id+"F0.wireOp",EDGE,"E1496"),sQuery(id+"F0.wireOp",EDGE,"E1497"),sQuery(id+"F0.wireOp",EDGE,"E1498"),sQuery(id+"F0.wireOp",EDGE,"E1499"),sQuery(id+"F0.wireOp",EDGE,"E1500"),sQuery(id+"F0.wireOp",EDGE,"E1501"),sQuery(id+"F0.wireOp",EDGE,"E1502"),sQuery(id+"F0.wireOp",EDGE,"E1503"),sQuery(id+"F0.wireOp",EDGE,"E1504"),sQuery(id+"F0.wireOp",EDGE,"E1505"),sQuery(id+"F0.wireOp",EDGE,"E1506"),sQuery(id+"F0.wireOp",EDGE,"E1507"),sQuery(id+"F0.wireOp",EDGE,"E1508"),sQuery(id+"F0.wireOp",EDGE,"E1509"),sQuery(id+"F0.wireOp",EDGE,"E1510"),sQuery(id+"F0.wireOp",EDGE,"E1511"),sQuery(id+"F0.wireOp",EDGE,"E1512"),sQuery(id+"F0.wireOp",EDGE,"E1513"),sQuery(id+"F0.wireOp",EDGE,"E1514"),sQuery(id+"F0.wireOp",EDGE,"E1515"),sQuery(id+"F0.wireOp",EDGE,"E1516"),sQuery(id+"F0.wireOp",EDGE,"E1517"),sQuery(id+"F0.wireOp",EDGE,"E1518"),sQuery(id+"F0.wireOp",EDGE,"E1519"),sQuery(id+"F0.wireOp",EDGE,"E1520"),sQuery(id+"F0.wireOp",EDGE,"E1521"),sQuery(id+"F0.wireOp",EDGE,"E1522"),sQuery(id+"F0.wireOp",EDGE,"E1523"),sQuery(id+"F0.wireOp",EDGE,"E1524"),sQuery(id+"F0.wireOp",EDGE,"E1525"),sQuery(id+"F0.wireOp",EDGE,"E1526"),sQuery(id+"F0.wireOp",EDGE,"E1527"),sQuery(id+"F0.wireOp",EDGE,"E1528"),sQuery(id+"F0.wireOp",EDGE,"E1529"),sQuery(id+"F0.wireOp",EDGE,"E1530"),sQuery(id+"F0.wireOp",EDGE,"E1531"),sQuery(id+"F0.wireOp",EDGE,"E1532"),sQuery(id+"F0.wireOp",EDGE,"E1533"),sQuery(id+"F0.wireOp",EDGE,"E1534"),sQuery(id+"F0.wireOp",EDGE,"E1535"),sQuery(id+"F0.wireOp",EDGE,"E1536"),sQuery(id+"F0.wireOp",EDGE,"E1537"),sQuery(id+"F0.wireOp",EDGE,"E1538"),sQuery(id+"F0.wireOp",EDGE,"E1539"),sQuery(id+"F0.wireOp",EDGE,"E1540"),sQuery(id+"F0.wireOp",EDGE,"E1541"),sQuery(id+"F0.wireOp",EDGE,"E1542"),sQuery(id+"F0.wireOp",EDGE,"E1543"),sQuery(id+"F0.wireOp",EDGE,"E1544"),sQuery(id+"F0.wireOp",EDGE,"E1545"),sQuery(id+"F0.wireOp",EDGE,"E1546"),sQuery(id+"F0.wireOp",EDGE,"E1547"),sQuery(id+"F0.wireOp",EDGE,"E1548"),sQuery(id+"F0.wireOp",EDGE,"E1549"),sQuery(id+"F0.wireOp",EDGE,"E1550"),sQuery(id+"F0.wireOp",EDGE,"E1551"),sQuery(id+"F0.wireOp",EDGE,"E1552"),sQuery(id+"F0.wireOp",EDGE,"E1553"),sQuery(id+"F0.wireOp",EDGE,"E1554"),sQuery(id+"F0.wireOp",EDGE,"E1555"),sQuery(id+"F0.wireOp",EDGE,"E1556"),sQuery(id+"F0.wireOp",EDGE,"E1557"),sQuery(id+"F0.wireOp",EDGE,"E1558"),sQuery(id+"F0.wireOp",EDGE,"E1559"),sQuery(id+"F0.wireOp",EDGE,"E1560"),sQuery(id+"F0.wireOp",EDGE,"E1561"),sQuery(id+"F0.wireOp",EDGE,"E1562"),sQuery(id+"F0.wireOp",EDGE,"E1563"),sQuery(id+"F0.wireOp",EDGE,"E1564"),sQuery(id+"F0.wireOp",EDGE,"E1565"),sQuery(id+"F0.wireOp",EDGE,"E1566"),sQuery(id+"F0.wireOp",EDGE,"E1567"),sQuery(id+"F0.wireOp",EDGE,"E1568"),sQuery(id+"F0.wireOp",EDGE,"E1569"),sQuery(id+"F0.wireOp",EDGE,"E1570"),sQuery(id+"F0.wireOp",EDGE,"E1571"),sQuery(id+"F0.wireOp",EDGE,"E1572"),sQuery(id+"F0.wireOp",EDGE,"E1573"),sQuery(id+"F0.wireOp",EDGE,"E1574"),sQuery(id+"F0.wireOp",EDGE,"E1575"),sQuery(id+"F0.wireOp",EDGE,"E1576"),sQuery(id+"F0.wireOp",EDGE,"E1577"),sQuery(id+"F0.wireOp",EDGE,"E1578"),sQuery(id+"F0.wireOp",EDGE,"E1579"),sQuery(id+"F0.wireOp",EDGE,"E1580"),sQuery(id+"F0.wireOp",EDGE,"E1581"),sQuery(id+"F0.wireOp",EDGE,"E1582"),sQuery(id+"F0.wireOp",EDGE,"E1583"),sQuery(id+"F0.wireOp",EDGE,"E1584"),sQuery(id+"F0.wireOp",EDGE,"E1585"),sQuery(id+"F0.wireOp",EDGE,"E1586"),sQuery(id+"F0.wireOp",EDGE,"E1587"),sQuery(id+"F0.wireOp",EDGE,"E1588"),sQuery(id+"F0.wireOp",EDGE,"E1589"),sQuery(id+"F0.wireOp",EDGE,"E1590"),sQuery(id+"F0.wireOp",EDGE,"E1591"),sQuery(id+"F0.wireOp",EDGE,"E1592"),sQuery(id+"F0.wireOp",EDGE,"E1593"),sQuery(id+"F0.wireOp",EDGE,"E1594"),sQuery(id+"F0.wireOp",EDGE,"E1595"),sQuery(id+"F0.wireOp",EDGE,"E1596"),sQuery(id+"F0.wireOp",EDGE,"E1597"),sQuery(id+"F0.wireOp",EDGE,"E1598"),sQuery(id+"F0.wireOp",EDGE,"E1599"),sQuery(id+"F0.wireOp",EDGE,"E1600"),sQuery(id+"F0.wireOp",EDGE,"E1601"),sQuery(id+"F0.wireOp",EDGE,"E1602"),sQuery(id+"F0.wireOp",EDGE,"E1603"),sQuery(id+"F0.wireOp",EDGE,"E1604"),sQuery(id+"F0.wireOp",EDGE,"E1605"),sQuery(id+"F0.wireOp",EDGE,"E1606"),sQuery(id+"F0.wireOp",EDGE,"E1607"),sQuery(id+"F0.wireOp",EDGE,"E1608"),sQuery(id+"F0.wireOp",EDGE,"E1609"),sQuery(id+"F0.wireOp",EDGE,"E1610"),sQuery(id+"F0.wireOp",EDGE,"E1611"),sQuery(id+"F0.wireOp",EDGE,"E1612"),sQuery(id+"F0.wireOp",EDGE,"E1613"),sQuery(id+"F0.wireOp",EDGE,"E1614"),sQuery(id+"F0.wireOp",EDGE,"E1615"),sQuery(id+"F0.wireOp",EDGE,"E1616"),sQuery(id+"F0.wireOp",EDGE,"E1617"),sQuery(id+"F0.wireOp",EDGE,"E1618"),sQuery(id+"F0.wireOp",EDGE,"E1619"),sQuery(id+"F0.wireOp",EDGE,"E1620"),sQuery(id+"F0.wireOp",EDGE,"E1621"),sQuery(id+"F0.wireOp",EDGE,"E1622"),sQuery(id+"F0.wireOp",EDGE,"E1623"),sQuery(id+"F0.wireOp",EDGE,"E1624"),sQuery(id+"F0.wireOp",EDGE,"E1625"),sQuery(id+"F0.wireOp",EDGE,"E1626"),sQuery(id+"F0.wireOp",EDGE,"E1627"),sQuery(id+"F0.wireOp",EDGE,"E1628"),sQuery(id+"F0.wireOp",EDGE,"E1629"),sQuery(id+"F0.wireOp",EDGE,"E1630"),sQuery(id+"F0.wireOp",EDGE,"E1631"),sQuery(id+"F0.wireOp",EDGE,"E1632"),sQuery(id+"F0.wireOp",EDGE,"E1633"),sQuery(id+"F0.wireOp",EDGE,"E1634"),sQuery(id+"F0.wireOp",EDGE,"E1635"),sQuery(id+"F0.wireOp",EDGE,"E1636"),sQuery(id+"F0.wireOp",EDGE,"E1637"),sQuery(id+"F0.wireOp",EDGE,"E1638"),sQuery(id+"F0.wireOp",EDGE,"E1639"),sQuery(id+"F0.wireOp",EDGE,"E1640"),sQuery(id+"F0.wireOp",EDGE,"E1641"),sQuery(id+"F0.wireOp",EDGE,"E1642"),sQuery(id+"F0.wireOp",EDGE,"E1643"),sQuery(id+"F0.wireOp",EDGE,"E1644"),sQuery(id+"F0.wireOp",EDGE,"E1645"),sQuery(id+"F0.wireOp",EDGE,"E1646"),sQuery(id+"F0.wireOp",EDGE,"E1647"),sQuery(id+"F0.wireOp",EDGE,"E1648"),sQuery(id+"F0.wireOp",EDGE,"E1649"),sQuery(id+"F0.wireOp",EDGE,"E1650"),sQuery(id+"F0.wireOp",EDGE,"E1651"),sQuery(id+"F0.wireOp",EDGE,"E1652"),sQuery(id+"F0.wireOp",EDGE,"E1653"),sQuery(id+"F0.wireOp",EDGE,"E1654"),sQuery(id+"F0.wireOp",EDGE,"E1655"),sQuery(id+"F0.wireOp",EDGE,"E1656"),sQuery(id+"F0.wireOp",EDGE,"E1657"),sQuery(id+"F0.wireOp",EDGE,"E1658"),sQuery(id+"F0.wireOp",EDGE,"E1659"),sQuery(id+"F0.wireOp",EDGE,"E1660"),sQuery(id+"F0.wireOp",EDGE,"E1661"),sQuery(id+"F0.wireOp",EDGE,"E1662"),sQuery(id+"F0.wireOp",EDGE,"E1663"),sQuery(id+"F0.wireOp",EDGE,"E1664"),sQuery(id+"F0.wireOp",EDGE,"E1665"),sQuery(id+"F0.wireOp",EDGE,"E1666"),sQuery(id+"F0.wireOp",EDGE,"E1667"),sQuery(id+"F0.wireOp",EDGE,"E1668"),sQuery(id+"F0.wireOp",EDGE,"E1669"),sQuery(id+"F0.wireOp",EDGE,"E1670"),sQuery(id+"F0.wireOp",EDGE,"E1671"),sQuery(id+"F0.wireOp",EDGE,"E1672"),sQuery(id+"F0.wireOp",EDGE,"E1673"),sQuery(id+"F0.wireOp",EDGE,"E1674"),sQuery(id+"F0.wireOp",EDGE,"E1675"),sQuery(id+"F0.wireOp",EDGE,"E1676"),sQuery(id+"F0.wireOp",EDGE,"E1677"),sQuery(id+"F0.wireOp",EDGE,"E1678"),sQuery(id+"F0.wireOp",EDGE,"E1679"),sQuery(id+"F0.wireOp",EDGE,"E1680"),sQuery(id+"F0.wireOp",EDGE,"E1681"),sQuery(id+"F0.wireOp",EDGE,"E1682"),sQuery(id+"F0.wireOp",EDGE,"E1683"),sQuery(id+"F0.wireOp",EDGE,"E1684"),sQuery(id+"F0.wireOp",EDGE,"E1685"),sQuery(id+"F0.wireOp",EDGE,"E1686"),sQuery(id+"F0.wireOp",EDGE,"E1687"),sQuery(id+"F0.wireOp",EDGE,"E1688"),sQuery(id+"F0.wireOp",EDGE,"E1689"),sQuery(id+"F0.wireOp",EDGE,"E1690"),sQuery(id+"F0.wireOp",EDGE,"E1691"),sQuery(id+"F0.wireOp",EDGE,"E1692"),sQuery(id+"F0.wireOp",EDGE,"E1693"),sQuery(id+"F0.wireOp",EDGE,"E1694"),sQuery(id+"F0.wireOp",EDGE,"E1695"),sQuery(id+"F0.wireOp",EDGE,"E1696"),sQuery(id+"F0.wireOp",EDGE,"E1697"),sQuery(id+"F0.wireOp",EDGE,"E1698"),sQuery(id+"F0.wireOp",EDGE,"E1699"),sQuery(id+"F0.wireOp",EDGE,"E1700"),sQuery(id+"F0.wireOp",EDGE,"E1701"),sQuery(id+"F0.wireOp",EDGE,"E1702"),sQuery(id+"F0.wireOp",EDGE,"E1703"),sQuery(id+"F0.wireOp",EDGE,"E1704"),sQuery(id+"F0.wireOp",EDGE,"E1705"),sQuery(id+"F0.wireOp",EDGE,"E1706"),sQuery(id+"F0.wireOp",EDGE,"E1707"),sQuery(id+"F0.wireOp",EDGE,"E1708"),sQuery(id+"F0.wireOp",EDGE,"E1709"),sQuery(id+"F0.wireOp",EDGE,"E1710"),sQuery(id+"F0.wireOp",EDGE,"E1711"),sQuery(id+"F0.wireOp",EDGE,"E1712"),sQuery(id+"F0.wireOp",EDGE,"E1713"),sQuery(id+"F0.wireOp",EDGE,"E1714"),sQuery(id+"F0.wireOp",EDGE,"E1715"),sQuery(id+"F0.wireOp",EDGE,"E1716"),sQuery(id+"F0.wireOp",EDGE,"E1717"),sQuery(id+"F0.wireOp",EDGE,"E1718"),sQuery(id+"F0.wireOp",EDGE,"E1719"),sQuery(id+"F0.wireOp",EDGE,"E1720"),sQuery(id+"F0.wireOp",EDGE,"E1721"),sQuery(id+"F0.wireOp",EDGE,"E1722"),sQuery(id+"F0.wireOp",EDGE,"E1723"),sQuery(id+"F0.wireOp",EDGE,"E1724"),sQuery(id+"F0.wireOp",EDGE,"E1725"),sQuery(id+"F0.wireOp",EDGE,"E1726"),sQuery(id+"F0.wireOp",EDGE,"E1727"),sQuery(id+"F0.wireOp",EDGE,"E1728"),sQuery(id+"F0.wireOp",EDGE,"E1729"),sQuery(id+"F0.wireOp",EDGE,"E1730"),sQuery(id+"F0.wireOp",EDGE,"E1731"),sQuery(id+"F0.wireOp",EDGE,"E1732"),sQuery(id+"F0.wireOp",EDGE,"E1733"),sQuery(id+"F0.wireOp",EDGE,"E1734"),sQuery(id+"F0.wireOp",EDGE,"E1735"),sQuery(id+"F0.wireOp",EDGE,"E1736"),sQuery(id+"F0.wireOp",EDGE,"E1737"),sQuery(id+"F0.wireOp",EDGE,"E1738"),sQuery(id+"F0.wireOp",EDGE,"E1739"),sQuery(id+"F0.wireOp",EDGE,"E1740"),sQuery(id+"F0.wireOp",EDGE,"E1741"),sQuery(id+"F0.wireOp",EDGE,"E1742"),sQuery(id+"F0.wireOp",EDGE,"E1743"),sQuery(id+"F0.wireOp",EDGE,"E1744"),sQuery(id+"F0.wireOp",EDGE,"E1745"),sQuery(id+"F0.wireOp",EDGE,"E1746"),sQuery(id+"F0.wireOp",EDGE,"E1747"),sQuery(id+"F0.wireOp",EDGE,"E1748"),sQuery(id+"F0.wireOp",EDGE,"E1749"),sQuery(id+"F0.wireOp",EDGE,"E1750"),sQuery(id+"F0.wireOp",EDGE,"E1751"),sQuery(id+"F0.wireOp",EDGE,"E1752"),sQuery(id+"F0.wireOp",EDGE,"E1753"),sQuery(id+"F0.wireOp",EDGE,"E1754"),sQuery(id+"F0.wireOp",EDGE,"E1755"),sQuery(id+"F0.wireOp",EDGE,"E1756"),sQuery(id+"F0.wireOp",EDGE,"E1757"),sQuery(id+"F0.wireOp",EDGE,"E1758"),sQuery(id+"F0.wireOp",EDGE,"E1759"),sQuery(id+"F0.wireOp",EDGE,"E1760"),sQuery(id+"F0.wireOp",EDGE,"E1761"),sQuery(id+"F0.wireOp",EDGE,"E1762"),sQuery(id+"F0.wireOp",EDGE,"E1763"),sQuery(id+"F0.wireOp",EDGE,"E1764"),sQuery(id+"F0.wireOp",EDGE,"E1765"),sQuery(id+"F0.wireOp",EDGE,"E1766"),sQuery(id+"F0.wireOp",EDGE,"E1767"),sQuery(id+"F0.wireOp",EDGE,"E1768"),sQuery(id+"F0.wireOp",EDGE,"E1769"),sQuery(id+"F0.wireOp",EDGE,"E1770"),sQuery(id+"F0.wireOp",EDGE,"E1771"),sQuery(id+"F0.wireOp",EDGE,"E1772"),sQuery(id+"F0.wireOp",EDGE,"E1773"),sQuery(id+"F0.wireOp",EDGE,"E1774"),sQuery(id+"F0.wireOp",EDGE,"E1775"),sQuery(id+"F0.wireOp",EDGE,"E1776"),sQuery(id+"F0.wireOp",EDGE,"E1777"),sQuery(id+"F0.wireOp",EDGE,"E1778"),sQuery(id+"F0.wireOp",EDGE,"E1779"),sQuery(id+"F0.wireOp",EDGE,"E1780"),sQuery(id+"F0.wireOp",EDGE,"E1781"),sQuery(id+"F0.wireOp",EDGE,"E1782"),sQuery(id+"F0.wireOp",EDGE,"E1783"),sQuery(id+"F0.wireOp",EDGE,"E1784"),sQuery(id+"F0.wireOp",EDGE,"E1785"),sQuery(id+"F0.wireOp",EDGE,"E1786"),sQuery(id+"F0.wireOp",EDGE,"E1787"),sQuery(id+"F0.wireOp",EDGE,"E1788"),sQuery(id+"F0.wireOp",EDGE,"E1789"),sQuery(id+"F0.wireOp",EDGE,"E1790"),sQuery(id+"F0.wireOp",EDGE,"E1791"),sQuery(id+"F0.wireOp",EDGE,"E1792"),sQuery(id+"F0.wireOp",EDGE,"E1793"),sQuery(id+"F0.wireOp",EDGE,"E1794"),sQuery(id+"F0.wireOp",EDGE,"E1795"),sQuery(id+"F0.wireOp",EDGE,"E1796"),sQuery(id+"F0.wireOp",EDGE,"E1797"),sQuery(id+"F0.wireOp",EDGE,"E1798"),sQuery(id+"F0.wireOp",EDGE,"E1799"),sQuery(id+"F0.wireOp",EDGE,"E1800"),sQuery(id+"F0.wireOp",EDGE,"E1801"),sQuery(id+"F0.wireOp",EDGE,"E1802"),sQuery(id+"F0.wireOp",EDGE,"E1803"),sQuery(id+"F0.wireOp",EDGE,"E1804"),sQuery(id+"F0.wireOp",EDGE,"E1805"),sQuery(id+"F0.wireOp",EDGE,"E1806"),sQuery(id+"F0.wireOp",EDGE,"E1807"),sQuery(id+"F0.wireOp",EDGE,"E1808"),sQuery(id+"F0.wireOp",EDGE,"E1809"),sQuery(id+"F0.wireOp",EDGE,"E1810"),sQuery(id+"F0.wireOp",EDGE,"E1811"),sQuery(id+"F0.wireOp",EDGE,"E1812"),sQuery(id+"F0.wireOp",EDGE,"E1813"),sQuery(id+"F0.wireOp",EDGE,"E1814"),sQuery(id+"F0.wireOp",EDGE,"E1815"),sQuery(id+"F0.wireOp",EDGE,"E1816"),sQuery(id+"F0.wireOp",EDGE,"E1817"),sQuery(id+"F0.wireOp",EDGE,"E1818"),sQuery(id+"F0.wireOp",EDGE,"E1819"),sQuery(id+"F0.wireOp",EDGE,"E1820"),sQuery(id+"F0.wireOp",EDGE,"E1821"),sQuery(id+"F0.wireOp",EDGE,"E1822"),sQuery(id+"F0.wireOp",EDGE,"E1823"),sQuery(id+"F0.wireOp",EDGE,"E1824"),sQuery(id+"F0.wireOp",EDGE,"E1825"),sQuery(id+"F0.wireOp",EDGE,"E1826"),sQuery(id+"F0.wireOp",EDGE,"E1827"),sQuery(id+"F0.wireOp",EDGE,"E1828"),sQuery(id+"F0.wireOp",EDGE,"E1829"),sQuery(id+"F0.wireOp",EDGE,"E1830"),sQuery(id+"F0.wireOp",EDGE,"E1831"),sQuery(id+"F0.wireOp",EDGE,"E1832"),sQuery(id+"F0.wireOp",EDGE,"E1833"),sQuery(id+"F0.wireOp",EDGE,"E1834"),sQuery(id+"F0.wireOp",EDGE,"E1835"),sQuery(id+"F0.wireOp",EDGE,"E1836"),sQuery(id+"F0.wireOp",EDGE,"E1837"),sQuery(id+"F0.wireOp",EDGE,"E1838"),sQuery(id+"F0.wireOp",EDGE,"E1839"),sQuery(id+"F0.wireOp",EDGE,"E1840"),sQuery(id+"F0.wireOp",EDGE,"E1841"),sQuery(id+"F0.wireOp",EDGE,"E1842"),sQuery(id+"F0.wireOp",EDGE,"E1843"),sQuery(id+"F0.wireOp",EDGE,"E1844"),sQuery(id+"F0.wireOp",EDGE,"E1845"),sQuery(id+"F0.wireOp",EDGE,"E1846"),sQuery(id+"F0.wireOp",EDGE,"E1847"),sQuery(id+"F0.wireOp",EDGE,"E1848"),sQuery(id+"F0.wireOp",EDGE,"E1849"),sQuery(id+"F0.wireOp",EDGE,"E1850"),sQuery(id+"F0.wireOp",EDGE,"E1851"),sQuery(id+"F0.wireOp",EDGE,"E1852"),sQuery(id+"F0.wireOp",EDGE,"E1853"),sQuery(id+"F0.wireOp",EDGE,"E1854"),sQuery(id+"F0.wireOp",EDGE,"E1855"),sQuery(id+"F0.wireOp",EDGE,"E1856"),sQuery(id+"F0.wireOp",EDGE,"E1857"),sQuery(id+"F0.wireOp",EDGE,"E1858"),sQuery(id+"F0.wireOp",EDGE,"E1859"),sQuery(id+"F0.wireOp",EDGE,"E1860"),sQuery(id+"F0.wireOp",EDGE,"E1861"),sQuery(id+"F0.wireOp",EDGE,"E1862"),sQuery(id+"F0.wireOp",EDGE,"E1863"),sQuery(id+"F0.wireOp",EDGE,"E1864"),sQuery(id+"F0.wireOp",EDGE,"E1865"),sQuery(id+"F0.wireOp",EDGE,"E1866"),sQuery(id+"F0.wireOp",EDGE,"E1867"),sQuery(id+"F0.wireOp",EDGE,"E1868"),sQuery(id+"F0.wireOp",EDGE,"E1869"),sQuery(id+"F0.wireOp",EDGE,"E1870"),sQuery(id+"F0.wireOp",EDGE,"E1871"),sQuery(id+"F0.wireOp",EDGE,"E1872"),sQuery(id+"F0.wireOp",EDGE,"E1873"),sQuery(id+"F0.wireOp",EDGE,"E1874"),sQuery(id+"F0.wireOp",EDGE,"E1875"),sQuery(id+"F0.wireOp",EDGE,"E1876"),sQuery(id+"F0.wireOp",EDGE,"E1877"),sQuery(id+"F0.wireOp",EDGE,"E1878"),sQuery(id+"F0.wireOp",EDGE,"E1879"),sQuery(id+"F0.wireOp",EDGE,"E1880"),sQuery(id+"F0.wireOp",EDGE,"E1881"),sQuery(id+"F0.wireOp",EDGE,"E1882"),sQuery(id+"F0.wireOp",EDGE,"E1883"),sQuery(id+"F0.wireOp",EDGE,"E1884"),sQuery(id+"F0.wireOp",EDGE,"E1885"),sQuery(id+"F0.wireOp",EDGE,"E1886"),sQuery(id+"F0.wireOp",EDGE,"E1887"),sQuery(id+"F0.wireOp",EDGE,"E1888"),sQuery(id+"F0.wireOp",EDGE,"E1889"),sQuery(id+"F0.wireOp",EDGE,"E1890"),sQuery(id+"F0.wireOp",EDGE,"E1891"),sQuery(id+"F0.wireOp",EDGE,"E1892"),sQuery(id+"F0.wireOp",EDGE,"E1893"),sQuery(id+"F0.wireOp",EDGE,"E1894"),sQuery(id+"F0.wireOp",EDGE,"E1895"),sQuery(id+"F0.wireOp",EDGE,"E1896"),sQuery(id+"F0.wireOp",EDGE,"E1897"),sQuery(id+"F0.wireOp",EDGE,"E1898"),sQuery(id+"F0.wireOp",EDGE,"E1899"),sQuery(id+"F0.wireOp",EDGE,"E1900"),sQuery(id+"F0.wireOp",EDGE,"E1901"),sQuery(id+"F0.wireOp",EDGE,"E1902"),sQuery(id+"F0.wireOp",EDGE,"E1903"),sQuery(id+"F0.wireOp",EDGE,"E1904"),sQuery(id+"F0.wireOp",EDGE,"E1905"),sQuery(id+"F0.wireOp",EDGE,"E1906"),sQuery(id+"F0.wireOp",EDGE,"E1907"),sQuery(id+"F0.wireOp",EDGE,"E1908"),sQuery(id+"F0.wireOp",EDGE,"E1909"),sQuery(id+"F0.wireOp",EDGE,"E1910"),sQuery(id+"F0.wireOp",EDGE,"E1911"),sQuery(id+"F0.wireOp",EDGE,"E1912"),sQuery(id+"F0.wireOp",EDGE,"E1913"),sQuery(id+"F0.wireOp",EDGE,"E1914"),sQuery(id+"F0.wireOp",EDGE,"E1915"),sQuery(id+"F0.wireOp",EDGE,"E1916"),sQuery(id+"F0.wireOp",EDGE,"E1917"),sQuery(id+"F0.wireOp",EDGE,"E1918"),sQuery(id+"F0.wireOp",EDGE,"E1919"),sQuery(id+"F0.wireOp",EDGE,"E1920"),sQuery(id+"F0.wireOp",EDGE,"E1921"),sQuery(id+"F0.wireOp",EDGE,"E1922"),sQuery(id+"F0.wireOp",EDGE,"E1923"),sQuery(id+"F0.wireOp",EDGE,"E1924"),sQuery(id+"F0.wireOp",EDGE,"E1925"),sQuery(id+"F0.wireOp",EDGE,"E1926"),sQuery(id+"F0.wireOp",EDGE,"E1927"),sQuery(id+"F0.wireOp",EDGE,"E1928"),sQuery(id+"F0.wireOp",EDGE,"E1929"),sQuery(id+"F0.wireOp",EDGE,"E1930"),sQuery(id+"F0.wireOp",EDGE,"E1931"),sQuery(id+"F0.wireOp",EDGE,"E1932"),sQuery(id+"F0.wireOp",EDGE,"E1933"),sQuery(id+"F0.wireOp",EDGE,"E1934"),sQuery(id+"F0.wireOp",EDGE,"E1935"),sQuery(id+"F0.wireOp",EDGE,"E1936"),sQuery(id+"F0.wireOp",EDGE,"E1937"),sQuery(id+"F0.wireOp",EDGE,"E1938"),sQuery(id+"F0.wireOp",EDGE,"E1939"),sQuery(id+"F0.wireOp",EDGE,"E1940"),sQuery(id+"F0.wireOp",EDGE,"E1941"),sQuery(id+"F0.wireOp",EDGE,"E1942"),sQuery(id+"F0.wireOp",EDGE,"E1943"),sQuery(id+"F0.wireOp",EDGE,"E1944"),sQuery(id+"F0.wireOp",EDGE,"E1945"),sQuery(id+"F0.wireOp",EDGE,"E1946"),sQuery(id+"F0.wireOp",EDGE,"E1947"),sQuery(id+"F0.wireOp",EDGE,"E1948"),sQuery(id+"F0.wireOp",EDGE,"E1949"),sQuery(id+"F0.wireOp",EDGE,"E1950"),sQuery(id+"F0.wireOp",EDGE,"E1951"),sQuery(id+"F0.wireOp",EDGE,"E1952"),sQuery(id+"F0.wireOp",EDGE,"E1953"),sQuery(id+"F0.wireOp",EDGE,"E1954"),sQuery(id+"F0.wireOp",EDGE,"E1955"),sQuery(id+"F0.wireOp",EDGE,"E1956"),sQuery(id+"F0.wireOp",EDGE,"E1957"),sQuery(id+"F0.wireOp",EDGE,"E1958"),sQuery(id+"F0.wireOp",EDGE,"E1959"),sQuery(id+"F0.wireOp",EDGE,"E1960"),sQuery(id+"F0.wireOp",EDGE,"E1961"),sQuery(id+"F0.wireOp",EDGE,"E1962"),sQuery(id+"F0.wireOp",EDGE,"E1963"),sQuery(id+"F0.wireOp",EDGE,"E1964"),sQuery(id+"F0.wireOp",EDGE,"E1965"),sQuery(id+"F0.wireOp",EDGE,"E1966"),sQuery(id+"F0.wireOp",EDGE,"E1967"),sQuery(id+"F0.wireOp",EDGE,"E1968"),sQuery(id+"F0.wireOp",EDGE,"E1969"),sQuery(id+"F0.wireOp",EDGE,"E1970"),sQuery(id+"F0.wireOp",EDGE,"E1971"),sQuery(id+"F0.wireOp",EDGE,"E1972"),sQuery(id+"F0.wireOp",EDGE,"E1973"),sQuery(id+"F0.wireOp",EDGE,"E1974"),sQuery(id+"F0.wireOp",EDGE,"E1975"),sQuery(id+"F0.wireOp",EDGE,"E1976"),sQuery(id+"F0.wireOp",EDGE,"E1977"),sQuery(id+"F0.wireOp",EDGE,"E1978"),sQuery(id+"F0.wireOp",EDGE,"E1979"),sQuery(id+"F0.wireOp",EDGE,"E1980"),sQuery(id+"F0.wireOp",EDGE,"E1981"),sQuery(id+"F0.wireOp",EDGE,"E1982"),sQuery(id+"F0.wireOp",EDGE,"E1983"),sQuery(id+"F0.wireOp",EDGE,"E1984"),sQuery(id+"F0.wireOp",EDGE,"E1985"),sQuery(id+"F0.wireOp",EDGE,"E1986"),sQuery(id+"F0.wireOp",EDGE,"E1987"),sQuery(id+"F0.wireOp",EDGE,"E1988"),sQuery(id+"F0.wireOp",EDGE,"E1989"),sQuery(id+"F0.wireOp",EDGE,"E1990"),sQuery(id+"F0.wireOp",EDGE,"E1991"),sQuery(id+"F0.wireOp",EDGE,"E1992"),sQuery(id+"F0.wireOp",EDGE,"E1993"),sQuery(id+"F0.wireOp",EDGE,"E1994"),sQuery(id+"F0.wireOp",EDGE,"E1995"),sQuery(id+"F0.wireOp",EDGE,"E1996"),sQuery(id+"F0.wireOp",EDGE,"E1997"),sQuery(id+"F0.wireOp",EDGE,"E1998"),sQuery(id+"F0.wireOp",EDGE,"E1999"),sQuery(id+"F0.wireOp",EDGE,"E2000"),sQuery(id+"F0.wireOp",EDGE,"E2001"),sQuery(id+"F0.wireOp",EDGE,"E2002"),sQuery(id+"F0.wireOp",EDGE,"E2003"),sQuery(id+"F0.wireOp",EDGE,"E2004"),sQuery(id+"F0.wireOp",EDGE,"E2005"),sQuery(id+"F0.wireOp",EDGE,"E2006"),sQuery(id+"F0.wireOp",EDGE,"E2007"),sQuery(id+"F0.wireOp",EDGE,"E2008"),sQuery(id+"F0.wireOp",EDGE,"E2009"),sQuery(id+"F0.wireOp",EDGE,"E2010"),sQuery(id+"F0.wireOp",EDGE,"E2011"),sQuery(id+"F0.wireOp",EDGE,"E2012"),sQuery(id+"F0.wireOp",EDGE,"E2013"),sQuery(id+"F0.wireOp",EDGE,"E2014"),sQuery(id+"F0.wireOp",EDGE,"E2015"),sQuery(id+"F0.wireOp",EDGE,"E2016"),sQuery(id+"F0.wireOp",EDGE,"E2017"),sQuery(id+"F0.wireOp",EDGE,"E2018"),sQuery(id+"F0.wireOp",EDGE,"E2019"),sQuery(id+"F0.wireOp",EDGE,"E2020"),sQuery(id+"F0.wireOp",EDGE,"E2021"),sQuery(id+"F0.wireOp",EDGE,"E2022"),sQuery(id+"F0.wireOp",EDGE,"E2023"),sQuery(id+"F0.wireOp",EDGE,"E2024"),sQuery(id+"F0.wireOp",EDGE,"E2025"),sQuery(id+"F0.wireOp",EDGE,"E2026"),sQuery(id+"F0.wireOp",EDGE,"E2027"),sQuery(id+"F0.wireOp",EDGE,"E2028"),sQuery(id+"F0.wireOp",EDGE,"E2029"),sQuery(id+"F0.wireOp",EDGE,"E2030"),sQuery(id+"F0.wireOp",EDGE,"E2031"),sQuery(id+"F0.wireOp",EDGE,"E2032"),sQuery(id+"F0.wireOp",EDGE,"E2033"),sQuery(id+"F0.wireOp",EDGE,"E2034"),sQuery(id+"F0.wireOp",EDGE,"E2035"),sQuery(id+"F0.wireOp",EDGE,"E2036"),sQuery(id+"F0.wireOp",EDGE,"E2037"),sQuery(id+"F0.wireOp",EDGE,"E2038"),sQuery(id+"F0.wireOp",EDGE,"E2039"),sQuery(id+"F0.wireOp",EDGE,"E2040"),sQuery(id+"F0.wireOp",EDGE,"E2041"),sQuery(id+"F0.wireOp",EDGE,"E2042"),sQuery(id+"F0.wireOp",EDGE,"E2043"),sQuery(id+"F0.wireOp",EDGE,"E2044"),sQuery(id+"F0.wireOp",EDGE,"E2045"),sQuery(id+"F0.wireOp",EDGE,"E2046"),sQuery(id+"F0.wireOp",EDGE,"E2047"),sQuery(id+"F0.wireOp",EDGE,"E2048"),sQuery(id+"F0.wireOp",EDGE,"E2049"),sQuery(id+"F0.wireOp",EDGE,"E2050"),sQuery(id+"F0.wireOp",EDGE,"E2051"),sQuery(id+"F0.wireOp",EDGE,"E2052"),sQuery(id+"F0.wireOp",EDGE,"E2053"),sQuery(id+"F0.wireOp",EDGE,"E2054"),sQuery(id+"F0.wireOp",EDGE,"E2055"),sQuery(id+"F0.wireOp",EDGE,"E2056"),sQuery(id+"F0.wireOp",EDGE,"E2057"),sQuery(id+"F0.wireOp",EDGE,"E2058"),sQuery(id+"F0.wireOp",EDGE,"E2059"),sQuery(id+"F0.wireOp",EDGE,"E2060"),sQuery(id+"F0.wireOp",EDGE,"E2061"),sQuery(id+"F0.wireOp",EDGE,"E2062"),sQuery(id+"F0.wireOp",EDGE,"E2063"),sQuery(id+"F0.wireOp",EDGE,"E2064"),sQuery(id+"F0.wireOp",EDGE,"E2065"),sQuery(id+"F0.wireOp",EDGE,"E2066"),sQuery(id+"F0.wireOp",EDGE,"E2067"),sQuery(id+"F0.wireOp",EDGE,"E2068"),sQuery(id+"F0.wireOp",EDGE,"E2069"),sQuery(id+"F0.wireOp",EDGE,"E2070"),sQuery(id+"F0.wireOp",EDGE,"E2071"),sQuery(id+"F0.wireOp",EDGE,"E2072"),sQuery(id+"F0.wireOp",EDGE,"E2073"),sQuery(id+"F0.wireOp",EDGE,"E2074"),sQuery(id+"F0.wireOp",EDGE,"E2075"),sQuery(id+"F0.wireOp",EDGE,"E2076"),sQuery(id+"F0.wireOp",EDGE,"E2077"),sQuery(id+"F0.wireOp",EDGE,"E2078"),sQuery(id+"F0.wireOp",EDGE,"E2079"),sQuery(id+"F0.wireOp",EDGE,"E2080"),sQuery(id+"F0.wireOp",EDGE,"E2081"),sQuery(id+"F0.wireOp",EDGE,"E2082"),sQuery(id+"F0.wireOp",EDGE,"E2083"),sQuery(id+"F0.wireOp",EDGE,"E2084"),sQuery(id+"F0.wireOp",EDGE,"E2085"),sQuery(id+"F0.wireOp",EDGE,"E2086"),sQuery(id+"F0.wireOp",EDGE,"E2087"),sQuery(id+"F0.wireOp",EDGE,"E2088"),sQuery(id+"F0.wireOp",EDGE,"E2089"),sQuery(id+"F0.wireOp",EDGE,"E2090"),sQuery(id+"F0.wireOp",EDGE,"E2091"),sQuery(id+"F0.wireOp",EDGE,"E2092"),sQuery(id+"F0.wireOp",EDGE,"E2093"),sQuery(id+"F0.wireOp",EDGE,"E2094"),sQuery(id+"F0.wireOp",EDGE,"E2095"),sQuery(id+"F0.wireOp",EDGE,"E2096"),sQuery(id+"F0.wireOp",EDGE,"E2097"),sQuery(id+"F0.wireOp",EDGE,"E2098"),sQuery(id+"F0.wireOp",EDGE,"E2099"),sQuery(id+"F0.wireOp",EDGE,"E2100"),sQuery(id+"F0.wireOp",EDGE,"E2101"),sQuery(id+"F0.wireOp",EDGE,"E2102"),sQuery(id+"F0.wireOp",EDGE,"E2103"),sQuery(id+"F0.wireOp",EDGE,"E2104"),sQuery(id+"F0.wireOp",EDGE,"E2105"),sQuery(id+"F0.wireOp",EDGE,"E2106"),sQuery(id+"F0.wireOp",EDGE,"E2107"),sQuery(id+"F0.wireOp",EDGE,"E2108"),sQuery(id+"F0.wireOp",EDGE,"E2109"),sQuery(id+"F0.wireOp",EDGE,"E2110"),sQuery(id+"F0.wireOp",EDGE,"E2111"),sQuery(id+"F0.wireOp",EDGE,"E2112"),sQuery(id+"F0.wireOp",EDGE,"E2113"),sQuery(id+"F0.wireOp",EDGE,"E2114"),sQuery(id+"F0.wireOp",EDGE,"E2115"),sQuery(id+"F0.wireOp",EDGE,"E2116"),sQuery(id+"F0.wireOp",EDGE,"E2117"),sQuery(id+"F0.wireOp",EDGE,"E2118"),sQuery(id+"F0.wireOp",EDGE,"E2119"),sQuery(id+"F0.wireOp",EDGE,"E2120"),sQuery(id+"F0.wireOp",EDGE,"E2121"),sQuery(id+"F0.wireOp",EDGE,"E2122"),sQuery(id+"F0.wireOp",EDGE,"E2123"),sQuery(id+"F0.wireOp",EDGE,"E2124"),sQuery(id+"F0.wireOp",EDGE,"E2125"),sQuery(id+"F0.wireOp",EDGE,"E2126"),sQuery(id+"F0.wireOp",EDGE,"E2127"),sQuery(id+"F0.wireOp",EDGE,"E2128"),sQuery(id+"F0.wireOp",EDGE,"E2129"),sQuery(id+"F0.wireOp",EDGE,"E2130"),sQuery(id+"F0.wireOp",EDGE,"E2131"),sQuery(id+"F0.wireOp",EDGE,"E2132"),sQuery(id+"F0.wireOp",EDGE,"E2133"),sQuery(id+"F0.wireOp",EDGE,"E2134"),sQuery(id+"F0.wireOp",EDGE,"E2135"),sQuery(id+"F0.wireOp",EDGE,"E2136"),sQuery(id+"F0.wireOp",EDGE,"E2137"),sQuery(id+"F0.wireOp",EDGE,"E2138"),sQuery(id+"F0.wireOp",EDGE,"E2139"),sQuery(id+"F0.wireOp",EDGE,"E2140"),sQuery(id+"F0.wireOp",EDGE,"E2141"),sQuery(id+"F0.wireOp",EDGE,"E2142"),sQuery(id+"F0.wireOp",EDGE,"E2143"),sQuery(id+"F0.wireOp",EDGE,"E2144"),sQuery(id+"F0.wireOp",EDGE,"E2145"),sQuery(id+"F0.wireOp",EDGE,"E2146"),sQuery(id+"F0.wireOp",EDGE,"E2147"),sQuery(id+"F0.wireOp",EDGE,"E2148"),sQuery(id+"F0.wireOp",EDGE,"E2149"),sQuery(id+"F0.wireOp",EDGE,"E2150"),sQuery(id+"F0.wireOp",EDGE,"E2151"),sQuery(id+"F0.wireOp",EDGE,"E2152"),sQuery(id+"F0.wireOp",EDGE,"E2153"),sQuery(id+"F0.wireOp",EDGE,"E2154"),sQuery(id+"F0.wireOp",EDGE,"E2155"),sQuery(id+"F0.wireOp",EDGE,"E2156"),sQuery(id+"F0.wireOp",EDGE,"E2157"),sQuery(id+"F0.wireOp",EDGE,"E2158"),sQuery(id+"F0.wireOp",EDGE,"E2159"),sQuery(id+"F0.wireOp",EDGE,"E2160"),sQuery(id+"F0.wireOp",EDGE,"E2161"),sQuery(id+"F0.wireOp",EDGE,"E2162"),sQuery(id+"F0.wireOp",EDGE,"E2163"),sQuery(id+"F0.wireOp",EDGE,"E2164"),sQuery(id+"F0.wireOp",EDGE,"E2165"),sQuery(id+"F0.wireOp",EDGE,"E2166"),sQuery(id+"F0.wireOp",EDGE,"E2167"),sQuery(id+"F0.wireOp",EDGE,"E2168"),sQuery(id+"F0.wireOp",EDGE,"E2169"),sQuery(id+"F0.wireOp",EDGE,"E2170"),sQuery(id+"F0.wireOp",EDGE,"E2171"),sQuery(id+"F0.wireOp",EDGE,"E2172"),sQuery(id+"F0.wireOp",EDGE,"E2173"),sQuery(id+"F0.wireOp",EDGE,"E2174"),sQuery(id+"F0.wireOp",EDGE,"E2175"),sQuery(id+"F0.wireOp",EDGE,"E2176"),sQuery(id+"F0.wireOp",EDGE,"E2177"),sQuery(id+"F0.wireOp",EDGE,"E2178"),sQuery(id+"F0.wireOp",EDGE,"E2179"),sQuery(id+"F0.wireOp",EDGE,"E2180"),sQuery(id+"F0.wireOp",EDGE,"E2181"),sQuery(id+"F0.wireOp",EDGE,"E2182"),sQuery(id+"F0.wireOp",EDGE,"E2183"),sQuery(id+"F0.wireOp",EDGE,"E2184"),sQuery(id+"F0.wireOp",EDGE,"E2185"),sQuery(id+"F0.wireOp",EDGE,"E2186"),sQuery(id+"F0.wireOp",EDGE,"E2187"),sQuery(id+"F0.wireOp",EDGE,"E2188"),sQuery(id+"F0.wireOp",EDGE,"E2189"),sQuery(id+"F0.wireOp",EDGE,"E2190"),sQuery(id+"F0.wireOp",EDGE,"E2191"),sQuery(id+"F0.wireOp",EDGE,"E2192"),sQuery(id+"F0.wireOp",EDGE,"E2193"),sQuery(id+"F0.wireOp",EDGE,"E2194"),sQuery(id+"F0.wireOp",EDGE,"E2195"),sQuery(id+"F0.wireOp",EDGE,"E2196"),sQuery(id+"F0.wireOp",EDGE,"E2197"),sQuery(id+"F0.wireOp",EDGE,"E2198"),sQuery(id+"F0.wireOp",EDGE,"E2199"),sQuery(id+"F0.wireOp",EDGE,"E2200"),sQuery(id+"F0.wireOp",EDGE,"E2201"),sQuery(id+"F0.wireOp",EDGE,"E2202"),sQuery(id+"F0.wireOp",EDGE,"E2203"),sQuery(id+"F0.wireOp",EDGE,"E2204"),sQuery(id+"F0.wireOp",EDGE,"E2205"),sQuery(id+"F0.wireOp",EDGE,"E2206"),sQuery(id+"F0.wireOp",EDGE,"E2207"),sQuery(id+"F0.wireOp",EDGE,"E2208"),sQuery(id+"F0.wireOp",EDGE,"E2209"),sQuery(id+"F0.wireOp",EDGE,"E2210"),sQuery(id+"F0.wireOp",EDGE,"E2211"),sQuery(id+"F0.wireOp",EDGE,"E2212"),sQuery(id+"F0.wireOp",EDGE,"E2213"),sQuery(id+"F0.wireOp",EDGE,"E2214"),sQuery(id+"F0.wireOp",EDGE,"E2215"),sQuery(id+"F0.wireOp",EDGE,"E2216"),sQuery(id+"F0.wireOp",EDGE,"E2217"),sQuery(id+"F0.wireOp",EDGE,"E2218"),sQuery(id+"F0.wireOp",EDGE,"E2219"),sQuery(id+"F0.wireOp",EDGE,"E2220"),sQuery(id+"F0.wireOp",EDGE,"E2221"),sQuery(id+"F0.wireOp",EDGE,"E2222"),sQuery(id+"F0.wireOp",EDGE,"E2223"),sQuery(id+"F0.wireOp",EDGE,"E2224"),sQuery(id+"F0.wireOp",EDGE,"E2225"),sQuery(id+"F0.wireOp",EDGE,"E2226"),sQuery(id+"F0.wireOp",EDGE,"E2227"),sQuery(id+"F0.wireOp",EDGE,"E2228"),sQuery(id+"F0.wireOp",EDGE,"E2229"),sQuery(id+"F0.wireOp",EDGE,"E2230"),sQuery(id+"F0.wireOp",EDGE,"E2231"),sQuery(id+"F0.wireOp",EDGE,"E2232"),sQuery(id+"F0.wireOp",EDGE,"E2233"),sQuery(id+"F0.wireOp",EDGE,"E2234"),sQuery(id+"F0.wireOp",EDGE,"E2235"),sQuery(id+"F0.wireOp",EDGE,"E2236"),sQuery(id+"F0.wireOp",EDGE,"E2237"),sQuery(id+"F0.wireOp",EDGE,"E2238"),sQuery(id+"F0.wireOp",EDGE,"E2239"),sQuery(id+"F0.wireOp",EDGE,"E2240"),sQuery(id+"F0.wireOp",EDGE,"E2241"),sQuery(id+"F0.wireOp",EDGE,"E2242"),sQuery(id+"F0.wireOp",EDGE,"E2243"),sQuery(id+"F0.wireOp",EDGE,"E2244"),sQuery(id+"F0.wireOp",EDGE,"E2245"),sQuery(id+"F0.wireOp",EDGE,"E2246"),sQuery(id+"F0.wireOp",EDGE,"E2247"),sQuery(id+"F0.wireOp",EDGE,"E2248"),sQuery(id+"F0.wireOp",EDGE,"E2249"),sQuery(id+"F0.wireOp",EDGE,"E2250"),sQuery(id+"F0.wireOp",EDGE,"E2251"),sQuery(id+"F0.wireOp",EDGE,"E2252"),sQuery(id+"F0.wireOp",EDGE,"E2253"),sQuery(id+"F0.wireOp",EDGE,"E2254"),sQuery(id+"F0.wireOp",EDGE,"E2255"),sQuery(id+"F0.wireOp",EDGE,"E2256"),sQuery(id+"F0.wireOp",EDGE,"E2257"),sQuery(id+"F0.wireOp",EDGE,"E2258"),sQuery(id+"F0.wireOp",EDGE,"E2259"),sQuery(id+"F0.wireOp",EDGE,"E2260"),sQuery(id+"F0.wireOp",EDGE,"E2261"),sQuery(id+"F0.wireOp",EDGE,"E2262"),sQuery(id+"F0.wireOp",EDGE,"E2263"),sQuery(id+"F0.wireOp",EDGE,"E2264"),sQuery(id+"F0.wireOp",EDGE,"E2265"),sQuery(id+"F0.wireOp",EDGE,"E2266"),sQuery(id+"F0.wireOp",EDGE,"E2267"),sQuery(id+"F0.wireOp",EDGE,"E2268"),sQuery(id+"F0.wireOp",EDGE,"E2269"),sQuery(id+"F0.wireOp",EDGE,"E2270"),sQuery(id+"F0.wireOp",EDGE,"E2271"),sQuery(id+"F0.wireOp",EDGE,"E2272"),sQuery(id+"F0.wireOp",EDGE,"E2273"),sQuery(id+"F0.wireOp",EDGE,"E2274"),sQuery(id+"F0.wireOp",EDGE,"E2275"),sQuery(id+"F0.wireOp",EDGE,"E2276"),sQuery(id+"F0.wireOp",EDGE,"E2277"),sQuery(id+"F0.wireOp",EDGE,"E2278"),sQuery(id+"F0.wireOp",EDGE,"E2279"),sQuery(id+"F0.wireOp",EDGE,"E2280"),sQuery(id+"F0.wireOp",EDGE,"E2281"),sQuery(id+"F0.wireOp",EDGE,"E2282"),sQuery(id+"F0.wireOp",EDGE,"E2283"),sQuery(id+"F0.wireOp",EDGE,"E2284"),sQuery(id+"F0.wireOp",EDGE,"E2285"),sQuery(id+"F0.wireOp",EDGE,"E2286"),sQuery(id+"F0.wireOp",EDGE,"E2287"),sQuery(id+"F0.wireOp",EDGE,"E2288"),sQuery(id+"F0.wireOp",EDGE,"E2289"),sQuery(id+"F0.wireOp",EDGE,"E2290"),sQuery(id+"F0.wireOp",EDGE,"E2291"),sQuery(id+"F0.wireOp",EDGE,"E2292"),sQuery(id+"F0.wireOp",EDGE,"E2293"),sQuery(id+"F0.wireOp",EDGE,"E2294"),sQuery(id+"F0.wireOp",EDGE,"E2295"),sQuery(id+"F0.wireOp",EDGE,"E2296"),sQuery(id+"F0.wireOp",EDGE,"E2297"),sQuery(id+"F0.wireOp",EDGE,"E2298"),sQuery(id+"F0.wireOp",EDGE,"E2299"),sQuery(id+"F0.wireOp",EDGE,"E2300"),sQuery(id+"F0.wireOp",EDGE,"E2301"),sQuery(id+"F0.wireOp",EDGE,"E2302"),sQuery(id+"F0.wireOp",EDGE,"E2303"),sQuery(id+"F0.wireOp",EDGE,"E2304"),sQuery(id+"F0.wireOp",EDGE,"E2305"),sQuery(id+"F0.wireOp",EDGE,"E2306"),sQuery(id+"F0.wireOp",EDGE,"E2307"),sQuery(id+"F0.wireOp",EDGE,"E2308"),sQuery(id+"F0.wireOp",EDGE,"E2309"),sQuery(id+"F0.wireOp",EDGE,"E2310"),sQuery(id+"F0.wireOp",EDGE,"E2311"),sQuery(id+"F0.wireOp",EDGE,"E2312"),sQuery(id+"F0.wireOp",EDGE,"E2313"),sQuery(id+"F0.wireOp",EDGE,"E2314"),sQuery(id+"F0.wireOp",EDGE,"E2315"),sQuery(id+"F0.wireOp",EDGE,"E2316"),sQuery(id+"F0.wireOp",EDGE,"E2317"),sQuery(id+"F0.wireOp",EDGE,"E2318"),sQuery(id+"F0.wireOp",EDGE,"E2319"),sQuery(id+"F0.wireOp",EDGE,"E2320"),sQuery(id+"F0.wireOp",EDGE,"E2321"),sQuery(id+"F0.wireOp",EDGE,"E2322"),sQuery(id+"F0.wireOp",EDGE,"E2323"),sQuery(id+"F0.wireOp",EDGE,"E2324"),sQuery(id+"F0.wireOp",EDGE,"E2325"),sQuery(id+"F0.wireOp",EDGE,"E2326"),sQuery(id+"F0.wireOp",EDGE,"E2327"),sQuery(id+"F0.wireOp",EDGE,"E2328"),sQuery(id+"F0.wireOp",EDGE,"E2329"),sQuery(id+"F0.wireOp",EDGE,"E2330"),sQuery(id+"F0.wireOp",EDGE,"E2331"),sQuery(id+"F0.wireOp",EDGE,"E2332"),sQuery(id+"F0.wireOp",EDGE,"E2333"),sQuery(id+"F0.wireOp",EDGE,"E2334"),sQuery(id+"F0.wireOp",EDGE,"E2335"),sQuery(id+"F0.wireOp",EDGE,"E2336"),sQuery(id+"F0.wireOp",EDGE,"E2337"),sQuery(id+"F0.wireOp",EDGE,"E2338"),sQuery(id+"F0.wireOp",EDGE,"E2339"),sQuery(id+"F0.wireOp",EDGE,"E2340"),sQuery(id+"F0.wireOp",EDGE,"E2341"),sQuery(id+"F0.wireOp",EDGE,"E2342"),sQuery(id+"F0.wireOp",EDGE,"E2343"),sQuery(id+"F0.wireOp",EDGE,"E2344"),sQuery(id+"F0.wireOp",EDGE,"E2345"),sQuery(id+"F0.wireOp",EDGE,"E2346"),sQuery(id+"F0.wireOp",EDGE,"E2347")])],"isStart":false});
            var sketch = newSketch(context, id + "F2", { "sketchPlane" : qUnion([Q0])});
            skLineSegment(sketch, "E2348", {"start": v(72.23, 61.91) * mm, "end": v(72.23, -16.91) * mm});
            skLineSegment(sketch, "E2349", {"start": v(72.23, -16.91) * mm, "end": v(82.23, -16.91) * mm});
            skLineSegment(sketch, "E2350", {"start": v(82.23, -16.91) * mm, "end": v(82.23, -36.91) * mm});
            skLineSegment(sketch, "E2351", {"start": v(82.23, -36.91) * mm, "end": v(72.23, -36.91) * mm});
            skLineSegment(sketch, "E2352", {"start": v(72.23, -36.91) * mm, "end": v(72.23, -61.91) * mm});
            skLineSegment(sketch, "E2353", {"start": v(-71.52, 61.91) * mm, "end": v(-71.52, 34.55) * mm});
            skLineSegment(sketch, "E2354", {"start": v(-71.52, 34.55) * mm, "end": v(-61.91, 34.55) * mm});
            skLineSegment(sketch, "E2355", {"start": v(-61.91, 34.55) * mm, "end": v(-61.91, 15.19) * mm});
            skLineSegment(sketch, "E2356", {"start": v(-61.91, 15.19) * mm, "end": v(-71.44, 15.19) * mm});
            skLineSegment(sketch, "E2357", {"start": v(-71.44, 15.19) * mm, "end": v(-71.44, -4.06) * mm});
            skLineSegment(sketch, "E2358", {"start": v(-71.44, -4.06) * mm, "end": v(-66.7, -4.06) * mm});
            skLineSegment(sketch, "E2359", {"start": v(-66.7, -4.06) * mm, "end": v(-66.7, -22.86) * mm});
            skLineSegment(sketch, "E2360", {"start": v(-66.7, -22.86) * mm, "end": v(-76, -22.86) * mm});
            skLineSegment(sketch, "E2361", {"start": v(-76, -22.86) * mm, "end": v(-76, -42.68) * mm});
            skLineSegment(sketch, "E2362", {"start": v(-76, -42.68) * mm, "end": v(-27.57, -42.68) * mm});
            skLineSegment(sketch, "E2363", {"start": v(-27.57, -42.68) * mm, "end": v(-21.55, -61.91) * mm});
            skLineSegment(sketch, "E2364", {"start": v(-76, -42.68) * mm, "end": v(-138.72, -42.68) * mm});
            skLineSegment(sketch, "E2365", {"start": v(-138.72, -42.68) * mm, "end": v(-145.35, -61.91) * mm});
            skLineSegment(sketch, "E2366", {"start": v(72.03, 61.91) * mm, "end": v(72.03, -17.11) * mm});
            skLineSegment(sketch, "E2367", {"start": v(72.03, -17.11) * mm, "end": v(82.03, -17.11) * mm});
            skLineSegment(sketch, "E2368", {"start": v(82.03, -17.11) * mm, "end": v(82.03, -36.71) * mm});
            skLineSegment(sketch, "E2369", {"start": v(82.03, -36.71) * mm, "end": v(72.03, -36.71) * mm});
            skLineSegment(sketch, "E2370", {"start": v(72.03, -36.71) * mm, "end": v(72.03, -61.91) * mm});
            skLineSegment(sketch, "E2371", {"start": v(-71.32, 61.91) * mm, "end": v(-71.32, 34.75) * mm});
            skLineSegment(sketch, "E2372", {"start": v(-71.32, 34.75) * mm, "end": v(-61.71, 34.75) * mm});
            skLineSegment(sketch, "E2373", {"start": v(-61.71, 34.75) * mm, "end": v(-61.71, 14.99) * mm});
            skLineSegment(sketch, "E2374", {"start": v(-61.71, 14.99) * mm, "end": v(-71.24, 14.99) * mm});
            skLineSegment(sketch, "E2375", {"start": v(-71.24, 14.99) * mm, "end": v(-71.24, -3.86) * mm});
            skLineSegment(sketch, "E2376", {"start": v(-71.24, -3.86) * mm, "end": v(-66.5, -3.86) * mm});
            skLineSegment(sketch, "E2377", {"start": v(-66.5, -3.86) * mm, "end": v(-66.5, -23.06) * mm});
            skLineSegment(sketch, "E2378", {"start": v(-66.5, -23.06) * mm, "end": v(-75.8, -23.06) * mm});
            skLineSegment(sketch, "E2379", {"start": v(-75.8, -23.06) * mm, "end": v(-75.8, -42.48) * mm});
            skLineSegment(sketch, "E2380", {"start": v(-75.8, -42.48) * mm, "end": v(-27.42, -42.48) * mm});
            skLineSegment(sketch, "E2381", {"start": v(-27.42, -42.48) * mm, "end": v(-21.34, -61.91) * mm});
            skLineSegment(sketch, "E2382", {"start": v(-76, -42.48) * mm, "end": v(-138.87, -42.48) * mm});
            skLineSegment(sketch, "E2383", {"start": v(-138.87, -42.48) * mm, "end": v(-145.56, -61.91) * mm});
            skSolve(sketch);
        }
        {
            var Q0;
            {var subQ2=sQuery(id+"F2.wireOp",EDGE,"E2348");Q0=makeQuery(id+"F2.imprint","IMPRINT",FACE,{"disambiguationData":[TD([[makeQuery(id+"F2.imprint","IMPRINT",EDGE,{"derivedFrom":subQ2}),-1.0]])]});}
            var Q1;
            {var subQ8=sQuery(id+"F2.wireOp",EDGE,"E2353");Q1=makeQuery(id+"F2.imprint","IMPRINT",FACE,{"disambiguationData":[TD([[makeQuery(id+"F2.imprint","IMPRINT",EDGE,{"derivedFrom":subQ8}),1.0]])]});}
            var Q2;
            {var subQ1=sQuery(id+"F2.wireOp",EDGE,"E2364");Q2=makeQuery(id+"F2.imprint","IMPRINT",FACE,{"disambiguationData":[TD([[makeQuery(id+"F2.imprint","IMPRINT",EDGE,{"derivedFrom":subQ1}),-1.0]])]});}
            extrude(context, id + "F3", {"entities" : qUnion([Q0, Q1, Q2]), "operationType" : NewBodyOperationType.REMOVE, "oppositeDirection" : true, "depth" : 25 * mm});
        }
    });
